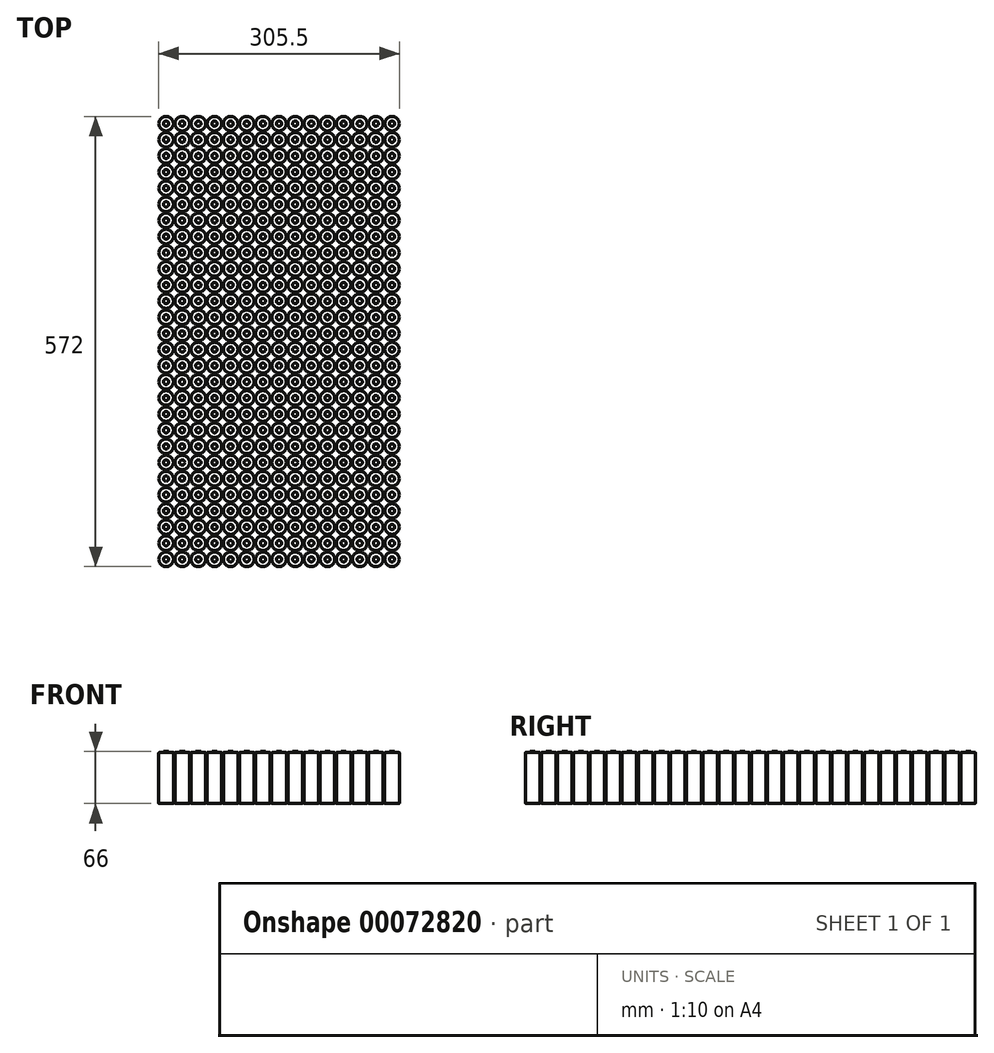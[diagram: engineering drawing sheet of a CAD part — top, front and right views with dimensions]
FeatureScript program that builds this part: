
annotation { "Feature Type Name" : "Feature", "Feature Type Description" : "" }
export const myFeature = defineFeature(function(context is Context, id is Id, definition is map)
    precondition{}
    {
        {
            var Q0;
            Q0=qCreatedBy(makeId("Top.planeOp"),FACE);
            var sketch = newSketch(context, id + "F0", { "sketchPlane" : qUnion([Q0])});
            skCircle(sketch, "E0", {"center": v(0, 0) * mm, "radius": 9.25 * mm});
            skSolve(sketch);
        }
        {
            var Q0;
            Q0 = qSketchRegion(id + "F0", true);
            extrude(context, id + "F1", {"entities" : qUnion([Q0]), "endBound" : BoundingType.SYMMETRIC, "depth" : 65 * mm});
        }
        {
            var Q0;
            Q0=makeQuery(id+"F1.opExtrude","CAP_FACE",FACE,{"disambiguationData":[OSD([sQuery(id+"F0.wireOp",EDGE,"E0")])],"isStart":false});
            var sketch = newSketch(context, id + "F2", { "sketchPlane" : qUnion([Q0])});
            skCircle(sketch, "E1", {"center": v(0, 0) * mm, "radius": 3.3 * mm});
            skSolve(sketch);
        }
        {
            var Q0;
            Q0 = qSketchRegion(id + "F2", true);
            extrude(context, id + "F3", {"entities" : qUnion([Q0]), "operationType" : NewBodyOperationType.ADD, "depth" : 1 * mm});
        }
        {
            var Q0;
            Q0=makeQuery(id+"F1.opExtrude","SWEPT_BODY",BODY,{"disambiguationData":[OSD([sQuery(id+"F0.wireOp",EDGE,"E0")])]});
            var Q1;
            Q1=qCreatedBy(makeId("Right.planeOp"),FACE);
            transform(context, id + "F4", {"entities" : qUnion([Q0]), "transformType" : TransformType.TRANSLATION_DISTANCE, "transformDirection" : qUnion([Q1]), "distance" : 20.5 * mm, "makeCopy" : true});
        }
        {
            var Q0;
            Q0=makeQuery(id+"F1.opExtrude","CAP_EDGE",EDGE,{"disambiguationData":[OSD([sQuery(id+"F0.wireOp",EDGE,"E0")])],"isStart":false});
            fillet(context, id + "F5", {"entities" : qUnion([Q0]), "radius" : 0.64 * mm, "tangentPropagation" : true, "allowEdgeOverflow" : false});
        }
        {
            var Q0;
            Q0=makeQuery(id+"F4.opPattern","COPY",EDGE,{"derivedFrom":makeQuery(id+"F1.opExtrude","CAP_EDGE",EDGE,{"disambiguationData":[OSD([sQuery(id+"F0.wireOp",EDGE,"E0")])],"isStart":false}),"instanceName":"1"});
            fillet(context, id + "F6", {"entities" : qUnion([Q0]), "radius" : 0.64 * mm, "tangentPropagation" : true, "allowEdgeOverflow" : false});
        }
        {
            var Q0;
            Q0=makeQuery(id+"F1.opExtrude","CAP_EDGE",EDGE,{"disambiguationData":[OSD([sQuery(id+"F0.wireOp",EDGE,"E0")])],"isStart":true});
            var Q1;
            Q1=makeQuery(id+"F1.opExtrude","SWEPT_FACE",FACE,{"disambiguationData":[OSD([sQuery(id+"F0.wireOp",EDGE,"E0")])]});
            fillet(context, id + "F7", {"entities" : qUnion([Q0, Q1]), "radius" : 0.64 * mm, "tangentPropagation" : true, "allowEdgeOverflow" : false});
        }
        {
            var Q0;
            Q0=makeQuery(id+"F4.opPattern","COPY",EDGE,{"derivedFrom":makeQuery(id+"F1.opExtrude","CAP_EDGE",EDGE,{"disambiguationData":[OSD([sQuery(id+"F0.wireOp",EDGE,"E0")])],"isStart":true}),"instanceName":"1"});
            fillet(context, id + "F8", {"entities" : qUnion([Q0]), "radius" : 0.64 * mm, "tangentPropagation" : true, "allowEdgeOverflow" : false});
        }
        {
            var Q0;
            Q0=makeQuery(id+"F1.opExtrude","SWEPT_BODY",BODY,{"disambiguationData":[OSD([sQuery(id+"F0.wireOp",EDGE,"E0")])]});
            var Q1;
            Q1=makeQuery(id+"F4.opPattern","COPY",BODY,{"derivedFrom":makeQuery(id+"F1.opExtrude","SWEPT_BODY",BODY,{"disambiguationData":[OSD([sQuery(id+"F0.wireOp",EDGE,"E0")])]}),"instanceName":"1"});
            var Q2;
            Q2=qCreatedBy(makeId("Right.planeOp"),FACE);
            transform(context, id + "F9", {"entities" : qUnion([Q0, Q1]), "transformType" : TransformType.TRANSLATION_DISTANCE, "transformDirection" : qUnion([Q2]), "distance" : 41 * mm, "oppositeDirection" : true, "makeCopy" : true});
        }
        {
            var Q0;
            Q0=makeQuery(id+"F1.opExtrude","SWEPT_BODY",BODY,{"disambiguationData":[OSD([sQuery(id+"F0.wireOp",EDGE,"E0")])]});
            var Q1;
            Q1=qCreatedBy(makeId("Right.planeOp"),FACE);
            transform(context, id + "F10", {"entities" : qUnion([Q0]), "transformType" : TransformType.TRANSLATION_DISTANCE, "transformDirection" : qUnion([Q1]), "distance" : 41 * mm, "makeCopy" : true});
        }
        {
            var Q0;
            Q0=makeQuery(id+"F4.opPattern","COPY",BODY,{"derivedFrom":makeQuery(id+"F1.opExtrude","SWEPT_BODY",BODY,{"disambiguationData":[OSD([sQuery(id+"F0.wireOp",EDGE,"E0")])]}),"instanceName":"1"});
            var Q1;
            Q1=makeQuery(id+"F1.opExtrude","SWEPT_BODY",BODY,{"disambiguationData":[OSD([sQuery(id+"F0.wireOp",EDGE,"E0")])]});
            var Q2;
            Q2=makeQuery(id+"F9.opPattern","COPY",BODY,{"derivedFrom":makeQuery(id+"F1.opExtrude","SWEPT_BODY",BODY,{"disambiguationData":[OSD([sQuery(id+"F0.wireOp",EDGE,"E0")])]}),"instanceName":"1"});
            var Q3;
            Q3=makeQuery(id+"F10.opPattern","COPY",BODY,{"derivedFrom":makeQuery(id+"F1.opExtrude","SWEPT_BODY",BODY,{"disambiguationData":[OSD([sQuery(id+"F0.wireOp",EDGE,"E0")])]}),"instanceName":"1"});
            var Q4;
            Q4=makeQuery(id+"F9.opPattern","COPY",BODY,{"derivedFrom":makeQuery(id+"F4.opPattern","COPY",BODY,{"derivedFrom":makeQuery(id+"F1.opExtrude","SWEPT_BODY",BODY,{"disambiguationData":[OSD([sQuery(id+"F0.wireOp",EDGE,"E0")])]}),"instanceName":"1"}),"instanceName":"1"});
            var Q5;
            Q5=qCreatedBy(makeId("Right.planeOp"),FACE);
            transform(context, id + "F11", {"entities" : qUnion([Q0, Q1, Q2, Q3, Q4]), "transformType" : TransformType.TRANSLATION_DISTANCE, "transformDirection" : qUnion([Q5]), "distance" : 102.5 * mm, "makeCopy" : true});
        }
        {
            var Q0;
            Q0=makeQuery(id+"F1.opExtrude","SWEPT_BODY",BODY,{"disambiguationData":[OSD([sQuery(id+"F0.wireOp",EDGE,"E0")])]});
            var Q1;
            Q1=makeQuery(id+"F4.opPattern","COPY",BODY,{"derivedFrom":makeQuery(id+"F1.opExtrude","SWEPT_BODY",BODY,{"disambiguationData":[OSD([sQuery(id+"F0.wireOp",EDGE,"E0")])]}),"instanceName":"1"});
            var Q2;
            Q2=makeQuery(id+"F9.opPattern","COPY",BODY,{"derivedFrom":makeQuery(id+"F1.opExtrude","SWEPT_BODY",BODY,{"disambiguationData":[OSD([sQuery(id+"F0.wireOp",EDGE,"E0")])]}),"instanceName":"1"});
            var Q3;
            Q3=makeQuery(id+"F10.opPattern","COPY",BODY,{"derivedFrom":makeQuery(id+"F1.opExtrude","SWEPT_BODY",BODY,{"disambiguationData":[OSD([sQuery(id+"F0.wireOp",EDGE,"E0")])]}),"instanceName":"1"});
            var Q4;
            Q4=makeQuery(id+"F11.opPattern","COPY",BODY,{"derivedFrom":makeQuery(id+"F9.opPattern","COPY",BODY,{"derivedFrom":makeQuery(id+"F1.opExtrude","SWEPT_BODY",BODY,{"disambiguationData":[OSD([sQuery(id+"F0.wireOp",EDGE,"E0")])]}),"instanceName":"1"}),"instanceName":"1"});
            var Q5;
            Q5=makeQuery(id+"F11.opPattern","COPY",BODY,{"derivedFrom":makeQuery(id+"F10.opPattern","COPY",BODY,{"derivedFrom":makeQuery(id+"F1.opExtrude","SWEPT_BODY",BODY,{"disambiguationData":[OSD([sQuery(id+"F0.wireOp",EDGE,"E0")])]}),"instanceName":"1"}),"instanceName":"1"});
            var Q6;
            Q6=makeQuery(id+"F11.opPattern","COPY",BODY,{"derivedFrom":makeQuery(id+"F9.opPattern","COPY",BODY,{"derivedFrom":makeQuery(id+"F4.opPattern","COPY",BODY,{"derivedFrom":makeQuery(id+"F1.opExtrude","SWEPT_BODY",BODY,{"disambiguationData":[OSD([sQuery(id+"F0.wireOp",EDGE,"E0")])]}),"instanceName":"1"}),"instanceName":"1"}),"instanceName":"1"});
            var Q7;
            Q7=makeQuery(id+"F11.opPattern","COPY",BODY,{"derivedFrom":makeQuery(id+"F4.opPattern","COPY",BODY,{"derivedFrom":makeQuery(id+"F1.opExtrude","SWEPT_BODY",BODY,{"disambiguationData":[OSD([sQuery(id+"F0.wireOp",EDGE,"E0")])]}),"instanceName":"1"}),"instanceName":"1"});
            var Q8;
            Q8=makeQuery(id+"F11.opPattern","COPY",BODY,{"derivedFrom":makeQuery(id+"F1.opExtrude","SWEPT_BODY",BODY,{"disambiguationData":[OSD([sQuery(id+"F0.wireOp",EDGE,"E0")])]}),"instanceName":"1"});
            var Q9;
            Q9=makeQuery(id+"F9.opPattern","COPY",BODY,{"derivedFrom":makeQuery(id+"F4.opPattern","COPY",BODY,{"derivedFrom":makeQuery(id+"F1.opExtrude","SWEPT_BODY",BODY,{"disambiguationData":[OSD([sQuery(id+"F0.wireOp",EDGE,"E0")])]}),"instanceName":"1"}),"instanceName":"1"});
            var Q10;
            Q10=qCreatedBy(makeId("Right.planeOp"),FACE);
            transform(context, id + "F12", {"entities" : qUnion([Q0, Q1, Q2, Q3, Q4, Q5, Q6, Q7, Q8, Q9]), "transformType" : TransformType.TRANSLATION_DISTANCE, "transformDirection" : qUnion([Q10]), "distance" : 205 * mm, "oppositeDirection" : true, "makeCopy" : true});
        }
        {
            var Q0;
            Q0=makeQuery(id+"F1.opExtrude","SWEPT_BODY",BODY,{"disambiguationData":[OSD([sQuery(id+"F0.wireOp",EDGE,"E0")])]});
            var Q1;
            Q1=makeQuery(id+"F4.opPattern","COPY",BODY,{"derivedFrom":makeQuery(id+"F1.opExtrude","SWEPT_BODY",BODY,{"disambiguationData":[OSD([sQuery(id+"F0.wireOp",EDGE,"E0")])]}),"instanceName":"1"});
            var Q2;
            Q2=makeQuery(id+"F9.opPattern","COPY",BODY,{"derivedFrom":makeQuery(id+"F4.opPattern","COPY",BODY,{"derivedFrom":makeQuery(id+"F1.opExtrude","SWEPT_BODY",BODY,{"disambiguationData":[OSD([sQuery(id+"F0.wireOp",EDGE,"E0")])]}),"instanceName":"1"}),"instanceName":"1"});
            var Q3;
            Q3=makeQuery(id+"F9.opPattern","COPY",BODY,{"derivedFrom":makeQuery(id+"F1.opExtrude","SWEPT_BODY",BODY,{"disambiguationData":[OSD([sQuery(id+"F0.wireOp",EDGE,"E0")])]}),"instanceName":"1"});
            var Q4;
            Q4=makeQuery(id+"F10.opPattern","COPY",BODY,{"derivedFrom":makeQuery(id+"F1.opExtrude","SWEPT_BODY",BODY,{"disambiguationData":[OSD([sQuery(id+"F0.wireOp",EDGE,"E0")])]}),"instanceName":"1"});
            var Q5;
            Q5=makeQuery(id+"F11.opPattern","COPY",BODY,{"derivedFrom":makeQuery(id+"F9.opPattern","COPY",BODY,{"derivedFrom":makeQuery(id+"F1.opExtrude","SWEPT_BODY",BODY,{"disambiguationData":[OSD([sQuery(id+"F0.wireOp",EDGE,"E0")])]}),"instanceName":"1"}),"instanceName":"1"});
            var Q6;
            Q6=makeQuery(id+"F11.opPattern","COPY",BODY,{"derivedFrom":makeQuery(id+"F10.opPattern","COPY",BODY,{"derivedFrom":makeQuery(id+"F1.opExtrude","SWEPT_BODY",BODY,{"disambiguationData":[OSD([sQuery(id+"F0.wireOp",EDGE,"E0")])]}),"instanceName":"1"}),"instanceName":"1"});
            var Q7;
            Q7=makeQuery(id+"F11.opPattern","COPY",BODY,{"derivedFrom":makeQuery(id+"F9.opPattern","COPY",BODY,{"derivedFrom":makeQuery(id+"F4.opPattern","COPY",BODY,{"derivedFrom":makeQuery(id+"F1.opExtrude","SWEPT_BODY",BODY,{"disambiguationData":[OSD([sQuery(id+"F0.wireOp",EDGE,"E0")])]}),"instanceName":"1"}),"instanceName":"1"}),"instanceName":"1"});
            var Q8;
            Q8=makeQuery(id+"F11.opPattern","COPY",BODY,{"derivedFrom":makeQuery(id+"F4.opPattern","COPY",BODY,{"derivedFrom":makeQuery(id+"F1.opExtrude","SWEPT_BODY",BODY,{"disambiguationData":[OSD([sQuery(id+"F0.wireOp",EDGE,"E0")])]}),"instanceName":"1"}),"instanceName":"1"});
            var Q9;
            Q9=makeQuery(id+"F11.opPattern","COPY",BODY,{"derivedFrom":makeQuery(id+"F1.opExtrude","SWEPT_BODY",BODY,{"disambiguationData":[OSD([sQuery(id+"F0.wireOp",EDGE,"E0")])]}),"instanceName":"1"});
            var Q10;
            Q10=makeQuery(id+"F12.opPattern","COPY",BODY,{"derivedFrom":makeQuery(id+"F11.opPattern","COPY",BODY,{"derivedFrom":makeQuery(id+"F4.opPattern","COPY",BODY,{"derivedFrom":makeQuery(id+"F1.opExtrude","SWEPT_BODY",BODY,{"disambiguationData":[OSD([sQuery(id+"F0.wireOp",EDGE,"E0")])]}),"instanceName":"1"}),"instanceName":"1"}),"instanceName":"1"});
            var Q11;
            Q11=makeQuery(id+"F12.opPattern","COPY",BODY,{"derivedFrom":makeQuery(id+"F11.opPattern","COPY",BODY,{"derivedFrom":makeQuery(id+"F1.opExtrude","SWEPT_BODY",BODY,{"disambiguationData":[OSD([sQuery(id+"F0.wireOp",EDGE,"E0")])]}),"instanceName":"1"}),"instanceName":"1"});
            var Q12;
            Q12=makeQuery(id+"F12.opPattern","COPY",BODY,{"derivedFrom":makeQuery(id+"F11.opPattern","COPY",BODY,{"derivedFrom":makeQuery(id+"F9.opPattern","COPY",BODY,{"derivedFrom":makeQuery(id+"F4.opPattern","COPY",BODY,{"derivedFrom":makeQuery(id+"F1.opExtrude","SWEPT_BODY",BODY,{"disambiguationData":[OSD([sQuery(id+"F0.wireOp",EDGE,"E0")])]}),"instanceName":"1"}),"instanceName":"1"}),"instanceName":"1"}),"instanceName":"1"});
            var Q13;
            Q13=makeQuery(id+"F12.opPattern","COPY",BODY,{"derivedFrom":makeQuery(id+"F10.opPattern","COPY",BODY,{"derivedFrom":makeQuery(id+"F1.opExtrude","SWEPT_BODY",BODY,{"disambiguationData":[OSD([sQuery(id+"F0.wireOp",EDGE,"E0")])]}),"instanceName":"1"}),"instanceName":"1"});
            var Q14;
            Q14=makeQuery(id+"F12.opPattern","COPY",BODY,{"derivedFrom":makeQuery(id+"F9.opPattern","COPY",BODY,{"derivedFrom":makeQuery(id+"F4.opPattern","COPY",BODY,{"derivedFrom":makeQuery(id+"F1.opExtrude","SWEPT_BODY",BODY,{"disambiguationData":[OSD([sQuery(id+"F0.wireOp",EDGE,"E0")])]}),"instanceName":"1"}),"instanceName":"1"}),"instanceName":"1"});
            var Q15;
            Q15=makeQuery(id+"F12.opPattern","COPY",BODY,{"derivedFrom":makeQuery(id+"F11.opPattern","COPY",BODY,{"derivedFrom":makeQuery(id+"F10.opPattern","COPY",BODY,{"derivedFrom":makeQuery(id+"F1.opExtrude","SWEPT_BODY",BODY,{"disambiguationData":[OSD([sQuery(id+"F0.wireOp",EDGE,"E0")])]}),"instanceName":"1"}),"instanceName":"1"}),"instanceName":"1"});
            var Q16;
            Q16=makeQuery(id+"F12.opPattern","COPY",BODY,{"derivedFrom":makeQuery(id+"F11.opPattern","COPY",BODY,{"derivedFrom":makeQuery(id+"F9.opPattern","COPY",BODY,{"derivedFrom":makeQuery(id+"F1.opExtrude","SWEPT_BODY",BODY,{"disambiguationData":[OSD([sQuery(id+"F0.wireOp",EDGE,"E0")])]}),"instanceName":"1"}),"instanceName":"1"}),"instanceName":"1"});
            var Q17;
            Q17=makeQuery(id+"F12.opPattern","COPY",BODY,{"derivedFrom":makeQuery(id+"F9.opPattern","COPY",BODY,{"derivedFrom":makeQuery(id+"F1.opExtrude","SWEPT_BODY",BODY,{"disambiguationData":[OSD([sQuery(id+"F0.wireOp",EDGE,"E0")])]}),"instanceName":"1"}),"instanceName":"1"});
            var Q18;
            Q18=makeQuery(id+"F12.opPattern","COPY",BODY,{"derivedFrom":makeQuery(id+"F4.opPattern","COPY",BODY,{"derivedFrom":makeQuery(id+"F1.opExtrude","SWEPT_BODY",BODY,{"disambiguationData":[OSD([sQuery(id+"F0.wireOp",EDGE,"E0")])]}),"instanceName":"1"}),"instanceName":"1"});
            var Q19;
            Q19=makeQuery(id+"F12.opPattern","COPY",BODY,{"derivedFrom":makeQuery(id+"F1.opExtrude","SWEPT_BODY",BODY,{"disambiguationData":[OSD([sQuery(id+"F0.wireOp",EDGE,"E0")])]}),"instanceName":"1"});
            var Q20;
            Q20=qCreatedBy(makeId("Right.planeOp"),FACE);
            transform(context, id + "F13", {"entities" : qUnion([Q0, Q1, Q2, Q3, Q4, Q5, Q6, Q7, Q8, Q9, Q10, Q11, Q12, Q13, Q14, Q15, Q16, Q17, Q18, Q19]), "transformType" : TransformType.TRANSLATION_DISTANCE, "transformDirection" : qUnion([Q20]), "distance" : 30.75 * mm, "oppositeDirection" : true, "makeCopy" : false});
        }
        {
            var Q0;
            Q0=makeQuery(id+"F4.opPattern","COPY",BODY,{"derivedFrom":makeQuery(id+"F1.opExtrude","SWEPT_BODY",BODY,{"disambiguationData":[OSD([sQuery(id+"F0.wireOp",EDGE,"E0")])]}),"instanceName":"1"});
            var Q1;
            Q1=makeQuery(id+"F10.opPattern","COPY",BODY,{"derivedFrom":makeQuery(id+"F1.opExtrude","SWEPT_BODY",BODY,{"disambiguationData":[OSD([sQuery(id+"F0.wireOp",EDGE,"E0")])]}),"instanceName":"1"});
            var Q2;
            Q2=makeQuery(id+"F11.opPattern","COPY",BODY,{"derivedFrom":makeQuery(id+"F9.opPattern","COPY",BODY,{"derivedFrom":makeQuery(id+"F1.opExtrude","SWEPT_BODY",BODY,{"disambiguationData":[OSD([sQuery(id+"F0.wireOp",EDGE,"E0")])]}),"instanceName":"1"}),"instanceName":"1"});
            var Q3;
            Q3=makeQuery(id+"F11.opPattern","COPY",BODY,{"derivedFrom":makeQuery(id+"F10.opPattern","COPY",BODY,{"derivedFrom":makeQuery(id+"F1.opExtrude","SWEPT_BODY",BODY,{"disambiguationData":[OSD([sQuery(id+"F0.wireOp",EDGE,"E0")])]}),"instanceName":"1"}),"instanceName":"1"});
            var Q4;
            Q4=makeQuery(id+"F11.opPattern","COPY",BODY,{"derivedFrom":makeQuery(id+"F9.opPattern","COPY",BODY,{"derivedFrom":makeQuery(id+"F4.opPattern","COPY",BODY,{"derivedFrom":makeQuery(id+"F1.opExtrude","SWEPT_BODY",BODY,{"disambiguationData":[OSD([sQuery(id+"F0.wireOp",EDGE,"E0")])]}),"instanceName":"1"}),"instanceName":"1"}),"instanceName":"1"});
            var Q5;
            Q5=makeQuery(id+"F11.opPattern","COPY",BODY,{"derivedFrom":makeQuery(id+"F4.opPattern","COPY",BODY,{"derivedFrom":makeQuery(id+"F1.opExtrude","SWEPT_BODY",BODY,{"disambiguationData":[OSD([sQuery(id+"F0.wireOp",EDGE,"E0")])]}),"instanceName":"1"}),"instanceName":"1"});
            var Q6;
            Q6=makeQuery(id+"F11.opPattern","COPY",BODY,{"derivedFrom":makeQuery(id+"F1.opExtrude","SWEPT_BODY",BODY,{"disambiguationData":[OSD([sQuery(id+"F0.wireOp",EDGE,"E0")])]}),"instanceName":"1"});
            var Q7;
            Q7=makeQuery(id+"F1.opExtrude","SWEPT_BODY",BODY,{"disambiguationData":[OSD([sQuery(id+"F0.wireOp",EDGE,"E0")])]});
            var Q8;
            Q8=qCreatedBy(makeId("Right.planeOp"),FACE);
            transform(context, id + "F14", {"entities" : qUnion([Q0, Q1, Q2, Q3, Q4, Q5, Q6, Q7]), "transformType" : TransformType.TRANSLATION_DISTANCE, "transformDirection" : qUnion([Q8]), "distance" : 164 * mm, "makeCopy" : true});
        }
        {
            var Q0;
            Q0=makeQuery(id+"F4.opPattern","COPY",BODY,{"derivedFrom":makeQuery(id+"F1.opExtrude","SWEPT_BODY",BODY,{"disambiguationData":[OSD([sQuery(id+"F0.wireOp",EDGE,"E0")])]}),"instanceName":"1"});
            var Q1;
            Q1=makeQuery(id+"F9.opPattern","COPY",BODY,{"derivedFrom":makeQuery(id+"F4.opPattern","COPY",BODY,{"derivedFrom":makeQuery(id+"F1.opExtrude","SWEPT_BODY",BODY,{"disambiguationData":[OSD([sQuery(id+"F0.wireOp",EDGE,"E0")])]}),"instanceName":"1"}),"instanceName":"1"});
            var Q2;
            Q2=makeQuery(id+"F9.opPattern","COPY",BODY,{"derivedFrom":makeQuery(id+"F1.opExtrude","SWEPT_BODY",BODY,{"disambiguationData":[OSD([sQuery(id+"F0.wireOp",EDGE,"E0")])]}),"instanceName":"1"});
            var Q3;
            Q3=makeQuery(id+"F10.opPattern","COPY",BODY,{"derivedFrom":makeQuery(id+"F1.opExtrude","SWEPT_BODY",BODY,{"disambiguationData":[OSD([sQuery(id+"F0.wireOp",EDGE,"E0")])]}),"instanceName":"1"});
            var Q4;
            Q4=makeQuery(id+"F11.opPattern","COPY",BODY,{"derivedFrom":makeQuery(id+"F9.opPattern","COPY",BODY,{"derivedFrom":makeQuery(id+"F1.opExtrude","SWEPT_BODY",BODY,{"disambiguationData":[OSD([sQuery(id+"F0.wireOp",EDGE,"E0")])]}),"instanceName":"1"}),"instanceName":"1"});
            var Q5;
            Q5=makeQuery(id+"F11.opPattern","COPY",BODY,{"derivedFrom":makeQuery(id+"F10.opPattern","COPY",BODY,{"derivedFrom":makeQuery(id+"F1.opExtrude","SWEPT_BODY",BODY,{"disambiguationData":[OSD([sQuery(id+"F0.wireOp",EDGE,"E0")])]}),"instanceName":"1"}),"instanceName":"1"});
            var Q6;
            Q6=makeQuery(id+"F11.opPattern","COPY",BODY,{"derivedFrom":makeQuery(id+"F9.opPattern","COPY",BODY,{"derivedFrom":makeQuery(id+"F4.opPattern","COPY",BODY,{"derivedFrom":makeQuery(id+"F1.opExtrude","SWEPT_BODY",BODY,{"disambiguationData":[OSD([sQuery(id+"F0.wireOp",EDGE,"E0")])]}),"instanceName":"1"}),"instanceName":"1"}),"instanceName":"1"});
            var Q7;
            Q7=makeQuery(id+"F11.opPattern","COPY",BODY,{"derivedFrom":makeQuery(id+"F4.opPattern","COPY",BODY,{"derivedFrom":makeQuery(id+"F1.opExtrude","SWEPT_BODY",BODY,{"disambiguationData":[OSD([sQuery(id+"F0.wireOp",EDGE,"E0")])]}),"instanceName":"1"}),"instanceName":"1"});
            var Q8;
            Q8=makeQuery(id+"F11.opPattern","COPY",BODY,{"derivedFrom":makeQuery(id+"F1.opExtrude","SWEPT_BODY",BODY,{"disambiguationData":[OSD([sQuery(id+"F0.wireOp",EDGE,"E0")])]}),"instanceName":"1"});
            var Q9;
            Q9=makeQuery(id+"F12.opPattern","COPY",BODY,{"derivedFrom":makeQuery(id+"F11.opPattern","COPY",BODY,{"derivedFrom":makeQuery(id+"F1.opExtrude","SWEPT_BODY",BODY,{"disambiguationData":[OSD([sQuery(id+"F0.wireOp",EDGE,"E0")])]}),"instanceName":"1"}),"instanceName":"1"});
            var Q10;
            Q10=makeQuery(id+"F12.opPattern","COPY",BODY,{"derivedFrom":makeQuery(id+"F11.opPattern","COPY",BODY,{"derivedFrom":makeQuery(id+"F9.opPattern","COPY",BODY,{"derivedFrom":makeQuery(id+"F4.opPattern","COPY",BODY,{"derivedFrom":makeQuery(id+"F1.opExtrude","SWEPT_BODY",BODY,{"disambiguationData":[OSD([sQuery(id+"F0.wireOp",EDGE,"E0")])]}),"instanceName":"1"}),"instanceName":"1"}),"instanceName":"1"}),"instanceName":"1"});
            var Q11;
            Q11=makeQuery(id+"F12.opPattern","COPY",BODY,{"derivedFrom":makeQuery(id+"F10.opPattern","COPY",BODY,{"derivedFrom":makeQuery(id+"F1.opExtrude","SWEPT_BODY",BODY,{"disambiguationData":[OSD([sQuery(id+"F0.wireOp",EDGE,"E0")])]}),"instanceName":"1"}),"instanceName":"1"});
            var Q12;
            Q12=makeQuery(id+"F12.opPattern","COPY",BODY,{"derivedFrom":makeQuery(id+"F9.opPattern","COPY",BODY,{"derivedFrom":makeQuery(id+"F4.opPattern","COPY",BODY,{"derivedFrom":makeQuery(id+"F1.opExtrude","SWEPT_BODY",BODY,{"disambiguationData":[OSD([sQuery(id+"F0.wireOp",EDGE,"E0")])]}),"instanceName":"1"}),"instanceName":"1"}),"instanceName":"1"});
            var Q13;
            Q13=makeQuery(id+"F12.opPattern","COPY",BODY,{"derivedFrom":makeQuery(id+"F11.opPattern","COPY",BODY,{"derivedFrom":makeQuery(id+"F4.opPattern","COPY",BODY,{"derivedFrom":makeQuery(id+"F1.opExtrude","SWEPT_BODY",BODY,{"disambiguationData":[OSD([sQuery(id+"F0.wireOp",EDGE,"E0")])]}),"instanceName":"1"}),"instanceName":"1"}),"instanceName":"1"});
            var Q14;
            Q14=makeQuery(id+"F12.opPattern","COPY",BODY,{"derivedFrom":makeQuery(id+"F11.opPattern","COPY",BODY,{"derivedFrom":makeQuery(id+"F10.opPattern","COPY",BODY,{"derivedFrom":makeQuery(id+"F1.opExtrude","SWEPT_BODY",BODY,{"disambiguationData":[OSD([sQuery(id+"F0.wireOp",EDGE,"E0")])]}),"instanceName":"1"}),"instanceName":"1"}),"instanceName":"1"});
            var Q15;
            Q15=makeQuery(id+"F12.opPattern","COPY",BODY,{"derivedFrom":makeQuery(id+"F9.opPattern","COPY",BODY,{"derivedFrom":makeQuery(id+"F1.opExtrude","SWEPT_BODY",BODY,{"disambiguationData":[OSD([sQuery(id+"F0.wireOp",EDGE,"E0")])]}),"instanceName":"1"}),"instanceName":"1"});
            var Q16;
            Q16=makeQuery(id+"F12.opPattern","COPY",BODY,{"derivedFrom":makeQuery(id+"F11.opPattern","COPY",BODY,{"derivedFrom":makeQuery(id+"F9.opPattern","COPY",BODY,{"derivedFrom":makeQuery(id+"F1.opExtrude","SWEPT_BODY",BODY,{"disambiguationData":[OSD([sQuery(id+"F0.wireOp",EDGE,"E0")])]}),"instanceName":"1"}),"instanceName":"1"}),"instanceName":"1"});
            var Q17;
            Q17=makeQuery(id+"F12.opPattern","COPY",BODY,{"derivedFrom":makeQuery(id+"F4.opPattern","COPY",BODY,{"derivedFrom":makeQuery(id+"F1.opExtrude","SWEPT_BODY",BODY,{"disambiguationData":[OSD([sQuery(id+"F0.wireOp",EDGE,"E0")])]}),"instanceName":"1"}),"instanceName":"1"});
            var Q18;
            Q18=makeQuery(id+"F12.opPattern","COPY",BODY,{"derivedFrom":makeQuery(id+"F1.opExtrude","SWEPT_BODY",BODY,{"disambiguationData":[OSD([sQuery(id+"F0.wireOp",EDGE,"E0")])]}),"instanceName":"1"});
            var Q19;
            Q19=makeQuery(id+"F14.opPattern","COPY",BODY,{"derivedFrom":makeQuery(id+"F11.opPattern","COPY",BODY,{"derivedFrom":makeQuery(id+"F10.opPattern","COPY",BODY,{"derivedFrom":makeQuery(id+"F1.opExtrude","SWEPT_BODY",BODY,{"disambiguationData":[OSD([sQuery(id+"F0.wireOp",EDGE,"E0")])]}),"instanceName":"1"}),"instanceName":"1"}),"instanceName":"1"});
            var Q20;
            Q20=makeQuery(id+"F14.opPattern","COPY",BODY,{"derivedFrom":makeQuery(id+"F11.opPattern","COPY",BODY,{"derivedFrom":makeQuery(id+"F9.opPattern","COPY",BODY,{"derivedFrom":makeQuery(id+"F4.opPattern","COPY",BODY,{"derivedFrom":makeQuery(id+"F1.opExtrude","SWEPT_BODY",BODY,{"disambiguationData":[OSD([sQuery(id+"F0.wireOp",EDGE,"E0")])]}),"instanceName":"1"}),"instanceName":"1"}),"instanceName":"1"}),"instanceName":"1"});
            var Q21;
            Q21=makeQuery(id+"F14.opPattern","COPY",BODY,{"derivedFrom":makeQuery(id+"F11.opPattern","COPY",BODY,{"derivedFrom":makeQuery(id+"F1.opExtrude","SWEPT_BODY",BODY,{"disambiguationData":[OSD([sQuery(id+"F0.wireOp",EDGE,"E0")])]}),"instanceName":"1"}),"instanceName":"1"});
            var Q22;
            Q22=makeQuery(id+"F14.opPattern","COPY",BODY,{"derivedFrom":makeQuery(id+"F11.opPattern","COPY",BODY,{"derivedFrom":makeQuery(id+"F9.opPattern","COPY",BODY,{"derivedFrom":makeQuery(id+"F1.opExtrude","SWEPT_BODY",BODY,{"disambiguationData":[OSD([sQuery(id+"F0.wireOp",EDGE,"E0")])]}),"instanceName":"1"}),"instanceName":"1"}),"instanceName":"1"});
            var Q23;
            Q23=makeQuery(id+"F14.opPattern","COPY",BODY,{"derivedFrom":makeQuery(id+"F11.opPattern","COPY",BODY,{"derivedFrom":makeQuery(id+"F4.opPattern","COPY",BODY,{"derivedFrom":makeQuery(id+"F1.opExtrude","SWEPT_BODY",BODY,{"disambiguationData":[OSD([sQuery(id+"F0.wireOp",EDGE,"E0")])]}),"instanceName":"1"}),"instanceName":"1"}),"instanceName":"1"});
            var Q24;
            Q24=makeQuery(id+"F14.opPattern","COPY",BODY,{"derivedFrom":makeQuery(id+"F10.opPattern","COPY",BODY,{"derivedFrom":makeQuery(id+"F1.opExtrude","SWEPT_BODY",BODY,{"disambiguationData":[OSD([sQuery(id+"F0.wireOp",EDGE,"E0")])]}),"instanceName":"1"}),"instanceName":"1"});
            var Q25;
            Q25=makeQuery(id+"F14.opPattern","COPY",BODY,{"derivedFrom":makeQuery(id+"F4.opPattern","COPY",BODY,{"derivedFrom":makeQuery(id+"F1.opExtrude","SWEPT_BODY",BODY,{"disambiguationData":[OSD([sQuery(id+"F0.wireOp",EDGE,"E0")])]}),"instanceName":"1"}),"instanceName":"1"});
            var Q26;
            Q26=makeQuery(id+"F14.opPattern","COPY",BODY,{"derivedFrom":makeQuery(id+"F1.opExtrude","SWEPT_BODY",BODY,{"disambiguationData":[OSD([sQuery(id+"F0.wireOp",EDGE,"E0")])]}),"instanceName":"1"});
            var Q27;
            Q27=makeQuery(id+"F1.opExtrude","SWEPT_BODY",BODY,{"disambiguationData":[OSD([sQuery(id+"F0.wireOp",EDGE,"E0")])]});
            var Q28;
            Q28=qCreatedBy(makeId("Front.planeOp"),FACE);
            transform(context, id + "F15", {"entities" : qUnion([Q0, Q1, Q2, Q3, Q4, Q5, Q6, Q7, Q8, Q9, Q10, Q11, Q12, Q13, Q14, Q15, Q16, Q17, Q18, Q19, Q20, Q21, Q22, Q23, Q24, Q25, Q26, Q27]), "transformType" : TransformType.TRANSLATION_DISTANCE, "transformDirection" : qUnion([Q28]), "distance" : 20.5 * mm, "makeCopy" : true});
        }
        {
            var Q0;
            Q0=makeQuery(id+"F4.opPattern","COPY",BODY,{"derivedFrom":makeQuery(id+"F1.opExtrude","SWEPT_BODY",BODY,{"disambiguationData":[OSD([sQuery(id+"F0.wireOp",EDGE,"E0")])]}),"instanceName":"1"});
            var Q1;
            Q1=makeQuery(id+"F9.opPattern","COPY",BODY,{"derivedFrom":makeQuery(id+"F4.opPattern","COPY",BODY,{"derivedFrom":makeQuery(id+"F1.opExtrude","SWEPT_BODY",BODY,{"disambiguationData":[OSD([sQuery(id+"F0.wireOp",EDGE,"E0")])]}),"instanceName":"1"}),"instanceName":"1"});
            var Q2;
            Q2=makeQuery(id+"F9.opPattern","COPY",BODY,{"derivedFrom":makeQuery(id+"F1.opExtrude","SWEPT_BODY",BODY,{"disambiguationData":[OSD([sQuery(id+"F0.wireOp",EDGE,"E0")])]}),"instanceName":"1"});
            var Q3;
            Q3=makeQuery(id+"F10.opPattern","COPY",BODY,{"derivedFrom":makeQuery(id+"F1.opExtrude","SWEPT_BODY",BODY,{"disambiguationData":[OSD([sQuery(id+"F0.wireOp",EDGE,"E0")])]}),"instanceName":"1"});
            var Q4;
            Q4=makeQuery(id+"F11.opPattern","COPY",BODY,{"derivedFrom":makeQuery(id+"F9.opPattern","COPY",BODY,{"derivedFrom":makeQuery(id+"F1.opExtrude","SWEPT_BODY",BODY,{"disambiguationData":[OSD([sQuery(id+"F0.wireOp",EDGE,"E0")])]}),"instanceName":"1"}),"instanceName":"1"});
            var Q5;
            Q5=makeQuery(id+"F11.opPattern","COPY",BODY,{"derivedFrom":makeQuery(id+"F10.opPattern","COPY",BODY,{"derivedFrom":makeQuery(id+"F1.opExtrude","SWEPT_BODY",BODY,{"disambiguationData":[OSD([sQuery(id+"F0.wireOp",EDGE,"E0")])]}),"instanceName":"1"}),"instanceName":"1"});
            var Q6;
            Q6=makeQuery(id+"F11.opPattern","COPY",BODY,{"derivedFrom":makeQuery(id+"F4.opPattern","COPY",BODY,{"derivedFrom":makeQuery(id+"F1.opExtrude","SWEPT_BODY",BODY,{"disambiguationData":[OSD([sQuery(id+"F0.wireOp",EDGE,"E0")])]}),"instanceName":"1"}),"instanceName":"1"});
            var Q7;
            Q7=makeQuery(id+"F11.opPattern","COPY",BODY,{"derivedFrom":makeQuery(id+"F9.opPattern","COPY",BODY,{"derivedFrom":makeQuery(id+"F4.opPattern","COPY",BODY,{"derivedFrom":makeQuery(id+"F1.opExtrude","SWEPT_BODY",BODY,{"disambiguationData":[OSD([sQuery(id+"F0.wireOp",EDGE,"E0")])]}),"instanceName":"1"}),"instanceName":"1"}),"instanceName":"1"});
            var Q8;
            Q8=makeQuery(id+"F11.opPattern","COPY",BODY,{"derivedFrom":makeQuery(id+"F1.opExtrude","SWEPT_BODY",BODY,{"disambiguationData":[OSD([sQuery(id+"F0.wireOp",EDGE,"E0")])]}),"instanceName":"1"});
            var Q9;
            Q9=makeQuery(id+"F12.opPattern","COPY",BODY,{"derivedFrom":makeQuery(id+"F9.opPattern","COPY",BODY,{"derivedFrom":makeQuery(id+"F1.opExtrude","SWEPT_BODY",BODY,{"disambiguationData":[OSD([sQuery(id+"F0.wireOp",EDGE,"E0")])]}),"instanceName":"1"}),"instanceName":"1"});
            var Q10;
            Q10=makeQuery(id+"F12.opPattern","COPY",BODY,{"derivedFrom":makeQuery(id+"F11.opPattern","COPY",BODY,{"derivedFrom":makeQuery(id+"F1.opExtrude","SWEPT_BODY",BODY,{"disambiguationData":[OSD([sQuery(id+"F0.wireOp",EDGE,"E0")])]}),"instanceName":"1"}),"instanceName":"1"});
            var Q11;
            Q11=makeQuery(id+"F12.opPattern","COPY",BODY,{"derivedFrom":makeQuery(id+"F11.opPattern","COPY",BODY,{"derivedFrom":makeQuery(id+"F9.opPattern","COPY",BODY,{"derivedFrom":makeQuery(id+"F4.opPattern","COPY",BODY,{"derivedFrom":makeQuery(id+"F1.opExtrude","SWEPT_BODY",BODY,{"disambiguationData":[OSD([sQuery(id+"F0.wireOp",EDGE,"E0")])]}),"instanceName":"1"}),"instanceName":"1"}),"instanceName":"1"}),"instanceName":"1"});
            var Q12;
            Q12=makeQuery(id+"F12.opPattern","COPY",BODY,{"derivedFrom":makeQuery(id+"F10.opPattern","COPY",BODY,{"derivedFrom":makeQuery(id+"F1.opExtrude","SWEPT_BODY",BODY,{"disambiguationData":[OSD([sQuery(id+"F0.wireOp",EDGE,"E0")])]}),"instanceName":"1"}),"instanceName":"1"});
            var Q13;
            Q13=makeQuery(id+"F12.opPattern","COPY",BODY,{"derivedFrom":makeQuery(id+"F9.opPattern","COPY",BODY,{"derivedFrom":makeQuery(id+"F4.opPattern","COPY",BODY,{"derivedFrom":makeQuery(id+"F1.opExtrude","SWEPT_BODY",BODY,{"disambiguationData":[OSD([sQuery(id+"F0.wireOp",EDGE,"E0")])]}),"instanceName":"1"}),"instanceName":"1"}),"instanceName":"1"});
            var Q14;
            Q14=makeQuery(id+"F12.opPattern","COPY",BODY,{"derivedFrom":makeQuery(id+"F11.opPattern","COPY",BODY,{"derivedFrom":makeQuery(id+"F10.opPattern","COPY",BODY,{"derivedFrom":makeQuery(id+"F1.opExtrude","SWEPT_BODY",BODY,{"disambiguationData":[OSD([sQuery(id+"F0.wireOp",EDGE,"E0")])]}),"instanceName":"1"}),"instanceName":"1"}),"instanceName":"1"});
            var Q15;
            Q15=makeQuery(id+"F12.opPattern","COPY",BODY,{"derivedFrom":makeQuery(id+"F11.opPattern","COPY",BODY,{"derivedFrom":makeQuery(id+"F4.opPattern","COPY",BODY,{"derivedFrom":makeQuery(id+"F1.opExtrude","SWEPT_BODY",BODY,{"disambiguationData":[OSD([sQuery(id+"F0.wireOp",EDGE,"E0")])]}),"instanceName":"1"}),"instanceName":"1"}),"instanceName":"1"});
            var Q16;
            Q16=makeQuery(id+"F12.opPattern","COPY",BODY,{"derivedFrom":makeQuery(id+"F4.opPattern","COPY",BODY,{"derivedFrom":makeQuery(id+"F1.opExtrude","SWEPT_BODY",BODY,{"disambiguationData":[OSD([sQuery(id+"F0.wireOp",EDGE,"E0")])]}),"instanceName":"1"}),"instanceName":"1"});
            var Q17;
            Q17=makeQuery(id+"F12.opPattern","COPY",BODY,{"derivedFrom":makeQuery(id+"F1.opExtrude","SWEPT_BODY",BODY,{"disambiguationData":[OSD([sQuery(id+"F0.wireOp",EDGE,"E0")])]}),"instanceName":"1"});
            var Q18;
            Q18=makeQuery(id+"F12.opPattern","COPY",BODY,{"derivedFrom":makeQuery(id+"F11.opPattern","COPY",BODY,{"derivedFrom":makeQuery(id+"F9.opPattern","COPY",BODY,{"derivedFrom":makeQuery(id+"F1.opExtrude","SWEPT_BODY",BODY,{"disambiguationData":[OSD([sQuery(id+"F0.wireOp",EDGE,"E0")])]}),"instanceName":"1"}),"instanceName":"1"}),"instanceName":"1"});
            var Q19;
            Q19=makeQuery(id+"F14.opPattern","COPY",BODY,{"derivedFrom":makeQuery(id+"F11.opPattern","COPY",BODY,{"derivedFrom":makeQuery(id+"F10.opPattern","COPY",BODY,{"derivedFrom":makeQuery(id+"F1.opExtrude","SWEPT_BODY",BODY,{"disambiguationData":[OSD([sQuery(id+"F0.wireOp",EDGE,"E0")])]}),"instanceName":"1"}),"instanceName":"1"}),"instanceName":"1"});
            var Q20;
            Q20=makeQuery(id+"F14.opPattern","COPY",BODY,{"derivedFrom":makeQuery(id+"F11.opPattern","COPY",BODY,{"derivedFrom":makeQuery(id+"F1.opExtrude","SWEPT_BODY",BODY,{"disambiguationData":[OSD([sQuery(id+"F0.wireOp",EDGE,"E0")])]}),"instanceName":"1"}),"instanceName":"1"});
            var Q21;
            Q21=makeQuery(id+"F14.opPattern","COPY",BODY,{"derivedFrom":makeQuery(id+"F11.opPattern","COPY",BODY,{"derivedFrom":makeQuery(id+"F9.opPattern","COPY",BODY,{"derivedFrom":makeQuery(id+"F4.opPattern","COPY",BODY,{"derivedFrom":makeQuery(id+"F1.opExtrude","SWEPT_BODY",BODY,{"disambiguationData":[OSD([sQuery(id+"F0.wireOp",EDGE,"E0")])]}),"instanceName":"1"}),"instanceName":"1"}),"instanceName":"1"}),"instanceName":"1"});
            var Q22;
            Q22=makeQuery(id+"F14.opPattern","COPY",BODY,{"derivedFrom":makeQuery(id+"F11.opPattern","COPY",BODY,{"derivedFrom":makeQuery(id+"F9.opPattern","COPY",BODY,{"derivedFrom":makeQuery(id+"F1.opExtrude","SWEPT_BODY",BODY,{"disambiguationData":[OSD([sQuery(id+"F0.wireOp",EDGE,"E0")])]}),"instanceName":"1"}),"instanceName":"1"}),"instanceName":"1"});
            var Q23;
            Q23=makeQuery(id+"F14.opPattern","COPY",BODY,{"derivedFrom":makeQuery(id+"F11.opPattern","COPY",BODY,{"derivedFrom":makeQuery(id+"F4.opPattern","COPY",BODY,{"derivedFrom":makeQuery(id+"F1.opExtrude","SWEPT_BODY",BODY,{"disambiguationData":[OSD([sQuery(id+"F0.wireOp",EDGE,"E0")])]}),"instanceName":"1"}),"instanceName":"1"}),"instanceName":"1"});
            var Q24;
            Q24=makeQuery(id+"F14.opPattern","COPY",BODY,{"derivedFrom":makeQuery(id+"F10.opPattern","COPY",BODY,{"derivedFrom":makeQuery(id+"F1.opExtrude","SWEPT_BODY",BODY,{"disambiguationData":[OSD([sQuery(id+"F0.wireOp",EDGE,"E0")])]}),"instanceName":"1"}),"instanceName":"1"});
            var Q25;
            Q25=makeQuery(id+"F14.opPattern","COPY",BODY,{"derivedFrom":makeQuery(id+"F4.opPattern","COPY",BODY,{"derivedFrom":makeQuery(id+"F1.opExtrude","SWEPT_BODY",BODY,{"disambiguationData":[OSD([sQuery(id+"F0.wireOp",EDGE,"E0")])]}),"instanceName":"1"}),"instanceName":"1"});
            var Q26;
            Q26=makeQuery(id+"F14.opPattern","COPY",BODY,{"derivedFrom":makeQuery(id+"F1.opExtrude","SWEPT_BODY",BODY,{"disambiguationData":[OSD([sQuery(id+"F0.wireOp",EDGE,"E0")])]}),"instanceName":"1"});
            var Q27;
            Q27=makeQuery(id+"F15.opPattern","COPY",BODY,{"derivedFrom":makeQuery(id+"F12.opPattern","COPY",BODY,{"derivedFrom":makeQuery(id+"F11.opPattern","COPY",BODY,{"derivedFrom":makeQuery(id+"F9.opPattern","COPY",BODY,{"derivedFrom":makeQuery(id+"F4.opPattern","COPY",BODY,{"derivedFrom":makeQuery(id+"F1.opExtrude","SWEPT_BODY",BODY,{"disambiguationData":[OSD([sQuery(id+"F0.wireOp",EDGE,"E0")])]}),"instanceName":"1"}),"instanceName":"1"}),"instanceName":"1"}),"instanceName":"1"}),"instanceName":"1"});
            var Q28;
            Q28=makeQuery(id+"F15.opPattern","COPY",BODY,{"derivedFrom":makeQuery(id+"F14.opPattern","COPY",BODY,{"derivedFrom":makeQuery(id+"F10.opPattern","COPY",BODY,{"derivedFrom":makeQuery(id+"F1.opExtrude","SWEPT_BODY",BODY,{"disambiguationData":[OSD([sQuery(id+"F0.wireOp",EDGE,"E0")])]}),"instanceName":"1"}),"instanceName":"1"}),"instanceName":"1"});
            var Q29;
            Q29=makeQuery(id+"F15.opPattern","COPY",BODY,{"derivedFrom":makeQuery(id+"F12.opPattern","COPY",BODY,{"derivedFrom":makeQuery(id+"F11.opPattern","COPY",BODY,{"derivedFrom":makeQuery(id+"F1.opExtrude","SWEPT_BODY",BODY,{"disambiguationData":[OSD([sQuery(id+"F0.wireOp",EDGE,"E0")])]}),"instanceName":"1"}),"instanceName":"1"}),"instanceName":"1"});
            var Q30;
            Q30=makeQuery(id+"F15.opPattern","COPY",BODY,{"derivedFrom":makeQuery(id+"F14.opPattern","COPY",BODY,{"derivedFrom":makeQuery(id+"F11.opPattern","COPY",BODY,{"derivedFrom":makeQuery(id+"F1.opExtrude","SWEPT_BODY",BODY,{"disambiguationData":[OSD([sQuery(id+"F0.wireOp",EDGE,"E0")])]}),"instanceName":"1"}),"instanceName":"1"}),"instanceName":"1"});
            var Q31;
            Q31=makeQuery(id+"F15.opPattern","COPY",BODY,{"derivedFrom":makeQuery(id+"F12.opPattern","COPY",BODY,{"derivedFrom":makeQuery(id+"F1.opExtrude","SWEPT_BODY",BODY,{"disambiguationData":[OSD([sQuery(id+"F0.wireOp",EDGE,"E0")])]}),"instanceName":"1"}),"instanceName":"1"});
            var Q32;
            Q32=makeQuery(id+"F15.opPattern","COPY",BODY,{"derivedFrom":makeQuery(id+"F12.opPattern","COPY",BODY,{"derivedFrom":makeQuery(id+"F9.opPattern","COPY",BODY,{"derivedFrom":makeQuery(id+"F4.opPattern","COPY",BODY,{"derivedFrom":makeQuery(id+"F1.opExtrude","SWEPT_BODY",BODY,{"disambiguationData":[OSD([sQuery(id+"F0.wireOp",EDGE,"E0")])]}),"instanceName":"1"}),"instanceName":"1"}),"instanceName":"1"}),"instanceName":"1"});
            var Q33;
            Q33=makeQuery(id+"F15.opPattern","COPY",BODY,{"derivedFrom":makeQuery(id+"F14.opPattern","COPY",BODY,{"derivedFrom":makeQuery(id+"F11.opPattern","COPY",BODY,{"derivedFrom":makeQuery(id+"F9.opPattern","COPY",BODY,{"derivedFrom":makeQuery(id+"F4.opPattern","COPY",BODY,{"derivedFrom":makeQuery(id+"F1.opExtrude","SWEPT_BODY",BODY,{"disambiguationData":[OSD([sQuery(id+"F0.wireOp",EDGE,"E0")])]}),"instanceName":"1"}),"instanceName":"1"}),"instanceName":"1"}),"instanceName":"1"}),"instanceName":"1"});
            var Q34;
            Q34=makeQuery(id+"F15.opPattern","COPY",BODY,{"derivedFrom":makeQuery(id+"F11.opPattern","COPY",BODY,{"derivedFrom":makeQuery(id+"F10.opPattern","COPY",BODY,{"derivedFrom":makeQuery(id+"F1.opExtrude","SWEPT_BODY",BODY,{"disambiguationData":[OSD([sQuery(id+"F0.wireOp",EDGE,"E0")])]}),"instanceName":"1"}),"instanceName":"1"}),"instanceName":"1"});
            var Q35;
            Q35=makeQuery(id+"F15.opPattern","COPY",BODY,{"derivedFrom":makeQuery(id+"F11.opPattern","COPY",BODY,{"derivedFrom":makeQuery(id+"F9.opPattern","COPY",BODY,{"derivedFrom":makeQuery(id+"F4.opPattern","COPY",BODY,{"derivedFrom":makeQuery(id+"F1.opExtrude","SWEPT_BODY",BODY,{"disambiguationData":[OSD([sQuery(id+"F0.wireOp",EDGE,"E0")])]}),"instanceName":"1"}),"instanceName":"1"}),"instanceName":"1"}),"instanceName":"1"});
            var Q36;
            Q36=makeQuery(id+"F15.opPattern","COPY",BODY,{"derivedFrom":makeQuery(id+"F11.opPattern","COPY",BODY,{"derivedFrom":makeQuery(id+"F1.opExtrude","SWEPT_BODY",BODY,{"disambiguationData":[OSD([sQuery(id+"F0.wireOp",EDGE,"E0")])]}),"instanceName":"1"}),"instanceName":"1"});
            var Q37;
            Q37=makeQuery(id+"F15.opPattern","COPY",BODY,{"derivedFrom":makeQuery(id+"F9.opPattern","COPY",BODY,{"derivedFrom":makeQuery(id+"F1.opExtrude","SWEPT_BODY",BODY,{"disambiguationData":[OSD([sQuery(id+"F0.wireOp",EDGE,"E0")])]}),"instanceName":"1"}),"instanceName":"1"});
            var Q38;
            Q38=makeQuery(id+"F15.opPattern","COPY",BODY,{"derivedFrom":makeQuery(id+"F14.opPattern","COPY",BODY,{"derivedFrom":makeQuery(id+"F11.opPattern","COPY",BODY,{"derivedFrom":makeQuery(id+"F9.opPattern","COPY",BODY,{"derivedFrom":makeQuery(id+"F1.opExtrude","SWEPT_BODY",BODY,{"disambiguationData":[OSD([sQuery(id+"F0.wireOp",EDGE,"E0")])]}),"instanceName":"1"}),"instanceName":"1"}),"instanceName":"1"}),"instanceName":"1"});
            var Q39;
            Q39=makeQuery(id+"F15.opPattern","COPY",BODY,{"derivedFrom":makeQuery(id+"F14.opPattern","COPY",BODY,{"derivedFrom":makeQuery(id+"F4.opPattern","COPY",BODY,{"derivedFrom":makeQuery(id+"F1.opExtrude","SWEPT_BODY",BODY,{"disambiguationData":[OSD([sQuery(id+"F0.wireOp",EDGE,"E0")])]}),"instanceName":"1"}),"instanceName":"1"}),"instanceName":"1"});
            var Q40;
            Q40=makeQuery(id+"F15.opPattern","COPY",BODY,{"derivedFrom":makeQuery(id+"F12.opPattern","COPY",BODY,{"derivedFrom":makeQuery(id+"F10.opPattern","COPY",BODY,{"derivedFrom":makeQuery(id+"F1.opExtrude","SWEPT_BODY",BODY,{"disambiguationData":[OSD([sQuery(id+"F0.wireOp",EDGE,"E0")])]}),"instanceName":"1"}),"instanceName":"1"}),"instanceName":"1"});
            var Q41;
            Q41=makeQuery(id+"F15.opPattern","COPY",BODY,{"derivedFrom":makeQuery(id+"F12.opPattern","COPY",BODY,{"derivedFrom":makeQuery(id+"F4.opPattern","COPY",BODY,{"derivedFrom":makeQuery(id+"F1.opExtrude","SWEPT_BODY",BODY,{"disambiguationData":[OSD([sQuery(id+"F0.wireOp",EDGE,"E0")])]}),"instanceName":"1"}),"instanceName":"1"}),"instanceName":"1"});
            var Q42;
            Q42=makeQuery(id+"F15.opPattern","COPY",BODY,{"derivedFrom":makeQuery(id+"F14.opPattern","COPY",BODY,{"derivedFrom":makeQuery(id+"F11.opPattern","COPY",BODY,{"derivedFrom":makeQuery(id+"F10.opPattern","COPY",BODY,{"derivedFrom":makeQuery(id+"F1.opExtrude","SWEPT_BODY",BODY,{"disambiguationData":[OSD([sQuery(id+"F0.wireOp",EDGE,"E0")])]}),"instanceName":"1"}),"instanceName":"1"}),"instanceName":"1"}),"instanceName":"1"});
            var Q43;
            Q43=makeQuery(id+"F15.opPattern","COPY",BODY,{"derivedFrom":makeQuery(id+"F14.opPattern","COPY",BODY,{"derivedFrom":makeQuery(id+"F11.opPattern","COPY",BODY,{"derivedFrom":makeQuery(id+"F4.opPattern","COPY",BODY,{"derivedFrom":makeQuery(id+"F1.opExtrude","SWEPT_BODY",BODY,{"disambiguationData":[OSD([sQuery(id+"F0.wireOp",EDGE,"E0")])]}),"instanceName":"1"}),"instanceName":"1"}),"instanceName":"1"}),"instanceName":"1"});
            var Q44;
            Q44=makeQuery(id+"F15.opPattern","COPY",BODY,{"derivedFrom":makeQuery(id+"F11.opPattern","COPY",BODY,{"derivedFrom":makeQuery(id+"F4.opPattern","COPY",BODY,{"derivedFrom":makeQuery(id+"F1.opExtrude","SWEPT_BODY",BODY,{"disambiguationData":[OSD([sQuery(id+"F0.wireOp",EDGE,"E0")])]}),"instanceName":"1"}),"instanceName":"1"}),"instanceName":"1"});
            var Q45;
            Q45=makeQuery(id+"F15.opPattern","COPY",BODY,{"derivedFrom":makeQuery(id+"F10.opPattern","COPY",BODY,{"derivedFrom":makeQuery(id+"F1.opExtrude","SWEPT_BODY",BODY,{"disambiguationData":[OSD([sQuery(id+"F0.wireOp",EDGE,"E0")])]}),"instanceName":"1"}),"instanceName":"1"});
            var Q46;
            Q46=makeQuery(id+"F15.opPattern","COPY",BODY,{"derivedFrom":makeQuery(id+"F9.opPattern","COPY",BODY,{"derivedFrom":makeQuery(id+"F4.opPattern","COPY",BODY,{"derivedFrom":makeQuery(id+"F1.opExtrude","SWEPT_BODY",BODY,{"disambiguationData":[OSD([sQuery(id+"F0.wireOp",EDGE,"E0")])]}),"instanceName":"1"}),"instanceName":"1"}),"instanceName":"1"});
            var Q47;
            Q47=makeQuery(id+"F15.opPattern","COPY",BODY,{"derivedFrom":makeQuery(id+"F12.opPattern","COPY",BODY,{"derivedFrom":makeQuery(id+"F11.opPattern","COPY",BODY,{"derivedFrom":makeQuery(id+"F10.opPattern","COPY",BODY,{"derivedFrom":makeQuery(id+"F1.opExtrude","SWEPT_BODY",BODY,{"disambiguationData":[OSD([sQuery(id+"F0.wireOp",EDGE,"E0")])]}),"instanceName":"1"}),"instanceName":"1"}),"instanceName":"1"}),"instanceName":"1"});
            var Q48;
            Q48=makeQuery(id+"F15.opPattern","COPY",BODY,{"derivedFrom":makeQuery(id+"F12.opPattern","COPY",BODY,{"derivedFrom":makeQuery(id+"F11.opPattern","COPY",BODY,{"derivedFrom":makeQuery(id+"F9.opPattern","COPY",BODY,{"derivedFrom":makeQuery(id+"F1.opExtrude","SWEPT_BODY",BODY,{"disambiguationData":[OSD([sQuery(id+"F0.wireOp",EDGE,"E0")])]}),"instanceName":"1"}),"instanceName":"1"}),"instanceName":"1"}),"instanceName":"1"});
            var Q49;
            Q49=makeQuery(id+"F15.opPattern","COPY",BODY,{"derivedFrom":makeQuery(id+"F12.opPattern","COPY",BODY,{"derivedFrom":makeQuery(id+"F11.opPattern","COPY",BODY,{"derivedFrom":makeQuery(id+"F4.opPattern","COPY",BODY,{"derivedFrom":makeQuery(id+"F1.opExtrude","SWEPT_BODY",BODY,{"disambiguationData":[OSD([sQuery(id+"F0.wireOp",EDGE,"E0")])]}),"instanceName":"1"}),"instanceName":"1"}),"instanceName":"1"}),"instanceName":"1"});
            var Q50;
            Q50=makeQuery(id+"F15.opPattern","COPY",BODY,{"derivedFrom":makeQuery(id+"F12.opPattern","COPY",BODY,{"derivedFrom":makeQuery(id+"F9.opPattern","COPY",BODY,{"derivedFrom":makeQuery(id+"F1.opExtrude","SWEPT_BODY",BODY,{"disambiguationData":[OSD([sQuery(id+"F0.wireOp",EDGE,"E0")])]}),"instanceName":"1"}),"instanceName":"1"}),"instanceName":"1"});
            var Q51;
            Q51=makeQuery(id+"F15.opPattern","COPY",BODY,{"derivedFrom":makeQuery(id+"F4.opPattern","COPY",BODY,{"derivedFrom":makeQuery(id+"F1.opExtrude","SWEPT_BODY",BODY,{"disambiguationData":[OSD([sQuery(id+"F0.wireOp",EDGE,"E0")])]}),"instanceName":"1"}),"instanceName":"1"});
            var Q52;
            Q52=makeQuery(id+"F15.opPattern","COPY",BODY,{"derivedFrom":makeQuery(id+"F14.opPattern","COPY",BODY,{"derivedFrom":makeQuery(id+"F1.opExtrude","SWEPT_BODY",BODY,{"disambiguationData":[OSD([sQuery(id+"F0.wireOp",EDGE,"E0")])]}),"instanceName":"1"}),"instanceName":"1"});
            var Q53;
            Q53=makeQuery(id+"F15.opPattern","COPY",BODY,{"derivedFrom":makeQuery(id+"F11.opPattern","COPY",BODY,{"derivedFrom":makeQuery(id+"F9.opPattern","COPY",BODY,{"derivedFrom":makeQuery(id+"F1.opExtrude","SWEPT_BODY",BODY,{"disambiguationData":[OSD([sQuery(id+"F0.wireOp",EDGE,"E0")])]}),"instanceName":"1"}),"instanceName":"1"}),"instanceName":"1"});
            var Q54;
            Q54=makeQuery(id+"F15.opPattern","COPY",BODY,{"derivedFrom":makeQuery(id+"F1.opExtrude","SWEPT_BODY",BODY,{"disambiguationData":[OSD([sQuery(id+"F0.wireOp",EDGE,"E0")])]}),"instanceName":"1"});
            var Q55;
            Q55=makeQuery(id+"F1.opExtrude","SWEPT_BODY",BODY,{"disambiguationData":[OSD([sQuery(id+"F0.wireOp",EDGE,"E0")])]});
            var Q56;
            Q56=qCreatedBy(makeId("Front.planeOp"),FACE);
            transform(context, id + "F16", {"entities" : qUnion([Q0, Q1, Q2, Q3, Q4, Q5, Q6, Q7, Q8, Q9, Q10, Q11, Q12, Q13, Q14, Q15, Q16, Q17, Q18, Q19, Q20, Q21, Q22, Q23, Q24, Q25, Q26, Q27, Q28, Q29, Q30, Q31, Q32, Q33, Q34, Q35, Q36, Q37, Q38, Q39, Q40, Q41, Q42, Q43, Q44, Q45, Q46, Q47, Q48, Q49, Q50, Q51, Q52, Q53, Q54, Q55]), "transformType" : TransformType.TRANSLATION_DISTANCE, "transformDirection" : qUnion([Q56]), "distance" : 41 * mm, "makeCopy" : true});
        }
        {
            var Q0;
            Q0=makeQuery(id+"F4.opPattern","COPY",BODY,{"derivedFrom":makeQuery(id+"F1.opExtrude","SWEPT_BODY",BODY,{"disambiguationData":[OSD([sQuery(id+"F0.wireOp",EDGE,"E0")])]}),"instanceName":"1"});
            var Q1;
            Q1=makeQuery(id+"F9.opPattern","COPY",BODY,{"derivedFrom":makeQuery(id+"F4.opPattern","COPY",BODY,{"derivedFrom":makeQuery(id+"F1.opExtrude","SWEPT_BODY",BODY,{"disambiguationData":[OSD([sQuery(id+"F0.wireOp",EDGE,"E0")])]}),"instanceName":"1"}),"instanceName":"1"});
            var Q2;
            Q2=makeQuery(id+"F9.opPattern","COPY",BODY,{"derivedFrom":makeQuery(id+"F1.opExtrude","SWEPT_BODY",BODY,{"disambiguationData":[OSD([sQuery(id+"F0.wireOp",EDGE,"E0")])]}),"instanceName":"1"});
            var Q3;
            Q3=makeQuery(id+"F10.opPattern","COPY",BODY,{"derivedFrom":makeQuery(id+"F1.opExtrude","SWEPT_BODY",BODY,{"disambiguationData":[OSD([sQuery(id+"F0.wireOp",EDGE,"E0")])]}),"instanceName":"1"});
            var Q4;
            Q4=makeQuery(id+"F11.opPattern","COPY",BODY,{"derivedFrom":makeQuery(id+"F10.opPattern","COPY",BODY,{"derivedFrom":makeQuery(id+"F1.opExtrude","SWEPT_BODY",BODY,{"disambiguationData":[OSD([sQuery(id+"F0.wireOp",EDGE,"E0")])]}),"instanceName":"1"}),"instanceName":"1"});
            var Q5;
            Q5=makeQuery(id+"F11.opPattern","COPY",BODY,{"derivedFrom":makeQuery(id+"F9.opPattern","COPY",BODY,{"derivedFrom":makeQuery(id+"F1.opExtrude","SWEPT_BODY",BODY,{"disambiguationData":[OSD([sQuery(id+"F0.wireOp",EDGE,"E0")])]}),"instanceName":"1"}),"instanceName":"1"});
            var Q6;
            Q6=makeQuery(id+"F11.opPattern","COPY",BODY,{"derivedFrom":makeQuery(id+"F9.opPattern","COPY",BODY,{"derivedFrom":makeQuery(id+"F4.opPattern","COPY",BODY,{"derivedFrom":makeQuery(id+"F1.opExtrude","SWEPT_BODY",BODY,{"disambiguationData":[OSD([sQuery(id+"F0.wireOp",EDGE,"E0")])]}),"instanceName":"1"}),"instanceName":"1"}),"instanceName":"1"});
            var Q7;
            Q7=makeQuery(id+"F11.opPattern","COPY",BODY,{"derivedFrom":makeQuery(id+"F4.opPattern","COPY",BODY,{"derivedFrom":makeQuery(id+"F1.opExtrude","SWEPT_BODY",BODY,{"disambiguationData":[OSD([sQuery(id+"F0.wireOp",EDGE,"E0")])]}),"instanceName":"1"}),"instanceName":"1"});
            var Q8;
            Q8=makeQuery(id+"F11.opPattern","COPY",BODY,{"derivedFrom":makeQuery(id+"F1.opExtrude","SWEPT_BODY",BODY,{"disambiguationData":[OSD([sQuery(id+"F0.wireOp",EDGE,"E0")])]}),"instanceName":"1"});
            var Q9;
            Q9=makeQuery(id+"F12.opPattern","COPY",BODY,{"derivedFrom":makeQuery(id+"F11.opPattern","COPY",BODY,{"derivedFrom":makeQuery(id+"F1.opExtrude","SWEPT_BODY",BODY,{"disambiguationData":[OSD([sQuery(id+"F0.wireOp",EDGE,"E0")])]}),"instanceName":"1"}),"instanceName":"1"});
            var Q10;
            Q10=makeQuery(id+"F12.opPattern","COPY",BODY,{"derivedFrom":makeQuery(id+"F11.opPattern","COPY",BODY,{"derivedFrom":makeQuery(id+"F9.opPattern","COPY",BODY,{"derivedFrom":makeQuery(id+"F4.opPattern","COPY",BODY,{"derivedFrom":makeQuery(id+"F1.opExtrude","SWEPT_BODY",BODY,{"disambiguationData":[OSD([sQuery(id+"F0.wireOp",EDGE,"E0")])]}),"instanceName":"1"}),"instanceName":"1"}),"instanceName":"1"}),"instanceName":"1"});
            var Q11;
            Q11=makeQuery(id+"F12.opPattern","COPY",BODY,{"derivedFrom":makeQuery(id+"F10.opPattern","COPY",BODY,{"derivedFrom":makeQuery(id+"F1.opExtrude","SWEPT_BODY",BODY,{"disambiguationData":[OSD([sQuery(id+"F0.wireOp",EDGE,"E0")])]}),"instanceName":"1"}),"instanceName":"1"});
            var Q12;
            Q12=makeQuery(id+"F12.opPattern","COPY",BODY,{"derivedFrom":makeQuery(id+"F11.opPattern","COPY",BODY,{"derivedFrom":makeQuery(id+"F10.opPattern","COPY",BODY,{"derivedFrom":makeQuery(id+"F1.opExtrude","SWEPT_BODY",BODY,{"disambiguationData":[OSD([sQuery(id+"F0.wireOp",EDGE,"E0")])]}),"instanceName":"1"}),"instanceName":"1"}),"instanceName":"1"});
            var Q13;
            Q13=makeQuery(id+"F12.opPattern","COPY",BODY,{"derivedFrom":makeQuery(id+"F9.opPattern","COPY",BODY,{"derivedFrom":makeQuery(id+"F1.opExtrude","SWEPT_BODY",BODY,{"disambiguationData":[OSD([sQuery(id+"F0.wireOp",EDGE,"E0")])]}),"instanceName":"1"}),"instanceName":"1"});
            var Q14;
            Q14=makeQuery(id+"F12.opPattern","COPY",BODY,{"derivedFrom":makeQuery(id+"F11.opPattern","COPY",BODY,{"derivedFrom":makeQuery(id+"F4.opPattern","COPY",BODY,{"derivedFrom":makeQuery(id+"F1.opExtrude","SWEPT_BODY",BODY,{"disambiguationData":[OSD([sQuery(id+"F0.wireOp",EDGE,"E0")])]}),"instanceName":"1"}),"instanceName":"1"}),"instanceName":"1"});
            var Q15;
            Q15=makeQuery(id+"F12.opPattern","COPY",BODY,{"derivedFrom":makeQuery(id+"F4.opPattern","COPY",BODY,{"derivedFrom":makeQuery(id+"F1.opExtrude","SWEPT_BODY",BODY,{"disambiguationData":[OSD([sQuery(id+"F0.wireOp",EDGE,"E0")])]}),"instanceName":"1"}),"instanceName":"1"});
            var Q16;
            Q16=makeQuery(id+"F12.opPattern","COPY",BODY,{"derivedFrom":makeQuery(id+"F1.opExtrude","SWEPT_BODY",BODY,{"disambiguationData":[OSD([sQuery(id+"F0.wireOp",EDGE,"E0")])]}),"instanceName":"1"});
            var Q17;
            Q17=makeQuery(id+"F12.opPattern","COPY",BODY,{"derivedFrom":makeQuery(id+"F9.opPattern","COPY",BODY,{"derivedFrom":makeQuery(id+"F4.opPattern","COPY",BODY,{"derivedFrom":makeQuery(id+"F1.opExtrude","SWEPT_BODY",BODY,{"disambiguationData":[OSD([sQuery(id+"F0.wireOp",EDGE,"E0")])]}),"instanceName":"1"}),"instanceName":"1"}),"instanceName":"1"});
            var Q18;
            Q18=makeQuery(id+"F12.opPattern","COPY",BODY,{"derivedFrom":makeQuery(id+"F11.opPattern","COPY",BODY,{"derivedFrom":makeQuery(id+"F9.opPattern","COPY",BODY,{"derivedFrom":makeQuery(id+"F1.opExtrude","SWEPT_BODY",BODY,{"disambiguationData":[OSD([sQuery(id+"F0.wireOp",EDGE,"E0")])]}),"instanceName":"1"}),"instanceName":"1"}),"instanceName":"1"});
            var Q19;
            Q19=makeQuery(id+"F14.opPattern","COPY",BODY,{"derivedFrom":makeQuery(id+"F11.opPattern","COPY",BODY,{"derivedFrom":makeQuery(id+"F10.opPattern","COPY",BODY,{"derivedFrom":makeQuery(id+"F1.opExtrude","SWEPT_BODY",BODY,{"disambiguationData":[OSD([sQuery(id+"F0.wireOp",EDGE,"E0")])]}),"instanceName":"1"}),"instanceName":"1"}),"instanceName":"1"});
            var Q20;
            Q20=makeQuery(id+"F14.opPattern","COPY",BODY,{"derivedFrom":makeQuery(id+"F11.opPattern","COPY",BODY,{"derivedFrom":makeQuery(id+"F1.opExtrude","SWEPT_BODY",BODY,{"disambiguationData":[OSD([sQuery(id+"F0.wireOp",EDGE,"E0")])]}),"instanceName":"1"}),"instanceName":"1"});
            var Q21;
            Q21=makeQuery(id+"F14.opPattern","COPY",BODY,{"derivedFrom":makeQuery(id+"F11.opPattern","COPY",BODY,{"derivedFrom":makeQuery(id+"F9.opPattern","COPY",BODY,{"derivedFrom":makeQuery(id+"F4.opPattern","COPY",BODY,{"derivedFrom":makeQuery(id+"F1.opExtrude","SWEPT_BODY",BODY,{"disambiguationData":[OSD([sQuery(id+"F0.wireOp",EDGE,"E0")])]}),"instanceName":"1"}),"instanceName":"1"}),"instanceName":"1"}),"instanceName":"1"});
            var Q22;
            Q22=makeQuery(id+"F14.opPattern","COPY",BODY,{"derivedFrom":makeQuery(id+"F11.opPattern","COPY",BODY,{"derivedFrom":makeQuery(id+"F9.opPattern","COPY",BODY,{"derivedFrom":makeQuery(id+"F1.opExtrude","SWEPT_BODY",BODY,{"disambiguationData":[OSD([sQuery(id+"F0.wireOp",EDGE,"E0")])]}),"instanceName":"1"}),"instanceName":"1"}),"instanceName":"1"});
            var Q23;
            Q23=makeQuery(id+"F14.opPattern","COPY",BODY,{"derivedFrom":makeQuery(id+"F11.opPattern","COPY",BODY,{"derivedFrom":makeQuery(id+"F4.opPattern","COPY",BODY,{"derivedFrom":makeQuery(id+"F1.opExtrude","SWEPT_BODY",BODY,{"disambiguationData":[OSD([sQuery(id+"F0.wireOp",EDGE,"E0")])]}),"instanceName":"1"}),"instanceName":"1"}),"instanceName":"1"});
            var Q24;
            Q24=makeQuery(id+"F14.opPattern","COPY",BODY,{"derivedFrom":makeQuery(id+"F10.opPattern","COPY",BODY,{"derivedFrom":makeQuery(id+"F1.opExtrude","SWEPT_BODY",BODY,{"disambiguationData":[OSD([sQuery(id+"F0.wireOp",EDGE,"E0")])]}),"instanceName":"1"}),"instanceName":"1"});
            var Q25;
            Q25=makeQuery(id+"F14.opPattern","COPY",BODY,{"derivedFrom":makeQuery(id+"F4.opPattern","COPY",BODY,{"derivedFrom":makeQuery(id+"F1.opExtrude","SWEPT_BODY",BODY,{"disambiguationData":[OSD([sQuery(id+"F0.wireOp",EDGE,"E0")])]}),"instanceName":"1"}),"instanceName":"1"});
            var Q26;
            Q26=makeQuery(id+"F14.opPattern","COPY",BODY,{"derivedFrom":makeQuery(id+"F1.opExtrude","SWEPT_BODY",BODY,{"disambiguationData":[OSD([sQuery(id+"F0.wireOp",EDGE,"E0")])]}),"instanceName":"1"});
            var Q27;
            Q27=makeQuery(id+"F15.opPattern","COPY",BODY,{"derivedFrom":makeQuery(id+"F12.opPattern","COPY",BODY,{"derivedFrom":makeQuery(id+"F11.opPattern","COPY",BODY,{"derivedFrom":makeQuery(id+"F9.opPattern","COPY",BODY,{"derivedFrom":makeQuery(id+"F4.opPattern","COPY",BODY,{"derivedFrom":makeQuery(id+"F1.opExtrude","SWEPT_BODY",BODY,{"disambiguationData":[OSD([sQuery(id+"F0.wireOp",EDGE,"E0")])]}),"instanceName":"1"}),"instanceName":"1"}),"instanceName":"1"}),"instanceName":"1"}),"instanceName":"1"});
            var Q28;
            Q28=makeQuery(id+"F15.opPattern","COPY",BODY,{"derivedFrom":makeQuery(id+"F14.opPattern","COPY",BODY,{"derivedFrom":makeQuery(id+"F10.opPattern","COPY",BODY,{"derivedFrom":makeQuery(id+"F1.opExtrude","SWEPT_BODY",BODY,{"disambiguationData":[OSD([sQuery(id+"F0.wireOp",EDGE,"E0")])]}),"instanceName":"1"}),"instanceName":"1"}),"instanceName":"1"});
            var Q29;
            Q29=makeQuery(id+"F15.opPattern","COPY",BODY,{"derivedFrom":makeQuery(id+"F12.opPattern","COPY",BODY,{"derivedFrom":makeQuery(id+"F11.opPattern","COPY",BODY,{"derivedFrom":makeQuery(id+"F1.opExtrude","SWEPT_BODY",BODY,{"disambiguationData":[OSD([sQuery(id+"F0.wireOp",EDGE,"E0")])]}),"instanceName":"1"}),"instanceName":"1"}),"instanceName":"1"});
            var Q30;
            Q30=makeQuery(id+"F15.opPattern","COPY",BODY,{"derivedFrom":makeQuery(id+"F12.opPattern","COPY",BODY,{"derivedFrom":makeQuery(id+"F1.opExtrude","SWEPT_BODY",BODY,{"disambiguationData":[OSD([sQuery(id+"F0.wireOp",EDGE,"E0")])]}),"instanceName":"1"}),"instanceName":"1"});
            var Q31;
            Q31=makeQuery(id+"F15.opPattern","COPY",BODY,{"derivedFrom":makeQuery(id+"F12.opPattern","COPY",BODY,{"derivedFrom":makeQuery(id+"F9.opPattern","COPY",BODY,{"derivedFrom":makeQuery(id+"F4.opPattern","COPY",BODY,{"derivedFrom":makeQuery(id+"F1.opExtrude","SWEPT_BODY",BODY,{"disambiguationData":[OSD([sQuery(id+"F0.wireOp",EDGE,"E0")])]}),"instanceName":"1"}),"instanceName":"1"}),"instanceName":"1"}),"instanceName":"1"});
            var Q32;
            Q32=makeQuery(id+"F15.opPattern","COPY",BODY,{"derivedFrom":makeQuery(id+"F11.opPattern","COPY",BODY,{"derivedFrom":makeQuery(id+"F9.opPattern","COPY",BODY,{"derivedFrom":makeQuery(id+"F4.opPattern","COPY",BODY,{"derivedFrom":makeQuery(id+"F1.opExtrude","SWEPT_BODY",BODY,{"disambiguationData":[OSD([sQuery(id+"F0.wireOp",EDGE,"E0")])]}),"instanceName":"1"}),"instanceName":"1"}),"instanceName":"1"}),"instanceName":"1"});
            var Q33;
            Q33=makeQuery(id+"F15.opPattern","COPY",BODY,{"derivedFrom":makeQuery(id+"F11.opPattern","COPY",BODY,{"derivedFrom":makeQuery(id+"F1.opExtrude","SWEPT_BODY",BODY,{"disambiguationData":[OSD([sQuery(id+"F0.wireOp",EDGE,"E0")])]}),"instanceName":"1"}),"instanceName":"1"});
            var Q34;
            Q34=makeQuery(id+"F15.opPattern","COPY",BODY,{"derivedFrom":makeQuery(id+"F9.opPattern","COPY",BODY,{"derivedFrom":makeQuery(id+"F1.opExtrude","SWEPT_BODY",BODY,{"disambiguationData":[OSD([sQuery(id+"F0.wireOp",EDGE,"E0")])]}),"instanceName":"1"}),"instanceName":"1"});
            var Q35;
            Q35=makeQuery(id+"F15.opPattern","COPY",BODY,{"derivedFrom":makeQuery(id+"F12.opPattern","COPY",BODY,{"derivedFrom":makeQuery(id+"F10.opPattern","COPY",BODY,{"derivedFrom":makeQuery(id+"F1.opExtrude","SWEPT_BODY",BODY,{"disambiguationData":[OSD([sQuery(id+"F0.wireOp",EDGE,"E0")])]}),"instanceName":"1"}),"instanceName":"1"}),"instanceName":"1"});
            var Q36;
            Q36=makeQuery(id+"F15.opPattern","COPY",BODY,{"derivedFrom":makeQuery(id+"F12.opPattern","COPY",BODY,{"derivedFrom":makeQuery(id+"F4.opPattern","COPY",BODY,{"derivedFrom":makeQuery(id+"F1.opExtrude","SWEPT_BODY",BODY,{"disambiguationData":[OSD([sQuery(id+"F0.wireOp",EDGE,"E0")])]}),"instanceName":"1"}),"instanceName":"1"}),"instanceName":"1"});
            var Q37;
            Q37=makeQuery(id+"F15.opPattern","COPY",BODY,{"derivedFrom":makeQuery(id+"F14.opPattern","COPY",BODY,{"derivedFrom":makeQuery(id+"F11.opPattern","COPY",BODY,{"derivedFrom":makeQuery(id+"F10.opPattern","COPY",BODY,{"derivedFrom":makeQuery(id+"F1.opExtrude","SWEPT_BODY",BODY,{"disambiguationData":[OSD([sQuery(id+"F0.wireOp",EDGE,"E0")])]}),"instanceName":"1"}),"instanceName":"1"}),"instanceName":"1"}),"instanceName":"1"});
            var Q38;
            Q38=makeQuery(id+"F15.opPattern","COPY",BODY,{"derivedFrom":makeQuery(id+"F14.opPattern","COPY",BODY,{"derivedFrom":makeQuery(id+"F11.opPattern","COPY",BODY,{"derivedFrom":makeQuery(id+"F4.opPattern","COPY",BODY,{"derivedFrom":makeQuery(id+"F1.opExtrude","SWEPT_BODY",BODY,{"disambiguationData":[OSD([sQuery(id+"F0.wireOp",EDGE,"E0")])]}),"instanceName":"1"}),"instanceName":"1"}),"instanceName":"1"}),"instanceName":"1"});
            var Q39;
            Q39=makeQuery(id+"F15.opPattern","COPY",BODY,{"derivedFrom":makeQuery(id+"F14.opPattern","COPY",BODY,{"derivedFrom":makeQuery(id+"F4.opPattern","COPY",BODY,{"derivedFrom":makeQuery(id+"F1.opExtrude","SWEPT_BODY",BODY,{"disambiguationData":[OSD([sQuery(id+"F0.wireOp",EDGE,"E0")])]}),"instanceName":"1"}),"instanceName":"1"}),"instanceName":"1"});
            var Q40;
            Q40=makeQuery(id+"F15.opPattern","COPY",BODY,{"derivedFrom":makeQuery(id+"F11.opPattern","COPY",BODY,{"derivedFrom":makeQuery(id+"F4.opPattern","COPY",BODY,{"derivedFrom":makeQuery(id+"F1.opExtrude","SWEPT_BODY",BODY,{"disambiguationData":[OSD([sQuery(id+"F0.wireOp",EDGE,"E0")])]}),"instanceName":"1"}),"instanceName":"1"}),"instanceName":"1"});
            var Q41;
            Q41=makeQuery(id+"F15.opPattern","COPY",BODY,{"derivedFrom":makeQuery(id+"F9.opPattern","COPY",BODY,{"derivedFrom":makeQuery(id+"F4.opPattern","COPY",BODY,{"derivedFrom":makeQuery(id+"F1.opExtrude","SWEPT_BODY",BODY,{"disambiguationData":[OSD([sQuery(id+"F0.wireOp",EDGE,"E0")])]}),"instanceName":"1"}),"instanceName":"1"}),"instanceName":"1"});
            var Q42;
            Q42=makeQuery(id+"F15.opPattern","COPY",BODY,{"derivedFrom":makeQuery(id+"F14.opPattern","COPY",BODY,{"derivedFrom":makeQuery(id+"F11.opPattern","COPY",BODY,{"derivedFrom":makeQuery(id+"F1.opExtrude","SWEPT_BODY",BODY,{"disambiguationData":[OSD([sQuery(id+"F0.wireOp",EDGE,"E0")])]}),"instanceName":"1"}),"instanceName":"1"}),"instanceName":"1"});
            var Q43;
            Q43=makeQuery(id+"F15.opPattern","COPY",BODY,{"derivedFrom":makeQuery(id+"F12.opPattern","COPY",BODY,{"derivedFrom":makeQuery(id+"F11.opPattern","COPY",BODY,{"derivedFrom":makeQuery(id+"F10.opPattern","COPY",BODY,{"derivedFrom":makeQuery(id+"F1.opExtrude","SWEPT_BODY",BODY,{"disambiguationData":[OSD([sQuery(id+"F0.wireOp",EDGE,"E0")])]}),"instanceName":"1"}),"instanceName":"1"}),"instanceName":"1"}),"instanceName":"1"});
            var Q44;
            Q44=makeQuery(id+"F15.opPattern","COPY",BODY,{"derivedFrom":makeQuery(id+"F12.opPattern","COPY",BODY,{"derivedFrom":makeQuery(id+"F11.opPattern","COPY",BODY,{"derivedFrom":makeQuery(id+"F9.opPattern","COPY",BODY,{"derivedFrom":makeQuery(id+"F1.opExtrude","SWEPT_BODY",BODY,{"disambiguationData":[OSD([sQuery(id+"F0.wireOp",EDGE,"E0")])]}),"instanceName":"1"}),"instanceName":"1"}),"instanceName":"1"}),"instanceName":"1"});
            var Q45;
            Q45=makeQuery(id+"F15.opPattern","COPY",BODY,{"derivedFrom":makeQuery(id+"F14.opPattern","COPY",BODY,{"derivedFrom":makeQuery(id+"F11.opPattern","COPY",BODY,{"derivedFrom":makeQuery(id+"F9.opPattern","COPY",BODY,{"derivedFrom":makeQuery(id+"F1.opExtrude","SWEPT_BODY",BODY,{"disambiguationData":[OSD([sQuery(id+"F0.wireOp",EDGE,"E0")])]}),"instanceName":"1"}),"instanceName":"1"}),"instanceName":"1"}),"instanceName":"1"});
            var Q46;
            Q46=makeQuery(id+"F15.opPattern","COPY",BODY,{"derivedFrom":makeQuery(id+"F12.opPattern","COPY",BODY,{"derivedFrom":makeQuery(id+"F9.opPattern","COPY",BODY,{"derivedFrom":makeQuery(id+"F1.opExtrude","SWEPT_BODY",BODY,{"disambiguationData":[OSD([sQuery(id+"F0.wireOp",EDGE,"E0")])]}),"instanceName":"1"}),"instanceName":"1"}),"instanceName":"1"});
            var Q47;
            Q47=makeQuery(id+"F15.opPattern","COPY",BODY,{"derivedFrom":makeQuery(id+"F12.opPattern","COPY",BODY,{"derivedFrom":makeQuery(id+"F11.opPattern","COPY",BODY,{"derivedFrom":makeQuery(id+"F4.opPattern","COPY",BODY,{"derivedFrom":makeQuery(id+"F1.opExtrude","SWEPT_BODY",BODY,{"disambiguationData":[OSD([sQuery(id+"F0.wireOp",EDGE,"E0")])]}),"instanceName":"1"}),"instanceName":"1"}),"instanceName":"1"}),"instanceName":"1"});
            var Q48;
            Q48=makeQuery(id+"F15.opPattern","COPY",BODY,{"derivedFrom":makeQuery(id+"F1.opExtrude","SWEPT_BODY",BODY,{"disambiguationData":[OSD([sQuery(id+"F0.wireOp",EDGE,"E0")])]}),"instanceName":"1"});
            var Q49;
            Q49=makeQuery(id+"F15.opPattern","COPY",BODY,{"derivedFrom":makeQuery(id+"F4.opPattern","COPY",BODY,{"derivedFrom":makeQuery(id+"F1.opExtrude","SWEPT_BODY",BODY,{"disambiguationData":[OSD([sQuery(id+"F0.wireOp",EDGE,"E0")])]}),"instanceName":"1"}),"instanceName":"1"});
            var Q50;
            Q50=makeQuery(id+"F15.opPattern","COPY",BODY,{"derivedFrom":makeQuery(id+"F11.opPattern","COPY",BODY,{"derivedFrom":makeQuery(id+"F10.opPattern","COPY",BODY,{"derivedFrom":makeQuery(id+"F1.opExtrude","SWEPT_BODY",BODY,{"disambiguationData":[OSD([sQuery(id+"F0.wireOp",EDGE,"E0")])]}),"instanceName":"1"}),"instanceName":"1"}),"instanceName":"1"});
            var Q51;
            Q51=makeQuery(id+"F15.opPattern","COPY",BODY,{"derivedFrom":makeQuery(id+"F11.opPattern","COPY",BODY,{"derivedFrom":makeQuery(id+"F9.opPattern","COPY",BODY,{"derivedFrom":makeQuery(id+"F1.opExtrude","SWEPT_BODY",BODY,{"disambiguationData":[OSD([sQuery(id+"F0.wireOp",EDGE,"E0")])]}),"instanceName":"1"}),"instanceName":"1"}),"instanceName":"1"});
            var Q52;
            Q52=makeQuery(id+"F15.opPattern","COPY",BODY,{"derivedFrom":makeQuery(id+"F10.opPattern","COPY",BODY,{"derivedFrom":makeQuery(id+"F1.opExtrude","SWEPT_BODY",BODY,{"disambiguationData":[OSD([sQuery(id+"F0.wireOp",EDGE,"E0")])]}),"instanceName":"1"}),"instanceName":"1"});
            var Q53;
            Q53=makeQuery(id+"F15.opPattern","COPY",BODY,{"derivedFrom":makeQuery(id+"F14.opPattern","COPY",BODY,{"derivedFrom":makeQuery(id+"F11.opPattern","COPY",BODY,{"derivedFrom":makeQuery(id+"F9.opPattern","COPY",BODY,{"derivedFrom":makeQuery(id+"F4.opPattern","COPY",BODY,{"derivedFrom":makeQuery(id+"F1.opExtrude","SWEPT_BODY",BODY,{"disambiguationData":[OSD([sQuery(id+"F0.wireOp",EDGE,"E0")])]}),"instanceName":"1"}),"instanceName":"1"}),"instanceName":"1"}),"instanceName":"1"}),"instanceName":"1"});
            var Q54;
            Q54=makeQuery(id+"F15.opPattern","COPY",BODY,{"derivedFrom":makeQuery(id+"F14.opPattern","COPY",BODY,{"derivedFrom":makeQuery(id+"F1.opExtrude","SWEPT_BODY",BODY,{"disambiguationData":[OSD([sQuery(id+"F0.wireOp",EDGE,"E0")])]}),"instanceName":"1"}),"instanceName":"1"});
            var Q55;
            Q55=makeQuery(id+"F16.opPattern","COPY",BODY,{"derivedFrom":makeQuery(id+"F12.opPattern","COPY",BODY,{"derivedFrom":makeQuery(id+"F9.opPattern","COPY",BODY,{"derivedFrom":makeQuery(id+"F1.opExtrude","SWEPT_BODY",BODY,{"disambiguationData":[OSD([sQuery(id+"F0.wireOp",EDGE,"E0")])]}),"instanceName":"1"}),"instanceName":"1"}),"instanceName":"1"});
            var Q56;
            Q56=makeQuery(id+"F16.opPattern","COPY",BODY,{"derivedFrom":makeQuery(id+"F12.opPattern","COPY",BODY,{"derivedFrom":makeQuery(id+"F10.opPattern","COPY",BODY,{"derivedFrom":makeQuery(id+"F1.opExtrude","SWEPT_BODY",BODY,{"disambiguationData":[OSD([sQuery(id+"F0.wireOp",EDGE,"E0")])]}),"instanceName":"1"}),"instanceName":"1"}),"instanceName":"1"});
            var Q57;
            Q57=makeQuery(id+"F16.opPattern","COPY",BODY,{"derivedFrom":makeQuery(id+"F9.opPattern","COPY",BODY,{"derivedFrom":makeQuery(id+"F4.opPattern","COPY",BODY,{"derivedFrom":makeQuery(id+"F1.opExtrude","SWEPT_BODY",BODY,{"disambiguationData":[OSD([sQuery(id+"F0.wireOp",EDGE,"E0")])]}),"instanceName":"1"}),"instanceName":"1"}),"instanceName":"1"});
            var Q58;
            Q58=makeQuery(id+"F16.opPattern","COPY",BODY,{"derivedFrom":makeQuery(id+"F11.opPattern","COPY",BODY,{"derivedFrom":makeQuery(id+"F1.opExtrude","SWEPT_BODY",BODY,{"disambiguationData":[OSD([sQuery(id+"F0.wireOp",EDGE,"E0")])]}),"instanceName":"1"}),"instanceName":"1"});
            var Q59;
            Q59=makeQuery(id+"F16.opPattern","COPY",BODY,{"derivedFrom":makeQuery(id+"F14.opPattern","COPY",BODY,{"derivedFrom":makeQuery(id+"F11.opPattern","COPY",BODY,{"derivedFrom":makeQuery(id+"F9.opPattern","COPY",BODY,{"derivedFrom":makeQuery(id+"F1.opExtrude","SWEPT_BODY",BODY,{"disambiguationData":[OSD([sQuery(id+"F0.wireOp",EDGE,"E0")])]}),"instanceName":"1"}),"instanceName":"1"}),"instanceName":"1"}),"instanceName":"1"});
            var Q60;
            Q60=makeQuery(id+"F16.opPattern","COPY",BODY,{"derivedFrom":makeQuery(id+"F14.opPattern","COPY",BODY,{"derivedFrom":makeQuery(id+"F11.opPattern","COPY",BODY,{"derivedFrom":makeQuery(id+"F4.opPattern","COPY",BODY,{"derivedFrom":makeQuery(id+"F1.opExtrude","SWEPT_BODY",BODY,{"disambiguationData":[OSD([sQuery(id+"F0.wireOp",EDGE,"E0")])]}),"instanceName":"1"}),"instanceName":"1"}),"instanceName":"1"}),"instanceName":"1"});
            var Q61;
            Q61=makeQuery(id+"F16.opPattern","COPY",BODY,{"derivedFrom":makeQuery(id+"F12.opPattern","COPY",BODY,{"derivedFrom":makeQuery(id+"F11.opPattern","COPY",BODY,{"derivedFrom":makeQuery(id+"F9.opPattern","COPY",BODY,{"derivedFrom":makeQuery(id+"F4.opPattern","COPY",BODY,{"derivedFrom":makeQuery(id+"F1.opExtrude","SWEPT_BODY",BODY,{"disambiguationData":[OSD([sQuery(id+"F0.wireOp",EDGE,"E0")])]}),"instanceName":"1"}),"instanceName":"1"}),"instanceName":"1"}),"instanceName":"1"}),"instanceName":"1"});
            var Q62;
            Q62=makeQuery(id+"F16.opPattern","COPY",BODY,{"derivedFrom":makeQuery(id+"F15.opPattern","COPY",BODY,{"derivedFrom":makeQuery(id+"F11.opPattern","COPY",BODY,{"derivedFrom":makeQuery(id+"F4.opPattern","COPY",BODY,{"derivedFrom":makeQuery(id+"F1.opExtrude","SWEPT_BODY",BODY,{"disambiguationData":[OSD([sQuery(id+"F0.wireOp",EDGE,"E0")])]}),"instanceName":"1"}),"instanceName":"1"}),"instanceName":"1"}),"instanceName":"1"});
            var Q63;
            Q63=makeQuery(id+"F16.opPattern","COPY",BODY,{"derivedFrom":makeQuery(id+"F15.opPattern","COPY",BODY,{"derivedFrom":makeQuery(id+"F9.opPattern","COPY",BODY,{"derivedFrom":makeQuery(id+"F4.opPattern","COPY",BODY,{"derivedFrom":makeQuery(id+"F1.opExtrude","SWEPT_BODY",BODY,{"disambiguationData":[OSD([sQuery(id+"F0.wireOp",EDGE,"E0")])]}),"instanceName":"1"}),"instanceName":"1"}),"instanceName":"1"}),"instanceName":"1"});
            var Q64;
            Q64=makeQuery(id+"F16.opPattern","COPY",BODY,{"derivedFrom":makeQuery(id+"F15.opPattern","COPY",BODY,{"derivedFrom":makeQuery(id+"F1.opExtrude","SWEPT_BODY",BODY,{"disambiguationData":[OSD([sQuery(id+"F0.wireOp",EDGE,"E0")])]}),"instanceName":"1"}),"instanceName":"1"});
            var Q65;
            Q65=makeQuery(id+"F16.opPattern","COPY",BODY,{"derivedFrom":makeQuery(id+"F15.opPattern","COPY",BODY,{"derivedFrom":makeQuery(id+"F12.opPattern","COPY",BODY,{"derivedFrom":makeQuery(id+"F11.opPattern","COPY",BODY,{"derivedFrom":makeQuery(id+"F4.opPattern","COPY",BODY,{"derivedFrom":makeQuery(id+"F1.opExtrude","SWEPT_BODY",BODY,{"disambiguationData":[OSD([sQuery(id+"F0.wireOp",EDGE,"E0")])]}),"instanceName":"1"}),"instanceName":"1"}),"instanceName":"1"}),"instanceName":"1"}),"instanceName":"1"});
            var Q66;
            Q66=makeQuery(id+"F16.opPattern","COPY",BODY,{"derivedFrom":makeQuery(id+"F15.opPattern","COPY",BODY,{"derivedFrom":makeQuery(id+"F12.opPattern","COPY",BODY,{"derivedFrom":makeQuery(id+"F1.opExtrude","SWEPT_BODY",BODY,{"disambiguationData":[OSD([sQuery(id+"F0.wireOp",EDGE,"E0")])]}),"instanceName":"1"}),"instanceName":"1"}),"instanceName":"1"});
            var Q67;
            Q67=makeQuery(id+"F16.opPattern","COPY",BODY,{"derivedFrom":makeQuery(id+"F15.opPattern","COPY",BODY,{"derivedFrom":makeQuery(id+"F11.opPattern","COPY",BODY,{"derivedFrom":makeQuery(id+"F10.opPattern","COPY",BODY,{"derivedFrom":makeQuery(id+"F1.opExtrude","SWEPT_BODY",BODY,{"disambiguationData":[OSD([sQuery(id+"F0.wireOp",EDGE,"E0")])]}),"instanceName":"1"}),"instanceName":"1"}),"instanceName":"1"}),"instanceName":"1"});
            var Q68;
            Q68=makeQuery(id+"F16.opPattern","COPY",BODY,{"derivedFrom":makeQuery(id+"F15.opPattern","COPY",BODY,{"derivedFrom":makeQuery(id+"F14.opPattern","COPY",BODY,{"derivedFrom":makeQuery(id+"F11.opPattern","COPY",BODY,{"derivedFrom":makeQuery(id+"F9.opPattern","COPY",BODY,{"derivedFrom":makeQuery(id+"F1.opExtrude","SWEPT_BODY",BODY,{"disambiguationData":[OSD([sQuery(id+"F0.wireOp",EDGE,"E0")])]}),"instanceName":"1"}),"instanceName":"1"}),"instanceName":"1"}),"instanceName":"1"}),"instanceName":"1"});
            var Q69;
            Q69=makeQuery(id+"F16.opPattern","COPY",BODY,{"derivedFrom":makeQuery(id+"F15.opPattern","COPY",BODY,{"derivedFrom":makeQuery(id+"F14.opPattern","COPY",BODY,{"derivedFrom":makeQuery(id+"F10.opPattern","COPY",BODY,{"derivedFrom":makeQuery(id+"F1.opExtrude","SWEPT_BODY",BODY,{"disambiguationData":[OSD([sQuery(id+"F0.wireOp",EDGE,"E0")])]}),"instanceName":"1"}),"instanceName":"1"}),"instanceName":"1"}),"instanceName":"1"});
            var Q70;
            Q70=makeQuery(id+"F16.opPattern","COPY",BODY,{"derivedFrom":makeQuery(id+"F15.opPattern","COPY",BODY,{"derivedFrom":makeQuery(id+"F14.opPattern","COPY",BODY,{"derivedFrom":makeQuery(id+"F1.opExtrude","SWEPT_BODY",BODY,{"disambiguationData":[OSD([sQuery(id+"F0.wireOp",EDGE,"E0")])]}),"instanceName":"1"}),"instanceName":"1"}),"instanceName":"1"});
            var Q71;
            Q71=makeQuery(id+"F16.opPattern","COPY",BODY,{"derivedFrom":makeQuery(id+"F15.opPattern","COPY",BODY,{"derivedFrom":makeQuery(id+"F14.opPattern","COPY",BODY,{"derivedFrom":makeQuery(id+"F11.opPattern","COPY",BODY,{"derivedFrom":makeQuery(id+"F10.opPattern","COPY",BODY,{"derivedFrom":makeQuery(id+"F1.opExtrude","SWEPT_BODY",BODY,{"disambiguationData":[OSD([sQuery(id+"F0.wireOp",EDGE,"E0")])]}),"instanceName":"1"}),"instanceName":"1"}),"instanceName":"1"}),"instanceName":"1"}),"instanceName":"1"});
            var Q72;
            Q72=makeQuery(id+"F16.opPattern","COPY",BODY,{"derivedFrom":makeQuery(id+"F14.opPattern","COPY",BODY,{"derivedFrom":makeQuery(id+"F11.opPattern","COPY",BODY,{"derivedFrom":makeQuery(id+"F10.opPattern","COPY",BODY,{"derivedFrom":makeQuery(id+"F1.opExtrude","SWEPT_BODY",BODY,{"disambiguationData":[OSD([sQuery(id+"F0.wireOp",EDGE,"E0")])]}),"instanceName":"1"}),"instanceName":"1"}),"instanceName":"1"}),"instanceName":"1"});
            var Q73;
            Q73=makeQuery(id+"F16.opPattern","COPY",BODY,{"derivedFrom":makeQuery(id+"F11.opPattern","COPY",BODY,{"derivedFrom":makeQuery(id+"F4.opPattern","COPY",BODY,{"derivedFrom":makeQuery(id+"F1.opExtrude","SWEPT_BODY",BODY,{"disambiguationData":[OSD([sQuery(id+"F0.wireOp",EDGE,"E0")])]}),"instanceName":"1"}),"instanceName":"1"}),"instanceName":"1"});
            var Q74;
            Q74=makeQuery(id+"F16.opPattern","COPY",BODY,{"derivedFrom":makeQuery(id+"F11.opPattern","COPY",BODY,{"derivedFrom":makeQuery(id+"F10.opPattern","COPY",BODY,{"derivedFrom":makeQuery(id+"F1.opExtrude","SWEPT_BODY",BODY,{"disambiguationData":[OSD([sQuery(id+"F0.wireOp",EDGE,"E0")])]}),"instanceName":"1"}),"instanceName":"1"}),"instanceName":"1"});
            var Q75;
            Q75=makeQuery(id+"F16.opPattern","COPY",BODY,{"derivedFrom":makeQuery(id+"F4.opPattern","COPY",BODY,{"derivedFrom":makeQuery(id+"F1.opExtrude","SWEPT_BODY",BODY,{"disambiguationData":[OSD([sQuery(id+"F0.wireOp",EDGE,"E0")])]}),"instanceName":"1"}),"instanceName":"1"});
            var Q76;
            Q76=makeQuery(id+"F16.opPattern","COPY",BODY,{"derivedFrom":makeQuery(id+"F9.opPattern","COPY",BODY,{"derivedFrom":makeQuery(id+"F1.opExtrude","SWEPT_BODY",BODY,{"disambiguationData":[OSD([sQuery(id+"F0.wireOp",EDGE,"E0")])]}),"instanceName":"1"}),"instanceName":"1"});
            var Q77;
            Q77=makeQuery(id+"F16.opPattern","COPY",BODY,{"derivedFrom":makeQuery(id+"F1.opExtrude","SWEPT_BODY",BODY,{"disambiguationData":[OSD([sQuery(id+"F0.wireOp",EDGE,"E0")])]}),"instanceName":"1"});
            var Q78;
            Q78=makeQuery(id+"F16.opPattern","COPY",BODY,{"derivedFrom":makeQuery(id+"F12.opPattern","COPY",BODY,{"derivedFrom":makeQuery(id+"F11.opPattern","COPY",BODY,{"derivedFrom":makeQuery(id+"F10.opPattern","COPY",BODY,{"derivedFrom":makeQuery(id+"F1.opExtrude","SWEPT_BODY",BODY,{"disambiguationData":[OSD([sQuery(id+"F0.wireOp",EDGE,"E0")])]}),"instanceName":"1"}),"instanceName":"1"}),"instanceName":"1"}),"instanceName":"1"});
            var Q79;
            Q79=makeQuery(id+"F16.opPattern","COPY",BODY,{"derivedFrom":makeQuery(id+"F15.opPattern","COPY",BODY,{"derivedFrom":makeQuery(id+"F12.opPattern","COPY",BODY,{"derivedFrom":makeQuery(id+"F11.opPattern","COPY",BODY,{"derivedFrom":makeQuery(id+"F1.opExtrude","SWEPT_BODY",BODY,{"disambiguationData":[OSD([sQuery(id+"F0.wireOp",EDGE,"E0")])]}),"instanceName":"1"}),"instanceName":"1"}),"instanceName":"1"}),"instanceName":"1"});
            var Q80;
            Q80=makeQuery(id+"F16.opPattern","COPY",BODY,{"derivedFrom":makeQuery(id+"F15.opPattern","COPY",BODY,{"derivedFrom":makeQuery(id+"F12.opPattern","COPY",BODY,{"derivedFrom":makeQuery(id+"F9.opPattern","COPY",BODY,{"derivedFrom":makeQuery(id+"F4.opPattern","COPY",BODY,{"derivedFrom":makeQuery(id+"F1.opExtrude","SWEPT_BODY",BODY,{"disambiguationData":[OSD([sQuery(id+"F0.wireOp",EDGE,"E0")])]}),"instanceName":"1"}),"instanceName":"1"}),"instanceName":"1"}),"instanceName":"1"}),"instanceName":"1"});
            var Q81;
            Q81=makeQuery(id+"F16.opPattern","COPY",BODY,{"derivedFrom":makeQuery(id+"F15.opPattern","COPY",BODY,{"derivedFrom":makeQuery(id+"F12.opPattern","COPY",BODY,{"derivedFrom":makeQuery(id+"F4.opPattern","COPY",BODY,{"derivedFrom":makeQuery(id+"F1.opExtrude","SWEPT_BODY",BODY,{"disambiguationData":[OSD([sQuery(id+"F0.wireOp",EDGE,"E0")])]}),"instanceName":"1"}),"instanceName":"1"}),"instanceName":"1"}),"instanceName":"1"});
            var Q82;
            Q82=makeQuery(id+"F16.opPattern","COPY",BODY,{"derivedFrom":makeQuery(id+"F15.opPattern","COPY",BODY,{"derivedFrom":makeQuery(id+"F14.opPattern","COPY",BODY,{"derivedFrom":makeQuery(id+"F11.opPattern","COPY",BODY,{"derivedFrom":makeQuery(id+"F9.opPattern","COPY",BODY,{"derivedFrom":makeQuery(id+"F4.opPattern","COPY",BODY,{"derivedFrom":makeQuery(id+"F1.opExtrude","SWEPT_BODY",BODY,{"disambiguationData":[OSD([sQuery(id+"F0.wireOp",EDGE,"E0")])]}),"instanceName":"1"}),"instanceName":"1"}),"instanceName":"1"}),"instanceName":"1"}),"instanceName":"1"}),"instanceName":"1"});
            var Q83;
            Q83=makeQuery(id+"F16.opPattern","COPY",BODY,{"derivedFrom":makeQuery(id+"F15.opPattern","COPY",BODY,{"derivedFrom":makeQuery(id+"F14.opPattern","COPY",BODY,{"derivedFrom":makeQuery(id+"F11.opPattern","COPY",BODY,{"derivedFrom":makeQuery(id+"F1.opExtrude","SWEPT_BODY",BODY,{"disambiguationData":[OSD([sQuery(id+"F0.wireOp",EDGE,"E0")])]}),"instanceName":"1"}),"instanceName":"1"}),"instanceName":"1"}),"instanceName":"1"});
            var Q84;
            Q84=makeQuery(id+"F16.opPattern","COPY",BODY,{"derivedFrom":makeQuery(id+"F15.opPattern","COPY",BODY,{"derivedFrom":makeQuery(id+"F12.opPattern","COPY",BODY,{"derivedFrom":makeQuery(id+"F11.opPattern","COPY",BODY,{"derivedFrom":makeQuery(id+"F9.opPattern","COPY",BODY,{"derivedFrom":makeQuery(id+"F1.opExtrude","SWEPT_BODY",BODY,{"disambiguationData":[OSD([sQuery(id+"F0.wireOp",EDGE,"E0")])]}),"instanceName":"1"}),"instanceName":"1"}),"instanceName":"1"}),"instanceName":"1"}),"instanceName":"1"});
            var Q85;
            Q85=makeQuery(id+"F16.opPattern","COPY",BODY,{"derivedFrom":makeQuery(id+"F12.opPattern","COPY",BODY,{"derivedFrom":makeQuery(id+"F9.opPattern","COPY",BODY,{"derivedFrom":makeQuery(id+"F4.opPattern","COPY",BODY,{"derivedFrom":makeQuery(id+"F1.opExtrude","SWEPT_BODY",BODY,{"disambiguationData":[OSD([sQuery(id+"F0.wireOp",EDGE,"E0")])]}),"instanceName":"1"}),"instanceName":"1"}),"instanceName":"1"}),"instanceName":"1"});
            var Q86;
            Q86=makeQuery(id+"F16.opPattern","COPY",BODY,{"derivedFrom":makeQuery(id+"F14.opPattern","COPY",BODY,{"derivedFrom":makeQuery(id+"F1.opExtrude","SWEPT_BODY",BODY,{"disambiguationData":[OSD([sQuery(id+"F0.wireOp",EDGE,"E0")])]}),"instanceName":"1"}),"instanceName":"1"});
            var Q87;
            Q87=makeQuery(id+"F16.opPattern","COPY",BODY,{"derivedFrom":makeQuery(id+"F12.opPattern","COPY",BODY,{"derivedFrom":makeQuery(id+"F11.opPattern","COPY",BODY,{"derivedFrom":makeQuery(id+"F4.opPattern","COPY",BODY,{"derivedFrom":makeQuery(id+"F1.opExtrude","SWEPT_BODY",BODY,{"disambiguationData":[OSD([sQuery(id+"F0.wireOp",EDGE,"E0")])]}),"instanceName":"1"}),"instanceName":"1"}),"instanceName":"1"}),"instanceName":"1"});
            var Q88;
            Q88=makeQuery(id+"F16.opPattern","COPY",BODY,{"derivedFrom":makeQuery(id+"F15.opPattern","COPY",BODY,{"derivedFrom":makeQuery(id+"F9.opPattern","COPY",BODY,{"derivedFrom":makeQuery(id+"F1.opExtrude","SWEPT_BODY",BODY,{"disambiguationData":[OSD([sQuery(id+"F0.wireOp",EDGE,"E0")])]}),"instanceName":"1"}),"instanceName":"1"}),"instanceName":"1"});
            var Q89;
            Q89=makeQuery(id+"F16.opPattern","COPY",BODY,{"derivedFrom":makeQuery(id+"F15.opPattern","COPY",BODY,{"derivedFrom":makeQuery(id+"F4.opPattern","COPY",BODY,{"derivedFrom":makeQuery(id+"F1.opExtrude","SWEPT_BODY",BODY,{"disambiguationData":[OSD([sQuery(id+"F0.wireOp",EDGE,"E0")])]}),"instanceName":"1"}),"instanceName":"1"}),"instanceName":"1"});
            var Q90;
            Q90=makeQuery(id+"F16.opPattern","COPY",BODY,{"derivedFrom":makeQuery(id+"F14.opPattern","COPY",BODY,{"derivedFrom":makeQuery(id+"F11.opPattern","COPY",BODY,{"derivedFrom":makeQuery(id+"F9.opPattern","COPY",BODY,{"derivedFrom":makeQuery(id+"F4.opPattern","COPY",BODY,{"derivedFrom":makeQuery(id+"F1.opExtrude","SWEPT_BODY",BODY,{"disambiguationData":[OSD([sQuery(id+"F0.wireOp",EDGE,"E0")])]}),"instanceName":"1"}),"instanceName":"1"}),"instanceName":"1"}),"instanceName":"1"}),"instanceName":"1"});
            var Q91;
            Q91=makeQuery(id+"F16.opPattern","COPY",BODY,{"derivedFrom":makeQuery(id+"F14.opPattern","COPY",BODY,{"derivedFrom":makeQuery(id+"F11.opPattern","COPY",BODY,{"derivedFrom":makeQuery(id+"F1.opExtrude","SWEPT_BODY",BODY,{"disambiguationData":[OSD([sQuery(id+"F0.wireOp",EDGE,"E0")])]}),"instanceName":"1"}),"instanceName":"1"}),"instanceName":"1"});
            var Q92;
            Q92=makeQuery(id+"F16.opPattern","COPY",BODY,{"derivedFrom":makeQuery(id+"F15.opPattern","COPY",BODY,{"derivedFrom":makeQuery(id+"F10.opPattern","COPY",BODY,{"derivedFrom":makeQuery(id+"F1.opExtrude","SWEPT_BODY",BODY,{"disambiguationData":[OSD([sQuery(id+"F0.wireOp",EDGE,"E0")])]}),"instanceName":"1"}),"instanceName":"1"}),"instanceName":"1"});
            var Q93;
            Q93=makeQuery(id+"F16.opPattern","COPY",BODY,{"derivedFrom":makeQuery(id+"F15.opPattern","COPY",BODY,{"derivedFrom":makeQuery(id+"F14.opPattern","COPY",BODY,{"derivedFrom":makeQuery(id+"F4.opPattern","COPY",BODY,{"derivedFrom":makeQuery(id+"F1.opExtrude","SWEPT_BODY",BODY,{"disambiguationData":[OSD([sQuery(id+"F0.wireOp",EDGE,"E0")])]}),"instanceName":"1"}),"instanceName":"1"}),"instanceName":"1"}),"instanceName":"1"});
            var Q94;
            Q94=makeQuery(id+"F16.opPattern","COPY",BODY,{"derivedFrom":makeQuery(id+"F15.opPattern","COPY",BODY,{"derivedFrom":makeQuery(id+"F12.opPattern","COPY",BODY,{"derivedFrom":makeQuery(id+"F11.opPattern","COPY",BODY,{"derivedFrom":makeQuery(id+"F9.opPattern","COPY",BODY,{"derivedFrom":makeQuery(id+"F4.opPattern","COPY",BODY,{"derivedFrom":makeQuery(id+"F1.opExtrude","SWEPT_BODY",BODY,{"disambiguationData":[OSD([sQuery(id+"F0.wireOp",EDGE,"E0")])]}),"instanceName":"1"}),"instanceName":"1"}),"instanceName":"1"}),"instanceName":"1"}),"instanceName":"1"}),"instanceName":"1"});
            var Q95;
            Q95=makeQuery(id+"F16.opPattern","COPY",BODY,{"derivedFrom":makeQuery(id+"F15.opPattern","COPY",BODY,{"derivedFrom":makeQuery(id+"F12.opPattern","COPY",BODY,{"derivedFrom":makeQuery(id+"F10.opPattern","COPY",BODY,{"derivedFrom":makeQuery(id+"F1.opExtrude","SWEPT_BODY",BODY,{"disambiguationData":[OSD([sQuery(id+"F0.wireOp",EDGE,"E0")])]}),"instanceName":"1"}),"instanceName":"1"}),"instanceName":"1"}),"instanceName":"1"});
            var Q96;
            Q96=makeQuery(id+"F16.opPattern","COPY",BODY,{"derivedFrom":makeQuery(id+"F12.opPattern","COPY",BODY,{"derivedFrom":makeQuery(id+"F1.opExtrude","SWEPT_BODY",BODY,{"disambiguationData":[OSD([sQuery(id+"F0.wireOp",EDGE,"E0")])]}),"instanceName":"1"}),"instanceName":"1"});
            var Q97;
            Q97=makeQuery(id+"F16.opPattern","COPY",BODY,{"derivedFrom":makeQuery(id+"F11.opPattern","COPY",BODY,{"derivedFrom":makeQuery(id+"F9.opPattern","COPY",BODY,{"derivedFrom":makeQuery(id+"F4.opPattern","COPY",BODY,{"derivedFrom":makeQuery(id+"F1.opExtrude","SWEPT_BODY",BODY,{"disambiguationData":[OSD([sQuery(id+"F0.wireOp",EDGE,"E0")])]}),"instanceName":"1"}),"instanceName":"1"}),"instanceName":"1"}),"instanceName":"1"});
            var Q98;
            Q98=makeQuery(id+"F16.opPattern","COPY",BODY,{"derivedFrom":makeQuery(id+"F12.opPattern","COPY",BODY,{"derivedFrom":makeQuery(id+"F11.opPattern","COPY",BODY,{"derivedFrom":makeQuery(id+"F9.opPattern","COPY",BODY,{"derivedFrom":makeQuery(id+"F1.opExtrude","SWEPT_BODY",BODY,{"disambiguationData":[OSD([sQuery(id+"F0.wireOp",EDGE,"E0")])]}),"instanceName":"1"}),"instanceName":"1"}),"instanceName":"1"}),"instanceName":"1"});
            var Q99;
            Q99=makeQuery(id+"F16.opPattern","COPY",BODY,{"derivedFrom":makeQuery(id+"F15.opPattern","COPY",BODY,{"derivedFrom":makeQuery(id+"F11.opPattern","COPY",BODY,{"derivedFrom":makeQuery(id+"F1.opExtrude","SWEPT_BODY",BODY,{"disambiguationData":[OSD([sQuery(id+"F0.wireOp",EDGE,"E0")])]}),"instanceName":"1"}),"instanceName":"1"}),"instanceName":"1"});
            var Q100;
            Q100=makeQuery(id+"F16.opPattern","COPY",BODY,{"derivedFrom":makeQuery(id+"F12.opPattern","COPY",BODY,{"derivedFrom":makeQuery(id+"F4.opPattern","COPY",BODY,{"derivedFrom":makeQuery(id+"F1.opExtrude","SWEPT_BODY",BODY,{"disambiguationData":[OSD([sQuery(id+"F0.wireOp",EDGE,"E0")])]}),"instanceName":"1"}),"instanceName":"1"}),"instanceName":"1"});
            var Q101;
            Q101=makeQuery(id+"F16.opPattern","COPY",BODY,{"derivedFrom":makeQuery(id+"F15.opPattern","COPY",BODY,{"derivedFrom":makeQuery(id+"F12.opPattern","COPY",BODY,{"derivedFrom":makeQuery(id+"F9.opPattern","COPY",BODY,{"derivedFrom":makeQuery(id+"F1.opExtrude","SWEPT_BODY",BODY,{"disambiguationData":[OSD([sQuery(id+"F0.wireOp",EDGE,"E0")])]}),"instanceName":"1"}),"instanceName":"1"}),"instanceName":"1"}),"instanceName":"1"});
            var Q102;
            Q102=makeQuery(id+"F16.opPattern","COPY",BODY,{"derivedFrom":makeQuery(id+"F15.opPattern","COPY",BODY,{"derivedFrom":makeQuery(id+"F14.opPattern","COPY",BODY,{"derivedFrom":makeQuery(id+"F11.opPattern","COPY",BODY,{"derivedFrom":makeQuery(id+"F4.opPattern","COPY",BODY,{"derivedFrom":makeQuery(id+"F1.opExtrude","SWEPT_BODY",BODY,{"disambiguationData":[OSD([sQuery(id+"F0.wireOp",EDGE,"E0")])]}),"instanceName":"1"}),"instanceName":"1"}),"instanceName":"1"}),"instanceName":"1"}),"instanceName":"1"});
            var Q103;
            Q103=makeQuery(id+"F16.opPattern","COPY",BODY,{"derivedFrom":makeQuery(id+"F14.opPattern","COPY",BODY,{"derivedFrom":makeQuery(id+"F4.opPattern","COPY",BODY,{"derivedFrom":makeQuery(id+"F1.opExtrude","SWEPT_BODY",BODY,{"disambiguationData":[OSD([sQuery(id+"F0.wireOp",EDGE,"E0")])]}),"instanceName":"1"}),"instanceName":"1"}),"instanceName":"1"});
            var Q104;
            Q104=makeQuery(id+"F16.opPattern","COPY",BODY,{"derivedFrom":makeQuery(id+"F12.opPattern","COPY",BODY,{"derivedFrom":makeQuery(id+"F11.opPattern","COPY",BODY,{"derivedFrom":makeQuery(id+"F1.opExtrude","SWEPT_BODY",BODY,{"disambiguationData":[OSD([sQuery(id+"F0.wireOp",EDGE,"E0")])]}),"instanceName":"1"}),"instanceName":"1"}),"instanceName":"1"});
            var Q105;
            Q105=makeQuery(id+"F16.opPattern","COPY",BODY,{"derivedFrom":makeQuery(id+"F15.opPattern","COPY",BODY,{"derivedFrom":makeQuery(id+"F11.opPattern","COPY",BODY,{"derivedFrom":makeQuery(id+"F9.opPattern","COPY",BODY,{"derivedFrom":makeQuery(id+"F1.opExtrude","SWEPT_BODY",BODY,{"disambiguationData":[OSD([sQuery(id+"F0.wireOp",EDGE,"E0")])]}),"instanceName":"1"}),"instanceName":"1"}),"instanceName":"1"}),"instanceName":"1"});
            var Q106;
            Q106=makeQuery(id+"F16.opPattern","COPY",BODY,{"derivedFrom":makeQuery(id+"F15.opPattern","COPY",BODY,{"derivedFrom":makeQuery(id+"F12.opPattern","COPY",BODY,{"derivedFrom":makeQuery(id+"F11.opPattern","COPY",BODY,{"derivedFrom":makeQuery(id+"F10.opPattern","COPY",BODY,{"derivedFrom":makeQuery(id+"F1.opExtrude","SWEPT_BODY",BODY,{"disambiguationData":[OSD([sQuery(id+"F0.wireOp",EDGE,"E0")])]}),"instanceName":"1"}),"instanceName":"1"}),"instanceName":"1"}),"instanceName":"1"}),"instanceName":"1"});
            var Q107;
            Q107=makeQuery(id+"F16.opPattern","COPY",BODY,{"derivedFrom":makeQuery(id+"F14.opPattern","COPY",BODY,{"derivedFrom":makeQuery(id+"F10.opPattern","COPY",BODY,{"derivedFrom":makeQuery(id+"F1.opExtrude","SWEPT_BODY",BODY,{"disambiguationData":[OSD([sQuery(id+"F0.wireOp",EDGE,"E0")])]}),"instanceName":"1"}),"instanceName":"1"}),"instanceName":"1"});
            var Q108;
            Q108=makeQuery(id+"F16.opPattern","COPY",BODY,{"derivedFrom":makeQuery(id+"F15.opPattern","COPY",BODY,{"derivedFrom":makeQuery(id+"F11.opPattern","COPY",BODY,{"derivedFrom":makeQuery(id+"F9.opPattern","COPY",BODY,{"derivedFrom":makeQuery(id+"F4.opPattern","COPY",BODY,{"derivedFrom":makeQuery(id+"F1.opExtrude","SWEPT_BODY",BODY,{"disambiguationData":[OSD([sQuery(id+"F0.wireOp",EDGE,"E0")])]}),"instanceName":"1"}),"instanceName":"1"}),"instanceName":"1"}),"instanceName":"1"}),"instanceName":"1"});
            var Q109;
            Q109=makeQuery(id+"F16.opPattern","COPY",BODY,{"derivedFrom":makeQuery(id+"F10.opPattern","COPY",BODY,{"derivedFrom":makeQuery(id+"F1.opExtrude","SWEPT_BODY",BODY,{"disambiguationData":[OSD([sQuery(id+"F0.wireOp",EDGE,"E0")])]}),"instanceName":"1"}),"instanceName":"1"});
            var Q110;
            Q110=makeQuery(id+"F1.opExtrude","SWEPT_BODY",BODY,{"disambiguationData":[OSD([sQuery(id+"F0.wireOp",EDGE,"E0")])]});
            var Q111;
            Q111=makeQuery(id+"F16.opPattern","COPY",BODY,{"derivedFrom":makeQuery(id+"F11.opPattern","COPY",BODY,{"derivedFrom":makeQuery(id+"F9.opPattern","COPY",BODY,{"derivedFrom":makeQuery(id+"F1.opExtrude","SWEPT_BODY",BODY,{"disambiguationData":[OSD([sQuery(id+"F0.wireOp",EDGE,"E0")])]}),"instanceName":"1"}),"instanceName":"1"}),"instanceName":"1"});
            var Q112;
            Q112=qCreatedBy(makeId("Front.planeOp"),FACE);
            transform(context, id + "F17", {"entities" : qUnion([Q0, Q1, Q2, Q3, Q4, Q5, Q6, Q7, Q8, Q9, Q10, Q11, Q12, Q13, Q14, Q15, Q16, Q17, Q18, Q19, Q20, Q21, Q22, Q23, Q24, Q25, Q26, Q27, Q28, Q29, Q30, Q31, Q32, Q33, Q34, Q35, Q36, Q37, Q38, Q39, Q40, Q41, Q42, Q43, Q44, Q45, Q46, Q47, Q48, Q49, Q50, Q51, Q52, Q53, Q54, Q55, Q56, Q57, Q58, Q59, Q60, Q61, Q62, Q63, Q64, Q65, Q66, Q67, Q68, Q69, Q70, Q71, Q72, Q73, Q74, Q75, Q76, Q77, Q78, Q79, Q80, Q81, Q82, Q83, Q84, Q85, Q86, Q87, Q88, Q89, Q90, Q91, Q92, Q93, Q94, Q95, Q96, Q97, Q98, Q99, Q100, Q101, Q102, Q103, Q104, Q105, Q106, Q107, Q108, Q109, Q110, Q111]), "transformType" : TransformType.TRANSLATION_DISTANCE, "transformDirection" : qUnion([Q112]), "distance" : 82 * mm, "makeCopy" : true});
        }
        {
            var Q0;
            Q0=makeQuery(id+"F1.opExtrude","SWEPT_BODY",BODY,{"disambiguationData":[OSD([sQuery(id+"F0.wireOp",EDGE,"E0")])]});
            var Q1;
            Q1=makeQuery(id+"F4.opPattern","COPY",BODY,{"derivedFrom":makeQuery(id+"F1.opExtrude","SWEPT_BODY",BODY,{"disambiguationData":[OSD([sQuery(id+"F0.wireOp",EDGE,"E0")])]}),"instanceName":"1"});
            var Q2;
            Q2=makeQuery(id+"F9.opPattern","COPY",BODY,{"derivedFrom":makeQuery(id+"F4.opPattern","COPY",BODY,{"derivedFrom":makeQuery(id+"F1.opExtrude","SWEPT_BODY",BODY,{"disambiguationData":[OSD([sQuery(id+"F0.wireOp",EDGE,"E0")])]}),"instanceName":"1"}),"instanceName":"1"});
            var Q3;
            Q3=makeQuery(id+"F9.opPattern","COPY",BODY,{"derivedFrom":makeQuery(id+"F1.opExtrude","SWEPT_BODY",BODY,{"disambiguationData":[OSD([sQuery(id+"F0.wireOp",EDGE,"E0")])]}),"instanceName":"1"});
            var Q4;
            Q4=makeQuery(id+"F10.opPattern","COPY",BODY,{"derivedFrom":makeQuery(id+"F1.opExtrude","SWEPT_BODY",BODY,{"disambiguationData":[OSD([sQuery(id+"F0.wireOp",EDGE,"E0")])]}),"instanceName":"1"});
            var Q5;
            Q5=makeQuery(id+"F11.opPattern","COPY",BODY,{"derivedFrom":makeQuery(id+"F10.opPattern","COPY",BODY,{"derivedFrom":makeQuery(id+"F1.opExtrude","SWEPT_BODY",BODY,{"disambiguationData":[OSD([sQuery(id+"F0.wireOp",EDGE,"E0")])]}),"instanceName":"1"}),"instanceName":"1"});
            var Q6;
            Q6=makeQuery(id+"F11.opPattern","COPY",BODY,{"derivedFrom":makeQuery(id+"F9.opPattern","COPY",BODY,{"derivedFrom":makeQuery(id+"F1.opExtrude","SWEPT_BODY",BODY,{"disambiguationData":[OSD([sQuery(id+"F0.wireOp",EDGE,"E0")])]}),"instanceName":"1"}),"instanceName":"1"});
            var Q7;
            Q7=makeQuery(id+"F11.opPattern","COPY",BODY,{"derivedFrom":makeQuery(id+"F9.opPattern","COPY",BODY,{"derivedFrom":makeQuery(id+"F4.opPattern","COPY",BODY,{"derivedFrom":makeQuery(id+"F1.opExtrude","SWEPT_BODY",BODY,{"disambiguationData":[OSD([sQuery(id+"F0.wireOp",EDGE,"E0")])]}),"instanceName":"1"}),"instanceName":"1"}),"instanceName":"1"});
            var Q8;
            Q8=makeQuery(id+"F11.opPattern","COPY",BODY,{"derivedFrom":makeQuery(id+"F1.opExtrude","SWEPT_BODY",BODY,{"disambiguationData":[OSD([sQuery(id+"F0.wireOp",EDGE,"E0")])]}),"instanceName":"1"});
            var Q9;
            Q9=makeQuery(id+"F11.opPattern","COPY",BODY,{"derivedFrom":makeQuery(id+"F4.opPattern","COPY",BODY,{"derivedFrom":makeQuery(id+"F1.opExtrude","SWEPT_BODY",BODY,{"disambiguationData":[OSD([sQuery(id+"F0.wireOp",EDGE,"E0")])]}),"instanceName":"1"}),"instanceName":"1"});
            var Q10;
            Q10=makeQuery(id+"F12.opPattern","COPY",BODY,{"derivedFrom":makeQuery(id+"F9.opPattern","COPY",BODY,{"derivedFrom":makeQuery(id+"F1.opExtrude","SWEPT_BODY",BODY,{"disambiguationData":[OSD([sQuery(id+"F0.wireOp",EDGE,"E0")])]}),"instanceName":"1"}),"instanceName":"1"});
            var Q11;
            Q11=makeQuery(id+"F12.opPattern","COPY",BODY,{"derivedFrom":makeQuery(id+"F9.opPattern","COPY",BODY,{"derivedFrom":makeQuery(id+"F4.opPattern","COPY",BODY,{"derivedFrom":makeQuery(id+"F1.opExtrude","SWEPT_BODY",BODY,{"disambiguationData":[OSD([sQuery(id+"F0.wireOp",EDGE,"E0")])]}),"instanceName":"1"}),"instanceName":"1"}),"instanceName":"1"});
            var Q12;
            Q12=makeQuery(id+"F12.opPattern","COPY",BODY,{"derivedFrom":makeQuery(id+"F11.opPattern","COPY",BODY,{"derivedFrom":makeQuery(id+"F1.opExtrude","SWEPT_BODY",BODY,{"disambiguationData":[OSD([sQuery(id+"F0.wireOp",EDGE,"E0")])]}),"instanceName":"1"}),"instanceName":"1"});
            var Q13;
            Q13=makeQuery(id+"F12.opPattern","COPY",BODY,{"derivedFrom":makeQuery(id+"F11.opPattern","COPY",BODY,{"derivedFrom":makeQuery(id+"F9.opPattern","COPY",BODY,{"derivedFrom":makeQuery(id+"F4.opPattern","COPY",BODY,{"derivedFrom":makeQuery(id+"F1.opExtrude","SWEPT_BODY",BODY,{"disambiguationData":[OSD([sQuery(id+"F0.wireOp",EDGE,"E0")])]}),"instanceName":"1"}),"instanceName":"1"}),"instanceName":"1"}),"instanceName":"1"});
            var Q14;
            Q14=makeQuery(id+"F12.opPattern","COPY",BODY,{"derivedFrom":makeQuery(id+"F10.opPattern","COPY",BODY,{"derivedFrom":makeQuery(id+"F1.opExtrude","SWEPT_BODY",BODY,{"disambiguationData":[OSD([sQuery(id+"F0.wireOp",EDGE,"E0")])]}),"instanceName":"1"}),"instanceName":"1"});
            var Q15;
            Q15=makeQuery(id+"F12.opPattern","COPY",BODY,{"derivedFrom":makeQuery(id+"F11.opPattern","COPY",BODY,{"derivedFrom":makeQuery(id+"F9.opPattern","COPY",BODY,{"derivedFrom":makeQuery(id+"F1.opExtrude","SWEPT_BODY",BODY,{"disambiguationData":[OSD([sQuery(id+"F0.wireOp",EDGE,"E0")])]}),"instanceName":"1"}),"instanceName":"1"}),"instanceName":"1"});
            var Q16;
            Q16=makeQuery(id+"F12.opPattern","COPY",BODY,{"derivedFrom":makeQuery(id+"F11.opPattern","COPY",BODY,{"derivedFrom":makeQuery(id+"F4.opPattern","COPY",BODY,{"derivedFrom":makeQuery(id+"F1.opExtrude","SWEPT_BODY",BODY,{"disambiguationData":[OSD([sQuery(id+"F0.wireOp",EDGE,"E0")])]}),"instanceName":"1"}),"instanceName":"1"}),"instanceName":"1"});
            var Q17;
            Q17=makeQuery(id+"F12.opPattern","COPY",BODY,{"derivedFrom":makeQuery(id+"F11.opPattern","COPY",BODY,{"derivedFrom":makeQuery(id+"F10.opPattern","COPY",BODY,{"derivedFrom":makeQuery(id+"F1.opExtrude","SWEPT_BODY",BODY,{"disambiguationData":[OSD([sQuery(id+"F0.wireOp",EDGE,"E0")])]}),"instanceName":"1"}),"instanceName":"1"}),"instanceName":"1"});
            var Q18;
            Q18=makeQuery(id+"F12.opPattern","COPY",BODY,{"derivedFrom":makeQuery(id+"F1.opExtrude","SWEPT_BODY",BODY,{"disambiguationData":[OSD([sQuery(id+"F0.wireOp",EDGE,"E0")])]}),"instanceName":"1"});
            var Q19;
            Q19=makeQuery(id+"F12.opPattern","COPY",BODY,{"derivedFrom":makeQuery(id+"F4.opPattern","COPY",BODY,{"derivedFrom":makeQuery(id+"F1.opExtrude","SWEPT_BODY",BODY,{"disambiguationData":[OSD([sQuery(id+"F0.wireOp",EDGE,"E0")])]}),"instanceName":"1"}),"instanceName":"1"});
            var Q20;
            Q20=makeQuery(id+"F14.opPattern","COPY",BODY,{"derivedFrom":makeQuery(id+"F11.opPattern","COPY",BODY,{"derivedFrom":makeQuery(id+"F1.opExtrude","SWEPT_BODY",BODY,{"disambiguationData":[OSD([sQuery(id+"F0.wireOp",EDGE,"E0")])]}),"instanceName":"1"}),"instanceName":"1"});
            var Q21;
            Q21=makeQuery(id+"F14.opPattern","COPY",BODY,{"derivedFrom":makeQuery(id+"F11.opPattern","COPY",BODY,{"derivedFrom":makeQuery(id+"F10.opPattern","COPY",BODY,{"derivedFrom":makeQuery(id+"F1.opExtrude","SWEPT_BODY",BODY,{"disambiguationData":[OSD([sQuery(id+"F0.wireOp",EDGE,"E0")])]}),"instanceName":"1"}),"instanceName":"1"}),"instanceName":"1"});
            var Q22;
            Q22=makeQuery(id+"F14.opPattern","COPY",BODY,{"derivedFrom":makeQuery(id+"F11.opPattern","COPY",BODY,{"derivedFrom":makeQuery(id+"F9.opPattern","COPY",BODY,{"derivedFrom":makeQuery(id+"F1.opExtrude","SWEPT_BODY",BODY,{"disambiguationData":[OSD([sQuery(id+"F0.wireOp",EDGE,"E0")])]}),"instanceName":"1"}),"instanceName":"1"}),"instanceName":"1"});
            var Q23;
            Q23=makeQuery(id+"F14.opPattern","COPY",BODY,{"derivedFrom":makeQuery(id+"F11.opPattern","COPY",BODY,{"derivedFrom":makeQuery(id+"F9.opPattern","COPY",BODY,{"derivedFrom":makeQuery(id+"F4.opPattern","COPY",BODY,{"derivedFrom":makeQuery(id+"F1.opExtrude","SWEPT_BODY",BODY,{"disambiguationData":[OSD([sQuery(id+"F0.wireOp",EDGE,"E0")])]}),"instanceName":"1"}),"instanceName":"1"}),"instanceName":"1"}),"instanceName":"1"});
            var Q24;
            Q24=makeQuery(id+"F14.opPattern","COPY",BODY,{"derivedFrom":makeQuery(id+"F11.opPattern","COPY",BODY,{"derivedFrom":makeQuery(id+"F4.opPattern","COPY",BODY,{"derivedFrom":makeQuery(id+"F1.opExtrude","SWEPT_BODY",BODY,{"disambiguationData":[OSD([sQuery(id+"F0.wireOp",EDGE,"E0")])]}),"instanceName":"1"}),"instanceName":"1"}),"instanceName":"1"});
            var Q25;
            Q25=makeQuery(id+"F14.opPattern","COPY",BODY,{"derivedFrom":makeQuery(id+"F10.opPattern","COPY",BODY,{"derivedFrom":makeQuery(id+"F1.opExtrude","SWEPT_BODY",BODY,{"disambiguationData":[OSD([sQuery(id+"F0.wireOp",EDGE,"E0")])]}),"instanceName":"1"}),"instanceName":"1"});
            var Q26;
            Q26=makeQuery(id+"F14.opPattern","COPY",BODY,{"derivedFrom":makeQuery(id+"F1.opExtrude","SWEPT_BODY",BODY,{"disambiguationData":[OSD([sQuery(id+"F0.wireOp",EDGE,"E0")])]}),"instanceName":"1"});
            var Q27;
            Q27=makeQuery(id+"F14.opPattern","COPY",BODY,{"derivedFrom":makeQuery(id+"F4.opPattern","COPY",BODY,{"derivedFrom":makeQuery(id+"F1.opExtrude","SWEPT_BODY",BODY,{"disambiguationData":[OSD([sQuery(id+"F0.wireOp",EDGE,"E0")])]}),"instanceName":"1"}),"instanceName":"1"});
            var Q28;
            Q28=makeQuery(id+"F15.opPattern","COPY",BODY,{"derivedFrom":makeQuery(id+"F12.opPattern","COPY",BODY,{"derivedFrom":makeQuery(id+"F11.opPattern","COPY",BODY,{"derivedFrom":makeQuery(id+"F9.opPattern","COPY",BODY,{"derivedFrom":makeQuery(id+"F4.opPattern","COPY",BODY,{"derivedFrom":makeQuery(id+"F1.opExtrude","SWEPT_BODY",BODY,{"disambiguationData":[OSD([sQuery(id+"F0.wireOp",EDGE,"E0")])]}),"instanceName":"1"}),"instanceName":"1"}),"instanceName":"1"}),"instanceName":"1"}),"instanceName":"1"});
            var Q29;
            Q29=makeQuery(id+"F15.opPattern","COPY",BODY,{"derivedFrom":makeQuery(id+"F12.opPattern","COPY",BODY,{"derivedFrom":makeQuery(id+"F11.opPattern","COPY",BODY,{"derivedFrom":makeQuery(id+"F1.opExtrude","SWEPT_BODY",BODY,{"disambiguationData":[OSD([sQuery(id+"F0.wireOp",EDGE,"E0")])]}),"instanceName":"1"}),"instanceName":"1"}),"instanceName":"1"});
            var Q30;
            Q30=makeQuery(id+"F15.opPattern","COPY",BODY,{"derivedFrom":makeQuery(id+"F12.opPattern","COPY",BODY,{"derivedFrom":makeQuery(id+"F1.opExtrude","SWEPT_BODY",BODY,{"disambiguationData":[OSD([sQuery(id+"F0.wireOp",EDGE,"E0")])]}),"instanceName":"1"}),"instanceName":"1"});
            var Q31;
            Q31=makeQuery(id+"F15.opPattern","COPY",BODY,{"derivedFrom":makeQuery(id+"F12.opPattern","COPY",BODY,{"derivedFrom":makeQuery(id+"F9.opPattern","COPY",BODY,{"derivedFrom":makeQuery(id+"F4.opPattern","COPY",BODY,{"derivedFrom":makeQuery(id+"F1.opExtrude","SWEPT_BODY",BODY,{"disambiguationData":[OSD([sQuery(id+"F0.wireOp",EDGE,"E0")])]}),"instanceName":"1"}),"instanceName":"1"}),"instanceName":"1"}),"instanceName":"1"});
            var Q32;
            Q32=makeQuery(id+"F15.opPattern","COPY",BODY,{"derivedFrom":makeQuery(id+"F11.opPattern","COPY",BODY,{"derivedFrom":makeQuery(id+"F9.opPattern","COPY",BODY,{"derivedFrom":makeQuery(id+"F1.opExtrude","SWEPT_BODY",BODY,{"disambiguationData":[OSD([sQuery(id+"F0.wireOp",EDGE,"E0")])]}),"instanceName":"1"}),"instanceName":"1"}),"instanceName":"1"});
            var Q33;
            Q33=makeQuery(id+"F15.opPattern","COPY",BODY,{"derivedFrom":makeQuery(id+"F9.opPattern","COPY",BODY,{"derivedFrom":makeQuery(id+"F1.opExtrude","SWEPT_BODY",BODY,{"disambiguationData":[OSD([sQuery(id+"F0.wireOp",EDGE,"E0")])]}),"instanceName":"1"}),"instanceName":"1"});
            var Q34;
            Q34=makeQuery(id+"F15.opPattern","COPY",BODY,{"derivedFrom":makeQuery(id+"F12.opPattern","COPY",BODY,{"derivedFrom":makeQuery(id+"F10.opPattern","COPY",BODY,{"derivedFrom":makeQuery(id+"F1.opExtrude","SWEPT_BODY",BODY,{"disambiguationData":[OSD([sQuery(id+"F0.wireOp",EDGE,"E0")])]}),"instanceName":"1"}),"instanceName":"1"}),"instanceName":"1"});
            var Q35;
            Q35=makeQuery(id+"F15.opPattern","COPY",BODY,{"derivedFrom":makeQuery(id+"F12.opPattern","COPY",BODY,{"derivedFrom":makeQuery(id+"F11.opPattern","COPY",BODY,{"derivedFrom":makeQuery(id+"F9.opPattern","COPY",BODY,{"derivedFrom":makeQuery(id+"F1.opExtrude","SWEPT_BODY",BODY,{"disambiguationData":[OSD([sQuery(id+"F0.wireOp",EDGE,"E0")])]}),"instanceName":"1"}),"instanceName":"1"}),"instanceName":"1"}),"instanceName":"1"});
            var Q36;
            Q36=makeQuery(id+"F15.opPattern","COPY",BODY,{"derivedFrom":makeQuery(id+"F14.opPattern","COPY",BODY,{"derivedFrom":makeQuery(id+"F11.opPattern","COPY",BODY,{"derivedFrom":makeQuery(id+"F10.opPattern","COPY",BODY,{"derivedFrom":makeQuery(id+"F1.opExtrude","SWEPT_BODY",BODY,{"disambiguationData":[OSD([sQuery(id+"F0.wireOp",EDGE,"E0")])]}),"instanceName":"1"}),"instanceName":"1"}),"instanceName":"1"}),"instanceName":"1"});
            var Q37;
            Q37=makeQuery(id+"F15.opPattern","COPY",BODY,{"derivedFrom":makeQuery(id+"F14.opPattern","COPY",BODY,{"derivedFrom":makeQuery(id+"F11.opPattern","COPY",BODY,{"derivedFrom":makeQuery(id+"F9.opPattern","COPY",BODY,{"derivedFrom":makeQuery(id+"F1.opExtrude","SWEPT_BODY",BODY,{"disambiguationData":[OSD([sQuery(id+"F0.wireOp",EDGE,"E0")])]}),"instanceName":"1"}),"instanceName":"1"}),"instanceName":"1"}),"instanceName":"1"});
            var Q38;
            Q38=makeQuery(id+"F15.opPattern","COPY",BODY,{"derivedFrom":makeQuery(id+"F14.opPattern","COPY",BODY,{"derivedFrom":makeQuery(id+"F4.opPattern","COPY",BODY,{"derivedFrom":makeQuery(id+"F1.opExtrude","SWEPT_BODY",BODY,{"disambiguationData":[OSD([sQuery(id+"F0.wireOp",EDGE,"E0")])]}),"instanceName":"1"}),"instanceName":"1"}),"instanceName":"1"});
            var Q39;
            Q39=makeQuery(id+"F15.opPattern","COPY",BODY,{"derivedFrom":makeQuery(id+"F11.opPattern","COPY",BODY,{"derivedFrom":makeQuery(id+"F4.opPattern","COPY",BODY,{"derivedFrom":makeQuery(id+"F1.opExtrude","SWEPT_BODY",BODY,{"disambiguationData":[OSD([sQuery(id+"F0.wireOp",EDGE,"E0")])]}),"instanceName":"1"}),"instanceName":"1"}),"instanceName":"1"});
            var Q40;
            Q40=makeQuery(id+"F15.opPattern","COPY",BODY,{"derivedFrom":makeQuery(id+"F14.opPattern","COPY",BODY,{"derivedFrom":makeQuery(id+"F11.opPattern","COPY",BODY,{"derivedFrom":makeQuery(id+"F9.opPattern","COPY",BODY,{"derivedFrom":makeQuery(id+"F4.opPattern","COPY",BODY,{"derivedFrom":makeQuery(id+"F1.opExtrude","SWEPT_BODY",BODY,{"disambiguationData":[OSD([sQuery(id+"F0.wireOp",EDGE,"E0")])]}),"instanceName":"1"}),"instanceName":"1"}),"instanceName":"1"}),"instanceName":"1"}),"instanceName":"1"});
            var Q41;
            Q41=makeQuery(id+"F15.opPattern","COPY",BODY,{"derivedFrom":makeQuery(id+"F14.opPattern","COPY",BODY,{"derivedFrom":makeQuery(id+"F1.opExtrude","SWEPT_BODY",BODY,{"disambiguationData":[OSD([sQuery(id+"F0.wireOp",EDGE,"E0")])]}),"instanceName":"1"}),"instanceName":"1"});
            var Q42;
            Q42=makeQuery(id+"F15.opPattern","COPY",BODY,{"derivedFrom":makeQuery(id+"F11.opPattern","COPY",BODY,{"derivedFrom":makeQuery(id+"F9.opPattern","COPY",BODY,{"derivedFrom":makeQuery(id+"F4.opPattern","COPY",BODY,{"derivedFrom":makeQuery(id+"F1.opExtrude","SWEPT_BODY",BODY,{"disambiguationData":[OSD([sQuery(id+"F0.wireOp",EDGE,"E0")])]}),"instanceName":"1"}),"instanceName":"1"}),"instanceName":"1"}),"instanceName":"1"});
            var Q43;
            Q43=makeQuery(id+"F15.opPattern","COPY",BODY,{"derivedFrom":makeQuery(id+"F10.opPattern","COPY",BODY,{"derivedFrom":makeQuery(id+"F1.opExtrude","SWEPT_BODY",BODY,{"disambiguationData":[OSD([sQuery(id+"F0.wireOp",EDGE,"E0")])]}),"instanceName":"1"}),"instanceName":"1"});
            var Q44;
            Q44=makeQuery(id+"F15.opPattern","COPY",BODY,{"derivedFrom":makeQuery(id+"F11.opPattern","COPY",BODY,{"derivedFrom":makeQuery(id+"F1.opExtrude","SWEPT_BODY",BODY,{"disambiguationData":[OSD([sQuery(id+"F0.wireOp",EDGE,"E0")])]}),"instanceName":"1"}),"instanceName":"1"});
            var Q45;
            Q45=makeQuery(id+"F15.opPattern","COPY",BODY,{"derivedFrom":makeQuery(id+"F9.opPattern","COPY",BODY,{"derivedFrom":makeQuery(id+"F4.opPattern","COPY",BODY,{"derivedFrom":makeQuery(id+"F1.opExtrude","SWEPT_BODY",BODY,{"disambiguationData":[OSD([sQuery(id+"F0.wireOp",EDGE,"E0")])]}),"instanceName":"1"}),"instanceName":"1"}),"instanceName":"1"});
            var Q46;
            Q46=makeQuery(id+"F15.opPattern","COPY",BODY,{"derivedFrom":makeQuery(id+"F14.opPattern","COPY",BODY,{"derivedFrom":makeQuery(id+"F10.opPattern","COPY",BODY,{"derivedFrom":makeQuery(id+"F1.opExtrude","SWEPT_BODY",BODY,{"disambiguationData":[OSD([sQuery(id+"F0.wireOp",EDGE,"E0")])]}),"instanceName":"1"}),"instanceName":"1"}),"instanceName":"1"});
            var Q47;
            Q47=makeQuery(id+"F15.opPattern","COPY",BODY,{"derivedFrom":makeQuery(id+"F12.opPattern","COPY",BODY,{"derivedFrom":makeQuery(id+"F4.opPattern","COPY",BODY,{"derivedFrom":makeQuery(id+"F1.opExtrude","SWEPT_BODY",BODY,{"disambiguationData":[OSD([sQuery(id+"F0.wireOp",EDGE,"E0")])]}),"instanceName":"1"}),"instanceName":"1"}),"instanceName":"1"});
            var Q48;
            Q48=makeQuery(id+"F15.opPattern","COPY",BODY,{"derivedFrom":makeQuery(id+"F14.opPattern","COPY",BODY,{"derivedFrom":makeQuery(id+"F11.opPattern","COPY",BODY,{"derivedFrom":makeQuery(id+"F4.opPattern","COPY",BODY,{"derivedFrom":makeQuery(id+"F1.opExtrude","SWEPT_BODY",BODY,{"disambiguationData":[OSD([sQuery(id+"F0.wireOp",EDGE,"E0")])]}),"instanceName":"1"}),"instanceName":"1"}),"instanceName":"1"}),"instanceName":"1"});
            var Q49;
            Q49=makeQuery(id+"F15.opPattern","COPY",BODY,{"derivedFrom":makeQuery(id+"F1.opExtrude","SWEPT_BODY",BODY,{"disambiguationData":[OSD([sQuery(id+"F0.wireOp",EDGE,"E0")])]}),"instanceName":"1"});
            var Q50;
            Q50=makeQuery(id+"F15.opPattern","COPY",BODY,{"derivedFrom":makeQuery(id+"F4.opPattern","COPY",BODY,{"derivedFrom":makeQuery(id+"F1.opExtrude","SWEPT_BODY",BODY,{"disambiguationData":[OSD([sQuery(id+"F0.wireOp",EDGE,"E0")])]}),"instanceName":"1"}),"instanceName":"1"});
            var Q51;
            Q51=makeQuery(id+"F15.opPattern","COPY",BODY,{"derivedFrom":makeQuery(id+"F12.opPattern","COPY",BODY,{"derivedFrom":makeQuery(id+"F9.opPattern","COPY",BODY,{"derivedFrom":makeQuery(id+"F1.opExtrude","SWEPT_BODY",BODY,{"disambiguationData":[OSD([sQuery(id+"F0.wireOp",EDGE,"E0")])]}),"instanceName":"1"}),"instanceName":"1"}),"instanceName":"1"});
            var Q52;
            Q52=makeQuery(id+"F15.opPattern","COPY",BODY,{"derivedFrom":makeQuery(id+"F12.opPattern","COPY",BODY,{"derivedFrom":makeQuery(id+"F11.opPattern","COPY",BODY,{"derivedFrom":makeQuery(id+"F10.opPattern","COPY",BODY,{"derivedFrom":makeQuery(id+"F1.opExtrude","SWEPT_BODY",BODY,{"disambiguationData":[OSD([sQuery(id+"F0.wireOp",EDGE,"E0")])]}),"instanceName":"1"}),"instanceName":"1"}),"instanceName":"1"}),"instanceName":"1"});
            var Q53;
            Q53=makeQuery(id+"F15.opPattern","COPY",BODY,{"derivedFrom":makeQuery(id+"F14.opPattern","COPY",BODY,{"derivedFrom":makeQuery(id+"F11.opPattern","COPY",BODY,{"derivedFrom":makeQuery(id+"F1.opExtrude","SWEPT_BODY",BODY,{"disambiguationData":[OSD([sQuery(id+"F0.wireOp",EDGE,"E0")])]}),"instanceName":"1"}),"instanceName":"1"}),"instanceName":"1"});
            var Q54;
            Q54=makeQuery(id+"F15.opPattern","COPY",BODY,{"derivedFrom":makeQuery(id+"F12.opPattern","COPY",BODY,{"derivedFrom":makeQuery(id+"F11.opPattern","COPY",BODY,{"derivedFrom":makeQuery(id+"F4.opPattern","COPY",BODY,{"derivedFrom":makeQuery(id+"F1.opExtrude","SWEPT_BODY",BODY,{"disambiguationData":[OSD([sQuery(id+"F0.wireOp",EDGE,"E0")])]}),"instanceName":"1"}),"instanceName":"1"}),"instanceName":"1"}),"instanceName":"1"});
            var Q55;
            Q55=makeQuery(id+"F15.opPattern","COPY",BODY,{"derivedFrom":makeQuery(id+"F11.opPattern","COPY",BODY,{"derivedFrom":makeQuery(id+"F10.opPattern","COPY",BODY,{"derivedFrom":makeQuery(id+"F1.opExtrude","SWEPT_BODY",BODY,{"disambiguationData":[OSD([sQuery(id+"F0.wireOp",EDGE,"E0")])]}),"instanceName":"1"}),"instanceName":"1"}),"instanceName":"1"});
            var Q56;
            Q56=makeQuery(id+"F16.opPattern","COPY",BODY,{"derivedFrom":makeQuery(id+"F12.opPattern","COPY",BODY,{"derivedFrom":makeQuery(id+"F9.opPattern","COPY",BODY,{"derivedFrom":makeQuery(id+"F1.opExtrude","SWEPT_BODY",BODY,{"disambiguationData":[OSD([sQuery(id+"F0.wireOp",EDGE,"E0")])]}),"instanceName":"1"}),"instanceName":"1"}),"instanceName":"1"});
            var Q57;
            Q57=makeQuery(id+"F16.opPattern","COPY",BODY,{"derivedFrom":makeQuery(id+"F12.opPattern","COPY",BODY,{"derivedFrom":makeQuery(id+"F10.opPattern","COPY",BODY,{"derivedFrom":makeQuery(id+"F1.opExtrude","SWEPT_BODY",BODY,{"disambiguationData":[OSD([sQuery(id+"F0.wireOp",EDGE,"E0")])]}),"instanceName":"1"}),"instanceName":"1"}),"instanceName":"1"});
            var Q58;
            Q58=makeQuery(id+"F16.opPattern","COPY",BODY,{"derivedFrom":makeQuery(id+"F11.opPattern","COPY",BODY,{"derivedFrom":makeQuery(id+"F4.opPattern","COPY",BODY,{"derivedFrom":makeQuery(id+"F1.opExtrude","SWEPT_BODY",BODY,{"disambiguationData":[OSD([sQuery(id+"F0.wireOp",EDGE,"E0")])]}),"instanceName":"1"}),"instanceName":"1"}),"instanceName":"1"});
            var Q59;
            Q59=makeQuery(id+"F16.opPattern","COPY",BODY,{"derivedFrom":makeQuery(id+"F9.opPattern","COPY",BODY,{"derivedFrom":makeQuery(id+"F4.opPattern","COPY",BODY,{"derivedFrom":makeQuery(id+"F1.opExtrude","SWEPT_BODY",BODY,{"disambiguationData":[OSD([sQuery(id+"F0.wireOp",EDGE,"E0")])]}),"instanceName":"1"}),"instanceName":"1"}),"instanceName":"1"});
            var Q60;
            Q60=makeQuery(id+"F16.opPattern","COPY",BODY,{"derivedFrom":makeQuery(id+"F11.opPattern","COPY",BODY,{"derivedFrom":makeQuery(id+"F1.opExtrude","SWEPT_BODY",BODY,{"disambiguationData":[OSD([sQuery(id+"F0.wireOp",EDGE,"E0")])]}),"instanceName":"1"}),"instanceName":"1"});
            var Q61;
            Q61=makeQuery(id+"F16.opPattern","COPY",BODY,{"derivedFrom":makeQuery(id+"F11.opPattern","COPY",BODY,{"derivedFrom":makeQuery(id+"F9.opPattern","COPY",BODY,{"derivedFrom":makeQuery(id+"F4.opPattern","COPY",BODY,{"derivedFrom":makeQuery(id+"F1.opExtrude","SWEPT_BODY",BODY,{"disambiguationData":[OSD([sQuery(id+"F0.wireOp",EDGE,"E0")])]}),"instanceName":"1"}),"instanceName":"1"}),"instanceName":"1"}),"instanceName":"1"});
            var Q62;
            Q62=makeQuery(id+"F16.opPattern","COPY",BODY,{"derivedFrom":makeQuery(id+"F15.opPattern","COPY",BODY,{"derivedFrom":makeQuery(id+"F12.opPattern","COPY",BODY,{"derivedFrom":makeQuery(id+"F9.opPattern","COPY",BODY,{"derivedFrom":makeQuery(id+"F1.opExtrude","SWEPT_BODY",BODY,{"disambiguationData":[OSD([sQuery(id+"F0.wireOp",EDGE,"E0")])]}),"instanceName":"1"}),"instanceName":"1"}),"instanceName":"1"}),"instanceName":"1"});
            var Q63;
            Q63=makeQuery(id+"F16.opPattern","COPY",BODY,{"derivedFrom":makeQuery(id+"F14.opPattern","COPY",BODY,{"derivedFrom":makeQuery(id+"F11.opPattern","COPY",BODY,{"derivedFrom":makeQuery(id+"F9.opPattern","COPY",BODY,{"derivedFrom":makeQuery(id+"F1.opExtrude","SWEPT_BODY",BODY,{"disambiguationData":[OSD([sQuery(id+"F0.wireOp",EDGE,"E0")])]}),"instanceName":"1"}),"instanceName":"1"}),"instanceName":"1"}),"instanceName":"1"});
            var Q64;
            Q64=makeQuery(id+"F16.opPattern","COPY",BODY,{"derivedFrom":makeQuery(id+"F15.opPattern","COPY",BODY,{"derivedFrom":makeQuery(id+"F14.opPattern","COPY",BODY,{"derivedFrom":makeQuery(id+"F1.opExtrude","SWEPT_BODY",BODY,{"disambiguationData":[OSD([sQuery(id+"F0.wireOp",EDGE,"E0")])]}),"instanceName":"1"}),"instanceName":"1"}),"instanceName":"1"});
            var Q65;
            Q65=makeQuery(id+"F16.opPattern","COPY",BODY,{"derivedFrom":makeQuery(id+"F15.opPattern","COPY",BODY,{"derivedFrom":makeQuery(id+"F12.opPattern","COPY",BODY,{"derivedFrom":makeQuery(id+"F1.opExtrude","SWEPT_BODY",BODY,{"disambiguationData":[OSD([sQuery(id+"F0.wireOp",EDGE,"E0")])]}),"instanceName":"1"}),"instanceName":"1"}),"instanceName":"1"});
            var Q66;
            Q66=makeQuery(id+"F16.opPattern","COPY",BODY,{"derivedFrom":makeQuery(id+"F14.opPattern","COPY",BODY,{"derivedFrom":makeQuery(id+"F11.opPattern","COPY",BODY,{"derivedFrom":makeQuery(id+"F4.opPattern","COPY",BODY,{"derivedFrom":makeQuery(id+"F1.opExtrude","SWEPT_BODY",BODY,{"disambiguationData":[OSD([sQuery(id+"F0.wireOp",EDGE,"E0")])]}),"instanceName":"1"}),"instanceName":"1"}),"instanceName":"1"}),"instanceName":"1"});
            var Q67;
            Q67=makeQuery(id+"F16.opPattern","COPY",BODY,{"derivedFrom":makeQuery(id+"F15.opPattern","COPY",BODY,{"derivedFrom":makeQuery(id+"F11.opPattern","COPY",BODY,{"derivedFrom":makeQuery(id+"F4.opPattern","COPY",BODY,{"derivedFrom":makeQuery(id+"F1.opExtrude","SWEPT_BODY",BODY,{"disambiguationData":[OSD([sQuery(id+"F0.wireOp",EDGE,"E0")])]}),"instanceName":"1"}),"instanceName":"1"}),"instanceName":"1"}),"instanceName":"1"});
            var Q68;
            Q68=makeQuery(id+"F16.opPattern","COPY",BODY,{"derivedFrom":makeQuery(id+"F15.opPattern","COPY",BODY,{"derivedFrom":makeQuery(id+"F9.opPattern","COPY",BODY,{"derivedFrom":makeQuery(id+"F4.opPattern","COPY",BODY,{"derivedFrom":makeQuery(id+"F1.opExtrude","SWEPT_BODY",BODY,{"disambiguationData":[OSD([sQuery(id+"F0.wireOp",EDGE,"E0")])]}),"instanceName":"1"}),"instanceName":"1"}),"instanceName":"1"}),"instanceName":"1"});
            var Q69;
            Q69=makeQuery(id+"F16.opPattern","COPY",BODY,{"derivedFrom":makeQuery(id+"F15.opPattern","COPY",BODY,{"derivedFrom":makeQuery(id+"F12.opPattern","COPY",BODY,{"derivedFrom":makeQuery(id+"F11.opPattern","COPY",BODY,{"derivedFrom":makeQuery(id+"F4.opPattern","COPY",BODY,{"derivedFrom":makeQuery(id+"F1.opExtrude","SWEPT_BODY",BODY,{"disambiguationData":[OSD([sQuery(id+"F0.wireOp",EDGE,"E0")])]}),"instanceName":"1"}),"instanceName":"1"}),"instanceName":"1"}),"instanceName":"1"}),"instanceName":"1"});
            var Q70;
            Q70=makeQuery(id+"F16.opPattern","COPY",BODY,{"derivedFrom":makeQuery(id+"F15.opPattern","COPY",BODY,{"derivedFrom":makeQuery(id+"F11.opPattern","COPY",BODY,{"derivedFrom":makeQuery(id+"F10.opPattern","COPY",BODY,{"derivedFrom":makeQuery(id+"F1.opExtrude","SWEPT_BODY",BODY,{"disambiguationData":[OSD([sQuery(id+"F0.wireOp",EDGE,"E0")])]}),"instanceName":"1"}),"instanceName":"1"}),"instanceName":"1"}),"instanceName":"1"});
            var Q71;
            Q71=makeQuery(id+"F16.opPattern","COPY",BODY,{"derivedFrom":makeQuery(id+"F15.opPattern","COPY",BODY,{"derivedFrom":makeQuery(id+"F14.opPattern","COPY",BODY,{"derivedFrom":makeQuery(id+"F11.opPattern","COPY",BODY,{"derivedFrom":makeQuery(id+"F9.opPattern","COPY",BODY,{"derivedFrom":makeQuery(id+"F1.opExtrude","SWEPT_BODY",BODY,{"disambiguationData":[OSD([sQuery(id+"F0.wireOp",EDGE,"E0")])]}),"instanceName":"1"}),"instanceName":"1"}),"instanceName":"1"}),"instanceName":"1"}),"instanceName":"1"});
            var Q72;
            Q72=makeQuery(id+"F16.opPattern","COPY",BODY,{"derivedFrom":makeQuery(id+"F15.opPattern","COPY",BODY,{"derivedFrom":makeQuery(id+"F14.opPattern","COPY",BODY,{"derivedFrom":makeQuery(id+"F11.opPattern","COPY",BODY,{"derivedFrom":makeQuery(id+"F10.opPattern","COPY",BODY,{"derivedFrom":makeQuery(id+"F1.opExtrude","SWEPT_BODY",BODY,{"disambiguationData":[OSD([sQuery(id+"F0.wireOp",EDGE,"E0")])]}),"instanceName":"1"}),"instanceName":"1"}),"instanceName":"1"}),"instanceName":"1"}),"instanceName":"1"});
            var Q73;
            Q73=makeQuery(id+"F16.opPattern","COPY",BODY,{"derivedFrom":makeQuery(id+"F14.opPattern","COPY",BODY,{"derivedFrom":makeQuery(id+"F11.opPattern","COPY",BODY,{"derivedFrom":makeQuery(id+"F10.opPattern","COPY",BODY,{"derivedFrom":makeQuery(id+"F1.opExtrude","SWEPT_BODY",BODY,{"disambiguationData":[OSD([sQuery(id+"F0.wireOp",EDGE,"E0")])]}),"instanceName":"1"}),"instanceName":"1"}),"instanceName":"1"}),"instanceName":"1"});
            var Q74;
            Q74=makeQuery(id+"F16.opPattern","COPY",BODY,{"derivedFrom":makeQuery(id+"F12.opPattern","COPY",BODY,{"derivedFrom":makeQuery(id+"F11.opPattern","COPY",BODY,{"derivedFrom":makeQuery(id+"F10.opPattern","COPY",BODY,{"derivedFrom":makeQuery(id+"F1.opExtrude","SWEPT_BODY",BODY,{"disambiguationData":[OSD([sQuery(id+"F0.wireOp",EDGE,"E0")])]}),"instanceName":"1"}),"instanceName":"1"}),"instanceName":"1"}),"instanceName":"1"});
            var Q75;
            Q75=makeQuery(id+"F16.opPattern","COPY",BODY,{"derivedFrom":makeQuery(id+"F15.opPattern","COPY",BODY,{"derivedFrom":makeQuery(id+"F12.opPattern","COPY",BODY,{"derivedFrom":makeQuery(id+"F11.opPattern","COPY",BODY,{"derivedFrom":makeQuery(id+"F9.opPattern","COPY",BODY,{"derivedFrom":makeQuery(id+"F4.opPattern","COPY",BODY,{"derivedFrom":makeQuery(id+"F1.opExtrude","SWEPT_BODY",BODY,{"disambiguationData":[OSD([sQuery(id+"F0.wireOp",EDGE,"E0")])]}),"instanceName":"1"}),"instanceName":"1"}),"instanceName":"1"}),"instanceName":"1"}),"instanceName":"1"}),"instanceName":"1"});
            var Q76;
            Q76=makeQuery(id+"F16.opPattern","COPY",BODY,{"derivedFrom":makeQuery(id+"F15.opPattern","COPY",BODY,{"derivedFrom":makeQuery(id+"F14.opPattern","COPY",BODY,{"derivedFrom":makeQuery(id+"F11.opPattern","COPY",BODY,{"derivedFrom":makeQuery(id+"F9.opPattern","COPY",BODY,{"derivedFrom":makeQuery(id+"F4.opPattern","COPY",BODY,{"derivedFrom":makeQuery(id+"F1.opExtrude","SWEPT_BODY",BODY,{"disambiguationData":[OSD([sQuery(id+"F0.wireOp",EDGE,"E0")])]}),"instanceName":"1"}),"instanceName":"1"}),"instanceName":"1"}),"instanceName":"1"}),"instanceName":"1"}),"instanceName":"1"});
            var Q77;
            Q77=makeQuery(id+"F16.opPattern","COPY",BODY,{"derivedFrom":makeQuery(id+"F11.opPattern","COPY",BODY,{"derivedFrom":makeQuery(id+"F9.opPattern","COPY",BODY,{"derivedFrom":makeQuery(id+"F1.opExtrude","SWEPT_BODY",BODY,{"disambiguationData":[OSD([sQuery(id+"F0.wireOp",EDGE,"E0")])]}),"instanceName":"1"}),"instanceName":"1"}),"instanceName":"1"});
            var Q78;
            Q78=makeQuery(id+"F16.opPattern","COPY",BODY,{"derivedFrom":makeQuery(id+"F9.opPattern","COPY",BODY,{"derivedFrom":makeQuery(id+"F1.opExtrude","SWEPT_BODY",BODY,{"disambiguationData":[OSD([sQuery(id+"F0.wireOp",EDGE,"E0")])]}),"instanceName":"1"}),"instanceName":"1"});
            var Q79;
            Q79=makeQuery(id+"F16.opPattern","COPY",BODY,{"derivedFrom":makeQuery(id+"F1.opExtrude","SWEPT_BODY",BODY,{"disambiguationData":[OSD([sQuery(id+"F0.wireOp",EDGE,"E0")])]}),"instanceName":"1"});
            var Q80;
            Q80=makeQuery(id+"F16.opPattern","COPY",BODY,{"derivedFrom":makeQuery(id+"F14.opPattern","COPY",BODY,{"derivedFrom":makeQuery(id+"F11.opPattern","COPY",BODY,{"derivedFrom":makeQuery(id+"F9.opPattern","COPY",BODY,{"derivedFrom":makeQuery(id+"F4.opPattern","COPY",BODY,{"derivedFrom":makeQuery(id+"F1.opExtrude","SWEPT_BODY",BODY,{"disambiguationData":[OSD([sQuery(id+"F0.wireOp",EDGE,"E0")])]}),"instanceName":"1"}),"instanceName":"1"}),"instanceName":"1"}),"instanceName":"1"}),"instanceName":"1"});
            var Q81;
            Q81=makeQuery(id+"F16.opPattern","COPY",BODY,{"derivedFrom":makeQuery(id+"F14.opPattern","COPY",BODY,{"derivedFrom":makeQuery(id+"F11.opPattern","COPY",BODY,{"derivedFrom":makeQuery(id+"F1.opExtrude","SWEPT_BODY",BODY,{"disambiguationData":[OSD([sQuery(id+"F0.wireOp",EDGE,"E0")])]}),"instanceName":"1"}),"instanceName":"1"}),"instanceName":"1"});
            var Q82;
            Q82=makeQuery(id+"F16.opPattern","COPY",BODY,{"derivedFrom":makeQuery(id+"F4.opPattern","COPY",BODY,{"derivedFrom":makeQuery(id+"F1.opExtrude","SWEPT_BODY",BODY,{"disambiguationData":[OSD([sQuery(id+"F0.wireOp",EDGE,"E0")])]}),"instanceName":"1"}),"instanceName":"1"});
            var Q83;
            Q83=makeQuery(id+"F16.opPattern","COPY",BODY,{"derivedFrom":makeQuery(id+"F15.opPattern","COPY",BODY,{"derivedFrom":makeQuery(id+"F1.opExtrude","SWEPT_BODY",BODY,{"disambiguationData":[OSD([sQuery(id+"F0.wireOp",EDGE,"E0")])]}),"instanceName":"1"}),"instanceName":"1"});
            var Q84;
            Q84=makeQuery(id+"F16.opPattern","COPY",BODY,{"derivedFrom":makeQuery(id+"F15.opPattern","COPY",BODY,{"derivedFrom":makeQuery(id+"F12.opPattern","COPY",BODY,{"derivedFrom":makeQuery(id+"F9.opPattern","COPY",BODY,{"derivedFrom":makeQuery(id+"F4.opPattern","COPY",BODY,{"derivedFrom":makeQuery(id+"F1.opExtrude","SWEPT_BODY",BODY,{"disambiguationData":[OSD([sQuery(id+"F0.wireOp",EDGE,"E0")])]}),"instanceName":"1"}),"instanceName":"1"}),"instanceName":"1"}),"instanceName":"1"}),"instanceName":"1"});
            var Q85;
            Q85=makeQuery(id+"F16.opPattern","COPY",BODY,{"derivedFrom":makeQuery(id+"F15.opPattern","COPY",BODY,{"derivedFrom":makeQuery(id+"F11.opPattern","COPY",BODY,{"derivedFrom":makeQuery(id+"F9.opPattern","COPY",BODY,{"derivedFrom":makeQuery(id+"F1.opExtrude","SWEPT_BODY",BODY,{"disambiguationData":[OSD([sQuery(id+"F0.wireOp",EDGE,"E0")])]}),"instanceName":"1"}),"instanceName":"1"}),"instanceName":"1"}),"instanceName":"1"});
            var Q86;
            Q86=makeQuery(id+"F16.opPattern","COPY",BODY,{"derivedFrom":makeQuery(id+"F15.opPattern","COPY",BODY,{"derivedFrom":makeQuery(id+"F14.opPattern","COPY",BODY,{"derivedFrom":makeQuery(id+"F4.opPattern","COPY",BODY,{"derivedFrom":makeQuery(id+"F1.opExtrude","SWEPT_BODY",BODY,{"disambiguationData":[OSD([sQuery(id+"F0.wireOp",EDGE,"E0")])]}),"instanceName":"1"}),"instanceName":"1"}),"instanceName":"1"}),"instanceName":"1"});
            var Q87;
            Q87=makeQuery(id+"F16.opPattern","COPY",BODY,{"derivedFrom":makeQuery(id+"F12.opPattern","COPY",BODY,{"derivedFrom":makeQuery(id+"F9.opPattern","COPY",BODY,{"derivedFrom":makeQuery(id+"F4.opPattern","COPY",BODY,{"derivedFrom":makeQuery(id+"F1.opExtrude","SWEPT_BODY",BODY,{"disambiguationData":[OSD([sQuery(id+"F0.wireOp",EDGE,"E0")])]}),"instanceName":"1"}),"instanceName":"1"}),"instanceName":"1"}),"instanceName":"1"});
            var Q88;
            Q88=makeQuery(id+"F16.opPattern","COPY",BODY,{"derivedFrom":makeQuery(id+"F15.opPattern","COPY",BODY,{"derivedFrom":makeQuery(id+"F9.opPattern","COPY",BODY,{"derivedFrom":makeQuery(id+"F1.opExtrude","SWEPT_BODY",BODY,{"disambiguationData":[OSD([sQuery(id+"F0.wireOp",EDGE,"E0")])]}),"instanceName":"1"}),"instanceName":"1"}),"instanceName":"1"});
            var Q89;
            Q89=makeQuery(id+"F16.opPattern","COPY",BODY,{"derivedFrom":makeQuery(id+"F15.opPattern","COPY",BODY,{"derivedFrom":makeQuery(id+"F14.opPattern","COPY",BODY,{"derivedFrom":makeQuery(id+"F11.opPattern","COPY",BODY,{"derivedFrom":makeQuery(id+"F1.opExtrude","SWEPT_BODY",BODY,{"disambiguationData":[OSD([sQuery(id+"F0.wireOp",EDGE,"E0")])]}),"instanceName":"1"}),"instanceName":"1"}),"instanceName":"1"}),"instanceName":"1"});
            var Q90;
            Q90=makeQuery(id+"F16.opPattern","COPY",BODY,{"derivedFrom":makeQuery(id+"F12.opPattern","COPY",BODY,{"derivedFrom":makeQuery(id+"F1.opExtrude","SWEPT_BODY",BODY,{"disambiguationData":[OSD([sQuery(id+"F0.wireOp",EDGE,"E0")])]}),"instanceName":"1"}),"instanceName":"1"});
            var Q91;
            Q91=makeQuery(id+"F16.opPattern","COPY",BODY,{"derivedFrom":makeQuery(id+"F15.opPattern","COPY",BODY,{"derivedFrom":makeQuery(id+"F4.opPattern","COPY",BODY,{"derivedFrom":makeQuery(id+"F1.opExtrude","SWEPT_BODY",BODY,{"disambiguationData":[OSD([sQuery(id+"F0.wireOp",EDGE,"E0")])]}),"instanceName":"1"}),"instanceName":"1"}),"instanceName":"1"});
            var Q92;
            Q92=makeQuery(id+"F16.opPattern","COPY",BODY,{"derivedFrom":makeQuery(id+"F15.opPattern","COPY",BODY,{"derivedFrom":makeQuery(id+"F12.opPattern","COPY",BODY,{"derivedFrom":makeQuery(id+"F10.opPattern","COPY",BODY,{"derivedFrom":makeQuery(id+"F1.opExtrude","SWEPT_BODY",BODY,{"disambiguationData":[OSD([sQuery(id+"F0.wireOp",EDGE,"E0")])]}),"instanceName":"1"}),"instanceName":"1"}),"instanceName":"1"}),"instanceName":"1"});
            var Q93;
            Q93=makeQuery(id+"F16.opPattern","COPY",BODY,{"derivedFrom":makeQuery(id+"F14.opPattern","COPY",BODY,{"derivedFrom":makeQuery(id+"F10.opPattern","COPY",BODY,{"derivedFrom":makeQuery(id+"F1.opExtrude","SWEPT_BODY",BODY,{"disambiguationData":[OSD([sQuery(id+"F0.wireOp",EDGE,"E0")])]}),"instanceName":"1"}),"instanceName":"1"}),"instanceName":"1"});
            var Q94;
            Q94=makeQuery(id+"F16.opPattern","COPY",BODY,{"derivedFrom":makeQuery(id+"F15.opPattern","COPY",BODY,{"derivedFrom":makeQuery(id+"F12.opPattern","COPY",BODY,{"derivedFrom":makeQuery(id+"F11.opPattern","COPY",BODY,{"derivedFrom":makeQuery(id+"F1.opExtrude","SWEPT_BODY",BODY,{"disambiguationData":[OSD([sQuery(id+"F0.wireOp",EDGE,"E0")])]}),"instanceName":"1"}),"instanceName":"1"}),"instanceName":"1"}),"instanceName":"1"});
            var Q95;
            Q95=makeQuery(id+"F16.opPattern","COPY",BODY,{"derivedFrom":makeQuery(id+"F12.opPattern","COPY",BODY,{"derivedFrom":makeQuery(id+"F11.opPattern","COPY",BODY,{"derivedFrom":makeQuery(id+"F9.opPattern","COPY",BODY,{"derivedFrom":makeQuery(id+"F1.opExtrude","SWEPT_BODY",BODY,{"disambiguationData":[OSD([sQuery(id+"F0.wireOp",EDGE,"E0")])]}),"instanceName":"1"}),"instanceName":"1"}),"instanceName":"1"}),"instanceName":"1"});
            var Q96;
            Q96=makeQuery(id+"F16.opPattern","COPY",BODY,{"derivedFrom":makeQuery(id+"F15.opPattern","COPY",BODY,{"derivedFrom":makeQuery(id+"F11.opPattern","COPY",BODY,{"derivedFrom":makeQuery(id+"F9.opPattern","COPY",BODY,{"derivedFrom":makeQuery(id+"F4.opPattern","COPY",BODY,{"derivedFrom":makeQuery(id+"F1.opExtrude","SWEPT_BODY",BODY,{"disambiguationData":[OSD([sQuery(id+"F0.wireOp",EDGE,"E0")])]}),"instanceName":"1"}),"instanceName":"1"}),"instanceName":"1"}),"instanceName":"1"}),"instanceName":"1"});
            var Q97;
            Q97=makeQuery(id+"F16.opPattern","COPY",BODY,{"derivedFrom":makeQuery(id+"F15.opPattern","COPY",BODY,{"derivedFrom":makeQuery(id+"F11.opPattern","COPY",BODY,{"derivedFrom":makeQuery(id+"F1.opExtrude","SWEPT_BODY",BODY,{"disambiguationData":[OSD([sQuery(id+"F0.wireOp",EDGE,"E0")])]}),"instanceName":"1"}),"instanceName":"1"}),"instanceName":"1"});
            var Q98;
            Q98=makeQuery(id+"F16.opPattern","COPY",BODY,{"derivedFrom":makeQuery(id+"F15.opPattern","COPY",BODY,{"derivedFrom":makeQuery(id+"F14.opPattern","COPY",BODY,{"derivedFrom":makeQuery(id+"F11.opPattern","COPY",BODY,{"derivedFrom":makeQuery(id+"F4.opPattern","COPY",BODY,{"derivedFrom":makeQuery(id+"F1.opExtrude","SWEPT_BODY",BODY,{"disambiguationData":[OSD([sQuery(id+"F0.wireOp",EDGE,"E0")])]}),"instanceName":"1"}),"instanceName":"1"}),"instanceName":"1"}),"instanceName":"1"}),"instanceName":"1"});
            var Q99;
            Q99=makeQuery(id+"F16.opPattern","COPY",BODY,{"derivedFrom":makeQuery(id+"F11.opPattern","COPY",BODY,{"derivedFrom":makeQuery(id+"F10.opPattern","COPY",BODY,{"derivedFrom":makeQuery(id+"F1.opExtrude","SWEPT_BODY",BODY,{"disambiguationData":[OSD([sQuery(id+"F0.wireOp",EDGE,"E0")])]}),"instanceName":"1"}),"instanceName":"1"}),"instanceName":"1"});
            var Q100;
            Q100=makeQuery(id+"F16.opPattern","COPY",BODY,{"derivedFrom":makeQuery(id+"F10.opPattern","COPY",BODY,{"derivedFrom":makeQuery(id+"F1.opExtrude","SWEPT_BODY",BODY,{"disambiguationData":[OSD([sQuery(id+"F0.wireOp",EDGE,"E0")])]}),"instanceName":"1"}),"instanceName":"1"});
            var Q101;
            Q101=makeQuery(id+"F16.opPattern","COPY",BODY,{"derivedFrom":makeQuery(id+"F12.opPattern","COPY",BODY,{"derivedFrom":makeQuery(id+"F4.opPattern","COPY",BODY,{"derivedFrom":makeQuery(id+"F1.opExtrude","SWEPT_BODY",BODY,{"disambiguationData":[OSD([sQuery(id+"F0.wireOp",EDGE,"E0")])]}),"instanceName":"1"}),"instanceName":"1"}),"instanceName":"1"});
            var Q102;
            Q102=makeQuery(id+"F16.opPattern","COPY",BODY,{"derivedFrom":makeQuery(id+"F12.opPattern","COPY",BODY,{"derivedFrom":makeQuery(id+"F11.opPattern","COPY",BODY,{"derivedFrom":makeQuery(id+"F4.opPattern","COPY",BODY,{"derivedFrom":makeQuery(id+"F1.opExtrude","SWEPT_BODY",BODY,{"disambiguationData":[OSD([sQuery(id+"F0.wireOp",EDGE,"E0")])]}),"instanceName":"1"}),"instanceName":"1"}),"instanceName":"1"}),"instanceName":"1"});
            var Q103;
            Q103=makeQuery(id+"F16.opPattern","COPY",BODY,{"derivedFrom":makeQuery(id+"F14.opPattern","COPY",BODY,{"derivedFrom":makeQuery(id+"F4.opPattern","COPY",BODY,{"derivedFrom":makeQuery(id+"F1.opExtrude","SWEPT_BODY",BODY,{"disambiguationData":[OSD([sQuery(id+"F0.wireOp",EDGE,"E0")])]}),"instanceName":"1"}),"instanceName":"1"}),"instanceName":"1"});
            var Q104;
            Q104=makeQuery(id+"F16.opPattern","COPY",BODY,{"derivedFrom":makeQuery(id+"F15.opPattern","COPY",BODY,{"derivedFrom":makeQuery(id+"F12.opPattern","COPY",BODY,{"derivedFrom":makeQuery(id+"F11.opPattern","COPY",BODY,{"derivedFrom":makeQuery(id+"F9.opPattern","COPY",BODY,{"derivedFrom":makeQuery(id+"F1.opExtrude","SWEPT_BODY",BODY,{"disambiguationData":[OSD([sQuery(id+"F0.wireOp",EDGE,"E0")])]}),"instanceName":"1"}),"instanceName":"1"}),"instanceName":"1"}),"instanceName":"1"}),"instanceName":"1"});
            var Q105;
            Q105=makeQuery(id+"F16.opPattern","COPY",BODY,{"derivedFrom":makeQuery(id+"F15.opPattern","COPY",BODY,{"derivedFrom":makeQuery(id+"F14.opPattern","COPY",BODY,{"derivedFrom":makeQuery(id+"F10.opPattern","COPY",BODY,{"derivedFrom":makeQuery(id+"F1.opExtrude","SWEPT_BODY",BODY,{"disambiguationData":[OSD([sQuery(id+"F0.wireOp",EDGE,"E0")])]}),"instanceName":"1"}),"instanceName":"1"}),"instanceName":"1"}),"instanceName":"1"});
            var Q106;
            Q106=makeQuery(id+"F16.opPattern","COPY",BODY,{"derivedFrom":makeQuery(id+"F12.opPattern","COPY",BODY,{"derivedFrom":makeQuery(id+"F11.opPattern","COPY",BODY,{"derivedFrom":makeQuery(id+"F9.opPattern","COPY",BODY,{"derivedFrom":makeQuery(id+"F4.opPattern","COPY",BODY,{"derivedFrom":makeQuery(id+"F1.opExtrude","SWEPT_BODY",BODY,{"disambiguationData":[OSD([sQuery(id+"F0.wireOp",EDGE,"E0")])]}),"instanceName":"1"}),"instanceName":"1"}),"instanceName":"1"}),"instanceName":"1"}),"instanceName":"1"});
            var Q107;
            Q107=makeQuery(id+"F16.opPattern","COPY",BODY,{"derivedFrom":makeQuery(id+"F12.opPattern","COPY",BODY,{"derivedFrom":makeQuery(id+"F11.opPattern","COPY",BODY,{"derivedFrom":makeQuery(id+"F1.opExtrude","SWEPT_BODY",BODY,{"disambiguationData":[OSD([sQuery(id+"F0.wireOp",EDGE,"E0")])]}),"instanceName":"1"}),"instanceName":"1"}),"instanceName":"1"});
            var Q108;
            Q108=makeQuery(id+"F16.opPattern","COPY",BODY,{"derivedFrom":makeQuery(id+"F15.opPattern","COPY",BODY,{"derivedFrom":makeQuery(id+"F12.opPattern","COPY",BODY,{"derivedFrom":makeQuery(id+"F11.opPattern","COPY",BODY,{"derivedFrom":makeQuery(id+"F10.opPattern","COPY",BODY,{"derivedFrom":makeQuery(id+"F1.opExtrude","SWEPT_BODY",BODY,{"disambiguationData":[OSD([sQuery(id+"F0.wireOp",EDGE,"E0")])]}),"instanceName":"1"}),"instanceName":"1"}),"instanceName":"1"}),"instanceName":"1"}),"instanceName":"1"});
            var Q109;
            Q109=makeQuery(id+"F16.opPattern","COPY",BODY,{"derivedFrom":makeQuery(id+"F15.opPattern","COPY",BODY,{"derivedFrom":makeQuery(id+"F12.opPattern","COPY",BODY,{"derivedFrom":makeQuery(id+"F4.opPattern","COPY",BODY,{"derivedFrom":makeQuery(id+"F1.opExtrude","SWEPT_BODY",BODY,{"disambiguationData":[OSD([sQuery(id+"F0.wireOp",EDGE,"E0")])]}),"instanceName":"1"}),"instanceName":"1"}),"instanceName":"1"}),"instanceName":"1"});
            var Q110;
            Q110=makeQuery(id+"F16.opPattern","COPY",BODY,{"derivedFrom":makeQuery(id+"F14.opPattern","COPY",BODY,{"derivedFrom":makeQuery(id+"F1.opExtrude","SWEPT_BODY",BODY,{"disambiguationData":[OSD([sQuery(id+"F0.wireOp",EDGE,"E0")])]}),"instanceName":"1"}),"instanceName":"1"});
            var Q111;
            Q111=makeQuery(id+"F16.opPattern","COPY",BODY,{"derivedFrom":makeQuery(id+"F15.opPattern","COPY",BODY,{"derivedFrom":makeQuery(id+"F10.opPattern","COPY",BODY,{"derivedFrom":makeQuery(id+"F1.opExtrude","SWEPT_BODY",BODY,{"disambiguationData":[OSD([sQuery(id+"F0.wireOp",EDGE,"E0")])]}),"instanceName":"1"}),"instanceName":"1"}),"instanceName":"1"});
            var Q112;
            Q112=makeQuery(id+"F17.opPattern","COPY",BODY,{"derivedFrom":makeQuery(id+"F16.opPattern","COPY",BODY,{"derivedFrom":makeQuery(id+"F12.opPattern","COPY",BODY,{"derivedFrom":makeQuery(id+"F11.opPattern","COPY",BODY,{"derivedFrom":makeQuery(id+"F9.opPattern","COPY",BODY,{"derivedFrom":makeQuery(id+"F4.opPattern","COPY",BODY,{"derivedFrom":makeQuery(id+"F1.opExtrude","SWEPT_BODY",BODY,{"disambiguationData":[OSD([sQuery(id+"F0.wireOp",EDGE,"E0")])]}),"instanceName":"1"}),"instanceName":"1"}),"instanceName":"1"}),"instanceName":"1"}),"instanceName":"1"}),"instanceName":"1"});
            var Q113;
            Q113=makeQuery(id+"F17.opPattern","COPY",BODY,{"derivedFrom":makeQuery(id+"F16.opPattern","COPY",BODY,{"derivedFrom":makeQuery(id+"F14.opPattern","COPY",BODY,{"derivedFrom":makeQuery(id+"F11.opPattern","COPY",BODY,{"derivedFrom":makeQuery(id+"F9.opPattern","COPY",BODY,{"derivedFrom":makeQuery(id+"F4.opPattern","COPY",BODY,{"derivedFrom":makeQuery(id+"F1.opExtrude","SWEPT_BODY",BODY,{"disambiguationData":[OSD([sQuery(id+"F0.wireOp",EDGE,"E0")])]}),"instanceName":"1"}),"instanceName":"1"}),"instanceName":"1"}),"instanceName":"1"}),"instanceName":"1"}),"instanceName":"1"});
            var Q114;
            Q114=makeQuery(id+"F17.opPattern","COPY",BODY,{"derivedFrom":makeQuery(id+"F14.opPattern","COPY",BODY,{"derivedFrom":makeQuery(id+"F10.opPattern","COPY",BODY,{"derivedFrom":makeQuery(id+"F1.opExtrude","SWEPT_BODY",BODY,{"disambiguationData":[OSD([sQuery(id+"F0.wireOp",EDGE,"E0")])]}),"instanceName":"1"}),"instanceName":"1"}),"instanceName":"1"});
            var Q115;
            Q115=makeQuery(id+"F17.opPattern","COPY",BODY,{"derivedFrom":makeQuery(id+"F12.opPattern","COPY",BODY,{"derivedFrom":makeQuery(id+"F11.opPattern","COPY",BODY,{"derivedFrom":makeQuery(id+"F1.opExtrude","SWEPT_BODY",BODY,{"disambiguationData":[OSD([sQuery(id+"F0.wireOp",EDGE,"E0")])]}),"instanceName":"1"}),"instanceName":"1"}),"instanceName":"1"});
            var Q116;
            Q116=makeQuery(id+"F17.opPattern","COPY",BODY,{"derivedFrom":makeQuery(id+"F15.opPattern","COPY",BODY,{"derivedFrom":makeQuery(id+"F11.opPattern","COPY",BODY,{"derivedFrom":makeQuery(id+"F4.opPattern","COPY",BODY,{"derivedFrom":makeQuery(id+"F1.opExtrude","SWEPT_BODY",BODY,{"disambiguationData":[OSD([sQuery(id+"F0.wireOp",EDGE,"E0")])]}),"instanceName":"1"}),"instanceName":"1"}),"instanceName":"1"}),"instanceName":"1"});
            var Q117;
            Q117=makeQuery(id+"F17.opPattern","COPY",BODY,{"derivedFrom":makeQuery(id+"F12.opPattern","COPY",BODY,{"derivedFrom":makeQuery(id+"F11.opPattern","COPY",BODY,{"derivedFrom":makeQuery(id+"F9.opPattern","COPY",BODY,{"derivedFrom":makeQuery(id+"F4.opPattern","COPY",BODY,{"derivedFrom":makeQuery(id+"F1.opExtrude","SWEPT_BODY",BODY,{"disambiguationData":[OSD([sQuery(id+"F0.wireOp",EDGE,"E0")])]}),"instanceName":"1"}),"instanceName":"1"}),"instanceName":"1"}),"instanceName":"1"}),"instanceName":"1"});
            var Q118;
            Q118=makeQuery(id+"F17.opPattern","COPY",BODY,{"derivedFrom":makeQuery(id+"F16.opPattern","COPY",BODY,{"derivedFrom":makeQuery(id+"F12.opPattern","COPY",BODY,{"derivedFrom":makeQuery(id+"F9.opPattern","COPY",BODY,{"derivedFrom":makeQuery(id+"F1.opExtrude","SWEPT_BODY",BODY,{"disambiguationData":[OSD([sQuery(id+"F0.wireOp",EDGE,"E0")])]}),"instanceName":"1"}),"instanceName":"1"}),"instanceName":"1"}),"instanceName":"1"});
            var Q119;
            Q119=makeQuery(id+"F17.opPattern","COPY",BODY,{"derivedFrom":makeQuery(id+"F16.opPattern","COPY",BODY,{"derivedFrom":makeQuery(id+"F14.opPattern","COPY",BODY,{"derivedFrom":makeQuery(id+"F1.opExtrude","SWEPT_BODY",BODY,{"disambiguationData":[OSD([sQuery(id+"F0.wireOp",EDGE,"E0")])]}),"instanceName":"1"}),"instanceName":"1"}),"instanceName":"1"});
            var Q120;
            Q120=makeQuery(id+"F17.opPattern","COPY",BODY,{"derivedFrom":makeQuery(id+"F12.opPattern","COPY",BODY,{"derivedFrom":makeQuery(id+"F4.opPattern","COPY",BODY,{"derivedFrom":makeQuery(id+"F1.opExtrude","SWEPT_BODY",BODY,{"disambiguationData":[OSD([sQuery(id+"F0.wireOp",EDGE,"E0")])]}),"instanceName":"1"}),"instanceName":"1"}),"instanceName":"1"});
            var Q121;
            Q121=makeQuery(id+"F17.opPattern","COPY",BODY,{"derivedFrom":makeQuery(id+"F15.opPattern","COPY",BODY,{"derivedFrom":makeQuery(id+"F12.opPattern","COPY",BODY,{"derivedFrom":makeQuery(id+"F4.opPattern","COPY",BODY,{"derivedFrom":makeQuery(id+"F1.opExtrude","SWEPT_BODY",BODY,{"disambiguationData":[OSD([sQuery(id+"F0.wireOp",EDGE,"E0")])]}),"instanceName":"1"}),"instanceName":"1"}),"instanceName":"1"}),"instanceName":"1"});
            var Q122;
            Q122=makeQuery(id+"F17.opPattern","COPY",BODY,{"derivedFrom":makeQuery(id+"F15.opPattern","COPY",BODY,{"derivedFrom":makeQuery(id+"F12.opPattern","COPY",BODY,{"derivedFrom":makeQuery(id+"F9.opPattern","COPY",BODY,{"derivedFrom":makeQuery(id+"F1.opExtrude","SWEPT_BODY",BODY,{"disambiguationData":[OSD([sQuery(id+"F0.wireOp",EDGE,"E0")])]}),"instanceName":"1"}),"instanceName":"1"}),"instanceName":"1"}),"instanceName":"1"});
            var Q123;
            Q123=makeQuery(id+"F17.opPattern","COPY",BODY,{"derivedFrom":makeQuery(id+"F16.opPattern","COPY",BODY,{"derivedFrom":makeQuery(id+"F14.opPattern","COPY",BODY,{"derivedFrom":makeQuery(id+"F11.opPattern","COPY",BODY,{"derivedFrom":makeQuery(id+"F1.opExtrude","SWEPT_BODY",BODY,{"disambiguationData":[OSD([sQuery(id+"F0.wireOp",EDGE,"E0")])]}),"instanceName":"1"}),"instanceName":"1"}),"instanceName":"1"}),"instanceName":"1"});
            var Q124;
            Q124=makeQuery(id+"F17.opPattern","COPY",BODY,{"derivedFrom":makeQuery(id+"F16.opPattern","COPY",BODY,{"derivedFrom":makeQuery(id+"F12.opPattern","COPY",BODY,{"derivedFrom":makeQuery(id+"F10.opPattern","COPY",BODY,{"derivedFrom":makeQuery(id+"F1.opExtrude","SWEPT_BODY",BODY,{"disambiguationData":[OSD([sQuery(id+"F0.wireOp",EDGE,"E0")])]}),"instanceName":"1"}),"instanceName":"1"}),"instanceName":"1"}),"instanceName":"1"});
            var Q125;
            Q125=makeQuery(id+"F17.opPattern","COPY",BODY,{"derivedFrom":makeQuery(id+"F14.opPattern","COPY",BODY,{"derivedFrom":makeQuery(id+"F1.opExtrude","SWEPT_BODY",BODY,{"disambiguationData":[OSD([sQuery(id+"F0.wireOp",EDGE,"E0")])]}),"instanceName":"1"}),"instanceName":"1"});
            var Q126;
            Q126=makeQuery(id+"F17.opPattern","COPY",BODY,{"derivedFrom":makeQuery(id+"F16.opPattern","COPY",BODY,{"derivedFrom":makeQuery(id+"F9.opPattern","COPY",BODY,{"derivedFrom":makeQuery(id+"F4.opPattern","COPY",BODY,{"derivedFrom":makeQuery(id+"F1.opExtrude","SWEPT_BODY",BODY,{"disambiguationData":[OSD([sQuery(id+"F0.wireOp",EDGE,"E0")])]}),"instanceName":"1"}),"instanceName":"1"}),"instanceName":"1"}),"instanceName":"1"});
            var Q127;
            Q127=makeQuery(id+"F17.opPattern","COPY",BODY,{"derivedFrom":makeQuery(id+"F16.opPattern","COPY",BODY,{"derivedFrom":makeQuery(id+"F1.opExtrude","SWEPT_BODY",BODY,{"disambiguationData":[OSD([sQuery(id+"F0.wireOp",EDGE,"E0")])]}),"instanceName":"1"}),"instanceName":"1"});
            var Q128;
            Q128=makeQuery(id+"F17.opPattern","COPY",BODY,{"derivedFrom":makeQuery(id+"F16.opPattern","COPY",BODY,{"derivedFrom":makeQuery(id+"F11.opPattern","COPY",BODY,{"derivedFrom":makeQuery(id+"F9.opPattern","COPY",BODY,{"derivedFrom":makeQuery(id+"F1.opExtrude","SWEPT_BODY",BODY,{"disambiguationData":[OSD([sQuery(id+"F0.wireOp",EDGE,"E0")])]}),"instanceName":"1"}),"instanceName":"1"}),"instanceName":"1"}),"instanceName":"1"});
            var Q129;
            Q129=makeQuery(id+"F17.opPattern","COPY",BODY,{"derivedFrom":makeQuery(id+"F16.opPattern","COPY",BODY,{"derivedFrom":makeQuery(id+"F11.opPattern","COPY",BODY,{"derivedFrom":makeQuery(id+"F4.opPattern","COPY",BODY,{"derivedFrom":makeQuery(id+"F1.opExtrude","SWEPT_BODY",BODY,{"disambiguationData":[OSD([sQuery(id+"F0.wireOp",EDGE,"E0")])]}),"instanceName":"1"}),"instanceName":"1"}),"instanceName":"1"}),"instanceName":"1"});
            var Q130;
            Q130=makeQuery(id+"F17.opPattern","COPY",BODY,{"derivedFrom":makeQuery(id+"F15.opPattern","COPY",BODY,{"derivedFrom":makeQuery(id+"F4.opPattern","COPY",BODY,{"derivedFrom":makeQuery(id+"F1.opExtrude","SWEPT_BODY",BODY,{"disambiguationData":[OSD([sQuery(id+"F0.wireOp",EDGE,"E0")])]}),"instanceName":"1"}),"instanceName":"1"}),"instanceName":"1"});
            var Q131;
            Q131=makeQuery(id+"F17.opPattern","COPY",BODY,{"derivedFrom":makeQuery(id+"F15.opPattern","COPY",BODY,{"derivedFrom":makeQuery(id+"F12.opPattern","COPY",BODY,{"derivedFrom":makeQuery(id+"F10.opPattern","COPY",BODY,{"derivedFrom":makeQuery(id+"F1.opExtrude","SWEPT_BODY",BODY,{"disambiguationData":[OSD([sQuery(id+"F0.wireOp",EDGE,"E0")])]}),"instanceName":"1"}),"instanceName":"1"}),"instanceName":"1"}),"instanceName":"1"});
            var Q132;
            Q132=makeQuery(id+"F17.opPattern","COPY",BODY,{"derivedFrom":makeQuery(id+"F15.opPattern","COPY",BODY,{"derivedFrom":makeQuery(id+"F11.opPattern","COPY",BODY,{"derivedFrom":makeQuery(id+"F10.opPattern","COPY",BODY,{"derivedFrom":makeQuery(id+"F1.opExtrude","SWEPT_BODY",BODY,{"disambiguationData":[OSD([sQuery(id+"F0.wireOp",EDGE,"E0")])]}),"instanceName":"1"}),"instanceName":"1"}),"instanceName":"1"}),"instanceName":"1"});
            var Q133;
            Q133=makeQuery(id+"F17.opPattern","COPY",BODY,{"derivedFrom":makeQuery(id+"F16.opPattern","COPY",BODY,{"derivedFrom":makeQuery(id+"F12.opPattern","COPY",BODY,{"derivedFrom":makeQuery(id+"F4.opPattern","COPY",BODY,{"derivedFrom":makeQuery(id+"F1.opExtrude","SWEPT_BODY",BODY,{"disambiguationData":[OSD([sQuery(id+"F0.wireOp",EDGE,"E0")])]}),"instanceName":"1"}),"instanceName":"1"}),"instanceName":"1"}),"instanceName":"1"});
            var Q134;
            Q134=makeQuery(id+"F17.opPattern","COPY",BODY,{"derivedFrom":makeQuery(id+"F16.opPattern","COPY",BODY,{"derivedFrom":makeQuery(id+"F11.opPattern","COPY",BODY,{"derivedFrom":makeQuery(id+"F1.opExtrude","SWEPT_BODY",BODY,{"disambiguationData":[OSD([sQuery(id+"F0.wireOp",EDGE,"E0")])]}),"instanceName":"1"}),"instanceName":"1"}),"instanceName":"1"});
            var Q135;
            Q135=makeQuery(id+"F17.opPattern","COPY",BODY,{"derivedFrom":makeQuery(id+"F16.opPattern","COPY",BODY,{"derivedFrom":makeQuery(id+"F12.opPattern","COPY",BODY,{"derivedFrom":makeQuery(id+"F9.opPattern","COPY",BODY,{"derivedFrom":makeQuery(id+"F4.opPattern","COPY",BODY,{"derivedFrom":makeQuery(id+"F1.opExtrude","SWEPT_BODY",BODY,{"disambiguationData":[OSD([sQuery(id+"F0.wireOp",EDGE,"E0")])]}),"instanceName":"1"}),"instanceName":"1"}),"instanceName":"1"}),"instanceName":"1"}),"instanceName":"1"});
            var Q136;
            Q136=makeQuery(id+"F17.opPattern","COPY",BODY,{"derivedFrom":makeQuery(id+"F10.opPattern","COPY",BODY,{"derivedFrom":makeQuery(id+"F1.opExtrude","SWEPT_BODY",BODY,{"disambiguationData":[OSD([sQuery(id+"F0.wireOp",EDGE,"E0")])]}),"instanceName":"1"}),"instanceName":"1"});
            var Q137;
            Q137=makeQuery(id+"F17.opPattern","COPY",BODY,{"derivedFrom":makeQuery(id+"F11.opPattern","COPY",BODY,{"derivedFrom":makeQuery(id+"F9.opPattern","COPY",BODY,{"derivedFrom":makeQuery(id+"F4.opPattern","COPY",BODY,{"derivedFrom":makeQuery(id+"F1.opExtrude","SWEPT_BODY",BODY,{"disambiguationData":[OSD([sQuery(id+"F0.wireOp",EDGE,"E0")])]}),"instanceName":"1"}),"instanceName":"1"}),"instanceName":"1"}),"instanceName":"1"});
            var Q138;
            Q138=makeQuery(id+"F17.opPattern","COPY",BODY,{"derivedFrom":makeQuery(id+"F12.opPattern","COPY",BODY,{"derivedFrom":makeQuery(id+"F9.opPattern","COPY",BODY,{"derivedFrom":makeQuery(id+"F4.opPattern","COPY",BODY,{"derivedFrom":makeQuery(id+"F1.opExtrude","SWEPT_BODY",BODY,{"disambiguationData":[OSD([sQuery(id+"F0.wireOp",EDGE,"E0")])]}),"instanceName":"1"}),"instanceName":"1"}),"instanceName":"1"}),"instanceName":"1"});
            var Q139;
            Q139=makeQuery(id+"F17.opPattern","COPY",BODY,{"derivedFrom":makeQuery(id+"F11.opPattern","COPY",BODY,{"derivedFrom":makeQuery(id+"F1.opExtrude","SWEPT_BODY",BODY,{"disambiguationData":[OSD([sQuery(id+"F0.wireOp",EDGE,"E0")])]}),"instanceName":"1"}),"instanceName":"1"});
            var Q140;
            Q140=makeQuery(id+"F17.opPattern","COPY",BODY,{"derivedFrom":makeQuery(id+"F16.opPattern","COPY",BODY,{"derivedFrom":makeQuery(id+"F12.opPattern","COPY",BODY,{"derivedFrom":makeQuery(id+"F11.opPattern","COPY",BODY,{"derivedFrom":makeQuery(id+"F10.opPattern","COPY",BODY,{"derivedFrom":makeQuery(id+"F1.opExtrude","SWEPT_BODY",BODY,{"disambiguationData":[OSD([sQuery(id+"F0.wireOp",EDGE,"E0")])]}),"instanceName":"1"}),"instanceName":"1"}),"instanceName":"1"}),"instanceName":"1"}),"instanceName":"1"});
            var Q141;
            Q141=makeQuery(id+"F17.opPattern","COPY",BODY,{"derivedFrom":makeQuery(id+"F14.opPattern","COPY",BODY,{"derivedFrom":makeQuery(id+"F11.opPattern","COPY",BODY,{"derivedFrom":makeQuery(id+"F10.opPattern","COPY",BODY,{"derivedFrom":makeQuery(id+"F1.opExtrude","SWEPT_BODY",BODY,{"disambiguationData":[OSD([sQuery(id+"F0.wireOp",EDGE,"E0")])]}),"instanceName":"1"}),"instanceName":"1"}),"instanceName":"1"}),"instanceName":"1"});
            var Q142;
            Q142=makeQuery(id+"F17.opPattern","COPY",BODY,{"derivedFrom":makeQuery(id+"F15.opPattern","COPY",BODY,{"derivedFrom":makeQuery(id+"F12.opPattern","COPY",BODY,{"derivedFrom":makeQuery(id+"F9.opPattern","COPY",BODY,{"derivedFrom":makeQuery(id+"F4.opPattern","COPY",BODY,{"derivedFrom":makeQuery(id+"F1.opExtrude","SWEPT_BODY",BODY,{"disambiguationData":[OSD([sQuery(id+"F0.wireOp",EDGE,"E0")])]}),"instanceName":"1"}),"instanceName":"1"}),"instanceName":"1"}),"instanceName":"1"}),"instanceName":"1"});
            var Q143;
            Q143=makeQuery(id+"F17.opPattern","COPY",BODY,{"derivedFrom":makeQuery(id+"F15.opPattern","COPY",BODY,{"derivedFrom":makeQuery(id+"F12.opPattern","COPY",BODY,{"derivedFrom":makeQuery(id+"F1.opExtrude","SWEPT_BODY",BODY,{"disambiguationData":[OSD([sQuery(id+"F0.wireOp",EDGE,"E0")])]}),"instanceName":"1"}),"instanceName":"1"}),"instanceName":"1"});
            var Q144;
            Q144=makeQuery(id+"F17.opPattern","COPY",BODY,{"derivedFrom":makeQuery(id+"F15.opPattern","COPY",BODY,{"derivedFrom":makeQuery(id+"F12.opPattern","COPY",BODY,{"derivedFrom":makeQuery(id+"F11.opPattern","COPY",BODY,{"derivedFrom":makeQuery(id+"F9.opPattern","COPY",BODY,{"derivedFrom":makeQuery(id+"F4.opPattern","COPY",BODY,{"derivedFrom":makeQuery(id+"F1.opExtrude","SWEPT_BODY",BODY,{"disambiguationData":[OSD([sQuery(id+"F0.wireOp",EDGE,"E0")])]}),"instanceName":"1"}),"instanceName":"1"}),"instanceName":"1"}),"instanceName":"1"}),"instanceName":"1"}),"instanceName":"1"});
            var Q145;
            Q145=makeQuery(id+"F17.opPattern","COPY",BODY,{"derivedFrom":makeQuery(id+"F15.opPattern","COPY",BODY,{"derivedFrom":makeQuery(id+"F12.opPattern","COPY",BODY,{"derivedFrom":makeQuery(id+"F11.opPattern","COPY",BODY,{"derivedFrom":makeQuery(id+"F1.opExtrude","SWEPT_BODY",BODY,{"disambiguationData":[OSD([sQuery(id+"F0.wireOp",EDGE,"E0")])]}),"instanceName":"1"}),"instanceName":"1"}),"instanceName":"1"}),"instanceName":"1"});
            var Q146;
            Q146=makeQuery(id+"F17.opPattern","COPY",BODY,{"derivedFrom":makeQuery(id+"F16.opPattern","COPY",BODY,{"derivedFrom":makeQuery(id+"F4.opPattern","COPY",BODY,{"derivedFrom":makeQuery(id+"F1.opExtrude","SWEPT_BODY",BODY,{"disambiguationData":[OSD([sQuery(id+"F0.wireOp",EDGE,"E0")])]}),"instanceName":"1"}),"instanceName":"1"}),"instanceName":"1"});
            var Q147;
            Q147=makeQuery(id+"F17.opPattern","COPY",BODY,{"derivedFrom":makeQuery(id+"F15.opPattern","COPY",BODY,{"derivedFrom":makeQuery(id+"F14.opPattern","COPY",BODY,{"derivedFrom":makeQuery(id+"F10.opPattern","COPY",BODY,{"derivedFrom":makeQuery(id+"F1.opExtrude","SWEPT_BODY",BODY,{"disambiguationData":[OSD([sQuery(id+"F0.wireOp",EDGE,"E0")])]}),"instanceName":"1"}),"instanceName":"1"}),"instanceName":"1"}),"instanceName":"1"});
            var Q148;
            Q148=makeQuery(id+"F17.opPattern","COPY",BODY,{"derivedFrom":makeQuery(id+"F16.opPattern","COPY",BODY,{"derivedFrom":makeQuery(id+"F12.opPattern","COPY",BODY,{"derivedFrom":makeQuery(id+"F11.opPattern","COPY",BODY,{"derivedFrom":makeQuery(id+"F1.opExtrude","SWEPT_BODY",BODY,{"disambiguationData":[OSD([sQuery(id+"F0.wireOp",EDGE,"E0")])]}),"instanceName":"1"}),"instanceName":"1"}),"instanceName":"1"}),"instanceName":"1"});
            var Q149;
            Q149=makeQuery(id+"F17.opPattern","COPY",BODY,{"derivedFrom":makeQuery(id+"F16.opPattern","COPY",BODY,{"derivedFrom":makeQuery(id+"F14.opPattern","COPY",BODY,{"derivedFrom":makeQuery(id+"F4.opPattern","COPY",BODY,{"derivedFrom":makeQuery(id+"F1.opExtrude","SWEPT_BODY",BODY,{"disambiguationData":[OSD([sQuery(id+"F0.wireOp",EDGE,"E0")])]}),"instanceName":"1"}),"instanceName":"1"}),"instanceName":"1"}),"instanceName":"1"});
            var Q150;
            Q150=makeQuery(id+"F17.opPattern","COPY",BODY,{"derivedFrom":makeQuery(id+"F9.opPattern","COPY",BODY,{"derivedFrom":makeQuery(id+"F1.opExtrude","SWEPT_BODY",BODY,{"disambiguationData":[OSD([sQuery(id+"F0.wireOp",EDGE,"E0")])]}),"instanceName":"1"}),"instanceName":"1"});
            var Q151;
            Q151=makeQuery(id+"F17.opPattern","COPY",BODY,{"derivedFrom":makeQuery(id+"F1.opExtrude","SWEPT_BODY",BODY,{"disambiguationData":[OSD([sQuery(id+"F0.wireOp",EDGE,"E0")])]}),"instanceName":"1"});
            var Q152;
            Q152=makeQuery(id+"F17.opPattern","COPY",BODY,{"derivedFrom":makeQuery(id+"F11.opPattern","COPY",BODY,{"derivedFrom":makeQuery(id+"F9.opPattern","COPY",BODY,{"derivedFrom":makeQuery(id+"F1.opExtrude","SWEPT_BODY",BODY,{"disambiguationData":[OSD([sQuery(id+"F0.wireOp",EDGE,"E0")])]}),"instanceName":"1"}),"instanceName":"1"}),"instanceName":"1"});
            var Q153;
            Q153=makeQuery(id+"F17.opPattern","COPY",BODY,{"derivedFrom":makeQuery(id+"F14.opPattern","COPY",BODY,{"derivedFrom":makeQuery(id+"F11.opPattern","COPY",BODY,{"derivedFrom":makeQuery(id+"F1.opExtrude","SWEPT_BODY",BODY,{"disambiguationData":[OSD([sQuery(id+"F0.wireOp",EDGE,"E0")])]}),"instanceName":"1"}),"instanceName":"1"}),"instanceName":"1"});
            var Q154;
            Q154=makeQuery(id+"F17.opPattern","COPY",BODY,{"derivedFrom":makeQuery(id+"F14.opPattern","COPY",BODY,{"derivedFrom":makeQuery(id+"F4.opPattern","COPY",BODY,{"derivedFrom":makeQuery(id+"F1.opExtrude","SWEPT_BODY",BODY,{"disambiguationData":[OSD([sQuery(id+"F0.wireOp",EDGE,"E0")])]}),"instanceName":"1"}),"instanceName":"1"}),"instanceName":"1"});
            var Q155;
            Q155=makeQuery(id+"F17.opPattern","COPY",BODY,{"derivedFrom":makeQuery(id+"F4.opPattern","COPY",BODY,{"derivedFrom":makeQuery(id+"F1.opExtrude","SWEPT_BODY",BODY,{"disambiguationData":[OSD([sQuery(id+"F0.wireOp",EDGE,"E0")])]}),"instanceName":"1"}),"instanceName":"1"});
            var Q156;
            Q156=makeQuery(id+"F17.opPattern","COPY",BODY,{"derivedFrom":makeQuery(id+"F12.opPattern","COPY",BODY,{"derivedFrom":makeQuery(id+"F1.opExtrude","SWEPT_BODY",BODY,{"disambiguationData":[OSD([sQuery(id+"F0.wireOp",EDGE,"E0")])]}),"instanceName":"1"}),"instanceName":"1"});
            var Q157;
            Q157=makeQuery(id+"F17.opPattern","COPY",BODY,{"derivedFrom":makeQuery(id+"F11.opPattern","COPY",BODY,{"derivedFrom":makeQuery(id+"F4.opPattern","COPY",BODY,{"derivedFrom":makeQuery(id+"F1.opExtrude","SWEPT_BODY",BODY,{"disambiguationData":[OSD([sQuery(id+"F0.wireOp",EDGE,"E0")])]}),"instanceName":"1"}),"instanceName":"1"}),"instanceName":"1"});
            var Q158;
            Q158=makeQuery(id+"F17.opPattern","COPY",BODY,{"derivedFrom":makeQuery(id+"F15.opPattern","COPY",BODY,{"derivedFrom":makeQuery(id+"F10.opPattern","COPY",BODY,{"derivedFrom":makeQuery(id+"F1.opExtrude","SWEPT_BODY",BODY,{"disambiguationData":[OSD([sQuery(id+"F0.wireOp",EDGE,"E0")])]}),"instanceName":"1"}),"instanceName":"1"}),"instanceName":"1"});
            var Q159;
            Q159=makeQuery(id+"F17.opPattern","COPY",BODY,{"derivedFrom":makeQuery(id+"F15.opPattern","COPY",BODY,{"derivedFrom":makeQuery(id+"F12.opPattern","COPY",BODY,{"derivedFrom":makeQuery(id+"F11.opPattern","COPY",BODY,{"derivedFrom":makeQuery(id+"F9.opPattern","COPY",BODY,{"derivedFrom":makeQuery(id+"F1.opExtrude","SWEPT_BODY",BODY,{"disambiguationData":[OSD([sQuery(id+"F0.wireOp",EDGE,"E0")])]}),"instanceName":"1"}),"instanceName":"1"}),"instanceName":"1"}),"instanceName":"1"}),"instanceName":"1"});
            var Q160;
            Q160=makeQuery(id+"F17.opPattern","COPY",BODY,{"derivedFrom":makeQuery(id+"F15.opPattern","COPY",BODY,{"derivedFrom":makeQuery(id+"F12.opPattern","COPY",BODY,{"derivedFrom":makeQuery(id+"F11.opPattern","COPY",BODY,{"derivedFrom":makeQuery(id+"F4.opPattern","COPY",BODY,{"derivedFrom":makeQuery(id+"F1.opExtrude","SWEPT_BODY",BODY,{"disambiguationData":[OSD([sQuery(id+"F0.wireOp",EDGE,"E0")])]}),"instanceName":"1"}),"instanceName":"1"}),"instanceName":"1"}),"instanceName":"1"}),"instanceName":"1"});
            var Q161;
            Q161=makeQuery(id+"F17.opPattern","COPY",BODY,{"derivedFrom":makeQuery(id+"F16.opPattern","COPY",BODY,{"derivedFrom":makeQuery(id+"F11.opPattern","COPY",BODY,{"derivedFrom":makeQuery(id+"F9.opPattern","COPY",BODY,{"derivedFrom":makeQuery(id+"F4.opPattern","COPY",BODY,{"derivedFrom":makeQuery(id+"F1.opExtrude","SWEPT_BODY",BODY,{"disambiguationData":[OSD([sQuery(id+"F0.wireOp",EDGE,"E0")])]}),"instanceName":"1"}),"instanceName":"1"}),"instanceName":"1"}),"instanceName":"1"}),"instanceName":"1"});
            var Q162;
            Q162=makeQuery(id+"F17.opPattern","COPY",BODY,{"derivedFrom":makeQuery(id+"F16.opPattern","COPY",BODY,{"derivedFrom":makeQuery(id+"F12.opPattern","COPY",BODY,{"derivedFrom":makeQuery(id+"F11.opPattern","COPY",BODY,{"derivedFrom":makeQuery(id+"F9.opPattern","COPY",BODY,{"derivedFrom":makeQuery(id+"F1.opExtrude","SWEPT_BODY",BODY,{"disambiguationData":[OSD([sQuery(id+"F0.wireOp",EDGE,"E0")])]}),"instanceName":"1"}),"instanceName":"1"}),"instanceName":"1"}),"instanceName":"1"}),"instanceName":"1"});
            var Q163;
            Q163=makeQuery(id+"F17.opPattern","COPY",BODY,{"derivedFrom":makeQuery(id+"F16.opPattern","COPY",BODY,{"derivedFrom":makeQuery(id+"F14.opPattern","COPY",BODY,{"derivedFrom":makeQuery(id+"F11.opPattern","COPY",BODY,{"derivedFrom":makeQuery(id+"F4.opPattern","COPY",BODY,{"derivedFrom":makeQuery(id+"F1.opExtrude","SWEPT_BODY",BODY,{"disambiguationData":[OSD([sQuery(id+"F0.wireOp",EDGE,"E0")])]}),"instanceName":"1"}),"instanceName":"1"}),"instanceName":"1"}),"instanceName":"1"}),"instanceName":"1"});
            var Q164;
            Q164=makeQuery(id+"F17.opPattern","COPY",BODY,{"derivedFrom":makeQuery(id+"F15.opPattern","COPY",BODY,{"derivedFrom":makeQuery(id+"F14.opPattern","COPY",BODY,{"derivedFrom":makeQuery(id+"F1.opExtrude","SWEPT_BODY",BODY,{"disambiguationData":[OSD([sQuery(id+"F0.wireOp",EDGE,"E0")])]}),"instanceName":"1"}),"instanceName":"1"}),"instanceName":"1"});
            var Q165;
            Q165=makeQuery(id+"F17.opPattern","COPY",BODY,{"derivedFrom":makeQuery(id+"F16.opPattern","COPY",BODY,{"derivedFrom":makeQuery(id+"F12.opPattern","COPY",BODY,{"derivedFrom":makeQuery(id+"F1.opExtrude","SWEPT_BODY",BODY,{"disambiguationData":[OSD([sQuery(id+"F0.wireOp",EDGE,"E0")])]}),"instanceName":"1"}),"instanceName":"1"}),"instanceName":"1"});
            var Q166;
            Q166=makeQuery(id+"F17.opPattern","COPY",BODY,{"derivedFrom":makeQuery(id+"F11.opPattern","COPY",BODY,{"derivedFrom":makeQuery(id+"F10.opPattern","COPY",BODY,{"derivedFrom":makeQuery(id+"F1.opExtrude","SWEPT_BODY",BODY,{"disambiguationData":[OSD([sQuery(id+"F0.wireOp",EDGE,"E0")])]}),"instanceName":"1"}),"instanceName":"1"}),"instanceName":"1"});
            var Q167;
            Q167=makeQuery(id+"F17.opPattern","COPY",BODY,{"derivedFrom":makeQuery(id+"F12.opPattern","COPY",BODY,{"derivedFrom":makeQuery(id+"F11.opPattern","COPY",BODY,{"derivedFrom":makeQuery(id+"F4.opPattern","COPY",BODY,{"derivedFrom":makeQuery(id+"F1.opExtrude","SWEPT_BODY",BODY,{"disambiguationData":[OSD([sQuery(id+"F0.wireOp",EDGE,"E0")])]}),"instanceName":"1"}),"instanceName":"1"}),"instanceName":"1"}),"instanceName":"1"});
            var Q168;
            Q168=makeQuery(id+"F17.opPattern","COPY",BODY,{"derivedFrom":makeQuery(id+"F14.opPattern","COPY",BODY,{"derivedFrom":makeQuery(id+"F11.opPattern","COPY",BODY,{"derivedFrom":makeQuery(id+"F9.opPattern","COPY",BODY,{"derivedFrom":makeQuery(id+"F1.opExtrude","SWEPT_BODY",BODY,{"disambiguationData":[OSD([sQuery(id+"F0.wireOp",EDGE,"E0")])]}),"instanceName":"1"}),"instanceName":"1"}),"instanceName":"1"}),"instanceName":"1"});
            var Q169;
            Q169=makeQuery(id+"F17.opPattern","COPY",BODY,{"derivedFrom":makeQuery(id+"F14.opPattern","COPY",BODY,{"derivedFrom":makeQuery(id+"F11.opPattern","COPY",BODY,{"derivedFrom":makeQuery(id+"F4.opPattern","COPY",BODY,{"derivedFrom":makeQuery(id+"F1.opExtrude","SWEPT_BODY",BODY,{"disambiguationData":[OSD([sQuery(id+"F0.wireOp",EDGE,"E0")])]}),"instanceName":"1"}),"instanceName":"1"}),"instanceName":"1"}),"instanceName":"1"});
            var Q170;
            Q170=makeQuery(id+"F17.opPattern","COPY",BODY,{"derivedFrom":makeQuery(id+"F16.opPattern","COPY",BODY,{"derivedFrom":makeQuery(id+"F9.opPattern","COPY",BODY,{"derivedFrom":makeQuery(id+"F1.opExtrude","SWEPT_BODY",BODY,{"disambiguationData":[OSD([sQuery(id+"F0.wireOp",EDGE,"E0")])]}),"instanceName":"1"}),"instanceName":"1"}),"instanceName":"1"});
            var Q171;
            Q171=makeQuery(id+"F17.opPattern","COPY",BODY,{"derivedFrom":makeQuery(id+"F16.opPattern","COPY",BODY,{"derivedFrom":makeQuery(id+"F12.opPattern","COPY",BODY,{"derivedFrom":makeQuery(id+"F11.opPattern","COPY",BODY,{"derivedFrom":makeQuery(id+"F4.opPattern","COPY",BODY,{"derivedFrom":makeQuery(id+"F1.opExtrude","SWEPT_BODY",BODY,{"disambiguationData":[OSD([sQuery(id+"F0.wireOp",EDGE,"E0")])]}),"instanceName":"1"}),"instanceName":"1"}),"instanceName":"1"}),"instanceName":"1"}),"instanceName":"1"});
            var Q172;
            Q172=makeQuery(id+"F17.opPattern","COPY",BODY,{"derivedFrom":makeQuery(id+"F9.opPattern","COPY",BODY,{"derivedFrom":makeQuery(id+"F4.opPattern","COPY",BODY,{"derivedFrom":makeQuery(id+"F1.opExtrude","SWEPT_BODY",BODY,{"disambiguationData":[OSD([sQuery(id+"F0.wireOp",EDGE,"E0")])]}),"instanceName":"1"}),"instanceName":"1"}),"instanceName":"1"});
            var Q173;
            Q173=makeQuery(id+"F17.opPattern","COPY",BODY,{"derivedFrom":makeQuery(id+"F12.opPattern","COPY",BODY,{"derivedFrom":makeQuery(id+"F11.opPattern","COPY",BODY,{"derivedFrom":makeQuery(id+"F9.opPattern","COPY",BODY,{"derivedFrom":makeQuery(id+"F1.opExtrude","SWEPT_BODY",BODY,{"disambiguationData":[OSD([sQuery(id+"F0.wireOp",EDGE,"E0")])]}),"instanceName":"1"}),"instanceName":"1"}),"instanceName":"1"}),"instanceName":"1"});
            var Q174;
            Q174=makeQuery(id+"F17.opPattern","COPY",BODY,{"derivedFrom":makeQuery(id+"F15.opPattern","COPY",BODY,{"derivedFrom":makeQuery(id+"F14.opPattern","COPY",BODY,{"derivedFrom":makeQuery(id+"F4.opPattern","COPY",BODY,{"derivedFrom":makeQuery(id+"F1.opExtrude","SWEPT_BODY",BODY,{"disambiguationData":[OSD([sQuery(id+"F0.wireOp",EDGE,"E0")])]}),"instanceName":"1"}),"instanceName":"1"}),"instanceName":"1"}),"instanceName":"1"});
            var Q175;
            Q175=makeQuery(id+"F17.opPattern","COPY",BODY,{"derivedFrom":makeQuery(id+"F14.opPattern","COPY",BODY,{"derivedFrom":makeQuery(id+"F11.opPattern","COPY",BODY,{"derivedFrom":makeQuery(id+"F9.opPattern","COPY",BODY,{"derivedFrom":makeQuery(id+"F4.opPattern","COPY",BODY,{"derivedFrom":makeQuery(id+"F1.opExtrude","SWEPT_BODY",BODY,{"disambiguationData":[OSD([sQuery(id+"F0.wireOp",EDGE,"E0")])]}),"instanceName":"1"}),"instanceName":"1"}),"instanceName":"1"}),"instanceName":"1"}),"instanceName":"1"});
            var Q176;
            Q176=makeQuery(id+"F17.opPattern","COPY",BODY,{"derivedFrom":makeQuery(id+"F15.opPattern","COPY",BODY,{"derivedFrom":makeQuery(id+"F14.opPattern","COPY",BODY,{"derivedFrom":makeQuery(id+"F11.opPattern","COPY",BODY,{"derivedFrom":makeQuery(id+"F10.opPattern","COPY",BODY,{"derivedFrom":makeQuery(id+"F1.opExtrude","SWEPT_BODY",BODY,{"disambiguationData":[OSD([sQuery(id+"F0.wireOp",EDGE,"E0")])]}),"instanceName":"1"}),"instanceName":"1"}),"instanceName":"1"}),"instanceName":"1"}),"instanceName":"1"});
            var Q177;
            Q177=makeQuery(id+"F17.opPattern","COPY",BODY,{"derivedFrom":makeQuery(id+"F15.opPattern","COPY",BODY,{"derivedFrom":makeQuery(id+"F14.opPattern","COPY",BODY,{"derivedFrom":makeQuery(id+"F11.opPattern","COPY",BODY,{"derivedFrom":makeQuery(id+"F9.opPattern","COPY",BODY,{"derivedFrom":makeQuery(id+"F1.opExtrude","SWEPT_BODY",BODY,{"disambiguationData":[OSD([sQuery(id+"F0.wireOp",EDGE,"E0")])]}),"instanceName":"1"}),"instanceName":"1"}),"instanceName":"1"}),"instanceName":"1"}),"instanceName":"1"});
            var Q178;
            Q178=makeQuery(id+"F17.opPattern","COPY",BODY,{"derivedFrom":makeQuery(id+"F16.opPattern","COPY",BODY,{"derivedFrom":makeQuery(id+"F14.opPattern","COPY",BODY,{"derivedFrom":makeQuery(id+"F10.opPattern","COPY",BODY,{"derivedFrom":makeQuery(id+"F1.opExtrude","SWEPT_BODY",BODY,{"disambiguationData":[OSD([sQuery(id+"F0.wireOp",EDGE,"E0")])]}),"instanceName":"1"}),"instanceName":"1"}),"instanceName":"1"}),"instanceName":"1"});
            var Q179;
            Q179=makeQuery(id+"F17.opPattern","COPY",BODY,{"derivedFrom":makeQuery(id+"F12.opPattern","COPY",BODY,{"derivedFrom":makeQuery(id+"F10.opPattern","COPY",BODY,{"derivedFrom":makeQuery(id+"F1.opExtrude","SWEPT_BODY",BODY,{"disambiguationData":[OSD([sQuery(id+"F0.wireOp",EDGE,"E0")])]}),"instanceName":"1"}),"instanceName":"1"}),"instanceName":"1"});
            var Q180;
            Q180=makeQuery(id+"F17.opPattern","COPY",BODY,{"derivedFrom":makeQuery(id+"F15.opPattern","COPY",BODY,{"derivedFrom":makeQuery(id+"F9.opPattern","COPY",BODY,{"derivedFrom":makeQuery(id+"F1.opExtrude","SWEPT_BODY",BODY,{"disambiguationData":[OSD([sQuery(id+"F0.wireOp",EDGE,"E0")])]}),"instanceName":"1"}),"instanceName":"1"}),"instanceName":"1"});
            var Q181;
            Q181=makeQuery(id+"F17.opPattern","COPY",BODY,{"derivedFrom":makeQuery(id+"F12.opPattern","COPY",BODY,{"derivedFrom":makeQuery(id+"F9.opPattern","COPY",BODY,{"derivedFrom":makeQuery(id+"F1.opExtrude","SWEPT_BODY",BODY,{"disambiguationData":[OSD([sQuery(id+"F0.wireOp",EDGE,"E0")])]}),"instanceName":"1"}),"instanceName":"1"}),"instanceName":"1"});
            var Q182;
            Q182=makeQuery(id+"F17.opPattern","COPY",BODY,{"derivedFrom":makeQuery(id+"F15.opPattern","COPY",BODY,{"derivedFrom":makeQuery(id+"F9.opPattern","COPY",BODY,{"derivedFrom":makeQuery(id+"F4.opPattern","COPY",BODY,{"derivedFrom":makeQuery(id+"F1.opExtrude","SWEPT_BODY",BODY,{"disambiguationData":[OSD([sQuery(id+"F0.wireOp",EDGE,"E0")])]}),"instanceName":"1"}),"instanceName":"1"}),"instanceName":"1"}),"instanceName":"1"});
            var Q183;
            Q183=makeQuery(id+"F17.opPattern","COPY",BODY,{"derivedFrom":makeQuery(id+"F12.opPattern","COPY",BODY,{"derivedFrom":makeQuery(id+"F11.opPattern","COPY",BODY,{"derivedFrom":makeQuery(id+"F10.opPattern","COPY",BODY,{"derivedFrom":makeQuery(id+"F1.opExtrude","SWEPT_BODY",BODY,{"disambiguationData":[OSD([sQuery(id+"F0.wireOp",EDGE,"E0")])]}),"instanceName":"1"}),"instanceName":"1"}),"instanceName":"1"}),"instanceName":"1"});
            var Q184;
            Q184=makeQuery(id+"F17.opPattern","COPY",BODY,{"derivedFrom":makeQuery(id+"F15.opPattern","COPY",BODY,{"derivedFrom":makeQuery(id+"F14.opPattern","COPY",BODY,{"derivedFrom":makeQuery(id+"F11.opPattern","COPY",BODY,{"derivedFrom":makeQuery(id+"F9.opPattern","COPY",BODY,{"derivedFrom":makeQuery(id+"F4.opPattern","COPY",BODY,{"derivedFrom":makeQuery(id+"F1.opExtrude","SWEPT_BODY",BODY,{"disambiguationData":[OSD([sQuery(id+"F0.wireOp",EDGE,"E0")])]}),"instanceName":"1"}),"instanceName":"1"}),"instanceName":"1"}),"instanceName":"1"}),"instanceName":"1"}),"instanceName":"1"});
            var Q185;
            Q185=makeQuery(id+"F17.opPattern","COPY",BODY,{"derivedFrom":makeQuery(id+"F16.opPattern","COPY",BODY,{"derivedFrom":makeQuery(id+"F14.opPattern","COPY",BODY,{"derivedFrom":makeQuery(id+"F11.opPattern","COPY",BODY,{"derivedFrom":makeQuery(id+"F10.opPattern","COPY",BODY,{"derivedFrom":makeQuery(id+"F1.opExtrude","SWEPT_BODY",BODY,{"disambiguationData":[OSD([sQuery(id+"F0.wireOp",EDGE,"E0")])]}),"instanceName":"1"}),"instanceName":"1"}),"instanceName":"1"}),"instanceName":"1"}),"instanceName":"1"});
            var Q186;
            Q186=makeQuery(id+"F17.opPattern","COPY",BODY,{"derivedFrom":makeQuery(id+"F15.opPattern","COPY",BODY,{"derivedFrom":makeQuery(id+"F1.opExtrude","SWEPT_BODY",BODY,{"disambiguationData":[OSD([sQuery(id+"F0.wireOp",EDGE,"E0")])]}),"instanceName":"1"}),"instanceName":"1"});
            var Q187;
            Q187=makeQuery(id+"F17.opPattern","COPY",BODY,{"derivedFrom":makeQuery(id+"F16.opPattern","COPY",BODY,{"derivedFrom":makeQuery(id+"F10.opPattern","COPY",BODY,{"derivedFrom":makeQuery(id+"F1.opExtrude","SWEPT_BODY",BODY,{"disambiguationData":[OSD([sQuery(id+"F0.wireOp",EDGE,"E0")])]}),"instanceName":"1"}),"instanceName":"1"}),"instanceName":"1"});
            var Q188;
            Q188=makeQuery(id+"F17.opPattern","COPY",BODY,{"derivedFrom":makeQuery(id+"F15.opPattern","COPY",BODY,{"derivedFrom":makeQuery(id+"F11.opPattern","COPY",BODY,{"derivedFrom":makeQuery(id+"F9.opPattern","COPY",BODY,{"derivedFrom":makeQuery(id+"F1.opExtrude","SWEPT_BODY",BODY,{"disambiguationData":[OSD([sQuery(id+"F0.wireOp",EDGE,"E0")])]}),"instanceName":"1"}),"instanceName":"1"}),"instanceName":"1"}),"instanceName":"1"});
            var Q189;
            Q189=makeQuery(id+"F17.opPattern","COPY",BODY,{"derivedFrom":makeQuery(id+"F15.opPattern","COPY",BODY,{"derivedFrom":makeQuery(id+"F14.opPattern","COPY",BODY,{"derivedFrom":makeQuery(id+"F11.opPattern","COPY",BODY,{"derivedFrom":makeQuery(id+"F1.opExtrude","SWEPT_BODY",BODY,{"disambiguationData":[OSD([sQuery(id+"F0.wireOp",EDGE,"E0")])]}),"instanceName":"1"}),"instanceName":"1"}),"instanceName":"1"}),"instanceName":"1"});
            var Q190;
            Q190=makeQuery(id+"F17.opPattern","COPY",BODY,{"derivedFrom":makeQuery(id+"F16.opPattern","COPY",BODY,{"derivedFrom":makeQuery(id+"F11.opPattern","COPY",BODY,{"derivedFrom":makeQuery(id+"F10.opPattern","COPY",BODY,{"derivedFrom":makeQuery(id+"F1.opExtrude","SWEPT_BODY",BODY,{"disambiguationData":[OSD([sQuery(id+"F0.wireOp",EDGE,"E0")])]}),"instanceName":"1"}),"instanceName":"1"}),"instanceName":"1"}),"instanceName":"1"});
            var Q191;
            Q191=makeQuery(id+"F17.opPattern","COPY",BODY,{"derivedFrom":makeQuery(id+"F15.opPattern","COPY",BODY,{"derivedFrom":makeQuery(id+"F11.opPattern","COPY",BODY,{"derivedFrom":makeQuery(id+"F9.opPattern","COPY",BODY,{"derivedFrom":makeQuery(id+"F4.opPattern","COPY",BODY,{"derivedFrom":makeQuery(id+"F1.opExtrude","SWEPT_BODY",BODY,{"disambiguationData":[OSD([sQuery(id+"F0.wireOp",EDGE,"E0")])]}),"instanceName":"1"}),"instanceName":"1"}),"instanceName":"1"}),"instanceName":"1"}),"instanceName":"1"});
            var Q192;
            Q192=makeQuery(id+"F17.opPattern","COPY",BODY,{"derivedFrom":makeQuery(id+"F15.opPattern","COPY",BODY,{"derivedFrom":makeQuery(id+"F11.opPattern","COPY",BODY,{"derivedFrom":makeQuery(id+"F1.opExtrude","SWEPT_BODY",BODY,{"disambiguationData":[OSD([sQuery(id+"F0.wireOp",EDGE,"E0")])]}),"instanceName":"1"}),"instanceName":"1"}),"instanceName":"1"});
            var Q193;
            Q193=makeQuery(id+"F17.opPattern","COPY",BODY,{"derivedFrom":makeQuery(id+"F15.opPattern","COPY",BODY,{"derivedFrom":makeQuery(id+"F14.opPattern","COPY",BODY,{"derivedFrom":makeQuery(id+"F11.opPattern","COPY",BODY,{"derivedFrom":makeQuery(id+"F4.opPattern","COPY",BODY,{"derivedFrom":makeQuery(id+"F1.opExtrude","SWEPT_BODY",BODY,{"disambiguationData":[OSD([sQuery(id+"F0.wireOp",EDGE,"E0")])]}),"instanceName":"1"}),"instanceName":"1"}),"instanceName":"1"}),"instanceName":"1"}),"instanceName":"1"});
            var Q194;
            Q194=makeQuery(id+"F17.opPattern","COPY",BODY,{"derivedFrom":makeQuery(id+"F16.opPattern","COPY",BODY,{"derivedFrom":makeQuery(id+"F14.opPattern","COPY",BODY,{"derivedFrom":makeQuery(id+"F11.opPattern","COPY",BODY,{"derivedFrom":makeQuery(id+"F9.opPattern","COPY",BODY,{"derivedFrom":makeQuery(id+"F1.opExtrude","SWEPT_BODY",BODY,{"disambiguationData":[OSD([sQuery(id+"F0.wireOp",EDGE,"E0")])]}),"instanceName":"1"}),"instanceName":"1"}),"instanceName":"1"}),"instanceName":"1"}),"instanceName":"1"});
            var Q195;
            Q195=makeQuery(id+"F17.opPattern","COPY",BODY,{"derivedFrom":makeQuery(id+"F15.opPattern","COPY",BODY,{"derivedFrom":makeQuery(id+"F12.opPattern","COPY",BODY,{"derivedFrom":makeQuery(id+"F11.opPattern","COPY",BODY,{"derivedFrom":makeQuery(id+"F10.opPattern","COPY",BODY,{"derivedFrom":makeQuery(id+"F1.opExtrude","SWEPT_BODY",BODY,{"disambiguationData":[OSD([sQuery(id+"F0.wireOp",EDGE,"E0")])]}),"instanceName":"1"}),"instanceName":"1"}),"instanceName":"1"}),"instanceName":"1"}),"instanceName":"1"});
            var Q196;
            Q196=qCreatedBy(makeId("Front.planeOp"),FACE);
            transform(context, id + "F18", {"entities" : qUnion([Q0, Q1, Q2, Q3, Q4, Q5, Q6, Q7, Q8, Q9, Q10, Q11, Q12, Q13, Q14, Q15, Q16, Q17, Q18, Q19, Q20, Q21, Q22, Q23, Q24, Q25, Q26, Q27, Q28, Q29, Q30, Q31, Q32, Q33, Q34, Q35, Q36, Q37, Q38, Q39, Q40, Q41, Q42, Q43, Q44, Q45, Q46, Q47, Q48, Q49, Q50, Q51, Q52, Q53, Q54, Q55, Q56, Q57, Q58, Q59, Q60, Q61, Q62, Q63, Q64, Q65, Q66, Q67, Q68, Q69, Q70, Q71, Q72, Q73, Q74, Q75, Q76, Q77, Q78, Q79, Q80, Q81, Q82, Q83, Q84, Q85, Q86, Q87, Q88, Q89, Q90, Q91, Q92, Q93, Q94, Q95, Q96, Q97, Q98, Q99, Q100, Q101, Q102, Q103, Q104, Q105, Q106, Q107, Q108, Q109, Q110, Q111, Q112, Q113, Q114, Q115, Q116, Q117, Q118, Q119, Q120, Q121, Q122, Q123, Q124, Q125, Q126, Q127, Q128, Q129, Q130, Q131, Q132, Q133, Q134, Q135, Q136, Q137, Q138, Q139, Q140, Q141, Q142, Q143, Q144, Q145, Q146, Q147, Q148, Q149, Q150, Q151, Q152, Q153, Q154, Q155, Q156, Q157, Q158, Q159, Q160, Q161, Q162, Q163, Q164, Q165, Q166, Q167, Q168, Q169, Q170, Q171, Q172, Q173, Q174, Q175, Q176, Q177, Q178, Q179, Q180, Q181, Q182, Q183, Q184, Q185, Q186, Q187, Q188, Q189, Q190, Q191, Q192, Q193, Q194, Q195]), "transformType" : TransformType.TRANSLATION_DISTANCE, "transformDirection" : qUnion([Q196]), "distance" : 143.5 * mm, "oppositeDirection" : true, "makeCopy" : true});
        }
        {
            var Q0;
            Q0=makeQuery(id+"F12.opPattern","COPY",BODY,{"derivedFrom":makeQuery(id+"F9.opPattern","COPY",BODY,{"derivedFrom":makeQuery(id+"F4.opPattern","COPY",BODY,{"derivedFrom":makeQuery(id+"F1.opExtrude","SWEPT_BODY",BODY,{"disambiguationData":[OSD([sQuery(id+"F0.wireOp",EDGE,"E0")])]}),"instanceName":"1"}),"instanceName":"1"}),"instanceName":"1"});
            var Q1;
            Q1=makeQuery(id+"F9.opPattern","COPY",BODY,{"derivedFrom":makeQuery(id+"F1.opExtrude","SWEPT_BODY",BODY,{"disambiguationData":[OSD([sQuery(id+"F0.wireOp",EDGE,"E0")])]}),"instanceName":"1"});
            var Q2;
            Q2=makeQuery(id+"F9.opPattern","COPY",BODY,{"derivedFrom":makeQuery(id+"F4.opPattern","COPY",BODY,{"derivedFrom":makeQuery(id+"F1.opExtrude","SWEPT_BODY",BODY,{"disambiguationData":[OSD([sQuery(id+"F0.wireOp",EDGE,"E0")])]}),"instanceName":"1"}),"instanceName":"1"});
            var Q3;
            Q3=makeQuery(id+"F10.opPattern","COPY",BODY,{"derivedFrom":makeQuery(id+"F1.opExtrude","SWEPT_BODY",BODY,{"disambiguationData":[OSD([sQuery(id+"F0.wireOp",EDGE,"E0")])]}),"instanceName":"1"});
            var Q4;
            Q4=makeQuery(id+"F11.opPattern","COPY",BODY,{"derivedFrom":makeQuery(id+"F9.opPattern","COPY",BODY,{"derivedFrom":makeQuery(id+"F1.opExtrude","SWEPT_BODY",BODY,{"disambiguationData":[OSD([sQuery(id+"F0.wireOp",EDGE,"E0")])]}),"instanceName":"1"}),"instanceName":"1"});
            var Q5;
            Q5=makeQuery(id+"F11.opPattern","COPY",BODY,{"derivedFrom":makeQuery(id+"F4.opPattern","COPY",BODY,{"derivedFrom":makeQuery(id+"F1.opExtrude","SWEPT_BODY",BODY,{"disambiguationData":[OSD([sQuery(id+"F0.wireOp",EDGE,"E0")])]}),"instanceName":"1"}),"instanceName":"1"});
            var Q6;
            Q6=makeQuery(id+"F11.opPattern","COPY",BODY,{"derivedFrom":makeQuery(id+"F1.opExtrude","SWEPT_BODY",BODY,{"disambiguationData":[OSD([sQuery(id+"F0.wireOp",EDGE,"E0")])]}),"instanceName":"1"});
            var Q7;
            Q7=makeQuery(id+"F12.opPattern","COPY",BODY,{"derivedFrom":makeQuery(id+"F9.opPattern","COPY",BODY,{"derivedFrom":makeQuery(id+"F1.opExtrude","SWEPT_BODY",BODY,{"disambiguationData":[OSD([sQuery(id+"F0.wireOp",EDGE,"E0")])]}),"instanceName":"1"}),"instanceName":"1"});
            var Q8;
            Q8=makeQuery(id+"F18.opPattern","COPY",BODY,{"derivedFrom":makeQuery(id+"F17.opPattern","COPY",BODY,{"derivedFrom":makeQuery(id+"F16.opPattern","COPY",BODY,{"derivedFrom":makeQuery(id+"F11.opPattern","COPY",BODY,{"derivedFrom":makeQuery(id+"F9.opPattern","COPY",BODY,{"derivedFrom":makeQuery(id+"F1.opExtrude","SWEPT_BODY",BODY,{"disambiguationData":[OSD([sQuery(id+"F0.wireOp",EDGE,"E0")])]}),"instanceName":"1"}),"instanceName":"1"}),"instanceName":"1"}),"instanceName":"1"}),"instanceName":"1"});
            var Q9;
            Q9=makeQuery(id+"F18.opPattern","COPY",BODY,{"derivedFrom":makeQuery(id+"F17.opPattern","COPY",BODY,{"derivedFrom":makeQuery(id+"F15.opPattern","COPY",BODY,{"derivedFrom":makeQuery(id+"F14.opPattern","COPY",BODY,{"derivedFrom":makeQuery(id+"F11.opPattern","COPY",BODY,{"derivedFrom":makeQuery(id+"F10.opPattern","COPY",BODY,{"derivedFrom":makeQuery(id+"F1.opExtrude","SWEPT_BODY",BODY,{"disambiguationData":[OSD([sQuery(id+"F0.wireOp",EDGE,"E0")])]}),"instanceName":"1"}),"instanceName":"1"}),"instanceName":"1"}),"instanceName":"1"}),"instanceName":"1"}),"instanceName":"1"});
            var Q10;
            Q10=makeQuery(id+"F12.opPattern","COPY",BODY,{"derivedFrom":makeQuery(id+"F1.opExtrude","SWEPT_BODY",BODY,{"disambiguationData":[OSD([sQuery(id+"F0.wireOp",EDGE,"E0")])]}),"instanceName":"1"});
            var Q11;
            Q11=makeQuery(id+"F12.opPattern","COPY",BODY,{"derivedFrom":makeQuery(id+"F11.opPattern","COPY",BODY,{"derivedFrom":makeQuery(id+"F9.opPattern","COPY",BODY,{"derivedFrom":makeQuery(id+"F1.opExtrude","SWEPT_BODY",BODY,{"disambiguationData":[OSD([sQuery(id+"F0.wireOp",EDGE,"E0")])]}),"instanceName":"1"}),"instanceName":"1"}),"instanceName":"1"});
            var Q12;
            Q12=makeQuery(id+"F12.opPattern","COPY",BODY,{"derivedFrom":makeQuery(id+"F4.opPattern","COPY",BODY,{"derivedFrom":makeQuery(id+"F1.opExtrude","SWEPT_BODY",BODY,{"disambiguationData":[OSD([sQuery(id+"F0.wireOp",EDGE,"E0")])]}),"instanceName":"1"}),"instanceName":"1"});
            var Q13;
            Q13=makeQuery(id+"F12.opPattern","COPY",BODY,{"derivedFrom":makeQuery(id+"F11.opPattern","COPY",BODY,{"derivedFrom":makeQuery(id+"F10.opPattern","COPY",BODY,{"derivedFrom":makeQuery(id+"F1.opExtrude","SWEPT_BODY",BODY,{"disambiguationData":[OSD([sQuery(id+"F0.wireOp",EDGE,"E0")])]}),"instanceName":"1"}),"instanceName":"1"}),"instanceName":"1"});
            var Q14;
            Q14=makeQuery(id+"F18.opPattern","COPY",BODY,{"derivedFrom":makeQuery(id+"F17.opPattern","COPY",BODY,{"derivedFrom":makeQuery(id+"F16.opPattern","COPY",BODY,{"derivedFrom":makeQuery(id+"F11.opPattern","COPY",BODY,{"derivedFrom":makeQuery(id+"F10.opPattern","COPY",BODY,{"derivedFrom":makeQuery(id+"F1.opExtrude","SWEPT_BODY",BODY,{"disambiguationData":[OSD([sQuery(id+"F0.wireOp",EDGE,"E0")])]}),"instanceName":"1"}),"instanceName":"1"}),"instanceName":"1"}),"instanceName":"1"}),"instanceName":"1"});
            var Q15;
            Q15=makeQuery(id+"F14.opPattern","COPY",BODY,{"derivedFrom":makeQuery(id+"F10.opPattern","COPY",BODY,{"derivedFrom":makeQuery(id+"F1.opExtrude","SWEPT_BODY",BODY,{"disambiguationData":[OSD([sQuery(id+"F0.wireOp",EDGE,"E0")])]}),"instanceName":"1"}),"instanceName":"1"});
            var Q16;
            Q16=makeQuery(id+"F18.opPattern","COPY",BODY,{"derivedFrom":makeQuery(id+"F17.opPattern","COPY",BODY,{"derivedFrom":makeQuery(id+"F16.opPattern","COPY",BODY,{"derivedFrom":makeQuery(id+"F12.opPattern","COPY",BODY,{"derivedFrom":makeQuery(id+"F9.opPattern","COPY",BODY,{"derivedFrom":makeQuery(id+"F4.opPattern","COPY",BODY,{"derivedFrom":makeQuery(id+"F1.opExtrude","SWEPT_BODY",BODY,{"disambiguationData":[OSD([sQuery(id+"F0.wireOp",EDGE,"E0")])]}),"instanceName":"1"}),"instanceName":"1"}),"instanceName":"1"}),"instanceName":"1"}),"instanceName":"1"}),"instanceName":"1"});
            var Q17;
            Q17=makeQuery(id+"F18.opPattern","COPY",BODY,{"derivedFrom":makeQuery(id+"F17.opPattern","COPY",BODY,{"derivedFrom":makeQuery(id+"F16.opPattern","COPY",BODY,{"derivedFrom":makeQuery(id+"F14.opPattern","COPY",BODY,{"derivedFrom":makeQuery(id+"F4.opPattern","COPY",BODY,{"derivedFrom":makeQuery(id+"F1.opExtrude","SWEPT_BODY",BODY,{"disambiguationData":[OSD([sQuery(id+"F0.wireOp",EDGE,"E0")])]}),"instanceName":"1"}),"instanceName":"1"}),"instanceName":"1"}),"instanceName":"1"}),"instanceName":"1"});
            var Q18;
            Q18=makeQuery(id+"F14.opPattern","COPY",BODY,{"derivedFrom":makeQuery(id+"F1.opExtrude","SWEPT_BODY",BODY,{"disambiguationData":[OSD([sQuery(id+"F0.wireOp",EDGE,"E0")])]}),"instanceName":"1"});
            var Q19;
            Q19=makeQuery(id+"F12.opPattern","COPY",BODY,{"derivedFrom":makeQuery(id+"F11.opPattern","COPY",BODY,{"derivedFrom":makeQuery(id+"F9.opPattern","COPY",BODY,{"derivedFrom":makeQuery(id+"F4.opPattern","COPY",BODY,{"derivedFrom":makeQuery(id+"F1.opExtrude","SWEPT_BODY",BODY,{"disambiguationData":[OSD([sQuery(id+"F0.wireOp",EDGE,"E0")])]}),"instanceName":"1"}),"instanceName":"1"}),"instanceName":"1"}),"instanceName":"1"});
            var Q20;
            Q20=makeQuery(id+"F15.opPattern","COPY",BODY,{"derivedFrom":makeQuery(id+"F9.opPattern","COPY",BODY,{"derivedFrom":makeQuery(id+"F1.opExtrude","SWEPT_BODY",BODY,{"disambiguationData":[OSD([sQuery(id+"F0.wireOp",EDGE,"E0")])]}),"instanceName":"1"}),"instanceName":"1"});
            var Q21;
            Q21=makeQuery(id+"F12.opPattern","COPY",BODY,{"derivedFrom":makeQuery(id+"F11.opPattern","COPY",BODY,{"derivedFrom":makeQuery(id+"F1.opExtrude","SWEPT_BODY",BODY,{"disambiguationData":[OSD([sQuery(id+"F0.wireOp",EDGE,"E0")])]}),"instanceName":"1"}),"instanceName":"1"});
            var Q22;
            Q22=makeQuery(id+"F14.opPattern","COPY",BODY,{"derivedFrom":makeQuery(id+"F4.opPattern","COPY",BODY,{"derivedFrom":makeQuery(id+"F1.opExtrude","SWEPT_BODY",BODY,{"disambiguationData":[OSD([sQuery(id+"F0.wireOp",EDGE,"E0")])]}),"instanceName":"1"}),"instanceName":"1"});
            var Q23;
            Q23=makeQuery(id+"F18.opPattern","COPY",BODY,{"derivedFrom":makeQuery(id+"F17.opPattern","COPY",BODY,{"derivedFrom":makeQuery(id+"F15.opPattern","COPY",BODY,{"derivedFrom":makeQuery(id+"F12.opPattern","COPY",BODY,{"derivedFrom":makeQuery(id+"F10.opPattern","COPY",BODY,{"derivedFrom":makeQuery(id+"F1.opExtrude","SWEPT_BODY",BODY,{"disambiguationData":[OSD([sQuery(id+"F0.wireOp",EDGE,"E0")])]}),"instanceName":"1"}),"instanceName":"1"}),"instanceName":"1"}),"instanceName":"1"}),"instanceName":"1"});
            var Q24;
            Q24=makeQuery(id+"F15.opPattern","COPY",BODY,{"derivedFrom":makeQuery(id+"F1.opExtrude","SWEPT_BODY",BODY,{"disambiguationData":[OSD([sQuery(id+"F0.wireOp",EDGE,"E0")])]}),"instanceName":"1"});
            var Q25;
            Q25=makeQuery(id+"F18.opPattern","COPY",BODY,{"derivedFrom":makeQuery(id+"F17.opPattern","COPY",BODY,{"derivedFrom":makeQuery(id+"F16.opPattern","COPY",BODY,{"derivedFrom":makeQuery(id+"F14.opPattern","COPY",BODY,{"derivedFrom":makeQuery(id+"F11.opPattern","COPY",BODY,{"derivedFrom":makeQuery(id+"F1.opExtrude","SWEPT_BODY",BODY,{"disambiguationData":[OSD([sQuery(id+"F0.wireOp",EDGE,"E0")])]}),"instanceName":"1"}),"instanceName":"1"}),"instanceName":"1"}),"instanceName":"1"}),"instanceName":"1"});
            var Q26;
            Q26=makeQuery(id+"F15.opPattern","COPY",BODY,{"derivedFrom":makeQuery(id+"F4.opPattern","COPY",BODY,{"derivedFrom":makeQuery(id+"F1.opExtrude","SWEPT_BODY",BODY,{"disambiguationData":[OSD([sQuery(id+"F0.wireOp",EDGE,"E0")])]}),"instanceName":"1"}),"instanceName":"1"});
            var Q27;
            Q27=makeQuery(id+"F16.opPattern","COPY",BODY,{"derivedFrom":makeQuery(id+"F9.opPattern","COPY",BODY,{"derivedFrom":makeQuery(id+"F1.opExtrude","SWEPT_BODY",BODY,{"disambiguationData":[OSD([sQuery(id+"F0.wireOp",EDGE,"E0")])]}),"instanceName":"1"}),"instanceName":"1"});
            var Q28;
            Q28=makeQuery(id+"F18.opPattern","COPY",BODY,{"derivedFrom":makeQuery(id+"F17.opPattern","COPY",BODY,{"derivedFrom":makeQuery(id+"F15.opPattern","COPY",BODY,{"derivedFrom":makeQuery(id+"F11.opPattern","COPY",BODY,{"derivedFrom":makeQuery(id+"F9.opPattern","COPY",BODY,{"derivedFrom":makeQuery(id+"F4.opPattern","COPY",BODY,{"derivedFrom":makeQuery(id+"F1.opExtrude","SWEPT_BODY",BODY,{"disambiguationData":[OSD([sQuery(id+"F0.wireOp",EDGE,"E0")])]}),"instanceName":"1"}),"instanceName":"1"}),"instanceName":"1"}),"instanceName":"1"}),"instanceName":"1"}),"instanceName":"1"});
            var Q29;
            Q29=makeQuery(id+"F16.opPattern","COPY",BODY,{"derivedFrom":makeQuery(id+"F1.opExtrude","SWEPT_BODY",BODY,{"disambiguationData":[OSD([sQuery(id+"F0.wireOp",EDGE,"E0")])]}),"instanceName":"1"});
            var Q30;
            Q30=makeQuery(id+"F11.opPattern","COPY",BODY,{"derivedFrom":makeQuery(id+"F10.opPattern","COPY",BODY,{"derivedFrom":makeQuery(id+"F1.opExtrude","SWEPT_BODY",BODY,{"disambiguationData":[OSD([sQuery(id+"F0.wireOp",EDGE,"E0")])]}),"instanceName":"1"}),"instanceName":"1"});
            var Q31;
            Q31=makeQuery(id+"F17.opPattern","COPY",BODY,{"derivedFrom":makeQuery(id+"F9.opPattern","COPY",BODY,{"derivedFrom":makeQuery(id+"F1.opExtrude","SWEPT_BODY",BODY,{"disambiguationData":[OSD([sQuery(id+"F0.wireOp",EDGE,"E0")])]}),"instanceName":"1"}),"instanceName":"1"});
            var Q32;
            Q32=makeQuery(id+"F16.opPattern","COPY",BODY,{"derivedFrom":makeQuery(id+"F4.opPattern","COPY",BODY,{"derivedFrom":makeQuery(id+"F1.opExtrude","SWEPT_BODY",BODY,{"disambiguationData":[OSD([sQuery(id+"F0.wireOp",EDGE,"E0")])]}),"instanceName":"1"}),"instanceName":"1"});
            var Q33;
            Q33=makeQuery(id+"F18.opPattern","COPY",BODY,{"derivedFrom":makeQuery(id+"F17.opPattern","COPY",BODY,{"derivedFrom":makeQuery(id+"F16.opPattern","COPY",BODY,{"derivedFrom":makeQuery(id+"F12.opPattern","COPY",BODY,{"derivedFrom":makeQuery(id+"F1.opExtrude","SWEPT_BODY",BODY,{"disambiguationData":[OSD([sQuery(id+"F0.wireOp",EDGE,"E0")])]}),"instanceName":"1"}),"instanceName":"1"}),"instanceName":"1"}),"instanceName":"1"});
            var Q34;
            Q34=makeQuery(id+"F17.opPattern","COPY",BODY,{"derivedFrom":makeQuery(id+"F1.opExtrude","SWEPT_BODY",BODY,{"disambiguationData":[OSD([sQuery(id+"F0.wireOp",EDGE,"E0")])]}),"instanceName":"1"});
            var Q35;
            Q35=makeQuery(id+"F17.opPattern","COPY",BODY,{"derivedFrom":makeQuery(id+"F4.opPattern","COPY",BODY,{"derivedFrom":makeQuery(id+"F1.opExtrude","SWEPT_BODY",BODY,{"disambiguationData":[OSD([sQuery(id+"F0.wireOp",EDGE,"E0")])]}),"instanceName":"1"}),"instanceName":"1"});
            var Q36;
            Q36=makeQuery(id+"F18.opPattern","COPY",BODY,{"derivedFrom":makeQuery(id+"F17.opPattern","COPY",BODY,{"derivedFrom":makeQuery(id+"F16.opPattern","COPY",BODY,{"derivedFrom":makeQuery(id+"F14.opPattern","COPY",BODY,{"derivedFrom":makeQuery(id+"F10.opPattern","COPY",BODY,{"derivedFrom":makeQuery(id+"F1.opExtrude","SWEPT_BODY",BODY,{"disambiguationData":[OSD([sQuery(id+"F0.wireOp",EDGE,"E0")])]}),"instanceName":"1"}),"instanceName":"1"}),"instanceName":"1"}),"instanceName":"1"}),"instanceName":"1"});
            var Q37;
            Q37=makeQuery(id+"F18.opPattern","COPY",BODY,{"derivedFrom":makeQuery(id+"F17.opPattern","COPY",BODY,{"derivedFrom":makeQuery(id+"F15.opPattern","COPY",BODY,{"derivedFrom":makeQuery(id+"F12.opPattern","COPY",BODY,{"derivedFrom":makeQuery(id+"F1.opExtrude","SWEPT_BODY",BODY,{"disambiguationData":[OSD([sQuery(id+"F0.wireOp",EDGE,"E0")])]}),"instanceName":"1"}),"instanceName":"1"}),"instanceName":"1"}),"instanceName":"1"});
            var Q38;
            Q38=makeQuery(id+"F18.opPattern","COPY",BODY,{"derivedFrom":makeQuery(id+"F17.opPattern","COPY",BODY,{"derivedFrom":makeQuery(id+"F15.opPattern","COPY",BODY,{"derivedFrom":makeQuery(id+"F12.opPattern","COPY",BODY,{"derivedFrom":makeQuery(id+"F11.opPattern","COPY",BODY,{"derivedFrom":makeQuery(id+"F1.opExtrude","SWEPT_BODY",BODY,{"disambiguationData":[OSD([sQuery(id+"F0.wireOp",EDGE,"E0")])]}),"instanceName":"1"}),"instanceName":"1"}),"instanceName":"1"}),"instanceName":"1"}),"instanceName":"1"});
            var Q39;
            Q39=makeQuery(id+"F18.opPattern","COPY",BODY,{"derivedFrom":makeQuery(id+"F17.opPattern","COPY",BODY,{"derivedFrom":makeQuery(id+"F15.opPattern","COPY",BODY,{"derivedFrom":makeQuery(id+"F14.opPattern","COPY",BODY,{"derivedFrom":makeQuery(id+"F11.opPattern","COPY",BODY,{"derivedFrom":makeQuery(id+"F4.opPattern","COPY",BODY,{"derivedFrom":makeQuery(id+"F1.opExtrude","SWEPT_BODY",BODY,{"disambiguationData":[OSD([sQuery(id+"F0.wireOp",EDGE,"E0")])]}),"instanceName":"1"}),"instanceName":"1"}),"instanceName":"1"}),"instanceName":"1"}),"instanceName":"1"}),"instanceName":"1"});
            var Q40;
            Q40=makeQuery(id+"F12.opPattern","COPY",BODY,{"derivedFrom":makeQuery(id+"F11.opPattern","COPY",BODY,{"derivedFrom":makeQuery(id+"F4.opPattern","COPY",BODY,{"derivedFrom":makeQuery(id+"F1.opExtrude","SWEPT_BODY",BODY,{"disambiguationData":[OSD([sQuery(id+"F0.wireOp",EDGE,"E0")])]}),"instanceName":"1"}),"instanceName":"1"}),"instanceName":"1"});
            var Q41;
            Q41=makeQuery(id+"F18.opPattern","COPY",BODY,{"derivedFrom":makeQuery(id+"F17.opPattern","COPY",BODY,{"derivedFrom":makeQuery(id+"F15.opPattern","COPY",BODY,{"derivedFrom":makeQuery(id+"F12.opPattern","COPY",BODY,{"derivedFrom":makeQuery(id+"F9.opPattern","COPY",BODY,{"derivedFrom":makeQuery(id+"F4.opPattern","COPY",BODY,{"derivedFrom":makeQuery(id+"F1.opExtrude","SWEPT_BODY",BODY,{"disambiguationData":[OSD([sQuery(id+"F0.wireOp",EDGE,"E0")])]}),"instanceName":"1"}),"instanceName":"1"}),"instanceName":"1"}),"instanceName":"1"}),"instanceName":"1"}),"instanceName":"1"});
            var Q42;
            Q42=makeQuery(id+"F18.opPattern","COPY",BODY,{"derivedFrom":makeQuery(id+"F17.opPattern","COPY",BODY,{"derivedFrom":makeQuery(id+"F16.opPattern","COPY",BODY,{"derivedFrom":makeQuery(id+"F14.opPattern","COPY",BODY,{"derivedFrom":makeQuery(id+"F11.opPattern","COPY",BODY,{"derivedFrom":makeQuery(id+"F9.opPattern","COPY",BODY,{"derivedFrom":makeQuery(id+"F4.opPattern","COPY",BODY,{"derivedFrom":makeQuery(id+"F1.opExtrude","SWEPT_BODY",BODY,{"disambiguationData":[OSD([sQuery(id+"F0.wireOp",EDGE,"E0")])]}),"instanceName":"1"}),"instanceName":"1"}),"instanceName":"1"}),"instanceName":"1"}),"instanceName":"1"}),"instanceName":"1"}),"instanceName":"1"});
            var Q43;
            Q43=makeQuery(id+"F18.opPattern","COPY",BODY,{"derivedFrom":makeQuery(id+"F17.opPattern","COPY",BODY,{"derivedFrom":makeQuery(id+"F16.opPattern","COPY",BODY,{"derivedFrom":makeQuery(id+"F12.opPattern","COPY",BODY,{"derivedFrom":makeQuery(id+"F11.opPattern","COPY",BODY,{"derivedFrom":makeQuery(id+"F9.opPattern","COPY",BODY,{"derivedFrom":makeQuery(id+"F1.opExtrude","SWEPT_BODY",BODY,{"disambiguationData":[OSD([sQuery(id+"F0.wireOp",EDGE,"E0")])]}),"instanceName":"1"}),"instanceName":"1"}),"instanceName":"1"}),"instanceName":"1"}),"instanceName":"1"}),"instanceName":"1"});
            var Q44;
            Q44=makeQuery(id+"F18.opPattern","COPY",BODY,{"derivedFrom":makeQuery(id+"F17.opPattern","COPY",BODY,{"derivedFrom":makeQuery(id+"F15.opPattern","COPY",BODY,{"derivedFrom":makeQuery(id+"F12.opPattern","COPY",BODY,{"derivedFrom":makeQuery(id+"F4.opPattern","COPY",BODY,{"derivedFrom":makeQuery(id+"F1.opExtrude","SWEPT_BODY",BODY,{"disambiguationData":[OSD([sQuery(id+"F0.wireOp",EDGE,"E0")])]}),"instanceName":"1"}),"instanceName":"1"}),"instanceName":"1"}),"instanceName":"1"}),"instanceName":"1"});
            var Q45;
            Q45=makeQuery(id+"F18.opPattern","COPY",BODY,{"derivedFrom":makeQuery(id+"F17.opPattern","COPY",BODY,{"derivedFrom":makeQuery(id+"F15.opPattern","COPY",BODY,{"derivedFrom":makeQuery(id+"F14.opPattern","COPY",BODY,{"derivedFrom":makeQuery(id+"F10.opPattern","COPY",BODY,{"derivedFrom":makeQuery(id+"F1.opExtrude","SWEPT_BODY",BODY,{"disambiguationData":[OSD([sQuery(id+"F0.wireOp",EDGE,"E0")])]}),"instanceName":"1"}),"instanceName":"1"}),"instanceName":"1"}),"instanceName":"1"}),"instanceName":"1"});
            var Q46;
            Q46=makeQuery(id+"F18.opPattern","COPY",BODY,{"derivedFrom":makeQuery(id+"F9.opPattern","COPY",BODY,{"derivedFrom":makeQuery(id+"F1.opExtrude","SWEPT_BODY",BODY,{"disambiguationData":[OSD([sQuery(id+"F0.wireOp",EDGE,"E0")])]}),"instanceName":"1"}),"instanceName":"1"});
            var Q47;
            Q47=makeQuery(id+"F18.opPattern","COPY",BODY,{"derivedFrom":makeQuery(id+"F4.opPattern","COPY",BODY,{"derivedFrom":makeQuery(id+"F1.opExtrude","SWEPT_BODY",BODY,{"disambiguationData":[OSD([sQuery(id+"F0.wireOp",EDGE,"E0")])]}),"instanceName":"1"}),"instanceName":"1"});
            var Q48;
            Q48=makeQuery(id+"F18.opPattern","COPY",BODY,{"derivedFrom":makeQuery(id+"F17.opPattern","COPY",BODY,{"derivedFrom":makeQuery(id+"F15.opPattern","COPY",BODY,{"derivedFrom":makeQuery(id+"F12.opPattern","COPY",BODY,{"derivedFrom":makeQuery(id+"F11.opPattern","COPY",BODY,{"derivedFrom":makeQuery(id+"F9.opPattern","COPY",BODY,{"derivedFrom":makeQuery(id+"F4.opPattern","COPY",BODY,{"derivedFrom":makeQuery(id+"F1.opExtrude","SWEPT_BODY",BODY,{"disambiguationData":[OSD([sQuery(id+"F0.wireOp",EDGE,"E0")])]}),"instanceName":"1"}),"instanceName":"1"}),"instanceName":"1"}),"instanceName":"1"}),"instanceName":"1"}),"instanceName":"1"}),"instanceName":"1"});
            var Q49;
            Q49=makeQuery(id+"F18.opPattern","COPY",BODY,{"derivedFrom":makeQuery(id+"F17.opPattern","COPY",BODY,{"derivedFrom":makeQuery(id+"F15.opPattern","COPY",BODY,{"derivedFrom":makeQuery(id+"F14.opPattern","COPY",BODY,{"derivedFrom":makeQuery(id+"F11.opPattern","COPY",BODY,{"derivedFrom":makeQuery(id+"F9.opPattern","COPY",BODY,{"derivedFrom":makeQuery(id+"F1.opExtrude","SWEPT_BODY",BODY,{"disambiguationData":[OSD([sQuery(id+"F0.wireOp",EDGE,"E0")])]}),"instanceName":"1"}),"instanceName":"1"}),"instanceName":"1"}),"instanceName":"1"}),"instanceName":"1"}),"instanceName":"1"});
            var Q50;
            Q50=makeQuery(id+"F18.opPattern","COPY",BODY,{"derivedFrom":makeQuery(id+"F1.opExtrude","SWEPT_BODY",BODY,{"disambiguationData":[OSD([sQuery(id+"F0.wireOp",EDGE,"E0")])]}),"instanceName":"1"});
            var Q51;
            Q51=makeQuery(id+"F18.opPattern","COPY",BODY,{"derivedFrom":makeQuery(id+"F17.opPattern","COPY",BODY,{"derivedFrom":makeQuery(id+"F15.opPattern","COPY",BODY,{"derivedFrom":makeQuery(id+"F14.opPattern","COPY",BODY,{"derivedFrom":makeQuery(id+"F1.opExtrude","SWEPT_BODY",BODY,{"disambiguationData":[OSD([sQuery(id+"F0.wireOp",EDGE,"E0")])]}),"instanceName":"1"}),"instanceName":"1"}),"instanceName":"1"}),"instanceName":"1"});
            var Q52;
            Q52=makeQuery(id+"F18.opPattern","COPY",BODY,{"derivedFrom":makeQuery(id+"F17.opPattern","COPY",BODY,{"derivedFrom":makeQuery(id+"F16.opPattern","COPY",BODY,{"derivedFrom":makeQuery(id+"F11.opPattern","COPY",BODY,{"derivedFrom":makeQuery(id+"F4.opPattern","COPY",BODY,{"derivedFrom":makeQuery(id+"F1.opExtrude","SWEPT_BODY",BODY,{"disambiguationData":[OSD([sQuery(id+"F0.wireOp",EDGE,"E0")])]}),"instanceName":"1"}),"instanceName":"1"}),"instanceName":"1"}),"instanceName":"1"}),"instanceName":"1"});
            var Q53;
            Q53=makeQuery(id+"F18.opPattern","COPY",BODY,{"derivedFrom":makeQuery(id+"F17.opPattern","COPY",BODY,{"derivedFrom":makeQuery(id+"F16.opPattern","COPY",BODY,{"derivedFrom":makeQuery(id+"F4.opPattern","COPY",BODY,{"derivedFrom":makeQuery(id+"F1.opExtrude","SWEPT_BODY",BODY,{"disambiguationData":[OSD([sQuery(id+"F0.wireOp",EDGE,"E0")])]}),"instanceName":"1"}),"instanceName":"1"}),"instanceName":"1"}),"instanceName":"1"});
            var Q54;
            Q54=makeQuery(id+"F18.opPattern","COPY",BODY,{"derivedFrom":makeQuery(id+"F17.opPattern","COPY",BODY,{"derivedFrom":makeQuery(id+"F16.opPattern","COPY",BODY,{"derivedFrom":makeQuery(id+"F12.opPattern","COPY",BODY,{"derivedFrom":makeQuery(id+"F9.opPattern","COPY",BODY,{"derivedFrom":makeQuery(id+"F1.opExtrude","SWEPT_BODY",BODY,{"disambiguationData":[OSD([sQuery(id+"F0.wireOp",EDGE,"E0")])]}),"instanceName":"1"}),"instanceName":"1"}),"instanceName":"1"}),"instanceName":"1"}),"instanceName":"1"});
            var Q55;
            Q55=makeQuery(id+"F18.opPattern","COPY",BODY,{"derivedFrom":makeQuery(id+"F17.opPattern","COPY",BODY,{"derivedFrom":makeQuery(id+"F16.opPattern","COPY",BODY,{"derivedFrom":makeQuery(id+"F14.opPattern","COPY",BODY,{"derivedFrom":makeQuery(id+"F1.opExtrude","SWEPT_BODY",BODY,{"disambiguationData":[OSD([sQuery(id+"F0.wireOp",EDGE,"E0")])]}),"instanceName":"1"}),"instanceName":"1"}),"instanceName":"1"}),"instanceName":"1"});
            var Q56;
            Q56=makeQuery(id+"F18.opPattern","COPY",BODY,{"derivedFrom":makeQuery(id+"F17.opPattern","COPY",BODY,{"derivedFrom":makeQuery(id+"F15.opPattern","COPY",BODY,{"derivedFrom":makeQuery(id+"F11.opPattern","COPY",BODY,{"derivedFrom":makeQuery(id+"F9.opPattern","COPY",BODY,{"derivedFrom":makeQuery(id+"F1.opExtrude","SWEPT_BODY",BODY,{"disambiguationData":[OSD([sQuery(id+"F0.wireOp",EDGE,"E0")])]}),"instanceName":"1"}),"instanceName":"1"}),"instanceName":"1"}),"instanceName":"1"}),"instanceName":"1"});
            var Q57;
            Q57=makeQuery(id+"F18.opPattern","COPY",BODY,{"derivedFrom":makeQuery(id+"F17.opPattern","COPY",BODY,{"derivedFrom":makeQuery(id+"F16.opPattern","COPY",BODY,{"derivedFrom":makeQuery(id+"F12.opPattern","COPY",BODY,{"derivedFrom":makeQuery(id+"F11.opPattern","COPY",BODY,{"derivedFrom":makeQuery(id+"F4.opPattern","COPY",BODY,{"derivedFrom":makeQuery(id+"F1.opExtrude","SWEPT_BODY",BODY,{"disambiguationData":[OSD([sQuery(id+"F0.wireOp",EDGE,"E0")])]}),"instanceName":"1"}),"instanceName":"1"}),"instanceName":"1"}),"instanceName":"1"}),"instanceName":"1"}),"instanceName":"1"});
            var Q58;
            Q58=makeQuery(id+"F18.opPattern","COPY",BODY,{"derivedFrom":makeQuery(id+"F17.opPattern","COPY",BODY,{"derivedFrom":makeQuery(id+"F15.opPattern","COPY",BODY,{"derivedFrom":makeQuery(id+"F11.opPattern","COPY",BODY,{"derivedFrom":makeQuery(id+"F10.opPattern","COPY",BODY,{"derivedFrom":makeQuery(id+"F1.opExtrude","SWEPT_BODY",BODY,{"disambiguationData":[OSD([sQuery(id+"F0.wireOp",EDGE,"E0")])]}),"instanceName":"1"}),"instanceName":"1"}),"instanceName":"1"}),"instanceName":"1"}),"instanceName":"1"});
            var Q59;
            Q59=makeQuery(id+"F18.opPattern","COPY",BODY,{"derivedFrom":makeQuery(id+"F17.opPattern","COPY",BODY,{"derivedFrom":makeQuery(id+"F16.opPattern","COPY",BODY,{"derivedFrom":makeQuery(id+"F12.opPattern","COPY",BODY,{"derivedFrom":makeQuery(id+"F4.opPattern","COPY",BODY,{"derivedFrom":makeQuery(id+"F1.opExtrude","SWEPT_BODY",BODY,{"disambiguationData":[OSD([sQuery(id+"F0.wireOp",EDGE,"E0")])]}),"instanceName":"1"}),"instanceName":"1"}),"instanceName":"1"}),"instanceName":"1"}),"instanceName":"1"});
            var Q60;
            Q60=makeQuery(id+"F18.opPattern","COPY",BODY,{"derivedFrom":makeQuery(id+"F17.opPattern","COPY",BODY,{"derivedFrom":makeQuery(id+"F15.opPattern","COPY",BODY,{"derivedFrom":makeQuery(id+"F14.opPattern","COPY",BODY,{"derivedFrom":makeQuery(id+"F4.opPattern","COPY",BODY,{"derivedFrom":makeQuery(id+"F1.opExtrude","SWEPT_BODY",BODY,{"disambiguationData":[OSD([sQuery(id+"F0.wireOp",EDGE,"E0")])]}),"instanceName":"1"}),"instanceName":"1"}),"instanceName":"1"}),"instanceName":"1"}),"instanceName":"1"});
            var Q61;
            Q61=makeQuery(id+"F18.opPattern","COPY",BODY,{"derivedFrom":makeQuery(id+"F17.opPattern","COPY",BODY,{"derivedFrom":makeQuery(id+"F15.opPattern","COPY",BODY,{"derivedFrom":makeQuery(id+"F14.opPattern","COPY",BODY,{"derivedFrom":makeQuery(id+"F11.opPattern","COPY",BODY,{"derivedFrom":makeQuery(id+"F1.opExtrude","SWEPT_BODY",BODY,{"disambiguationData":[OSD([sQuery(id+"F0.wireOp",EDGE,"E0")])]}),"instanceName":"1"}),"instanceName":"1"}),"instanceName":"1"}),"instanceName":"1"}),"instanceName":"1"});
            var Q62;
            Q62=makeQuery(id+"F18.opPattern","COPY",BODY,{"derivedFrom":makeQuery(id+"F17.opPattern","COPY",BODY,{"derivedFrom":makeQuery(id+"F16.opPattern","COPY",BODY,{"derivedFrom":makeQuery(id+"F14.opPattern","COPY",BODY,{"derivedFrom":makeQuery(id+"F11.opPattern","COPY",BODY,{"derivedFrom":makeQuery(id+"F9.opPattern","COPY",BODY,{"derivedFrom":makeQuery(id+"F1.opExtrude","SWEPT_BODY",BODY,{"disambiguationData":[OSD([sQuery(id+"F0.wireOp",EDGE,"E0")])]}),"instanceName":"1"}),"instanceName":"1"}),"instanceName":"1"}),"instanceName":"1"}),"instanceName":"1"}),"instanceName":"1"});
            var Q63;
            Q63=makeQuery(id+"F18.opPattern","COPY",BODY,{"derivedFrom":makeQuery(id+"F17.opPattern","COPY",BODY,{"derivedFrom":makeQuery(id+"F16.opPattern","COPY",BODY,{"derivedFrom":makeQuery(id+"F12.opPattern","COPY",BODY,{"derivedFrom":makeQuery(id+"F11.opPattern","COPY",BODY,{"derivedFrom":makeQuery(id+"F10.opPattern","COPY",BODY,{"derivedFrom":makeQuery(id+"F1.opExtrude","SWEPT_BODY",BODY,{"disambiguationData":[OSD([sQuery(id+"F0.wireOp",EDGE,"E0")])]}),"instanceName":"1"}),"instanceName":"1"}),"instanceName":"1"}),"instanceName":"1"}),"instanceName":"1"}),"instanceName":"1"});
            var Q64;
            Q64=makeQuery(id+"F18.opPattern","COPY",BODY,{"derivedFrom":makeQuery(id+"F17.opPattern","COPY",BODY,{"derivedFrom":makeQuery(id+"F16.opPattern","COPY",BODY,{"derivedFrom":makeQuery(id+"F14.opPattern","COPY",BODY,{"derivedFrom":makeQuery(id+"F11.opPattern","COPY",BODY,{"derivedFrom":makeQuery(id+"F10.opPattern","COPY",BODY,{"derivedFrom":makeQuery(id+"F1.opExtrude","SWEPT_BODY",BODY,{"disambiguationData":[OSD([sQuery(id+"F0.wireOp",EDGE,"E0")])]}),"instanceName":"1"}),"instanceName":"1"}),"instanceName":"1"}),"instanceName":"1"}),"instanceName":"1"}),"instanceName":"1"});
            var Q65;
            Q65=makeQuery(id+"F18.opPattern","COPY",BODY,{"derivedFrom":makeQuery(id+"F17.opPattern","COPY",BODY,{"derivedFrom":makeQuery(id+"F16.opPattern","COPY",BODY,{"derivedFrom":makeQuery(id+"F10.opPattern","COPY",BODY,{"derivedFrom":makeQuery(id+"F1.opExtrude","SWEPT_BODY",BODY,{"disambiguationData":[OSD([sQuery(id+"F0.wireOp",EDGE,"E0")])]}),"instanceName":"1"}),"instanceName":"1"}),"instanceName":"1"}),"instanceName":"1"});
            var Q66;
            Q66=makeQuery(id+"F18.opPattern","COPY",BODY,{"derivedFrom":makeQuery(id+"F17.opPattern","COPY",BODY,{"derivedFrom":makeQuery(id+"F15.opPattern","COPY",BODY,{"derivedFrom":makeQuery(id+"F14.opPattern","COPY",BODY,{"derivedFrom":makeQuery(id+"F11.opPattern","COPY",BODY,{"derivedFrom":makeQuery(id+"F9.opPattern","COPY",BODY,{"derivedFrom":makeQuery(id+"F4.opPattern","COPY",BODY,{"derivedFrom":makeQuery(id+"F1.opExtrude","SWEPT_BODY",BODY,{"disambiguationData":[OSD([sQuery(id+"F0.wireOp",EDGE,"E0")])]}),"instanceName":"1"}),"instanceName":"1"}),"instanceName":"1"}),"instanceName":"1"}),"instanceName":"1"}),"instanceName":"1"}),"instanceName":"1"});
            var Q67;
            Q67=makeQuery(id+"F12.opPattern","COPY",BODY,{"derivedFrom":makeQuery(id+"F10.opPattern","COPY",BODY,{"derivedFrom":makeQuery(id+"F1.opExtrude","SWEPT_BODY",BODY,{"disambiguationData":[OSD([sQuery(id+"F0.wireOp",EDGE,"E0")])]}),"instanceName":"1"}),"instanceName":"1"});
            var Q68;
            Q68=makeQuery(id+"F14.opPattern","COPY",BODY,{"derivedFrom":makeQuery(id+"F11.opPattern","COPY",BODY,{"derivedFrom":makeQuery(id+"F10.opPattern","COPY",BODY,{"derivedFrom":makeQuery(id+"F1.opExtrude","SWEPT_BODY",BODY,{"disambiguationData":[OSD([sQuery(id+"F0.wireOp",EDGE,"E0")])]}),"instanceName":"1"}),"instanceName":"1"}),"instanceName":"1"});
            var Q69;
            Q69=makeQuery(id+"F18.opPattern","COPY",BODY,{"derivedFrom":makeQuery(id+"F17.opPattern","COPY",BODY,{"derivedFrom":makeQuery(id+"F15.opPattern","COPY",BODY,{"derivedFrom":makeQuery(id+"F12.opPattern","COPY",BODY,{"derivedFrom":makeQuery(id+"F9.opPattern","COPY",BODY,{"derivedFrom":makeQuery(id+"F1.opExtrude","SWEPT_BODY",BODY,{"disambiguationData":[OSD([sQuery(id+"F0.wireOp",EDGE,"E0")])]}),"instanceName":"1"}),"instanceName":"1"}),"instanceName":"1"}),"instanceName":"1"}),"instanceName":"1"});
            var Q70;
            Q70=makeQuery(id+"F18.opPattern","COPY",BODY,{"derivedFrom":makeQuery(id+"F17.opPattern","COPY",BODY,{"derivedFrom":makeQuery(id+"F15.opPattern","COPY",BODY,{"derivedFrom":makeQuery(id+"F12.opPattern","COPY",BODY,{"derivedFrom":makeQuery(id+"F11.opPattern","COPY",BODY,{"derivedFrom":makeQuery(id+"F10.opPattern","COPY",BODY,{"derivedFrom":makeQuery(id+"F1.opExtrude","SWEPT_BODY",BODY,{"disambiguationData":[OSD([sQuery(id+"F0.wireOp",EDGE,"E0")])]}),"instanceName":"1"}),"instanceName":"1"}),"instanceName":"1"}),"instanceName":"1"}),"instanceName":"1"}),"instanceName":"1"});
            var Q71;
            Q71=makeQuery(id+"F18.opPattern","COPY",BODY,{"derivedFrom":makeQuery(id+"F17.opPattern","COPY",BODY,{"derivedFrom":makeQuery(id+"F16.opPattern","COPY",BODY,{"derivedFrom":makeQuery(id+"F11.opPattern","COPY",BODY,{"derivedFrom":makeQuery(id+"F9.opPattern","COPY",BODY,{"derivedFrom":makeQuery(id+"F4.opPattern","COPY",BODY,{"derivedFrom":makeQuery(id+"F1.opExtrude","SWEPT_BODY",BODY,{"disambiguationData":[OSD([sQuery(id+"F0.wireOp",EDGE,"E0")])]}),"instanceName":"1"}),"instanceName":"1"}),"instanceName":"1"}),"instanceName":"1"}),"instanceName":"1"}),"instanceName":"1"});
            var Q72;
            Q72=makeQuery(id+"F18.opPattern","COPY",BODY,{"derivedFrom":makeQuery(id+"F17.opPattern","COPY",BODY,{"derivedFrom":makeQuery(id+"F15.opPattern","COPY",BODY,{"derivedFrom":makeQuery(id+"F12.opPattern","COPY",BODY,{"derivedFrom":makeQuery(id+"F11.opPattern","COPY",BODY,{"derivedFrom":makeQuery(id+"F9.opPattern","COPY",BODY,{"derivedFrom":makeQuery(id+"F1.opExtrude","SWEPT_BODY",BODY,{"disambiguationData":[OSD([sQuery(id+"F0.wireOp",EDGE,"E0")])]}),"instanceName":"1"}),"instanceName":"1"}),"instanceName":"1"}),"instanceName":"1"}),"instanceName":"1"}),"instanceName":"1"});
            var Q73;
            Q73=makeQuery(id+"F18.opPattern","COPY",BODY,{"derivedFrom":makeQuery(id+"F17.opPattern","COPY",BODY,{"derivedFrom":makeQuery(id+"F16.opPattern","COPY",BODY,{"derivedFrom":makeQuery(id+"F9.opPattern","COPY",BODY,{"derivedFrom":makeQuery(id+"F4.opPattern","COPY",BODY,{"derivedFrom":makeQuery(id+"F1.opExtrude","SWEPT_BODY",BODY,{"disambiguationData":[OSD([sQuery(id+"F0.wireOp",EDGE,"E0")])]}),"instanceName":"1"}),"instanceName":"1"}),"instanceName":"1"}),"instanceName":"1"}),"instanceName":"1"});
            var Q74;
            Q74=makeQuery(id+"F18.opPattern","COPY",BODY,{"derivedFrom":makeQuery(id+"F17.opPattern","COPY",BODY,{"derivedFrom":makeQuery(id+"F16.opPattern","COPY",BODY,{"derivedFrom":makeQuery(id+"F11.opPattern","COPY",BODY,{"derivedFrom":makeQuery(id+"F1.opExtrude","SWEPT_BODY",BODY,{"disambiguationData":[OSD([sQuery(id+"F0.wireOp",EDGE,"E0")])]}),"instanceName":"1"}),"instanceName":"1"}),"instanceName":"1"}),"instanceName":"1"});
            var Q75;
            Q75=makeQuery(id+"F18.opPattern","COPY",BODY,{"derivedFrom":makeQuery(id+"F17.opPattern","COPY",BODY,{"derivedFrom":makeQuery(id+"F16.opPattern","COPY",BODY,{"derivedFrom":makeQuery(id+"F1.opExtrude","SWEPT_BODY",BODY,{"disambiguationData":[OSD([sQuery(id+"F0.wireOp",EDGE,"E0")])]}),"instanceName":"1"}),"instanceName":"1"}),"instanceName":"1"});
            var Q76;
            Q76=makeQuery(id+"F18.opPattern","COPY",BODY,{"derivedFrom":makeQuery(id+"F17.opPattern","COPY",BODY,{"derivedFrom":makeQuery(id+"F16.opPattern","COPY",BODY,{"derivedFrom":makeQuery(id+"F12.opPattern","COPY",BODY,{"derivedFrom":makeQuery(id+"F10.opPattern","COPY",BODY,{"derivedFrom":makeQuery(id+"F1.opExtrude","SWEPT_BODY",BODY,{"disambiguationData":[OSD([sQuery(id+"F0.wireOp",EDGE,"E0")])]}),"instanceName":"1"}),"instanceName":"1"}),"instanceName":"1"}),"instanceName":"1"}),"instanceName":"1"});
            var Q77;
            Q77=makeQuery(id+"F18.opPattern","COPY",BODY,{"derivedFrom":makeQuery(id+"F17.opPattern","COPY",BODY,{"derivedFrom":makeQuery(id+"F16.opPattern","COPY",BODY,{"derivedFrom":makeQuery(id+"F14.opPattern","COPY",BODY,{"derivedFrom":makeQuery(id+"F11.opPattern","COPY",BODY,{"derivedFrom":makeQuery(id+"F4.opPattern","COPY",BODY,{"derivedFrom":makeQuery(id+"F1.opExtrude","SWEPT_BODY",BODY,{"disambiguationData":[OSD([sQuery(id+"F0.wireOp",EDGE,"E0")])]}),"instanceName":"1"}),"instanceName":"1"}),"instanceName":"1"}),"instanceName":"1"}),"instanceName":"1"}),"instanceName":"1"});
            var Q78;
            Q78=makeQuery(id+"F18.opPattern","COPY",BODY,{"derivedFrom":makeQuery(id+"F17.opPattern","COPY",BODY,{"derivedFrom":makeQuery(id+"F16.opPattern","COPY",BODY,{"derivedFrom":makeQuery(id+"F12.opPattern","COPY",BODY,{"derivedFrom":makeQuery(id+"F11.opPattern","COPY",BODY,{"derivedFrom":makeQuery(id+"F1.opExtrude","SWEPT_BODY",BODY,{"disambiguationData":[OSD([sQuery(id+"F0.wireOp",EDGE,"E0")])]}),"instanceName":"1"}),"instanceName":"1"}),"instanceName":"1"}),"instanceName":"1"}),"instanceName":"1"});
            var Q79;
            Q79=makeQuery(id+"F18.opPattern","COPY",BODY,{"derivedFrom":makeQuery(id+"F17.opPattern","COPY",BODY,{"derivedFrom":makeQuery(id+"F15.opPattern","COPY",BODY,{"derivedFrom":makeQuery(id+"F12.opPattern","COPY",BODY,{"derivedFrom":makeQuery(id+"F11.opPattern","COPY",BODY,{"derivedFrom":makeQuery(id+"F4.opPattern","COPY",BODY,{"derivedFrom":makeQuery(id+"F1.opExtrude","SWEPT_BODY",BODY,{"disambiguationData":[OSD([sQuery(id+"F0.wireOp",EDGE,"E0")])]}),"instanceName":"1"}),"instanceName":"1"}),"instanceName":"1"}),"instanceName":"1"}),"instanceName":"1"}),"instanceName":"1"});
            var Q80;
            Q80=makeQuery(id+"F18.opPattern","COPY",BODY,{"derivedFrom":makeQuery(id+"F17.opPattern","COPY",BODY,{"derivedFrom":makeQuery(id+"F16.opPattern","COPY",BODY,{"derivedFrom":makeQuery(id+"F12.opPattern","COPY",BODY,{"derivedFrom":makeQuery(id+"F11.opPattern","COPY",BODY,{"derivedFrom":makeQuery(id+"F9.opPattern","COPY",BODY,{"derivedFrom":makeQuery(id+"F4.opPattern","COPY",BODY,{"derivedFrom":makeQuery(id+"F1.opExtrude","SWEPT_BODY",BODY,{"disambiguationData":[OSD([sQuery(id+"F0.wireOp",EDGE,"E0")])]}),"instanceName":"1"}),"instanceName":"1"}),"instanceName":"1"}),"instanceName":"1"}),"instanceName":"1"}),"instanceName":"1"}),"instanceName":"1"});
            var Q81;
            Q81=makeQuery(id+"F14.opPattern","COPY",BODY,{"derivedFrom":makeQuery(id+"F11.opPattern","COPY",BODY,{"derivedFrom":makeQuery(id+"F9.opPattern","COPY",BODY,{"derivedFrom":makeQuery(id+"F1.opExtrude","SWEPT_BODY",BODY,{"disambiguationData":[OSD([sQuery(id+"F0.wireOp",EDGE,"E0")])]}),"instanceName":"1"}),"instanceName":"1"}),"instanceName":"1"});
            var Q82;
            Q82=makeQuery(id+"F15.opPattern","COPY",BODY,{"derivedFrom":makeQuery(id+"F10.opPattern","COPY",BODY,{"derivedFrom":makeQuery(id+"F1.opExtrude","SWEPT_BODY",BODY,{"disambiguationData":[OSD([sQuery(id+"F0.wireOp",EDGE,"E0")])]}),"instanceName":"1"}),"instanceName":"1"});
            var Q83;
            Q83=makeQuery(id+"F15.opPattern","COPY",BODY,{"derivedFrom":makeQuery(id+"F14.opPattern","COPY",BODY,{"derivedFrom":makeQuery(id+"F4.opPattern","COPY",BODY,{"derivedFrom":makeQuery(id+"F1.opExtrude","SWEPT_BODY",BODY,{"disambiguationData":[OSD([sQuery(id+"F0.wireOp",EDGE,"E0")])]}),"instanceName":"1"}),"instanceName":"1"}),"instanceName":"1"});
            var Q84;
            Q84=makeQuery(id+"F15.opPattern","COPY",BODY,{"derivedFrom":makeQuery(id+"F12.opPattern","COPY",BODY,{"derivedFrom":makeQuery(id+"F11.opPattern","COPY",BODY,{"derivedFrom":makeQuery(id+"F4.opPattern","COPY",BODY,{"derivedFrom":makeQuery(id+"F1.opExtrude","SWEPT_BODY",BODY,{"disambiguationData":[OSD([sQuery(id+"F0.wireOp",EDGE,"E0")])]}),"instanceName":"1"}),"instanceName":"1"}),"instanceName":"1"}),"instanceName":"1"});
            var Q85;
            Q85=makeQuery(id+"F15.opPattern","COPY",BODY,{"derivedFrom":makeQuery(id+"F14.opPattern","COPY",BODY,{"derivedFrom":makeQuery(id+"F11.opPattern","COPY",BODY,{"derivedFrom":makeQuery(id+"F10.opPattern","COPY",BODY,{"derivedFrom":makeQuery(id+"F1.opExtrude","SWEPT_BODY",BODY,{"disambiguationData":[OSD([sQuery(id+"F0.wireOp",EDGE,"E0")])]}),"instanceName":"1"}),"instanceName":"1"}),"instanceName":"1"}),"instanceName":"1"});
            var Q86;
            Q86=makeQuery(id+"F18.opPattern","COPY",BODY,{"derivedFrom":makeQuery(id+"F17.opPattern","COPY",BODY,{"derivedFrom":makeQuery(id+"F16.opPattern","COPY",BODY,{"derivedFrom":makeQuery(id+"F9.opPattern","COPY",BODY,{"derivedFrom":makeQuery(id+"F1.opExtrude","SWEPT_BODY",BODY,{"disambiguationData":[OSD([sQuery(id+"F0.wireOp",EDGE,"E0")])]}),"instanceName":"1"}),"instanceName":"1"}),"instanceName":"1"}),"instanceName":"1"});
            var Q87;
            Q87=makeQuery(id+"F15.opPattern","COPY",BODY,{"derivedFrom":makeQuery(id+"F12.opPattern","COPY",BODY,{"derivedFrom":makeQuery(id+"F11.opPattern","COPY",BODY,{"derivedFrom":makeQuery(id+"F9.opPattern","COPY",BODY,{"derivedFrom":makeQuery(id+"F4.opPattern","COPY",BODY,{"derivedFrom":makeQuery(id+"F1.opExtrude","SWEPT_BODY",BODY,{"disambiguationData":[OSD([sQuery(id+"F0.wireOp",EDGE,"E0")])]}),"instanceName":"1"}),"instanceName":"1"}),"instanceName":"1"}),"instanceName":"1"}),"instanceName":"1"});
            var Q88;
            Q88=makeQuery(id+"F15.opPattern","COPY",BODY,{"derivedFrom":makeQuery(id+"F12.opPattern","COPY",BODY,{"derivedFrom":makeQuery(id+"F9.opPattern","COPY",BODY,{"derivedFrom":makeQuery(id+"F1.opExtrude","SWEPT_BODY",BODY,{"disambiguationData":[OSD([sQuery(id+"F0.wireOp",EDGE,"E0")])]}),"instanceName":"1"}),"instanceName":"1"}),"instanceName":"1"});
            var Q89;
            Q89=makeQuery(id+"F15.opPattern","COPY",BODY,{"derivedFrom":makeQuery(id+"F14.opPattern","COPY",BODY,{"derivedFrom":makeQuery(id+"F11.opPattern","COPY",BODY,{"derivedFrom":makeQuery(id+"F9.opPattern","COPY",BODY,{"derivedFrom":makeQuery(id+"F4.opPattern","COPY",BODY,{"derivedFrom":makeQuery(id+"F1.opExtrude","SWEPT_BODY",BODY,{"disambiguationData":[OSD([sQuery(id+"F0.wireOp",EDGE,"E0")])]}),"instanceName":"1"}),"instanceName":"1"}),"instanceName":"1"}),"instanceName":"1"}),"instanceName":"1"});
            var Q90;
            Q90=makeQuery(id+"F15.opPattern","COPY",BODY,{"derivedFrom":makeQuery(id+"F14.opPattern","COPY",BODY,{"derivedFrom":makeQuery(id+"F1.opExtrude","SWEPT_BODY",BODY,{"disambiguationData":[OSD([sQuery(id+"F0.wireOp",EDGE,"E0")])]}),"instanceName":"1"}),"instanceName":"1"});
            var Q91;
            Q91=makeQuery(id+"F15.opPattern","COPY",BODY,{"derivedFrom":makeQuery(id+"F12.opPattern","COPY",BODY,{"derivedFrom":makeQuery(id+"F11.opPattern","COPY",BODY,{"derivedFrom":makeQuery(id+"F1.opExtrude","SWEPT_BODY",BODY,{"disambiguationData":[OSD([sQuery(id+"F0.wireOp",EDGE,"E0")])]}),"instanceName":"1"}),"instanceName":"1"}),"instanceName":"1"});
            var Q92;
            Q92=makeQuery(id+"F15.opPattern","COPY",BODY,{"derivedFrom":makeQuery(id+"F12.opPattern","COPY",BODY,{"derivedFrom":makeQuery(id+"F4.opPattern","COPY",BODY,{"derivedFrom":makeQuery(id+"F1.opExtrude","SWEPT_BODY",BODY,{"disambiguationData":[OSD([sQuery(id+"F0.wireOp",EDGE,"E0")])]}),"instanceName":"1"}),"instanceName":"1"}),"instanceName":"1"});
            var Q93;
            Q93=makeQuery(id+"F15.opPattern","COPY",BODY,{"derivedFrom":makeQuery(id+"F14.opPattern","COPY",BODY,{"derivedFrom":makeQuery(id+"F10.opPattern","COPY",BODY,{"derivedFrom":makeQuery(id+"F1.opExtrude","SWEPT_BODY",BODY,{"disambiguationData":[OSD([sQuery(id+"F0.wireOp",EDGE,"E0")])]}),"instanceName":"1"}),"instanceName":"1"}),"instanceName":"1"});
            var Q94;
            Q94=makeQuery(id+"F14.opPattern","COPY",BODY,{"derivedFrom":makeQuery(id+"F11.opPattern","COPY",BODY,{"derivedFrom":makeQuery(id+"F9.opPattern","COPY",BODY,{"derivedFrom":makeQuery(id+"F4.opPattern","COPY",BODY,{"derivedFrom":makeQuery(id+"F1.opExtrude","SWEPT_BODY",BODY,{"disambiguationData":[OSD([sQuery(id+"F0.wireOp",EDGE,"E0")])]}),"instanceName":"1"}),"instanceName":"1"}),"instanceName":"1"}),"instanceName":"1"});
            var Q95;
            Q95=makeQuery(id+"F15.opPattern","COPY",BODY,{"derivedFrom":makeQuery(id+"F14.opPattern","COPY",BODY,{"derivedFrom":makeQuery(id+"F11.opPattern","COPY",BODY,{"derivedFrom":makeQuery(id+"F1.opExtrude","SWEPT_BODY",BODY,{"disambiguationData":[OSD([sQuery(id+"F0.wireOp",EDGE,"E0")])]}),"instanceName":"1"}),"instanceName":"1"}),"instanceName":"1"});
            var Q96;
            Q96=makeQuery(id+"F14.opPattern","COPY",BODY,{"derivedFrom":makeQuery(id+"F11.opPattern","COPY",BODY,{"derivedFrom":makeQuery(id+"F1.opExtrude","SWEPT_BODY",BODY,{"disambiguationData":[OSD([sQuery(id+"F0.wireOp",EDGE,"E0")])]}),"instanceName":"1"}),"instanceName":"1"});
            var Q97;
            Q97=makeQuery(id+"F18.opPattern","COPY",BODY,{"derivedFrom":makeQuery(id+"F17.opPattern","COPY",BODY,{"derivedFrom":makeQuery(id+"F14.opPattern","COPY",BODY,{"derivedFrom":makeQuery(id+"F11.opPattern","COPY",BODY,{"derivedFrom":makeQuery(id+"F10.opPattern","COPY",BODY,{"derivedFrom":makeQuery(id+"F1.opExtrude","SWEPT_BODY",BODY,{"disambiguationData":[OSD([sQuery(id+"F0.wireOp",EDGE,"E0")])]}),"instanceName":"1"}),"instanceName":"1"}),"instanceName":"1"}),"instanceName":"1"}),"instanceName":"1"});
            var Q98;
            Q98=makeQuery(id+"F18.opPattern","COPY",BODY,{"derivedFrom":makeQuery(id+"F17.opPattern","COPY",BODY,{"derivedFrom":makeQuery(id+"F14.opPattern","COPY",BODY,{"derivedFrom":makeQuery(id+"F4.opPattern","COPY",BODY,{"derivedFrom":makeQuery(id+"F1.opExtrude","SWEPT_BODY",BODY,{"disambiguationData":[OSD([sQuery(id+"F0.wireOp",EDGE,"E0")])]}),"instanceName":"1"}),"instanceName":"1"}),"instanceName":"1"}),"instanceName":"1"});
            var Q99;
            Q99=makeQuery(id+"F18.opPattern","COPY",BODY,{"derivedFrom":makeQuery(id+"F10.opPattern","COPY",BODY,{"derivedFrom":makeQuery(id+"F1.opExtrude","SWEPT_BODY",BODY,{"disambiguationData":[OSD([sQuery(id+"F0.wireOp",EDGE,"E0")])]}),"instanceName":"1"}),"instanceName":"1"});
            var Q100;
            Q100=makeQuery(id+"F18.opPattern","COPY",BODY,{"derivedFrom":makeQuery(id+"F12.opPattern","COPY",BODY,{"derivedFrom":makeQuery(id+"F11.opPattern","COPY",BODY,{"derivedFrom":makeQuery(id+"F4.opPattern","COPY",BODY,{"derivedFrom":makeQuery(id+"F1.opExtrude","SWEPT_BODY",BODY,{"disambiguationData":[OSD([sQuery(id+"F0.wireOp",EDGE,"E0")])]}),"instanceName":"1"}),"instanceName":"1"}),"instanceName":"1"}),"instanceName":"1"});
            var Q101;
            Q101=makeQuery(id+"F18.opPattern","COPY",BODY,{"derivedFrom":makeQuery(id+"F14.opPattern","COPY",BODY,{"derivedFrom":makeQuery(id+"F11.opPattern","COPY",BODY,{"derivedFrom":makeQuery(id+"F10.opPattern","COPY",BODY,{"derivedFrom":makeQuery(id+"F1.opExtrude","SWEPT_BODY",BODY,{"disambiguationData":[OSD([sQuery(id+"F0.wireOp",EDGE,"E0")])]}),"instanceName":"1"}),"instanceName":"1"}),"instanceName":"1"}),"instanceName":"1"});
            var Q102;
            Q102=makeQuery(id+"F18.opPattern","COPY",BODY,{"derivedFrom":makeQuery(id+"F14.opPattern","COPY",BODY,{"derivedFrom":makeQuery(id+"F4.opPattern","COPY",BODY,{"derivedFrom":makeQuery(id+"F1.opExtrude","SWEPT_BODY",BODY,{"disambiguationData":[OSD([sQuery(id+"F0.wireOp",EDGE,"E0")])]}),"instanceName":"1"}),"instanceName":"1"}),"instanceName":"1"});
            var Q103;
            Q103=makeQuery(id+"F18.opPattern","COPY",BODY,{"derivedFrom":makeQuery(id+"F15.opPattern","COPY",BODY,{"derivedFrom":makeQuery(id+"F12.opPattern","COPY",BODY,{"derivedFrom":makeQuery(id+"F11.opPattern","COPY",BODY,{"derivedFrom":makeQuery(id+"F9.opPattern","COPY",BODY,{"derivedFrom":makeQuery(id+"F1.opExtrude","SWEPT_BODY",BODY,{"disambiguationData":[OSD([sQuery(id+"F0.wireOp",EDGE,"E0")])]}),"instanceName":"1"}),"instanceName":"1"}),"instanceName":"1"}),"instanceName":"1"}),"instanceName":"1"});
            var Q104;
            Q104=makeQuery(id+"F18.opPattern","COPY",BODY,{"derivedFrom":makeQuery(id+"F15.opPattern","COPY",BODY,{"derivedFrom":makeQuery(id+"F12.opPattern","COPY",BODY,{"derivedFrom":makeQuery(id+"F9.opPattern","COPY",BODY,{"derivedFrom":makeQuery(id+"F4.opPattern","COPY",BODY,{"derivedFrom":makeQuery(id+"F1.opExtrude","SWEPT_BODY",BODY,{"disambiguationData":[OSD([sQuery(id+"F0.wireOp",EDGE,"E0")])]}),"instanceName":"1"}),"instanceName":"1"}),"instanceName":"1"}),"instanceName":"1"}),"instanceName":"1"});
            var Q105;
            Q105=makeQuery(id+"F18.opPattern","COPY",BODY,{"derivedFrom":makeQuery(id+"F15.opPattern","COPY",BODY,{"derivedFrom":makeQuery(id+"F12.opPattern","COPY",BODY,{"derivedFrom":makeQuery(id+"F1.opExtrude","SWEPT_BODY",BODY,{"disambiguationData":[OSD([sQuery(id+"F0.wireOp",EDGE,"E0")])]}),"instanceName":"1"}),"instanceName":"1"}),"instanceName":"1"});
            var Q106;
            Q106=makeQuery(id+"F15.opPattern","COPY",BODY,{"derivedFrom":makeQuery(id+"F11.opPattern","COPY",BODY,{"derivedFrom":makeQuery(id+"F9.opPattern","COPY",BODY,{"derivedFrom":makeQuery(id+"F1.opExtrude","SWEPT_BODY",BODY,{"disambiguationData":[OSD([sQuery(id+"F0.wireOp",EDGE,"E0")])]}),"instanceName":"1"}),"instanceName":"1"}),"instanceName":"1"});
            var Q107;
            Q107=makeQuery(id+"F15.opPattern","COPY",BODY,{"derivedFrom":makeQuery(id+"F12.opPattern","COPY",BODY,{"derivedFrom":makeQuery(id+"F9.opPattern","COPY",BODY,{"derivedFrom":makeQuery(id+"F4.opPattern","COPY",BODY,{"derivedFrom":makeQuery(id+"F1.opExtrude","SWEPT_BODY",BODY,{"disambiguationData":[OSD([sQuery(id+"F0.wireOp",EDGE,"E0")])]}),"instanceName":"1"}),"instanceName":"1"}),"instanceName":"1"}),"instanceName":"1"});
            var Q108;
            Q108=makeQuery(id+"F18.opPattern","COPY",BODY,{"derivedFrom":makeQuery(id+"F17.opPattern","COPY",BODY,{"derivedFrom":makeQuery(id+"F12.opPattern","COPY",BODY,{"derivedFrom":makeQuery(id+"F11.opPattern","COPY",BODY,{"derivedFrom":makeQuery(id+"F4.opPattern","COPY",BODY,{"derivedFrom":makeQuery(id+"F1.opExtrude","SWEPT_BODY",BODY,{"disambiguationData":[OSD([sQuery(id+"F0.wireOp",EDGE,"E0")])]}),"instanceName":"1"}),"instanceName":"1"}),"instanceName":"1"}),"instanceName":"1"}),"instanceName":"1"});
            var Q109;
            Q109=makeQuery(id+"F18.opPattern","COPY",BODY,{"derivedFrom":makeQuery(id+"F17.opPattern","COPY",BODY,{"derivedFrom":makeQuery(id+"F9.opPattern","COPY",BODY,{"derivedFrom":makeQuery(id+"F1.opExtrude","SWEPT_BODY",BODY,{"disambiguationData":[OSD([sQuery(id+"F0.wireOp",EDGE,"E0")])]}),"instanceName":"1"}),"instanceName":"1"}),"instanceName":"1"});
            var Q110;
            Q110=makeQuery(id+"F18.opPattern","COPY",BODY,{"derivedFrom":makeQuery(id+"F16.opPattern","COPY",BODY,{"derivedFrom":makeQuery(id+"F15.opPattern","COPY",BODY,{"derivedFrom":makeQuery(id+"F14.opPattern","COPY",BODY,{"derivedFrom":makeQuery(id+"F11.opPattern","COPY",BODY,{"derivedFrom":makeQuery(id+"F9.opPattern","COPY",BODY,{"derivedFrom":makeQuery(id+"F1.opExtrude","SWEPT_BODY",BODY,{"disambiguationData":[OSD([sQuery(id+"F0.wireOp",EDGE,"E0")])]}),"instanceName":"1"}),"instanceName":"1"}),"instanceName":"1"}),"instanceName":"1"}),"instanceName":"1"}),"instanceName":"1"});
            var Q111;
            Q111=makeQuery(id+"F18.opPattern","COPY",BODY,{"derivedFrom":makeQuery(id+"F16.opPattern","COPY",BODY,{"derivedFrom":makeQuery(id+"F15.opPattern","COPY",BODY,{"derivedFrom":makeQuery(id+"F14.opPattern","COPY",BODY,{"derivedFrom":makeQuery(id+"F11.opPattern","COPY",BODY,{"derivedFrom":makeQuery(id+"F4.opPattern","COPY",BODY,{"derivedFrom":makeQuery(id+"F1.opExtrude","SWEPT_BODY",BODY,{"disambiguationData":[OSD([sQuery(id+"F0.wireOp",EDGE,"E0")])]}),"instanceName":"1"}),"instanceName":"1"}),"instanceName":"1"}),"instanceName":"1"}),"instanceName":"1"}),"instanceName":"1"});
            var Q112;
            Q112=makeQuery(id+"F18.opPattern","COPY",BODY,{"derivedFrom":makeQuery(id+"F17.opPattern","COPY",BODY,{"derivedFrom":makeQuery(id+"F10.opPattern","COPY",BODY,{"derivedFrom":makeQuery(id+"F1.opExtrude","SWEPT_BODY",BODY,{"disambiguationData":[OSD([sQuery(id+"F0.wireOp",EDGE,"E0")])]}),"instanceName":"1"}),"instanceName":"1"}),"instanceName":"1"});
            var Q113;
            Q113=makeQuery(id+"F18.opPattern","COPY",BODY,{"derivedFrom":makeQuery(id+"F15.opPattern","COPY",BODY,{"derivedFrom":makeQuery(id+"F14.opPattern","COPY",BODY,{"derivedFrom":makeQuery(id+"F10.opPattern","COPY",BODY,{"derivedFrom":makeQuery(id+"F1.opExtrude","SWEPT_BODY",BODY,{"disambiguationData":[OSD([sQuery(id+"F0.wireOp",EDGE,"E0")])]}),"instanceName":"1"}),"instanceName":"1"}),"instanceName":"1"}),"instanceName":"1"});
            var Q114;
            Q114=makeQuery(id+"F18.opPattern","COPY",BODY,{"derivedFrom":makeQuery(id+"F16.opPattern","COPY",BODY,{"derivedFrom":makeQuery(id+"F4.opPattern","COPY",BODY,{"derivedFrom":makeQuery(id+"F1.opExtrude","SWEPT_BODY",BODY,{"disambiguationData":[OSD([sQuery(id+"F0.wireOp",EDGE,"E0")])]}),"instanceName":"1"}),"instanceName":"1"}),"instanceName":"1"});
            var Q115;
            Q115=makeQuery(id+"F18.opPattern","COPY",BODY,{"derivedFrom":makeQuery(id+"F16.opPattern","COPY",BODY,{"derivedFrom":makeQuery(id+"F12.opPattern","COPY",BODY,{"derivedFrom":makeQuery(id+"F9.opPattern","COPY",BODY,{"derivedFrom":makeQuery(id+"F4.opPattern","COPY",BODY,{"derivedFrom":makeQuery(id+"F1.opExtrude","SWEPT_BODY",BODY,{"disambiguationData":[OSD([sQuery(id+"F0.wireOp",EDGE,"E0")])]}),"instanceName":"1"}),"instanceName":"1"}),"instanceName":"1"}),"instanceName":"1"}),"instanceName":"1"});
            var Q116;
            Q116=makeQuery(id+"F18.opPattern","COPY",BODY,{"derivedFrom":makeQuery(id+"F16.opPattern","COPY",BODY,{"derivedFrom":makeQuery(id+"F12.opPattern","COPY",BODY,{"derivedFrom":makeQuery(id+"F1.opExtrude","SWEPT_BODY",BODY,{"disambiguationData":[OSD([sQuery(id+"F0.wireOp",EDGE,"E0")])]}),"instanceName":"1"}),"instanceName":"1"}),"instanceName":"1"});
            var Q117;
            Q117=makeQuery(id+"F18.opPattern","COPY",BODY,{"derivedFrom":makeQuery(id+"F16.opPattern","COPY",BODY,{"derivedFrom":makeQuery(id+"F11.opPattern","COPY",BODY,{"derivedFrom":makeQuery(id+"F9.opPattern","COPY",BODY,{"derivedFrom":makeQuery(id+"F4.opPattern","COPY",BODY,{"derivedFrom":makeQuery(id+"F1.opExtrude","SWEPT_BODY",BODY,{"disambiguationData":[OSD([sQuery(id+"F0.wireOp",EDGE,"E0")])]}),"instanceName":"1"}),"instanceName":"1"}),"instanceName":"1"}),"instanceName":"1"}),"instanceName":"1"});
            var Q118;
            Q118=makeQuery(id+"F18.opPattern","COPY",BODY,{"derivedFrom":makeQuery(id+"F16.opPattern","COPY",BODY,{"derivedFrom":makeQuery(id+"F11.opPattern","COPY",BODY,{"derivedFrom":makeQuery(id+"F1.opExtrude","SWEPT_BODY",BODY,{"disambiguationData":[OSD([sQuery(id+"F0.wireOp",EDGE,"E0")])]}),"instanceName":"1"}),"instanceName":"1"}),"instanceName":"1"});
            var Q119;
            Q119=makeQuery(id+"F18.opPattern","COPY",BODY,{"derivedFrom":makeQuery(id+"F16.opPattern","COPY",BODY,{"derivedFrom":makeQuery(id+"F12.opPattern","COPY",BODY,{"derivedFrom":makeQuery(id+"F11.opPattern","COPY",BODY,{"derivedFrom":makeQuery(id+"F10.opPattern","COPY",BODY,{"derivedFrom":makeQuery(id+"F1.opExtrude","SWEPT_BODY",BODY,{"disambiguationData":[OSD([sQuery(id+"F0.wireOp",EDGE,"E0")])]}),"instanceName":"1"}),"instanceName":"1"}),"instanceName":"1"}),"instanceName":"1"}),"instanceName":"1"});
            var Q120;
            Q120=makeQuery(id+"F18.opPattern","COPY",BODY,{"derivedFrom":makeQuery(id+"F16.opPattern","COPY",BODY,{"derivedFrom":makeQuery(id+"F15.opPattern","COPY",BODY,{"derivedFrom":makeQuery(id+"F9.opPattern","COPY",BODY,{"derivedFrom":makeQuery(id+"F1.opExtrude","SWEPT_BODY",BODY,{"disambiguationData":[OSD([sQuery(id+"F0.wireOp",EDGE,"E0")])]}),"instanceName":"1"}),"instanceName":"1"}),"instanceName":"1"}),"instanceName":"1"});
            var Q121;
            Q121=makeQuery(id+"F18.opPattern","COPY",BODY,{"derivedFrom":makeQuery(id+"F16.opPattern","COPY",BODY,{"derivedFrom":makeQuery(id+"F15.opPattern","COPY",BODY,{"derivedFrom":makeQuery(id+"F4.opPattern","COPY",BODY,{"derivedFrom":makeQuery(id+"F1.opExtrude","SWEPT_BODY",BODY,{"disambiguationData":[OSD([sQuery(id+"F0.wireOp",EDGE,"E0")])]}),"instanceName":"1"}),"instanceName":"1"}),"instanceName":"1"}),"instanceName":"1"});
            var Q122;
            Q122=makeQuery(id+"F18.opPattern","COPY",BODY,{"derivedFrom":makeQuery(id+"F16.opPattern","COPY",BODY,{"derivedFrom":makeQuery(id+"F14.opPattern","COPY",BODY,{"derivedFrom":makeQuery(id+"F11.opPattern","COPY",BODY,{"derivedFrom":makeQuery(id+"F4.opPattern","COPY",BODY,{"derivedFrom":makeQuery(id+"F1.opExtrude","SWEPT_BODY",BODY,{"disambiguationData":[OSD([sQuery(id+"F0.wireOp",EDGE,"E0")])]}),"instanceName":"1"}),"instanceName":"1"}),"instanceName":"1"}),"instanceName":"1"}),"instanceName":"1"});
            var Q123;
            Q123=makeQuery(id+"F18.opPattern","COPY",BODY,{"derivedFrom":makeQuery(id+"F16.opPattern","COPY",BODY,{"derivedFrom":makeQuery(id+"F15.opPattern","COPY",BODY,{"derivedFrom":makeQuery(id+"F11.opPattern","COPY",BODY,{"derivedFrom":makeQuery(id+"F9.opPattern","COPY",BODY,{"derivedFrom":makeQuery(id+"F4.opPattern","COPY",BODY,{"derivedFrom":makeQuery(id+"F1.opExtrude","SWEPT_BODY",BODY,{"disambiguationData":[OSD([sQuery(id+"F0.wireOp",EDGE,"E0")])]}),"instanceName":"1"}),"instanceName":"1"}),"instanceName":"1"}),"instanceName":"1"}),"instanceName":"1"}),"instanceName":"1"});
            var Q124;
            Q124=makeQuery(id+"F18.opPattern","COPY",BODY,{"derivedFrom":makeQuery(id+"F16.opPattern","COPY",BODY,{"derivedFrom":makeQuery(id+"F15.opPattern","COPY",BODY,{"derivedFrom":makeQuery(id+"F14.opPattern","COPY",BODY,{"derivedFrom":makeQuery(id+"F4.opPattern","COPY",BODY,{"derivedFrom":makeQuery(id+"F1.opExtrude","SWEPT_BODY",BODY,{"disambiguationData":[OSD([sQuery(id+"F0.wireOp",EDGE,"E0")])]}),"instanceName":"1"}),"instanceName":"1"}),"instanceName":"1"}),"instanceName":"1"}),"instanceName":"1"});
            var Q125;
            Q125=makeQuery(id+"F18.opPattern","COPY",BODY,{"derivedFrom":makeQuery(id+"F16.opPattern","COPY",BODY,{"derivedFrom":makeQuery(id+"F15.opPattern","COPY",BODY,{"derivedFrom":makeQuery(id+"F12.opPattern","COPY",BODY,{"derivedFrom":makeQuery(id+"F11.opPattern","COPY",BODY,{"derivedFrom":makeQuery(id+"F1.opExtrude","SWEPT_BODY",BODY,{"disambiguationData":[OSD([sQuery(id+"F0.wireOp",EDGE,"E0")])]}),"instanceName":"1"}),"instanceName":"1"}),"instanceName":"1"}),"instanceName":"1"}),"instanceName":"1"});
            var Q126;
            Q126=makeQuery(id+"F18.opPattern","COPY",BODY,{"derivedFrom":makeQuery(id+"F16.opPattern","COPY",BODY,{"derivedFrom":makeQuery(id+"F15.opPattern","COPY",BODY,{"derivedFrom":makeQuery(id+"F12.opPattern","COPY",BODY,{"derivedFrom":makeQuery(id+"F10.opPattern","COPY",BODY,{"derivedFrom":makeQuery(id+"F1.opExtrude","SWEPT_BODY",BODY,{"disambiguationData":[OSD([sQuery(id+"F0.wireOp",EDGE,"E0")])]}),"instanceName":"1"}),"instanceName":"1"}),"instanceName":"1"}),"instanceName":"1"}),"instanceName":"1"});
            var Q127;
            Q127=makeQuery(id+"F18.opPattern","COPY",BODY,{"derivedFrom":makeQuery(id+"F12.opPattern","COPY",BODY,{"derivedFrom":makeQuery(id+"F9.opPattern","COPY",BODY,{"derivedFrom":makeQuery(id+"F1.opExtrude","SWEPT_BODY",BODY,{"disambiguationData":[OSD([sQuery(id+"F0.wireOp",EDGE,"E0")])]}),"instanceName":"1"}),"instanceName":"1"}),"instanceName":"1"});
            var Q128;
            Q128=makeQuery(id+"F18.opPattern","COPY",BODY,{"derivedFrom":makeQuery(id+"F14.opPattern","COPY",BODY,{"derivedFrom":makeQuery(id+"F11.opPattern","COPY",BODY,{"derivedFrom":makeQuery(id+"F9.opPattern","COPY",BODY,{"derivedFrom":makeQuery(id+"F4.opPattern","COPY",BODY,{"derivedFrom":makeQuery(id+"F1.opExtrude","SWEPT_BODY",BODY,{"disambiguationData":[OSD([sQuery(id+"F0.wireOp",EDGE,"E0")])]}),"instanceName":"1"}),"instanceName":"1"}),"instanceName":"1"}),"instanceName":"1"}),"instanceName":"1"});
            var Q129;
            Q129=makeQuery(id+"F18.opPattern","COPY",BODY,{"derivedFrom":makeQuery(id+"F12.opPattern","COPY",BODY,{"derivedFrom":makeQuery(id+"F11.opPattern","COPY",BODY,{"derivedFrom":makeQuery(id+"F9.opPattern","COPY",BODY,{"derivedFrom":makeQuery(id+"F4.opPattern","COPY",BODY,{"derivedFrom":makeQuery(id+"F1.opExtrude","SWEPT_BODY",BODY,{"disambiguationData":[OSD([sQuery(id+"F0.wireOp",EDGE,"E0")])]}),"instanceName":"1"}),"instanceName":"1"}),"instanceName":"1"}),"instanceName":"1"}),"instanceName":"1"});
            var Q130;
            Q130=makeQuery(id+"F18.opPattern","COPY",BODY,{"derivedFrom":makeQuery(id+"F17.opPattern","COPY",BODY,{"derivedFrom":makeQuery(id+"F15.opPattern","COPY",BODY,{"derivedFrom":makeQuery(id+"F11.opPattern","COPY",BODY,{"derivedFrom":makeQuery(id+"F4.opPattern","COPY",BODY,{"derivedFrom":makeQuery(id+"F1.opExtrude","SWEPT_BODY",BODY,{"disambiguationData":[OSD([sQuery(id+"F0.wireOp",EDGE,"E0")])]}),"instanceName":"1"}),"instanceName":"1"}),"instanceName":"1"}),"instanceName":"1"}),"instanceName":"1"});
            var Q131;
            Q131=makeQuery(id+"F18.opPattern","COPY",BODY,{"derivedFrom":makeQuery(id+"F15.opPattern","COPY",BODY,{"derivedFrom":makeQuery(id+"F11.opPattern","COPY",BODY,{"derivedFrom":makeQuery(id+"F4.opPattern","COPY",BODY,{"derivedFrom":makeQuery(id+"F1.opExtrude","SWEPT_BODY",BODY,{"disambiguationData":[OSD([sQuery(id+"F0.wireOp",EDGE,"E0")])]}),"instanceName":"1"}),"instanceName":"1"}),"instanceName":"1"}),"instanceName":"1"});
            var Q132;
            Q132=makeQuery(id+"F18.opPattern","COPY",BODY,{"derivedFrom":makeQuery(id+"F15.opPattern","COPY",BODY,{"derivedFrom":makeQuery(id+"F1.opExtrude","SWEPT_BODY",BODY,{"disambiguationData":[OSD([sQuery(id+"F0.wireOp",EDGE,"E0")])]}),"instanceName":"1"}),"instanceName":"1"});
            var Q133;
            Q133=makeQuery(id+"F18.opPattern","COPY",BODY,{"derivedFrom":makeQuery(id+"F15.opPattern","COPY",BODY,{"derivedFrom":makeQuery(id+"F12.opPattern","COPY",BODY,{"derivedFrom":makeQuery(id+"F11.opPattern","COPY",BODY,{"derivedFrom":makeQuery(id+"F10.opPattern","COPY",BODY,{"derivedFrom":makeQuery(id+"F1.opExtrude","SWEPT_BODY",BODY,{"disambiguationData":[OSD([sQuery(id+"F0.wireOp",EDGE,"E0")])]}),"instanceName":"1"}),"instanceName":"1"}),"instanceName":"1"}),"instanceName":"1"}),"instanceName":"1"});
            var Q134;
            Q134=makeQuery(id+"F18.opPattern","COPY",BODY,{"derivedFrom":makeQuery(id+"F17.opPattern","COPY",BODY,{"derivedFrom":makeQuery(id+"F12.opPattern","COPY",BODY,{"derivedFrom":makeQuery(id+"F11.opPattern","COPY",BODY,{"derivedFrom":makeQuery(id+"F1.opExtrude","SWEPT_BODY",BODY,{"disambiguationData":[OSD([sQuery(id+"F0.wireOp",EDGE,"E0")])]}),"instanceName":"1"}),"instanceName":"1"}),"instanceName":"1"}),"instanceName":"1"});
            var Q135;
            Q135=makeQuery(id+"F18.opPattern","COPY",BODY,{"derivedFrom":makeQuery(id+"F17.opPattern","COPY",BODY,{"derivedFrom":makeQuery(id+"F12.opPattern","COPY",BODY,{"derivedFrom":makeQuery(id+"F4.opPattern","COPY",BODY,{"derivedFrom":makeQuery(id+"F1.opExtrude","SWEPT_BODY",BODY,{"disambiguationData":[OSD([sQuery(id+"F0.wireOp",EDGE,"E0")])]}),"instanceName":"1"}),"instanceName":"1"}),"instanceName":"1"}),"instanceName":"1"});
            var Q136;
            Q136=makeQuery(id+"F18.opPattern","COPY",BODY,{"derivedFrom":makeQuery(id+"F15.opPattern","COPY",BODY,{"derivedFrom":makeQuery(id+"F14.opPattern","COPY",BODY,{"derivedFrom":makeQuery(id+"F11.opPattern","COPY",BODY,{"derivedFrom":makeQuery(id+"F10.opPattern","COPY",BODY,{"derivedFrom":makeQuery(id+"F1.opExtrude","SWEPT_BODY",BODY,{"disambiguationData":[OSD([sQuery(id+"F0.wireOp",EDGE,"E0")])]}),"instanceName":"1"}),"instanceName":"1"}),"instanceName":"1"}),"instanceName":"1"}),"instanceName":"1"});
            var Q137;
            Q137=makeQuery(id+"F18.opPattern","COPY",BODY,{"derivedFrom":makeQuery(id+"F17.opPattern","COPY",BODY,{"derivedFrom":makeQuery(id+"F14.opPattern","COPY",BODY,{"derivedFrom":makeQuery(id+"F10.opPattern","COPY",BODY,{"derivedFrom":makeQuery(id+"F1.opExtrude","SWEPT_BODY",BODY,{"disambiguationData":[OSD([sQuery(id+"F0.wireOp",EDGE,"E0")])]}),"instanceName":"1"}),"instanceName":"1"}),"instanceName":"1"}),"instanceName":"1"});
            var Q138;
            Q138=makeQuery(id+"F18.opPattern","COPY",BODY,{"derivedFrom":makeQuery(id+"F17.opPattern","COPY",BODY,{"derivedFrom":makeQuery(id+"F14.opPattern","COPY",BODY,{"derivedFrom":makeQuery(id+"F1.opExtrude","SWEPT_BODY",BODY,{"disambiguationData":[OSD([sQuery(id+"F0.wireOp",EDGE,"E0")])]}),"instanceName":"1"}),"instanceName":"1"}),"instanceName":"1"});
            var Q139;
            Q139=makeQuery(id+"F18.opPattern","COPY",BODY,{"derivedFrom":makeQuery(id+"F17.opPattern","COPY",BODY,{"derivedFrom":makeQuery(id+"F12.opPattern","COPY",BODY,{"derivedFrom":makeQuery(id+"F11.opPattern","COPY",BODY,{"derivedFrom":makeQuery(id+"F9.opPattern","COPY",BODY,{"derivedFrom":makeQuery(id+"F4.opPattern","COPY",BODY,{"derivedFrom":makeQuery(id+"F1.opExtrude","SWEPT_BODY",BODY,{"disambiguationData":[OSD([sQuery(id+"F0.wireOp",EDGE,"E0")])]}),"instanceName":"1"}),"instanceName":"1"}),"instanceName":"1"}),"instanceName":"1"}),"instanceName":"1"}),"instanceName":"1"});
            var Q140;
            Q140=makeQuery(id+"F18.opPattern","COPY",BODY,{"derivedFrom":makeQuery(id+"F16.opPattern","COPY",BODY,{"derivedFrom":makeQuery(id+"F12.opPattern","COPY",BODY,{"derivedFrom":makeQuery(id+"F9.opPattern","COPY",BODY,{"derivedFrom":makeQuery(id+"F1.opExtrude","SWEPT_BODY",BODY,{"disambiguationData":[OSD([sQuery(id+"F0.wireOp",EDGE,"E0")])]}),"instanceName":"1"}),"instanceName":"1"}),"instanceName":"1"}),"instanceName":"1"});
            var Q141;
            Q141=makeQuery(id+"F18.opPattern","COPY",BODY,{"derivedFrom":makeQuery(id+"F17.opPattern","COPY",BODY,{"derivedFrom":makeQuery(id+"F15.opPattern","COPY",BODY,{"derivedFrom":makeQuery(id+"F1.opExtrude","SWEPT_BODY",BODY,{"disambiguationData":[OSD([sQuery(id+"F0.wireOp",EDGE,"E0")])]}),"instanceName":"1"}),"instanceName":"1"}),"instanceName":"1"});
            var Q142;
            Q142=makeQuery(id+"F18.opPattern","COPY",BODY,{"derivedFrom":makeQuery(id+"F16.opPattern","COPY",BODY,{"derivedFrom":makeQuery(id+"F11.opPattern","COPY",BODY,{"derivedFrom":makeQuery(id+"F9.opPattern","COPY",BODY,{"derivedFrom":makeQuery(id+"F1.opExtrude","SWEPT_BODY",BODY,{"disambiguationData":[OSD([sQuery(id+"F0.wireOp",EDGE,"E0")])]}),"instanceName":"1"}),"instanceName":"1"}),"instanceName":"1"}),"instanceName":"1"});
            var Q143;
            Q143=makeQuery(id+"F18.opPattern","COPY",BODY,{"derivedFrom":makeQuery(id+"F16.opPattern","COPY",BODY,{"derivedFrom":makeQuery(id+"F11.opPattern","COPY",BODY,{"derivedFrom":makeQuery(id+"F4.opPattern","COPY",BODY,{"derivedFrom":makeQuery(id+"F1.opExtrude","SWEPT_BODY",BODY,{"disambiguationData":[OSD([sQuery(id+"F0.wireOp",EDGE,"E0")])]}),"instanceName":"1"}),"instanceName":"1"}),"instanceName":"1"}),"instanceName":"1"});
            var Q144;
            Q144=makeQuery(id+"F18.opPattern","COPY",BODY,{"derivedFrom":makeQuery(id+"F16.opPattern","COPY",BODY,{"derivedFrom":makeQuery(id+"F12.opPattern","COPY",BODY,{"derivedFrom":makeQuery(id+"F10.opPattern","COPY",BODY,{"derivedFrom":makeQuery(id+"F1.opExtrude","SWEPT_BODY",BODY,{"disambiguationData":[OSD([sQuery(id+"F0.wireOp",EDGE,"E0")])]}),"instanceName":"1"}),"instanceName":"1"}),"instanceName":"1"}),"instanceName":"1"});
            var Q145;
            Q145=makeQuery(id+"F15.opPattern","COPY",BODY,{"derivedFrom":makeQuery(id+"F11.opPattern","COPY",BODY,{"derivedFrom":makeQuery(id+"F9.opPattern","COPY",BODY,{"derivedFrom":makeQuery(id+"F4.opPattern","COPY",BODY,{"derivedFrom":makeQuery(id+"F1.opExtrude","SWEPT_BODY",BODY,{"disambiguationData":[OSD([sQuery(id+"F0.wireOp",EDGE,"E0")])]}),"instanceName":"1"}),"instanceName":"1"}),"instanceName":"1"}),"instanceName":"1"});
            var Q146;
            Q146=makeQuery(id+"F18.opPattern","COPY",BODY,{"derivedFrom":makeQuery(id+"F16.opPattern","COPY",BODY,{"derivedFrom":makeQuery(id+"F15.opPattern","COPY",BODY,{"derivedFrom":makeQuery(id+"F1.opExtrude","SWEPT_BODY",BODY,{"disambiguationData":[OSD([sQuery(id+"F0.wireOp",EDGE,"E0")])]}),"instanceName":"1"}),"instanceName":"1"}),"instanceName":"1"});
            var Q147;
            Q147=makeQuery(id+"F15.opPattern","COPY",BODY,{"derivedFrom":makeQuery(id+"F11.opPattern","COPY",BODY,{"derivedFrom":makeQuery(id+"F4.opPattern","COPY",BODY,{"derivedFrom":makeQuery(id+"F1.opExtrude","SWEPT_BODY",BODY,{"disambiguationData":[OSD([sQuery(id+"F0.wireOp",EDGE,"E0")])]}),"instanceName":"1"}),"instanceName":"1"}),"instanceName":"1"});
            var Q148;
            Q148=makeQuery(id+"F18.opPattern","COPY",BODY,{"derivedFrom":makeQuery(id+"F16.opPattern","COPY",BODY,{"derivedFrom":makeQuery(id+"F14.opPattern","COPY",BODY,{"derivedFrom":makeQuery(id+"F11.opPattern","COPY",BODY,{"derivedFrom":makeQuery(id+"F9.opPattern","COPY",BODY,{"derivedFrom":makeQuery(id+"F4.opPattern","COPY",BODY,{"derivedFrom":makeQuery(id+"F1.opExtrude","SWEPT_BODY",BODY,{"disambiguationData":[OSD([sQuery(id+"F0.wireOp",EDGE,"E0")])]}),"instanceName":"1"}),"instanceName":"1"}),"instanceName":"1"}),"instanceName":"1"}),"instanceName":"1"}),"instanceName":"1"});
            var Q149;
            Q149=makeQuery(id+"F18.opPattern","COPY",BODY,{"derivedFrom":makeQuery(id+"F16.opPattern","COPY",BODY,{"derivedFrom":makeQuery(id+"F14.opPattern","COPY",BODY,{"derivedFrom":makeQuery(id+"F11.opPattern","COPY",BODY,{"derivedFrom":makeQuery(id+"F1.opExtrude","SWEPT_BODY",BODY,{"disambiguationData":[OSD([sQuery(id+"F0.wireOp",EDGE,"E0")])]}),"instanceName":"1"}),"instanceName":"1"}),"instanceName":"1"}),"instanceName":"1"});
            var Q150;
            Q150=makeQuery(id+"F18.opPattern","COPY",BODY,{"derivedFrom":makeQuery(id+"F16.opPattern","COPY",BODY,{"derivedFrom":makeQuery(id+"F15.opPattern","COPY",BODY,{"derivedFrom":makeQuery(id+"F11.opPattern","COPY",BODY,{"derivedFrom":makeQuery(id+"F10.opPattern","COPY",BODY,{"derivedFrom":makeQuery(id+"F1.opExtrude","SWEPT_BODY",BODY,{"disambiguationData":[OSD([sQuery(id+"F0.wireOp",EDGE,"E0")])]}),"instanceName":"1"}),"instanceName":"1"}),"instanceName":"1"}),"instanceName":"1"}),"instanceName":"1"});
            var Q151;
            Q151=makeQuery(id+"F15.opPattern","COPY",BODY,{"derivedFrom":makeQuery(id+"F12.opPattern","COPY",BODY,{"derivedFrom":makeQuery(id+"F1.opExtrude","SWEPT_BODY",BODY,{"disambiguationData":[OSD([sQuery(id+"F0.wireOp",EDGE,"E0")])]}),"instanceName":"1"}),"instanceName":"1"});
            var Q152;
            Q152=makeQuery(id+"F18.opPattern","COPY",BODY,{"derivedFrom":makeQuery(id+"F16.opPattern","COPY",BODY,{"derivedFrom":makeQuery(id+"F15.opPattern","COPY",BODY,{"derivedFrom":makeQuery(id+"F9.opPattern","COPY",BODY,{"derivedFrom":makeQuery(id+"F4.opPattern","COPY",BODY,{"derivedFrom":makeQuery(id+"F1.opExtrude","SWEPT_BODY",BODY,{"disambiguationData":[OSD([sQuery(id+"F0.wireOp",EDGE,"E0")])]}),"instanceName":"1"}),"instanceName":"1"}),"instanceName":"1"}),"instanceName":"1"}),"instanceName":"1"});
            var Q153;
            Q153=makeQuery(id+"F18.opPattern","COPY",BODY,{"derivedFrom":makeQuery(id+"F16.opPattern","COPY",BODY,{"derivedFrom":makeQuery(id+"F15.opPattern","COPY",BODY,{"derivedFrom":makeQuery(id+"F14.opPattern","COPY",BODY,{"derivedFrom":makeQuery(id+"F1.opExtrude","SWEPT_BODY",BODY,{"disambiguationData":[OSD([sQuery(id+"F0.wireOp",EDGE,"E0")])]}),"instanceName":"1"}),"instanceName":"1"}),"instanceName":"1"}),"instanceName":"1"});
            var Q154;
            Q154=makeQuery(id+"F18.opPattern","COPY",BODY,{"derivedFrom":makeQuery(id+"F16.opPattern","COPY",BODY,{"derivedFrom":makeQuery(id+"F12.opPattern","COPY",BODY,{"derivedFrom":makeQuery(id+"F11.opPattern","COPY",BODY,{"derivedFrom":makeQuery(id+"F9.opPattern","COPY",BODY,{"derivedFrom":makeQuery(id+"F4.opPattern","COPY",BODY,{"derivedFrom":makeQuery(id+"F1.opExtrude","SWEPT_BODY",BODY,{"disambiguationData":[OSD([sQuery(id+"F0.wireOp",EDGE,"E0")])]}),"instanceName":"1"}),"instanceName":"1"}),"instanceName":"1"}),"instanceName":"1"}),"instanceName":"1"}),"instanceName":"1"});
            var Q155;
            Q155=makeQuery(id+"F18.opPattern","COPY",BODY,{"derivedFrom":makeQuery(id+"F12.opPattern","COPY",BODY,{"derivedFrom":makeQuery(id+"F11.opPattern","COPY",BODY,{"derivedFrom":makeQuery(id+"F1.opExtrude","SWEPT_BODY",BODY,{"disambiguationData":[OSD([sQuery(id+"F0.wireOp",EDGE,"E0")])]}),"instanceName":"1"}),"instanceName":"1"}),"instanceName":"1"});
            var Q156;
            Q156=makeQuery(id+"F18.opPattern","COPY",BODY,{"derivedFrom":makeQuery(id+"F12.opPattern","COPY",BODY,{"derivedFrom":makeQuery(id+"F4.opPattern","COPY",BODY,{"derivedFrom":makeQuery(id+"F1.opExtrude","SWEPT_BODY",BODY,{"disambiguationData":[OSD([sQuery(id+"F0.wireOp",EDGE,"E0")])]}),"instanceName":"1"}),"instanceName":"1"}),"instanceName":"1"});
            var Q157;
            Q157=makeQuery(id+"F18.opPattern","COPY",BODY,{"derivedFrom":makeQuery(id+"F16.opPattern","COPY",BODY,{"derivedFrom":makeQuery(id+"F14.opPattern","COPY",BODY,{"derivedFrom":makeQuery(id+"F1.opExtrude","SWEPT_BODY",BODY,{"disambiguationData":[OSD([sQuery(id+"F0.wireOp",EDGE,"E0")])]}),"instanceName":"1"}),"instanceName":"1"}),"instanceName":"1"});
            var Q158;
            Q158=makeQuery(id+"F18.opPattern","COPY",BODY,{"derivedFrom":makeQuery(id+"F14.opPattern","COPY",BODY,{"derivedFrom":makeQuery(id+"F10.opPattern","COPY",BODY,{"derivedFrom":makeQuery(id+"F1.opExtrude","SWEPT_BODY",BODY,{"disambiguationData":[OSD([sQuery(id+"F0.wireOp",EDGE,"E0")])]}),"instanceName":"1"}),"instanceName":"1"}),"instanceName":"1"});
            var Q159;
            Q159=makeQuery(id+"F18.opPattern","COPY",BODY,{"derivedFrom":makeQuery(id+"F14.opPattern","COPY",BODY,{"derivedFrom":makeQuery(id+"F1.opExtrude","SWEPT_BODY",BODY,{"disambiguationData":[OSD([sQuery(id+"F0.wireOp",EDGE,"E0")])]}),"instanceName":"1"}),"instanceName":"1"});
            var Q160;
            Q160=makeQuery(id+"F18.opPattern","COPY",BODY,{"derivedFrom":makeQuery(id+"F16.opPattern","COPY",BODY,{"derivedFrom":makeQuery(id+"F15.opPattern","COPY",BODY,{"derivedFrom":makeQuery(id+"F11.opPattern","COPY",BODY,{"derivedFrom":makeQuery(id+"F4.opPattern","COPY",BODY,{"derivedFrom":makeQuery(id+"F1.opExtrude","SWEPT_BODY",BODY,{"disambiguationData":[OSD([sQuery(id+"F0.wireOp",EDGE,"E0")])]}),"instanceName":"1"}),"instanceName":"1"}),"instanceName":"1"}),"instanceName":"1"}),"instanceName":"1"});
            var Q161;
            Q161=makeQuery(id+"F18.opPattern","COPY",BODY,{"derivedFrom":makeQuery(id+"F16.opPattern","COPY",BODY,{"derivedFrom":makeQuery(id+"F15.opPattern","COPY",BODY,{"derivedFrom":makeQuery(id+"F12.opPattern","COPY",BODY,{"derivedFrom":makeQuery(id+"F11.opPattern","COPY",BODY,{"derivedFrom":makeQuery(id+"F10.opPattern","COPY",BODY,{"derivedFrom":makeQuery(id+"F1.opExtrude","SWEPT_BODY",BODY,{"disambiguationData":[OSD([sQuery(id+"F0.wireOp",EDGE,"E0")])]}),"instanceName":"1"}),"instanceName":"1"}),"instanceName":"1"}),"instanceName":"1"}),"instanceName":"1"}),"instanceName":"1"});
            var Q162;
            Q162=makeQuery(id+"F18.opPattern","COPY",BODY,{"derivedFrom":makeQuery(id+"F15.opPattern","COPY",BODY,{"derivedFrom":makeQuery(id+"F12.opPattern","COPY",BODY,{"derivedFrom":makeQuery(id+"F9.opPattern","COPY",BODY,{"derivedFrom":makeQuery(id+"F1.opExtrude","SWEPT_BODY",BODY,{"disambiguationData":[OSD([sQuery(id+"F0.wireOp",EDGE,"E0")])]}),"instanceName":"1"}),"instanceName":"1"}),"instanceName":"1"}),"instanceName":"1"});
            var Q163;
            Q163=makeQuery(id+"F18.opPattern","COPY",BODY,{"derivedFrom":makeQuery(id+"F15.opPattern","COPY",BODY,{"derivedFrom":makeQuery(id+"F12.opPattern","COPY",BODY,{"derivedFrom":makeQuery(id+"F4.opPattern","COPY",BODY,{"derivedFrom":makeQuery(id+"F1.opExtrude","SWEPT_BODY",BODY,{"disambiguationData":[OSD([sQuery(id+"F0.wireOp",EDGE,"E0")])]}),"instanceName":"1"}),"instanceName":"1"}),"instanceName":"1"}),"instanceName":"1"});
            var Q164;
            Q164=makeQuery(id+"F18.opPattern","COPY",BODY,{"derivedFrom":makeQuery(id+"F17.opPattern","COPY",BODY,{"derivedFrom":makeQuery(id+"F12.opPattern","COPY",BODY,{"derivedFrom":makeQuery(id+"F9.opPattern","COPY",BODY,{"derivedFrom":makeQuery(id+"F1.opExtrude","SWEPT_BODY",BODY,{"disambiguationData":[OSD([sQuery(id+"F0.wireOp",EDGE,"E0")])]}),"instanceName":"1"}),"instanceName":"1"}),"instanceName":"1"}),"instanceName":"1"});
            var Q165;
            Q165=makeQuery(id+"F18.opPattern","COPY",BODY,{"derivedFrom":makeQuery(id+"F17.opPattern","COPY",BODY,{"derivedFrom":makeQuery(id+"F14.opPattern","COPY",BODY,{"derivedFrom":makeQuery(id+"F11.opPattern","COPY",BODY,{"derivedFrom":makeQuery(id+"F9.opPattern","COPY",BODY,{"derivedFrom":makeQuery(id+"F4.opPattern","COPY",BODY,{"derivedFrom":makeQuery(id+"F1.opExtrude","SWEPT_BODY",BODY,{"disambiguationData":[OSD([sQuery(id+"F0.wireOp",EDGE,"E0")])]}),"instanceName":"1"}),"instanceName":"1"}),"instanceName":"1"}),"instanceName":"1"}),"instanceName":"1"}),"instanceName":"1"});
            var Q166;
            Q166=makeQuery(id+"F18.opPattern","COPY",BODY,{"derivedFrom":makeQuery(id+"F16.opPattern","COPY",BODY,{"derivedFrom":makeQuery(id+"F9.opPattern","COPY",BODY,{"derivedFrom":makeQuery(id+"F4.opPattern","COPY",BODY,{"derivedFrom":makeQuery(id+"F1.opExtrude","SWEPT_BODY",BODY,{"disambiguationData":[OSD([sQuery(id+"F0.wireOp",EDGE,"E0")])]}),"instanceName":"1"}),"instanceName":"1"}),"instanceName":"1"}),"instanceName":"1"});
            var Q167;
            Q167=makeQuery(id+"F18.opPattern","COPY",BODY,{"derivedFrom":makeQuery(id+"F16.opPattern","COPY",BODY,{"derivedFrom":makeQuery(id+"F1.opExtrude","SWEPT_BODY",BODY,{"disambiguationData":[OSD([sQuery(id+"F0.wireOp",EDGE,"E0")])]}),"instanceName":"1"}),"instanceName":"1"});
            var Q168;
            Q168=makeQuery(id+"F18.opPattern","COPY",BODY,{"derivedFrom":makeQuery(id+"F15.opPattern","COPY",BODY,{"derivedFrom":makeQuery(id+"F11.opPattern","COPY",BODY,{"derivedFrom":makeQuery(id+"F10.opPattern","COPY",BODY,{"derivedFrom":makeQuery(id+"F1.opExtrude","SWEPT_BODY",BODY,{"disambiguationData":[OSD([sQuery(id+"F0.wireOp",EDGE,"E0")])]}),"instanceName":"1"}),"instanceName":"1"}),"instanceName":"1"}),"instanceName":"1"});
            var Q169;
            Q169=makeQuery(id+"F15.opPattern","COPY",BODY,{"derivedFrom":makeQuery(id+"F11.opPattern","COPY",BODY,{"derivedFrom":makeQuery(id+"F10.opPattern","COPY",BODY,{"derivedFrom":makeQuery(id+"F1.opExtrude","SWEPT_BODY",BODY,{"disambiguationData":[OSD([sQuery(id+"F0.wireOp",EDGE,"E0")])]}),"instanceName":"1"}),"instanceName":"1"}),"instanceName":"1"});
            var Q170;
            Q170=makeQuery(id+"F18.opPattern","COPY",BODY,{"derivedFrom":makeQuery(id+"F17.opPattern","COPY",BODY,{"derivedFrom":makeQuery(id+"F15.opPattern","COPY",BODY,{"derivedFrom":makeQuery(id+"F4.opPattern","COPY",BODY,{"derivedFrom":makeQuery(id+"F1.opExtrude","SWEPT_BODY",BODY,{"disambiguationData":[OSD([sQuery(id+"F0.wireOp",EDGE,"E0")])]}),"instanceName":"1"}),"instanceName":"1"}),"instanceName":"1"}),"instanceName":"1"});
            var Q171;
            Q171=makeQuery(id+"F15.opPattern","COPY",BODY,{"derivedFrom":makeQuery(id+"F14.opPattern","COPY",BODY,{"derivedFrom":makeQuery(id+"F11.opPattern","COPY",BODY,{"derivedFrom":makeQuery(id+"F9.opPattern","COPY",BODY,{"derivedFrom":makeQuery(id+"F1.opExtrude","SWEPT_BODY",BODY,{"disambiguationData":[OSD([sQuery(id+"F0.wireOp",EDGE,"E0")])]}),"instanceName":"1"}),"instanceName":"1"}),"instanceName":"1"}),"instanceName":"1"});
            var Q172;
            Q172=makeQuery(id+"F18.opPattern","COPY",BODY,{"derivedFrom":makeQuery(id+"F16.opPattern","COPY",BODY,{"derivedFrom":makeQuery(id+"F15.opPattern","COPY",BODY,{"derivedFrom":makeQuery(id+"F11.opPattern","COPY",BODY,{"derivedFrom":makeQuery(id+"F9.opPattern","COPY",BODY,{"derivedFrom":makeQuery(id+"F1.opExtrude","SWEPT_BODY",BODY,{"disambiguationData":[OSD([sQuery(id+"F0.wireOp",EDGE,"E0")])]}),"instanceName":"1"}),"instanceName":"1"}),"instanceName":"1"}),"instanceName":"1"}),"instanceName":"1"});
            var Q173;
            Q173=makeQuery(id+"F18.opPattern","COPY",BODY,{"derivedFrom":makeQuery(id+"F16.opPattern","COPY",BODY,{"derivedFrom":makeQuery(id+"F15.opPattern","COPY",BODY,{"derivedFrom":makeQuery(id+"F10.opPattern","COPY",BODY,{"derivedFrom":makeQuery(id+"F1.opExtrude","SWEPT_BODY",BODY,{"disambiguationData":[OSD([sQuery(id+"F0.wireOp",EDGE,"E0")])]}),"instanceName":"1"}),"instanceName":"1"}),"instanceName":"1"}),"instanceName":"1"});
            var Q174;
            Q174=makeQuery(id+"F15.opPattern","COPY",BODY,{"derivedFrom":makeQuery(id+"F14.opPattern","COPY",BODY,{"derivedFrom":makeQuery(id+"F11.opPattern","COPY",BODY,{"derivedFrom":makeQuery(id+"F4.opPattern","COPY",BODY,{"derivedFrom":makeQuery(id+"F1.opExtrude","SWEPT_BODY",BODY,{"disambiguationData":[OSD([sQuery(id+"F0.wireOp",EDGE,"E0")])]}),"instanceName":"1"}),"instanceName":"1"}),"instanceName":"1"}),"instanceName":"1"});
            var Q175;
            Q175=makeQuery(id+"F18.opPattern","COPY",BODY,{"derivedFrom":makeQuery(id+"F16.opPattern","COPY",BODY,{"derivedFrom":makeQuery(id+"F15.opPattern","COPY",BODY,{"derivedFrom":makeQuery(id+"F14.opPattern","COPY",BODY,{"derivedFrom":makeQuery(id+"F11.opPattern","COPY",BODY,{"derivedFrom":makeQuery(id+"F9.opPattern","COPY",BODY,{"derivedFrom":makeQuery(id+"F4.opPattern","COPY",BODY,{"derivedFrom":makeQuery(id+"F1.opExtrude","SWEPT_BODY",BODY,{"disambiguationData":[OSD([sQuery(id+"F0.wireOp",EDGE,"E0")])]}),"instanceName":"1"}),"instanceName":"1"}),"instanceName":"1"}),"instanceName":"1"}),"instanceName":"1"}),"instanceName":"1"}),"instanceName":"1"});
            var Q176;
            Q176=makeQuery(id+"F18.opPattern","COPY",BODY,{"derivedFrom":makeQuery(id+"F16.opPattern","COPY",BODY,{"derivedFrom":makeQuery(id+"F15.opPattern","COPY",BODY,{"derivedFrom":makeQuery(id+"F14.opPattern","COPY",BODY,{"derivedFrom":makeQuery(id+"F11.opPattern","COPY",BODY,{"derivedFrom":makeQuery(id+"F1.opExtrude","SWEPT_BODY",BODY,{"disambiguationData":[OSD([sQuery(id+"F0.wireOp",EDGE,"E0")])]}),"instanceName":"1"}),"instanceName":"1"}),"instanceName":"1"}),"instanceName":"1"}),"instanceName":"1"});
            var Q177;
            Q177=makeQuery(id+"F18.opPattern","COPY",BODY,{"derivedFrom":makeQuery(id+"F16.opPattern","COPY",BODY,{"derivedFrom":makeQuery(id+"F12.opPattern","COPY",BODY,{"derivedFrom":makeQuery(id+"F11.opPattern","COPY",BODY,{"derivedFrom":makeQuery(id+"F1.opExtrude","SWEPT_BODY",BODY,{"disambiguationData":[OSD([sQuery(id+"F0.wireOp",EDGE,"E0")])]}),"instanceName":"1"}),"instanceName":"1"}),"instanceName":"1"}),"instanceName":"1"});
            var Q178;
            Q178=makeQuery(id+"F18.opPattern","COPY",BODY,{"derivedFrom":makeQuery(id+"F16.opPattern","COPY",BODY,{"derivedFrom":makeQuery(id+"F14.opPattern","COPY",BODY,{"derivedFrom":makeQuery(id+"F4.opPattern","COPY",BODY,{"derivedFrom":makeQuery(id+"F1.opExtrude","SWEPT_BODY",BODY,{"disambiguationData":[OSD([sQuery(id+"F0.wireOp",EDGE,"E0")])]}),"instanceName":"1"}),"instanceName":"1"}),"instanceName":"1"}),"instanceName":"1"});
            var Q179;
            Q179=makeQuery(id+"F18.opPattern","COPY",BODY,{"derivedFrom":makeQuery(id+"F14.opPattern","COPY",BODY,{"derivedFrom":makeQuery(id+"F11.opPattern","COPY",BODY,{"derivedFrom":makeQuery(id+"F4.opPattern","COPY",BODY,{"derivedFrom":makeQuery(id+"F1.opExtrude","SWEPT_BODY",BODY,{"disambiguationData":[OSD([sQuery(id+"F0.wireOp",EDGE,"E0")])]}),"instanceName":"1"}),"instanceName":"1"}),"instanceName":"1"}),"instanceName":"1"});
            var Q180;
            Q180=makeQuery(id+"F18.opPattern","COPY",BODY,{"derivedFrom":makeQuery(id+"F16.opPattern","COPY",BODY,{"derivedFrom":makeQuery(id+"F15.opPattern","COPY",BODY,{"derivedFrom":makeQuery(id+"F14.opPattern","COPY",BODY,{"derivedFrom":makeQuery(id+"F10.opPattern","COPY",BODY,{"derivedFrom":makeQuery(id+"F1.opExtrude","SWEPT_BODY",BODY,{"disambiguationData":[OSD([sQuery(id+"F0.wireOp",EDGE,"E0")])]}),"instanceName":"1"}),"instanceName":"1"}),"instanceName":"1"}),"instanceName":"1"}),"instanceName":"1"});
            var Q181;
            Q181=makeQuery(id+"F18.opPattern","COPY",BODY,{"derivedFrom":makeQuery(id+"F17.opPattern","COPY",BODY,{"derivedFrom":makeQuery(id+"F11.opPattern","COPY",BODY,{"derivedFrom":makeQuery(id+"F1.opExtrude","SWEPT_BODY",BODY,{"disambiguationData":[OSD([sQuery(id+"F0.wireOp",EDGE,"E0")])]}),"instanceName":"1"}),"instanceName":"1"}),"instanceName":"1"});
            var Q182;
            Q182=makeQuery(id+"F18.opPattern","COPY",BODY,{"derivedFrom":makeQuery(id+"F15.opPattern","COPY",BODY,{"derivedFrom":makeQuery(id+"F12.opPattern","COPY",BODY,{"derivedFrom":makeQuery(id+"F11.opPattern","COPY",BODY,{"derivedFrom":makeQuery(id+"F1.opExtrude","SWEPT_BODY",BODY,{"disambiguationData":[OSD([sQuery(id+"F0.wireOp",EDGE,"E0")])]}),"instanceName":"1"}),"instanceName":"1"}),"instanceName":"1"}),"instanceName":"1"});
            var Q183;
            Q183=makeQuery(id+"F18.opPattern","COPY",BODY,{"derivedFrom":makeQuery(id+"F17.opPattern","COPY",BODY,{"derivedFrom":makeQuery(id+"F12.opPattern","COPY",BODY,{"derivedFrom":makeQuery(id+"F9.opPattern","COPY",BODY,{"derivedFrom":makeQuery(id+"F4.opPattern","COPY",BODY,{"derivedFrom":makeQuery(id+"F1.opExtrude","SWEPT_BODY",BODY,{"disambiguationData":[OSD([sQuery(id+"F0.wireOp",EDGE,"E0")])]}),"instanceName":"1"}),"instanceName":"1"}),"instanceName":"1"}),"instanceName":"1"}),"instanceName":"1"});
            var Q184;
            Q184=makeQuery(id+"F18.opPattern","COPY",BODY,{"derivedFrom":makeQuery(id+"F17.opPattern","COPY",BODY,{"derivedFrom":makeQuery(id+"F11.opPattern","COPY",BODY,{"derivedFrom":makeQuery(id+"F9.opPattern","COPY",BODY,{"derivedFrom":makeQuery(id+"F1.opExtrude","SWEPT_BODY",BODY,{"disambiguationData":[OSD([sQuery(id+"F0.wireOp",EDGE,"E0")])]}),"instanceName":"1"}),"instanceName":"1"}),"instanceName":"1"}),"instanceName":"1"});
            var Q185;
            Q185=makeQuery(id+"F18.opPattern","COPY",BODY,{"derivedFrom":makeQuery(id+"F15.opPattern","COPY",BODY,{"derivedFrom":makeQuery(id+"F12.opPattern","COPY",BODY,{"derivedFrom":makeQuery(id+"F11.opPattern","COPY",BODY,{"derivedFrom":makeQuery(id+"F9.opPattern","COPY",BODY,{"derivedFrom":makeQuery(id+"F4.opPattern","COPY",BODY,{"derivedFrom":makeQuery(id+"F1.opExtrude","SWEPT_BODY",BODY,{"disambiguationData":[OSD([sQuery(id+"F0.wireOp",EDGE,"E0")])]}),"instanceName":"1"}),"instanceName":"1"}),"instanceName":"1"}),"instanceName":"1"}),"instanceName":"1"}),"instanceName":"1"});
            var Q186;
            Q186=makeQuery(id+"F18.opPattern","COPY",BODY,{"derivedFrom":makeQuery(id+"F12.opPattern","COPY",BODY,{"derivedFrom":makeQuery(id+"F9.opPattern","COPY",BODY,{"derivedFrom":makeQuery(id+"F4.opPattern","COPY",BODY,{"derivedFrom":makeQuery(id+"F1.opExtrude","SWEPT_BODY",BODY,{"disambiguationData":[OSD([sQuery(id+"F0.wireOp",EDGE,"E0")])]}),"instanceName":"1"}),"instanceName":"1"}),"instanceName":"1"}),"instanceName":"1"});
            var Q187;
            Q187=makeQuery(id+"F18.opPattern","COPY",BODY,{"derivedFrom":makeQuery(id+"F11.opPattern","COPY",BODY,{"derivedFrom":makeQuery(id+"F9.opPattern","COPY",BODY,{"derivedFrom":makeQuery(id+"F1.opExtrude","SWEPT_BODY",BODY,{"disambiguationData":[OSD([sQuery(id+"F0.wireOp",EDGE,"E0")])]}),"instanceName":"1"}),"instanceName":"1"}),"instanceName":"1"});
            var Q188;
            Q188=makeQuery(id+"F18.opPattern","COPY",BODY,{"derivedFrom":makeQuery(id+"F14.opPattern","COPY",BODY,{"derivedFrom":makeQuery(id+"F11.opPattern","COPY",BODY,{"derivedFrom":makeQuery(id+"F1.opExtrude","SWEPT_BODY",BODY,{"disambiguationData":[OSD([sQuery(id+"F0.wireOp",EDGE,"E0")])]}),"instanceName":"1"}),"instanceName":"1"}),"instanceName":"1"});
            var Q189;
            Q189=makeQuery(id+"F18.opPattern","COPY",BODY,{"derivedFrom":makeQuery(id+"F15.opPattern","COPY",BODY,{"derivedFrom":makeQuery(id+"F4.opPattern","COPY",BODY,{"derivedFrom":makeQuery(id+"F1.opExtrude","SWEPT_BODY",BODY,{"disambiguationData":[OSD([sQuery(id+"F0.wireOp",EDGE,"E0")])]}),"instanceName":"1"}),"instanceName":"1"}),"instanceName":"1"});
            var Q190;
            Q190=makeQuery(id+"F18.opPattern","COPY",BODY,{"derivedFrom":makeQuery(id+"F15.opPattern","COPY",BODY,{"derivedFrom":makeQuery(id+"F12.opPattern","COPY",BODY,{"derivedFrom":makeQuery(id+"F10.opPattern","COPY",BODY,{"derivedFrom":makeQuery(id+"F1.opExtrude","SWEPT_BODY",BODY,{"disambiguationData":[OSD([sQuery(id+"F0.wireOp",EDGE,"E0")])]}),"instanceName":"1"}),"instanceName":"1"}),"instanceName":"1"}),"instanceName":"1"});
            var Q191;
            Q191=makeQuery(id+"F15.opPattern","COPY",BODY,{"derivedFrom":makeQuery(id+"F9.opPattern","COPY",BODY,{"derivedFrom":makeQuery(id+"F4.opPattern","COPY",BODY,{"derivedFrom":makeQuery(id+"F1.opExtrude","SWEPT_BODY",BODY,{"disambiguationData":[OSD([sQuery(id+"F0.wireOp",EDGE,"E0")])]}),"instanceName":"1"}),"instanceName":"1"}),"instanceName":"1"});
            var Q192;
            Q192=makeQuery(id+"F15.opPattern","COPY",BODY,{"derivedFrom":makeQuery(id+"F11.opPattern","COPY",BODY,{"derivedFrom":makeQuery(id+"F1.opExtrude","SWEPT_BODY",BODY,{"disambiguationData":[OSD([sQuery(id+"F0.wireOp",EDGE,"E0")])]}),"instanceName":"1"}),"instanceName":"1"});
            var Q193;
            Q193=makeQuery(id+"F14.opPattern","COPY",BODY,{"derivedFrom":makeQuery(id+"F11.opPattern","COPY",BODY,{"derivedFrom":makeQuery(id+"F4.opPattern","COPY",BODY,{"derivedFrom":makeQuery(id+"F1.opExtrude","SWEPT_BODY",BODY,{"disambiguationData":[OSD([sQuery(id+"F0.wireOp",EDGE,"E0")])]}),"instanceName":"1"}),"instanceName":"1"}),"instanceName":"1"});
            var Q194;
            Q194=makeQuery(id+"F16.opPattern","COPY",BODY,{"derivedFrom":makeQuery(id+"F10.opPattern","COPY",BODY,{"derivedFrom":makeQuery(id+"F1.opExtrude","SWEPT_BODY",BODY,{"disambiguationData":[OSD([sQuery(id+"F0.wireOp",EDGE,"E0")])]}),"instanceName":"1"}),"instanceName":"1"});
            var Q195;
            Q195=makeQuery(id+"F15.opPattern","COPY",BODY,{"derivedFrom":makeQuery(id+"F12.opPattern","COPY",BODY,{"derivedFrom":makeQuery(id+"F11.opPattern","COPY",BODY,{"derivedFrom":makeQuery(id+"F10.opPattern","COPY",BODY,{"derivedFrom":makeQuery(id+"F1.opExtrude","SWEPT_BODY",BODY,{"disambiguationData":[OSD([sQuery(id+"F0.wireOp",EDGE,"E0")])]}),"instanceName":"1"}),"instanceName":"1"}),"instanceName":"1"}),"instanceName":"1"});
            var Q196;
            Q196=makeQuery(id+"F16.opPattern","COPY",BODY,{"derivedFrom":makeQuery(id+"F12.opPattern","COPY",BODY,{"derivedFrom":makeQuery(id+"F11.opPattern","COPY",BODY,{"derivedFrom":makeQuery(id+"F4.opPattern","COPY",BODY,{"derivedFrom":makeQuery(id+"F1.opExtrude","SWEPT_BODY",BODY,{"disambiguationData":[OSD([sQuery(id+"F0.wireOp",EDGE,"E0")])]}),"instanceName":"1"}),"instanceName":"1"}),"instanceName":"1"}),"instanceName":"1"});
            var Q197;
            Q197=makeQuery(id+"F16.opPattern","COPY",BODY,{"derivedFrom":makeQuery(id+"F14.opPattern","COPY",BODY,{"derivedFrom":makeQuery(id+"F11.opPattern","COPY",BODY,{"derivedFrom":makeQuery(id+"F10.opPattern","COPY",BODY,{"derivedFrom":makeQuery(id+"F1.opExtrude","SWEPT_BODY",BODY,{"disambiguationData":[OSD([sQuery(id+"F0.wireOp",EDGE,"E0")])]}),"instanceName":"1"}),"instanceName":"1"}),"instanceName":"1"}),"instanceName":"1"});
            var Q198;
            Q198=makeQuery(id+"F16.opPattern","COPY",BODY,{"derivedFrom":makeQuery(id+"F14.opPattern","COPY",BODY,{"derivedFrom":makeQuery(id+"F4.opPattern","COPY",BODY,{"derivedFrom":makeQuery(id+"F1.opExtrude","SWEPT_BODY",BODY,{"disambiguationData":[OSD([sQuery(id+"F0.wireOp",EDGE,"E0")])]}),"instanceName":"1"}),"instanceName":"1"}),"instanceName":"1"});
            var Q199;
            Q199=makeQuery(id+"F16.opPattern","COPY",BODY,{"derivedFrom":makeQuery(id+"F15.opPattern","COPY",BODY,{"derivedFrom":makeQuery(id+"F12.opPattern","COPY",BODY,{"derivedFrom":makeQuery(id+"F11.opPattern","COPY",BODY,{"derivedFrom":makeQuery(id+"F9.opPattern","COPY",BODY,{"derivedFrom":makeQuery(id+"F1.opExtrude","SWEPT_BODY",BODY,{"disambiguationData":[OSD([sQuery(id+"F0.wireOp",EDGE,"E0")])]}),"instanceName":"1"}),"instanceName":"1"}),"instanceName":"1"}),"instanceName":"1"}),"instanceName":"1"});
            var Q200;
            Q200=makeQuery(id+"F16.opPattern","COPY",BODY,{"derivedFrom":makeQuery(id+"F15.opPattern","COPY",BODY,{"derivedFrom":makeQuery(id+"F12.opPattern","COPY",BODY,{"derivedFrom":makeQuery(id+"F9.opPattern","COPY",BODY,{"derivedFrom":makeQuery(id+"F4.opPattern","COPY",BODY,{"derivedFrom":makeQuery(id+"F1.opExtrude","SWEPT_BODY",BODY,{"disambiguationData":[OSD([sQuery(id+"F0.wireOp",EDGE,"E0")])]}),"instanceName":"1"}),"instanceName":"1"}),"instanceName":"1"}),"instanceName":"1"}),"instanceName":"1"});
            var Q201;
            Q201=makeQuery(id+"F16.opPattern","COPY",BODY,{"derivedFrom":makeQuery(id+"F15.opPattern","COPY",BODY,{"derivedFrom":makeQuery(id+"F12.opPattern","COPY",BODY,{"derivedFrom":makeQuery(id+"F1.opExtrude","SWEPT_BODY",BODY,{"disambiguationData":[OSD([sQuery(id+"F0.wireOp",EDGE,"E0")])]}),"instanceName":"1"}),"instanceName":"1"}),"instanceName":"1"});
            var Q202;
            Q202=makeQuery(id+"F16.opPattern","COPY",BODY,{"derivedFrom":makeQuery(id+"F15.opPattern","COPY",BODY,{"derivedFrom":makeQuery(id+"F14.opPattern","COPY",BODY,{"derivedFrom":makeQuery(id+"F10.opPattern","COPY",BODY,{"derivedFrom":makeQuery(id+"F1.opExtrude","SWEPT_BODY",BODY,{"disambiguationData":[OSD([sQuery(id+"F0.wireOp",EDGE,"E0")])]}),"instanceName":"1"}),"instanceName":"1"}),"instanceName":"1"}),"instanceName":"1"});
            var Q203;
            Q203=makeQuery(id+"F18.opPattern","COPY",BODY,{"derivedFrom":makeQuery(id+"F17.opPattern","COPY",BODY,{"derivedFrom":makeQuery(id+"F14.opPattern","COPY",BODY,{"derivedFrom":makeQuery(id+"F11.opPattern","COPY",BODY,{"derivedFrom":makeQuery(id+"F1.opExtrude","SWEPT_BODY",BODY,{"disambiguationData":[OSD([sQuery(id+"F0.wireOp",EDGE,"E0")])]}),"instanceName":"1"}),"instanceName":"1"}),"instanceName":"1"}),"instanceName":"1"});
            var Q204;
            Q204=makeQuery(id+"F16.opPattern","COPY",BODY,{"derivedFrom":makeQuery(id+"F12.opPattern","COPY",BODY,{"derivedFrom":makeQuery(id+"F9.opPattern","COPY",BODY,{"derivedFrom":makeQuery(id+"F1.opExtrude","SWEPT_BODY",BODY,{"disambiguationData":[OSD([sQuery(id+"F0.wireOp",EDGE,"E0")])]}),"instanceName":"1"}),"instanceName":"1"}),"instanceName":"1"});
            var Q205;
            Q205=makeQuery(id+"F16.opPattern","COPY",BODY,{"derivedFrom":makeQuery(id+"F14.opPattern","COPY",BODY,{"derivedFrom":makeQuery(id+"F11.opPattern","COPY",BODY,{"derivedFrom":makeQuery(id+"F9.opPattern","COPY",BODY,{"derivedFrom":makeQuery(id+"F4.opPattern","COPY",BODY,{"derivedFrom":makeQuery(id+"F1.opExtrude","SWEPT_BODY",BODY,{"disambiguationData":[OSD([sQuery(id+"F0.wireOp",EDGE,"E0")])]}),"instanceName":"1"}),"instanceName":"1"}),"instanceName":"1"}),"instanceName":"1"}),"instanceName":"1"});
            var Q206;
            Q206=makeQuery(id+"F16.opPattern","COPY",BODY,{"derivedFrom":makeQuery(id+"F14.opPattern","COPY",BODY,{"derivedFrom":makeQuery(id+"F1.opExtrude","SWEPT_BODY",BODY,{"disambiguationData":[OSD([sQuery(id+"F0.wireOp",EDGE,"E0")])]}),"instanceName":"1"}),"instanceName":"1"});
            var Q207;
            Q207=makeQuery(id+"F16.opPattern","COPY",BODY,{"derivedFrom":makeQuery(id+"F12.opPattern","COPY",BODY,{"derivedFrom":makeQuery(id+"F11.opPattern","COPY",BODY,{"derivedFrom":makeQuery(id+"F9.opPattern","COPY",BODY,{"derivedFrom":makeQuery(id+"F4.opPattern","COPY",BODY,{"derivedFrom":makeQuery(id+"F1.opExtrude","SWEPT_BODY",BODY,{"disambiguationData":[OSD([sQuery(id+"F0.wireOp",EDGE,"E0")])]}),"instanceName":"1"}),"instanceName":"1"}),"instanceName":"1"}),"instanceName":"1"}),"instanceName":"1"});
            var Q208;
            Q208=makeQuery(id+"F16.opPattern","COPY",BODY,{"derivedFrom":makeQuery(id+"F15.opPattern","COPY",BODY,{"derivedFrom":makeQuery(id+"F11.opPattern","COPY",BODY,{"derivedFrom":makeQuery(id+"F4.opPattern","COPY",BODY,{"derivedFrom":makeQuery(id+"F1.opExtrude","SWEPT_BODY",BODY,{"disambiguationData":[OSD([sQuery(id+"F0.wireOp",EDGE,"E0")])]}),"instanceName":"1"}),"instanceName":"1"}),"instanceName":"1"}),"instanceName":"1"});
            var Q209;
            Q209=makeQuery(id+"F16.opPattern","COPY",BODY,{"derivedFrom":makeQuery(id+"F15.opPattern","COPY",BODY,{"derivedFrom":makeQuery(id+"F1.opExtrude","SWEPT_BODY",BODY,{"disambiguationData":[OSD([sQuery(id+"F0.wireOp",EDGE,"E0")])]}),"instanceName":"1"}),"instanceName":"1"});
            var Q210;
            Q210=makeQuery(id+"F16.opPattern","COPY",BODY,{"derivedFrom":makeQuery(id+"F15.opPattern","COPY",BODY,{"derivedFrom":makeQuery(id+"F12.opPattern","COPY",BODY,{"derivedFrom":makeQuery(id+"F11.opPattern","COPY",BODY,{"derivedFrom":makeQuery(id+"F10.opPattern","COPY",BODY,{"derivedFrom":makeQuery(id+"F1.opExtrude","SWEPT_BODY",BODY,{"disambiguationData":[OSD([sQuery(id+"F0.wireOp",EDGE,"E0")])]}),"instanceName":"1"}),"instanceName":"1"}),"instanceName":"1"}),"instanceName":"1"}),"instanceName":"1"});
            var Q211;
            Q211=makeQuery(id+"F16.opPattern","COPY",BODY,{"derivedFrom":makeQuery(id+"F15.opPattern","COPY",BODY,{"derivedFrom":makeQuery(id+"F14.opPattern","COPY",BODY,{"derivedFrom":makeQuery(id+"F11.opPattern","COPY",BODY,{"derivedFrom":makeQuery(id+"F10.opPattern","COPY",BODY,{"derivedFrom":makeQuery(id+"F1.opExtrude","SWEPT_BODY",BODY,{"disambiguationData":[OSD([sQuery(id+"F0.wireOp",EDGE,"E0")])]}),"instanceName":"1"}),"instanceName":"1"}),"instanceName":"1"}),"instanceName":"1"}),"instanceName":"1"});
            var Q212;
            Q212=makeQuery(id+"F18.opPattern","COPY",BODY,{"derivedFrom":makeQuery(id+"F11.opPattern","COPY",BODY,{"derivedFrom":makeQuery(id+"F9.opPattern","COPY",BODY,{"derivedFrom":makeQuery(id+"F4.opPattern","COPY",BODY,{"derivedFrom":makeQuery(id+"F1.opExtrude","SWEPT_BODY",BODY,{"disambiguationData":[OSD([sQuery(id+"F0.wireOp",EDGE,"E0")])]}),"instanceName":"1"}),"instanceName":"1"}),"instanceName":"1"}),"instanceName":"1"});
            var Q213;
            Q213=makeQuery(id+"F15.opPattern","COPY",BODY,{"derivedFrom":makeQuery(id+"F12.opPattern","COPY",BODY,{"derivedFrom":makeQuery(id+"F10.opPattern","COPY",BODY,{"derivedFrom":makeQuery(id+"F1.opExtrude","SWEPT_BODY",BODY,{"disambiguationData":[OSD([sQuery(id+"F0.wireOp",EDGE,"E0")])]}),"instanceName":"1"}),"instanceName":"1"}),"instanceName":"1"});
            var Q214;
            Q214=makeQuery(id+"F18.opPattern","COPY",BODY,{"derivedFrom":makeQuery(id+"F17.opPattern","COPY",BODY,{"derivedFrom":makeQuery(id+"F11.opPattern","COPY",BODY,{"derivedFrom":makeQuery(id+"F4.opPattern","COPY",BODY,{"derivedFrom":makeQuery(id+"F1.opExtrude","SWEPT_BODY",BODY,{"disambiguationData":[OSD([sQuery(id+"F0.wireOp",EDGE,"E0")])]}),"instanceName":"1"}),"instanceName":"1"}),"instanceName":"1"}),"instanceName":"1"});
            var Q215;
            Q215=makeQuery(id+"F18.opPattern","COPY",BODY,{"derivedFrom":makeQuery(id+"F15.opPattern","COPY",BODY,{"derivedFrom":makeQuery(id+"F12.opPattern","COPY",BODY,{"derivedFrom":makeQuery(id+"F11.opPattern","COPY",BODY,{"derivedFrom":makeQuery(id+"F4.opPattern","COPY",BODY,{"derivedFrom":makeQuery(id+"F1.opExtrude","SWEPT_BODY",BODY,{"disambiguationData":[OSD([sQuery(id+"F0.wireOp",EDGE,"E0")])]}),"instanceName":"1"}),"instanceName":"1"}),"instanceName":"1"}),"instanceName":"1"}),"instanceName":"1"});
            var Q216;
            Q216=makeQuery(id+"F18.opPattern","COPY",BODY,{"derivedFrom":makeQuery(id+"F17.opPattern","COPY",BODY,{"derivedFrom":makeQuery(id+"F1.opExtrude","SWEPT_BODY",BODY,{"disambiguationData":[OSD([sQuery(id+"F0.wireOp",EDGE,"E0")])]}),"instanceName":"1"}),"instanceName":"1"});
            var Q217;
            Q217=makeQuery(id+"F18.opPattern","COPY",BODY,{"derivedFrom":makeQuery(id+"F16.opPattern","COPY",BODY,{"derivedFrom":makeQuery(id+"F9.opPattern","COPY",BODY,{"derivedFrom":makeQuery(id+"F1.opExtrude","SWEPT_BODY",BODY,{"disambiguationData":[OSD([sQuery(id+"F0.wireOp",EDGE,"E0")])]}),"instanceName":"1"}),"instanceName":"1"}),"instanceName":"1"});
            var Q218;
            Q218=makeQuery(id+"F18.opPattern","COPY",BODY,{"derivedFrom":makeQuery(id+"F16.opPattern","COPY",BODY,{"derivedFrom":makeQuery(id+"F12.opPattern","COPY",BODY,{"derivedFrom":makeQuery(id+"F11.opPattern","COPY",BODY,{"derivedFrom":makeQuery(id+"F9.opPattern","COPY",BODY,{"derivedFrom":makeQuery(id+"F1.opExtrude","SWEPT_BODY",BODY,{"disambiguationData":[OSD([sQuery(id+"F0.wireOp",EDGE,"E0")])]}),"instanceName":"1"}),"instanceName":"1"}),"instanceName":"1"}),"instanceName":"1"}),"instanceName":"1"});
            var Q219;
            Q219=makeQuery(id+"F16.opPattern","COPY",BODY,{"derivedFrom":makeQuery(id+"F12.opPattern","COPY",BODY,{"derivedFrom":makeQuery(id+"F11.opPattern","COPY",BODY,{"derivedFrom":makeQuery(id+"F1.opExtrude","SWEPT_BODY",BODY,{"disambiguationData":[OSD([sQuery(id+"F0.wireOp",EDGE,"E0")])]}),"instanceName":"1"}),"instanceName":"1"}),"instanceName":"1"});
            var Q220;
            Q220=makeQuery(id+"F16.opPattern","COPY",BODY,{"derivedFrom":makeQuery(id+"F12.opPattern","COPY",BODY,{"derivedFrom":makeQuery(id+"F4.opPattern","COPY",BODY,{"derivedFrom":makeQuery(id+"F1.opExtrude","SWEPT_BODY",BODY,{"disambiguationData":[OSD([sQuery(id+"F0.wireOp",EDGE,"E0")])]}),"instanceName":"1"}),"instanceName":"1"}),"instanceName":"1"});
            var Q221;
            Q221=makeQuery(id+"F18.opPattern","COPY",BODY,{"derivedFrom":makeQuery(id+"F15.opPattern","COPY",BODY,{"derivedFrom":makeQuery(id+"F10.opPattern","COPY",BODY,{"derivedFrom":makeQuery(id+"F1.opExtrude","SWEPT_BODY",BODY,{"disambiguationData":[OSD([sQuery(id+"F0.wireOp",EDGE,"E0")])]}),"instanceName":"1"}),"instanceName":"1"}),"instanceName":"1"});
            var Q222;
            Q222=makeQuery(id+"F18.opPattern","COPY",BODY,{"derivedFrom":makeQuery(id+"F15.opPattern","COPY",BODY,{"derivedFrom":makeQuery(id+"F14.opPattern","COPY",BODY,{"derivedFrom":makeQuery(id+"F1.opExtrude","SWEPT_BODY",BODY,{"disambiguationData":[OSD([sQuery(id+"F0.wireOp",EDGE,"E0")])]}),"instanceName":"1"}),"instanceName":"1"}),"instanceName":"1"});
            var Q223;
            Q223=makeQuery(id+"F16.opPattern","COPY",BODY,{"derivedFrom":makeQuery(id+"F14.opPattern","COPY",BODY,{"derivedFrom":makeQuery(id+"F10.opPattern","COPY",BODY,{"derivedFrom":makeQuery(id+"F1.opExtrude","SWEPT_BODY",BODY,{"disambiguationData":[OSD([sQuery(id+"F0.wireOp",EDGE,"E0")])]}),"instanceName":"1"}),"instanceName":"1"}),"instanceName":"1"});
            var Q224;
            Q224=makeQuery(id+"F18.opPattern","COPY",BODY,{"derivedFrom":makeQuery(id+"F17.opPattern","COPY",BODY,{"derivedFrom":makeQuery(id+"F11.opPattern","COPY",BODY,{"derivedFrom":makeQuery(id+"F10.opPattern","COPY",BODY,{"derivedFrom":makeQuery(id+"F1.opExtrude","SWEPT_BODY",BODY,{"disambiguationData":[OSD([sQuery(id+"F0.wireOp",EDGE,"E0")])]}),"instanceName":"1"}),"instanceName":"1"}),"instanceName":"1"}),"instanceName":"1"});
            var Q225;
            Q225=makeQuery(id+"F18.opPattern","COPY",BODY,{"derivedFrom":makeQuery(id+"F17.opPattern","COPY",BODY,{"derivedFrom":makeQuery(id+"F14.opPattern","COPY",BODY,{"derivedFrom":makeQuery(id+"F11.opPattern","COPY",BODY,{"derivedFrom":makeQuery(id+"F9.opPattern","COPY",BODY,{"derivedFrom":makeQuery(id+"F1.opExtrude","SWEPT_BODY",BODY,{"disambiguationData":[OSD([sQuery(id+"F0.wireOp",EDGE,"E0")])]}),"instanceName":"1"}),"instanceName":"1"}),"instanceName":"1"}),"instanceName":"1"}),"instanceName":"1"});
            var Q226;
            Q226=makeQuery(id+"F18.opPattern","COPY",BODY,{"derivedFrom":makeQuery(id+"F15.opPattern","COPY",BODY,{"derivedFrom":makeQuery(id+"F14.opPattern","COPY",BODY,{"derivedFrom":makeQuery(id+"F11.opPattern","COPY",BODY,{"derivedFrom":makeQuery(id+"F9.opPattern","COPY",BODY,{"derivedFrom":makeQuery(id+"F4.opPattern","COPY",BODY,{"derivedFrom":makeQuery(id+"F1.opExtrude","SWEPT_BODY",BODY,{"disambiguationData":[OSD([sQuery(id+"F0.wireOp",EDGE,"E0")])]}),"instanceName":"1"}),"instanceName":"1"}),"instanceName":"1"}),"instanceName":"1"}),"instanceName":"1"}),"instanceName":"1"});
            var Q227;
            Q227=makeQuery(id+"F16.opPattern","COPY",BODY,{"derivedFrom":makeQuery(id+"F15.opPattern","COPY",BODY,{"derivedFrom":makeQuery(id+"F12.opPattern","COPY",BODY,{"derivedFrom":makeQuery(id+"F9.opPattern","COPY",BODY,{"derivedFrom":makeQuery(id+"F1.opExtrude","SWEPT_BODY",BODY,{"disambiguationData":[OSD([sQuery(id+"F0.wireOp",EDGE,"E0")])]}),"instanceName":"1"}),"instanceName":"1"}),"instanceName":"1"}),"instanceName":"1"});
            var Q228;
            Q228=makeQuery(id+"F16.opPattern","COPY",BODY,{"derivedFrom":makeQuery(id+"F15.opPattern","COPY",BODY,{"derivedFrom":makeQuery(id+"F12.opPattern","COPY",BODY,{"derivedFrom":makeQuery(id+"F4.opPattern","COPY",BODY,{"derivedFrom":makeQuery(id+"F1.opExtrude","SWEPT_BODY",BODY,{"disambiguationData":[OSD([sQuery(id+"F0.wireOp",EDGE,"E0")])]}),"instanceName":"1"}),"instanceName":"1"}),"instanceName":"1"}),"instanceName":"1"});
            var Q229;
            Q229=makeQuery(id+"F16.opPattern","COPY",BODY,{"derivedFrom":makeQuery(id+"F15.opPattern","COPY",BODY,{"derivedFrom":makeQuery(id+"F14.opPattern","COPY",BODY,{"derivedFrom":makeQuery(id+"F4.opPattern","COPY",BODY,{"derivedFrom":makeQuery(id+"F1.opExtrude","SWEPT_BODY",BODY,{"disambiguationData":[OSD([sQuery(id+"F0.wireOp",EDGE,"E0")])]}),"instanceName":"1"}),"instanceName":"1"}),"instanceName":"1"}),"instanceName":"1"});
            var Q230;
            Q230=makeQuery(id+"F18.opPattern","COPY",BODY,{"derivedFrom":makeQuery(id+"F16.opPattern","COPY",BODY,{"derivedFrom":makeQuery(id+"F12.opPattern","COPY",BODY,{"derivedFrom":makeQuery(id+"F11.opPattern","COPY",BODY,{"derivedFrom":makeQuery(id+"F4.opPattern","COPY",BODY,{"derivedFrom":makeQuery(id+"F1.opExtrude","SWEPT_BODY",BODY,{"disambiguationData":[OSD([sQuery(id+"F0.wireOp",EDGE,"E0")])]}),"instanceName":"1"}),"instanceName":"1"}),"instanceName":"1"}),"instanceName":"1"}),"instanceName":"1"});
            var Q231;
            Q231=makeQuery(id+"F18.opPattern","COPY",BODY,{"derivedFrom":makeQuery(id+"F11.opPattern","COPY",BODY,{"derivedFrom":makeQuery(id+"F10.opPattern","COPY",BODY,{"derivedFrom":makeQuery(id+"F1.opExtrude","SWEPT_BODY",BODY,{"disambiguationData":[OSD([sQuery(id+"F0.wireOp",EDGE,"E0")])]}),"instanceName":"1"}),"instanceName":"1"}),"instanceName":"1"});
            var Q232;
            Q232=makeQuery(id+"F18.opPattern","COPY",BODY,{"derivedFrom":makeQuery(id+"F14.opPattern","COPY",BODY,{"derivedFrom":makeQuery(id+"F11.opPattern","COPY",BODY,{"derivedFrom":makeQuery(id+"F9.opPattern","COPY",BODY,{"derivedFrom":makeQuery(id+"F1.opExtrude","SWEPT_BODY",BODY,{"disambiguationData":[OSD([sQuery(id+"F0.wireOp",EDGE,"E0")])]}),"instanceName":"1"}),"instanceName":"1"}),"instanceName":"1"}),"instanceName":"1"});
            var Q233;
            Q233=makeQuery(id+"F16.opPattern","COPY",BODY,{"derivedFrom":makeQuery(id+"F15.opPattern","COPY",BODY,{"derivedFrom":makeQuery(id+"F11.opPattern","COPY",BODY,{"derivedFrom":makeQuery(id+"F10.opPattern","COPY",BODY,{"derivedFrom":makeQuery(id+"F1.opExtrude","SWEPT_BODY",BODY,{"disambiguationData":[OSD([sQuery(id+"F0.wireOp",EDGE,"E0")])]}),"instanceName":"1"}),"instanceName":"1"}),"instanceName":"1"}),"instanceName":"1"});
            var Q234;
            Q234=makeQuery(id+"F16.opPattern","COPY",BODY,{"derivedFrom":makeQuery(id+"F15.opPattern","COPY",BODY,{"derivedFrom":makeQuery(id+"F4.opPattern","COPY",BODY,{"derivedFrom":makeQuery(id+"F1.opExtrude","SWEPT_BODY",BODY,{"disambiguationData":[OSD([sQuery(id+"F0.wireOp",EDGE,"E0")])]}),"instanceName":"1"}),"instanceName":"1"}),"instanceName":"1"});
            var Q235;
            Q235=makeQuery(id+"F18.opPattern","COPY",BODY,{"derivedFrom":makeQuery(id+"F17.opPattern","COPY",BODY,{"derivedFrom":makeQuery(id+"F15.opPattern","COPY",BODY,{"derivedFrom":makeQuery(id+"F10.opPattern","COPY",BODY,{"derivedFrom":makeQuery(id+"F1.opExtrude","SWEPT_BODY",BODY,{"disambiguationData":[OSD([sQuery(id+"F0.wireOp",EDGE,"E0")])]}),"instanceName":"1"}),"instanceName":"1"}),"instanceName":"1"}),"instanceName":"1"});
            var Q236;
            Q236=makeQuery(id+"F18.opPattern","COPY",BODY,{"derivedFrom":makeQuery(id+"F16.opPattern","COPY",BODY,{"derivedFrom":makeQuery(id+"F15.opPattern","COPY",BODY,{"derivedFrom":makeQuery(id+"F11.opPattern","COPY",BODY,{"derivedFrom":makeQuery(id+"F1.opExtrude","SWEPT_BODY",BODY,{"disambiguationData":[OSD([sQuery(id+"F0.wireOp",EDGE,"E0")])]}),"instanceName":"1"}),"instanceName":"1"}),"instanceName":"1"}),"instanceName":"1"});
            var Q237;
            Q237=makeQuery(id+"F16.opPattern","COPY",BODY,{"derivedFrom":makeQuery(id+"F11.opPattern","COPY",BODY,{"derivedFrom":makeQuery(id+"F1.opExtrude","SWEPT_BODY",BODY,{"disambiguationData":[OSD([sQuery(id+"F0.wireOp",EDGE,"E0")])]}),"instanceName":"1"}),"instanceName":"1"});
            var Q238;
            Q238=makeQuery(id+"F16.opPattern","COPY",BODY,{"derivedFrom":makeQuery(id+"F12.opPattern","COPY",BODY,{"derivedFrom":makeQuery(id+"F9.opPattern","COPY",BODY,{"derivedFrom":makeQuery(id+"F4.opPattern","COPY",BODY,{"derivedFrom":makeQuery(id+"F1.opExtrude","SWEPT_BODY",BODY,{"disambiguationData":[OSD([sQuery(id+"F0.wireOp",EDGE,"E0")])]}),"instanceName":"1"}),"instanceName":"1"}),"instanceName":"1"}),"instanceName":"1"});
            var Q239;
            Q239=makeQuery(id+"F18.opPattern","COPY",BODY,{"derivedFrom":makeQuery(id+"F17.opPattern","COPY",BODY,{"derivedFrom":makeQuery(id+"F12.opPattern","COPY",BODY,{"derivedFrom":makeQuery(id+"F1.opExtrude","SWEPT_BODY",BODY,{"disambiguationData":[OSD([sQuery(id+"F0.wireOp",EDGE,"E0")])]}),"instanceName":"1"}),"instanceName":"1"}),"instanceName":"1"});
            var Q240;
            Q240=makeQuery(id+"F18.opPattern","COPY",BODY,{"derivedFrom":makeQuery(id+"F17.opPattern","COPY",BODY,{"derivedFrom":makeQuery(id+"F11.opPattern","COPY",BODY,{"derivedFrom":makeQuery(id+"F9.opPattern","COPY",BODY,{"derivedFrom":makeQuery(id+"F4.opPattern","COPY",BODY,{"derivedFrom":makeQuery(id+"F1.opExtrude","SWEPT_BODY",BODY,{"disambiguationData":[OSD([sQuery(id+"F0.wireOp",EDGE,"E0")])]}),"instanceName":"1"}),"instanceName":"1"}),"instanceName":"1"}),"instanceName":"1"}),"instanceName":"1"});
            var Q241;
            Q241=makeQuery(id+"F18.opPattern","COPY",BODY,{"derivedFrom":makeQuery(id+"F16.opPattern","COPY",BODY,{"derivedFrom":makeQuery(id+"F12.opPattern","COPY",BODY,{"derivedFrom":makeQuery(id+"F4.opPattern","COPY",BODY,{"derivedFrom":makeQuery(id+"F1.opExtrude","SWEPT_BODY",BODY,{"disambiguationData":[OSD([sQuery(id+"F0.wireOp",EDGE,"E0")])]}),"instanceName":"1"}),"instanceName":"1"}),"instanceName":"1"}),"instanceName":"1"});
            var Q242;
            Q242=makeQuery(id+"F16.opPattern","COPY",BODY,{"derivedFrom":makeQuery(id+"F15.opPattern","COPY",BODY,{"derivedFrom":makeQuery(id+"F12.opPattern","COPY",BODY,{"derivedFrom":makeQuery(id+"F11.opPattern","COPY",BODY,{"derivedFrom":makeQuery(id+"F1.opExtrude","SWEPT_BODY",BODY,{"disambiguationData":[OSD([sQuery(id+"F0.wireOp",EDGE,"E0")])]}),"instanceName":"1"}),"instanceName":"1"}),"instanceName":"1"}),"instanceName":"1"});
            var Q243;
            Q243=makeQuery(id+"F16.opPattern","COPY",BODY,{"derivedFrom":makeQuery(id+"F15.opPattern","COPY",BODY,{"derivedFrom":makeQuery(id+"F12.opPattern","COPY",BODY,{"derivedFrom":makeQuery(id+"F11.opPattern","COPY",BODY,{"derivedFrom":makeQuery(id+"F9.opPattern","COPY",BODY,{"derivedFrom":makeQuery(id+"F4.opPattern","COPY",BODY,{"derivedFrom":makeQuery(id+"F1.opExtrude","SWEPT_BODY",BODY,{"disambiguationData":[OSD([sQuery(id+"F0.wireOp",EDGE,"E0")])]}),"instanceName":"1"}),"instanceName":"1"}),"instanceName":"1"}),"instanceName":"1"}),"instanceName":"1"}),"instanceName":"1"});
            var Q244;
            Q244=makeQuery(id+"F18.opPattern","COPY",BODY,{"derivedFrom":makeQuery(id+"F9.opPattern","COPY",BODY,{"derivedFrom":makeQuery(id+"F4.opPattern","COPY",BODY,{"derivedFrom":makeQuery(id+"F1.opExtrude","SWEPT_BODY",BODY,{"disambiguationData":[OSD([sQuery(id+"F0.wireOp",EDGE,"E0")])]}),"instanceName":"1"}),"instanceName":"1"}),"instanceName":"1"});
            var Q245;
            Q245=makeQuery(id+"F16.opPattern","COPY",BODY,{"derivedFrom":makeQuery(id+"F15.opPattern","COPY",BODY,{"derivedFrom":makeQuery(id+"F12.opPattern","COPY",BODY,{"derivedFrom":makeQuery(id+"F10.opPattern","COPY",BODY,{"derivedFrom":makeQuery(id+"F1.opExtrude","SWEPT_BODY",BODY,{"disambiguationData":[OSD([sQuery(id+"F0.wireOp",EDGE,"E0")])]}),"instanceName":"1"}),"instanceName":"1"}),"instanceName":"1"}),"instanceName":"1"});
            var Q246;
            Q246=makeQuery(id+"F18.opPattern","COPY",BODY,{"derivedFrom":makeQuery(id+"F15.opPattern","COPY",BODY,{"derivedFrom":makeQuery(id+"F11.opPattern","COPY",BODY,{"derivedFrom":makeQuery(id+"F9.opPattern","COPY",BODY,{"derivedFrom":makeQuery(id+"F1.opExtrude","SWEPT_BODY",BODY,{"disambiguationData":[OSD([sQuery(id+"F0.wireOp",EDGE,"E0")])]}),"instanceName":"1"}),"instanceName":"1"}),"instanceName":"1"}),"instanceName":"1"});
            var Q247;
            Q247=makeQuery(id+"F18.opPattern","COPY",BODY,{"derivedFrom":makeQuery(id+"F16.opPattern","COPY",BODY,{"derivedFrom":makeQuery(id+"F15.opPattern","COPY",BODY,{"derivedFrom":makeQuery(id+"F12.opPattern","COPY",BODY,{"derivedFrom":makeQuery(id+"F9.opPattern","COPY",BODY,{"derivedFrom":makeQuery(id+"F1.opExtrude","SWEPT_BODY",BODY,{"disambiguationData":[OSD([sQuery(id+"F0.wireOp",EDGE,"E0")])]}),"instanceName":"1"}),"instanceName":"1"}),"instanceName":"1"}),"instanceName":"1"}),"instanceName":"1"});
            var Q248;
            Q248=makeQuery(id+"F18.opPattern","COPY",BODY,{"derivedFrom":makeQuery(id+"F17.opPattern","COPY",BODY,{"derivedFrom":makeQuery(id+"F9.opPattern","COPY",BODY,{"derivedFrom":makeQuery(id+"F4.opPattern","COPY",BODY,{"derivedFrom":makeQuery(id+"F1.opExtrude","SWEPT_BODY",BODY,{"disambiguationData":[OSD([sQuery(id+"F0.wireOp",EDGE,"E0")])]}),"instanceName":"1"}),"instanceName":"1"}),"instanceName":"1"}),"instanceName":"1"});
            var Q249;
            Q249=makeQuery(id+"F16.opPattern","COPY",BODY,{"derivedFrom":makeQuery(id+"F11.opPattern","COPY",BODY,{"derivedFrom":makeQuery(id+"F9.opPattern","COPY",BODY,{"derivedFrom":makeQuery(id+"F1.opExtrude","SWEPT_BODY",BODY,{"disambiguationData":[OSD([sQuery(id+"F0.wireOp",EDGE,"E0")])]}),"instanceName":"1"}),"instanceName":"1"}),"instanceName":"1"});
            var Q250;
            Q250=makeQuery(id+"F16.opPattern","COPY",BODY,{"derivedFrom":makeQuery(id+"F14.opPattern","COPY",BODY,{"derivedFrom":makeQuery(id+"F11.opPattern","COPY",BODY,{"derivedFrom":makeQuery(id+"F1.opExtrude","SWEPT_BODY",BODY,{"disambiguationData":[OSD([sQuery(id+"F0.wireOp",EDGE,"E0")])]}),"instanceName":"1"}),"instanceName":"1"}),"instanceName":"1"});
            var Q251;
            Q251=makeQuery(id+"F18.opPattern","COPY",BODY,{"derivedFrom":makeQuery(id+"F15.opPattern","COPY",BODY,{"derivedFrom":makeQuery(id+"F14.opPattern","COPY",BODY,{"derivedFrom":makeQuery(id+"F11.opPattern","COPY",BODY,{"derivedFrom":makeQuery(id+"F1.opExtrude","SWEPT_BODY",BODY,{"disambiguationData":[OSD([sQuery(id+"F0.wireOp",EDGE,"E0")])]}),"instanceName":"1"}),"instanceName":"1"}),"instanceName":"1"}),"instanceName":"1"});
            var Q252;
            Q252=makeQuery(id+"F18.opPattern","COPY",BODY,{"derivedFrom":makeQuery(id+"F16.opPattern","COPY",BODY,{"derivedFrom":makeQuery(id+"F14.opPattern","COPY",BODY,{"derivedFrom":makeQuery(id+"F11.opPattern","COPY",BODY,{"derivedFrom":makeQuery(id+"F10.opPattern","COPY",BODY,{"derivedFrom":makeQuery(id+"F1.opExtrude","SWEPT_BODY",BODY,{"disambiguationData":[OSD([sQuery(id+"F0.wireOp",EDGE,"E0")])]}),"instanceName":"1"}),"instanceName":"1"}),"instanceName":"1"}),"instanceName":"1"}),"instanceName":"1"});
            var Q253;
            Q253=makeQuery(id+"F18.opPattern","COPY",BODY,{"derivedFrom":makeQuery(id+"F16.opPattern","COPY",BODY,{"derivedFrom":makeQuery(id+"F15.opPattern","COPY",BODY,{"derivedFrom":makeQuery(id+"F12.opPattern","COPY",BODY,{"derivedFrom":makeQuery(id+"F11.opPattern","COPY",BODY,{"derivedFrom":makeQuery(id+"F9.opPattern","COPY",BODY,{"derivedFrom":makeQuery(id+"F1.opExtrude","SWEPT_BODY",BODY,{"disambiguationData":[OSD([sQuery(id+"F0.wireOp",EDGE,"E0")])]}),"instanceName":"1"}),"instanceName":"1"}),"instanceName":"1"}),"instanceName":"1"}),"instanceName":"1"}),"instanceName":"1"});
            var Q254;
            Q254=makeQuery(id+"F18.opPattern","COPY",BODY,{"derivedFrom":makeQuery(id+"F11.opPattern","COPY",BODY,{"derivedFrom":makeQuery(id+"F1.opExtrude","SWEPT_BODY",BODY,{"disambiguationData":[OSD([sQuery(id+"F0.wireOp",EDGE,"E0")])]}),"instanceName":"1"}),"instanceName":"1"});
            var Q255;
            Q255=makeQuery(id+"F18.opPattern","COPY",BODY,{"derivedFrom":makeQuery(id+"F17.opPattern","COPY",BODY,{"derivedFrom":makeQuery(id+"F15.opPattern","COPY",BODY,{"derivedFrom":makeQuery(id+"F9.opPattern","COPY",BODY,{"derivedFrom":makeQuery(id+"F1.opExtrude","SWEPT_BODY",BODY,{"disambiguationData":[OSD([sQuery(id+"F0.wireOp",EDGE,"E0")])]}),"instanceName":"1"}),"instanceName":"1"}),"instanceName":"1"}),"instanceName":"1"});
            var Q256;
            Q256=makeQuery(id+"F18.opPattern","COPY",BODY,{"derivedFrom":makeQuery(id+"F17.opPattern","COPY",BODY,{"derivedFrom":makeQuery(id+"F12.opPattern","COPY",BODY,{"derivedFrom":makeQuery(id+"F10.opPattern","COPY",BODY,{"derivedFrom":makeQuery(id+"F1.opExtrude","SWEPT_BODY",BODY,{"disambiguationData":[OSD([sQuery(id+"F0.wireOp",EDGE,"E0")])]}),"instanceName":"1"}),"instanceName":"1"}),"instanceName":"1"}),"instanceName":"1"});
            var Q257;
            Q257=makeQuery(id+"F18.opPattern","COPY",BODY,{"derivedFrom":makeQuery(id+"F15.opPattern","COPY",BODY,{"derivedFrom":makeQuery(id+"F14.opPattern","COPY",BODY,{"derivedFrom":makeQuery(id+"F11.opPattern","COPY",BODY,{"derivedFrom":makeQuery(id+"F9.opPattern","COPY",BODY,{"derivedFrom":makeQuery(id+"F1.opExtrude","SWEPT_BODY",BODY,{"disambiguationData":[OSD([sQuery(id+"F0.wireOp",EDGE,"E0")])]}),"instanceName":"1"}),"instanceName":"1"}),"instanceName":"1"}),"instanceName":"1"}),"instanceName":"1"});
            var Q258;
            Q258=makeQuery(id+"F18.opPattern","COPY",BODY,{"derivedFrom":makeQuery(id+"F16.opPattern","COPY",BODY,{"derivedFrom":makeQuery(id+"F14.opPattern","COPY",BODY,{"derivedFrom":makeQuery(id+"F10.opPattern","COPY",BODY,{"derivedFrom":makeQuery(id+"F1.opExtrude","SWEPT_BODY",BODY,{"disambiguationData":[OSD([sQuery(id+"F0.wireOp",EDGE,"E0")])]}),"instanceName":"1"}),"instanceName":"1"}),"instanceName":"1"}),"instanceName":"1"});
            var Q259;
            Q259=makeQuery(id+"F18.opPattern","COPY",BODY,{"derivedFrom":makeQuery(id+"F16.opPattern","COPY",BODY,{"derivedFrom":makeQuery(id+"F15.opPattern","COPY",BODY,{"derivedFrom":makeQuery(id+"F12.opPattern","COPY",BODY,{"derivedFrom":makeQuery(id+"F1.opExtrude","SWEPT_BODY",BODY,{"disambiguationData":[OSD([sQuery(id+"F0.wireOp",EDGE,"E0")])]}),"instanceName":"1"}),"instanceName":"1"}),"instanceName":"1"}),"instanceName":"1"});
            var Q260;
            Q260=makeQuery(id+"F18.opPattern","COPY",BODY,{"derivedFrom":makeQuery(id+"F16.opPattern","COPY",BODY,{"derivedFrom":makeQuery(id+"F15.opPattern","COPY",BODY,{"derivedFrom":makeQuery(id+"F12.opPattern","COPY",BODY,{"derivedFrom":makeQuery(id+"F9.opPattern","COPY",BODY,{"derivedFrom":makeQuery(id+"F4.opPattern","COPY",BODY,{"derivedFrom":makeQuery(id+"F1.opExtrude","SWEPT_BODY",BODY,{"disambiguationData":[OSD([sQuery(id+"F0.wireOp",EDGE,"E0")])]}),"instanceName":"1"}),"instanceName":"1"}),"instanceName":"1"}),"instanceName":"1"}),"instanceName":"1"}),"instanceName":"1"});
            var Q261;
            Q261=makeQuery(id+"F18.opPattern","COPY",BODY,{"derivedFrom":makeQuery(id+"F17.opPattern","COPY",BODY,{"derivedFrom":makeQuery(id+"F4.opPattern","COPY",BODY,{"derivedFrom":makeQuery(id+"F1.opExtrude","SWEPT_BODY",BODY,{"disambiguationData":[OSD([sQuery(id+"F0.wireOp",EDGE,"E0")])]}),"instanceName":"1"}),"instanceName":"1"}),"instanceName":"1"});
            var Q262;
            Q262=makeQuery(id+"F18.opPattern","COPY",BODY,{"derivedFrom":makeQuery(id+"F12.opPattern","COPY",BODY,{"derivedFrom":makeQuery(id+"F10.opPattern","COPY",BODY,{"derivedFrom":makeQuery(id+"F1.opExtrude","SWEPT_BODY",BODY,{"disambiguationData":[OSD([sQuery(id+"F0.wireOp",EDGE,"E0")])]}),"instanceName":"1"}),"instanceName":"1"}),"instanceName":"1"});
            var Q263;
            Q263=makeQuery(id+"F18.opPattern","COPY",BODY,{"derivedFrom":makeQuery(id+"F15.opPattern","COPY",BODY,{"derivedFrom":makeQuery(id+"F9.opPattern","COPY",BODY,{"derivedFrom":makeQuery(id+"F1.opExtrude","SWEPT_BODY",BODY,{"disambiguationData":[OSD([sQuery(id+"F0.wireOp",EDGE,"E0")])]}),"instanceName":"1"}),"instanceName":"1"}),"instanceName":"1"});
            var Q264;
            Q264=makeQuery(id+"F18.opPattern","COPY",BODY,{"derivedFrom":makeQuery(id+"F15.opPattern","COPY",BODY,{"derivedFrom":makeQuery(id+"F14.opPattern","COPY",BODY,{"derivedFrom":makeQuery(id+"F4.opPattern","COPY",BODY,{"derivedFrom":makeQuery(id+"F1.opExtrude","SWEPT_BODY",BODY,{"disambiguationData":[OSD([sQuery(id+"F0.wireOp",EDGE,"E0")])]}),"instanceName":"1"}),"instanceName":"1"}),"instanceName":"1"}),"instanceName":"1"});
            var Q265;
            Q265=makeQuery(id+"F18.opPattern","COPY",BODY,{"derivedFrom":makeQuery(id+"F11.opPattern","COPY",BODY,{"derivedFrom":makeQuery(id+"F4.opPattern","COPY",BODY,{"derivedFrom":makeQuery(id+"F1.opExtrude","SWEPT_BODY",BODY,{"disambiguationData":[OSD([sQuery(id+"F0.wireOp",EDGE,"E0")])]}),"instanceName":"1"}),"instanceName":"1"}),"instanceName":"1"});
            var Q266;
            Q266=makeQuery(id+"F16.opPattern","COPY",BODY,{"derivedFrom":makeQuery(id+"F11.opPattern","COPY",BODY,{"derivedFrom":makeQuery(id+"F4.opPattern","COPY",BODY,{"derivedFrom":makeQuery(id+"F1.opExtrude","SWEPT_BODY",BODY,{"disambiguationData":[OSD([sQuery(id+"F0.wireOp",EDGE,"E0")])]}),"instanceName":"1"}),"instanceName":"1"}),"instanceName":"1"});
            var Q267;
            Q267=makeQuery(id+"F18.opPattern","COPY",BODY,{"derivedFrom":makeQuery(id+"F15.opPattern","COPY",BODY,{"derivedFrom":makeQuery(id+"F11.opPattern","COPY",BODY,{"derivedFrom":makeQuery(id+"F9.opPattern","COPY",BODY,{"derivedFrom":makeQuery(id+"F4.opPattern","COPY",BODY,{"derivedFrom":makeQuery(id+"F1.opExtrude","SWEPT_BODY",BODY,{"disambiguationData":[OSD([sQuery(id+"F0.wireOp",EDGE,"E0")])]}),"instanceName":"1"}),"instanceName":"1"}),"instanceName":"1"}),"instanceName":"1"}),"instanceName":"1"});
            var Q268;
            Q268=makeQuery(id+"F18.opPattern","COPY",BODY,{"derivedFrom":makeQuery(id+"F17.opPattern","COPY",BODY,{"derivedFrom":makeQuery(id+"F14.opPattern","COPY",BODY,{"derivedFrom":makeQuery(id+"F11.opPattern","COPY",BODY,{"derivedFrom":makeQuery(id+"F4.opPattern","COPY",BODY,{"derivedFrom":makeQuery(id+"F1.opExtrude","SWEPT_BODY",BODY,{"disambiguationData":[OSD([sQuery(id+"F0.wireOp",EDGE,"E0")])]}),"instanceName":"1"}),"instanceName":"1"}),"instanceName":"1"}),"instanceName":"1"}),"instanceName":"1"});
            var Q269;
            Q269=makeQuery(id+"F18.opPattern","COPY",BODY,{"derivedFrom":makeQuery(id+"F16.opPattern","COPY",BODY,{"derivedFrom":makeQuery(id+"F15.opPattern","COPY",BODY,{"derivedFrom":makeQuery(id+"F12.opPattern","COPY",BODY,{"derivedFrom":makeQuery(id+"F11.opPattern","COPY",BODY,{"derivedFrom":makeQuery(id+"F9.opPattern","COPY",BODY,{"derivedFrom":makeQuery(id+"F4.opPattern","COPY",BODY,{"derivedFrom":makeQuery(id+"F1.opExtrude","SWEPT_BODY",BODY,{"disambiguationData":[OSD([sQuery(id+"F0.wireOp",EDGE,"E0")])]}),"instanceName":"1"}),"instanceName":"1"}),"instanceName":"1"}),"instanceName":"1"}),"instanceName":"1"}),"instanceName":"1"}),"instanceName":"1"});
            var Q270;
            Q270=makeQuery(id+"F16.opPattern","COPY",BODY,{"derivedFrom":makeQuery(id+"F11.opPattern","COPY",BODY,{"derivedFrom":makeQuery(id+"F10.opPattern","COPY",BODY,{"derivedFrom":makeQuery(id+"F1.opExtrude","SWEPT_BODY",BODY,{"disambiguationData":[OSD([sQuery(id+"F0.wireOp",EDGE,"E0")])]}),"instanceName":"1"}),"instanceName":"1"}),"instanceName":"1"});
            var Q271;
            Q271=makeQuery(id+"F18.opPattern","COPY",BODY,{"derivedFrom":makeQuery(id+"F16.opPattern","COPY",BODY,{"derivedFrom":makeQuery(id+"F15.opPattern","COPY",BODY,{"derivedFrom":makeQuery(id+"F12.opPattern","COPY",BODY,{"derivedFrom":makeQuery(id+"F11.opPattern","COPY",BODY,{"derivedFrom":makeQuery(id+"F4.opPattern","COPY",BODY,{"derivedFrom":makeQuery(id+"F1.opExtrude","SWEPT_BODY",BODY,{"disambiguationData":[OSD([sQuery(id+"F0.wireOp",EDGE,"E0")])]}),"instanceName":"1"}),"instanceName":"1"}),"instanceName":"1"}),"instanceName":"1"}),"instanceName":"1"}),"instanceName":"1"});
            var Q272;
            Q272=makeQuery(id+"F16.opPattern","COPY",BODY,{"derivedFrom":makeQuery(id+"F14.opPattern","COPY",BODY,{"derivedFrom":makeQuery(id+"F11.opPattern","COPY",BODY,{"derivedFrom":makeQuery(id+"F9.opPattern","COPY",BODY,{"derivedFrom":makeQuery(id+"F1.opExtrude","SWEPT_BODY",BODY,{"disambiguationData":[OSD([sQuery(id+"F0.wireOp",EDGE,"E0")])]}),"instanceName":"1"}),"instanceName":"1"}),"instanceName":"1"}),"instanceName":"1"});
            var Q273;
            Q273=makeQuery(id+"F16.opPattern","COPY",BODY,{"derivedFrom":makeQuery(id+"F15.opPattern","COPY",BODY,{"derivedFrom":makeQuery(id+"F12.opPattern","COPY",BODY,{"derivedFrom":makeQuery(id+"F11.opPattern","COPY",BODY,{"derivedFrom":makeQuery(id+"F4.opPattern","COPY",BODY,{"derivedFrom":makeQuery(id+"F1.opExtrude","SWEPT_BODY",BODY,{"disambiguationData":[OSD([sQuery(id+"F0.wireOp",EDGE,"E0")])]}),"instanceName":"1"}),"instanceName":"1"}),"instanceName":"1"}),"instanceName":"1"}),"instanceName":"1"});
            var Q274;
            Q274=makeQuery(id+"F18.opPattern","COPY",BODY,{"derivedFrom":makeQuery(id+"F17.opPattern","COPY",BODY,{"derivedFrom":makeQuery(id+"F15.opPattern","COPY",BODY,{"derivedFrom":makeQuery(id+"F9.opPattern","COPY",BODY,{"derivedFrom":makeQuery(id+"F4.opPattern","COPY",BODY,{"derivedFrom":makeQuery(id+"F1.opExtrude","SWEPT_BODY",BODY,{"disambiguationData":[OSD([sQuery(id+"F0.wireOp",EDGE,"E0")])]}),"instanceName":"1"}),"instanceName":"1"}),"instanceName":"1"}),"instanceName":"1"}),"instanceName":"1"});
            var Q275;
            Q275=makeQuery(id+"F18.opPattern","COPY",BODY,{"derivedFrom":makeQuery(id+"F12.opPattern","COPY",BODY,{"derivedFrom":makeQuery(id+"F11.opPattern","COPY",BODY,{"derivedFrom":makeQuery(id+"F10.opPattern","COPY",BODY,{"derivedFrom":makeQuery(id+"F1.opExtrude","SWEPT_BODY",BODY,{"disambiguationData":[OSD([sQuery(id+"F0.wireOp",EDGE,"E0")])]}),"instanceName":"1"}),"instanceName":"1"}),"instanceName":"1"}),"instanceName":"1"});
            var Q276;
            Q276=makeQuery(id+"F16.opPattern","COPY",BODY,{"derivedFrom":makeQuery(id+"F12.opPattern","COPY",BODY,{"derivedFrom":makeQuery(id+"F1.opExtrude","SWEPT_BODY",BODY,{"disambiguationData":[OSD([sQuery(id+"F0.wireOp",EDGE,"E0")])]}),"instanceName":"1"}),"instanceName":"1"});
            var Q277;
            Q277=makeQuery(id+"F16.opPattern","COPY",BODY,{"derivedFrom":makeQuery(id+"F11.opPattern","COPY",BODY,{"derivedFrom":makeQuery(id+"F9.opPattern","COPY",BODY,{"derivedFrom":makeQuery(id+"F4.opPattern","COPY",BODY,{"derivedFrom":makeQuery(id+"F1.opExtrude","SWEPT_BODY",BODY,{"disambiguationData":[OSD([sQuery(id+"F0.wireOp",EDGE,"E0")])]}),"instanceName":"1"}),"instanceName":"1"}),"instanceName":"1"}),"instanceName":"1"});
            var Q278;
            Q278=makeQuery(id+"F18.opPattern","COPY",BODY,{"derivedFrom":makeQuery(id+"F16.opPattern","COPY",BODY,{"derivedFrom":makeQuery(id+"F10.opPattern","COPY",BODY,{"derivedFrom":makeQuery(id+"F1.opExtrude","SWEPT_BODY",BODY,{"disambiguationData":[OSD([sQuery(id+"F0.wireOp",EDGE,"E0")])]}),"instanceName":"1"}),"instanceName":"1"}),"instanceName":"1"});
            var Q279;
            Q279=makeQuery(id+"F18.opPattern","COPY",BODY,{"derivedFrom":makeQuery(id+"F16.opPattern","COPY",BODY,{"derivedFrom":makeQuery(id+"F15.opPattern","COPY",BODY,{"derivedFrom":makeQuery(id+"F12.opPattern","COPY",BODY,{"derivedFrom":makeQuery(id+"F4.opPattern","COPY",BODY,{"derivedFrom":makeQuery(id+"F1.opExtrude","SWEPT_BODY",BODY,{"disambiguationData":[OSD([sQuery(id+"F0.wireOp",EDGE,"E0")])]}),"instanceName":"1"}),"instanceName":"1"}),"instanceName":"1"}),"instanceName":"1"}),"instanceName":"1"});
            var Q280;
            Q280=makeQuery(id+"F16.opPattern","COPY",BODY,{"derivedFrom":makeQuery(id+"F9.opPattern","COPY",BODY,{"derivedFrom":makeQuery(id+"F4.opPattern","COPY",BODY,{"derivedFrom":makeQuery(id+"F1.opExtrude","SWEPT_BODY",BODY,{"disambiguationData":[OSD([sQuery(id+"F0.wireOp",EDGE,"E0")])]}),"instanceName":"1"}),"instanceName":"1"}),"instanceName":"1"});
            var Q281;
            Q281=makeQuery(id+"F18.opPattern","COPY",BODY,{"derivedFrom":makeQuery(id+"F15.opPattern","COPY",BODY,{"derivedFrom":makeQuery(id+"F9.opPattern","COPY",BODY,{"derivedFrom":makeQuery(id+"F4.opPattern","COPY",BODY,{"derivedFrom":makeQuery(id+"F1.opExtrude","SWEPT_BODY",BODY,{"disambiguationData":[OSD([sQuery(id+"F0.wireOp",EDGE,"E0")])]}),"instanceName":"1"}),"instanceName":"1"}),"instanceName":"1"}),"instanceName":"1"});
            var Q282;
            Q282=makeQuery(id+"F16.opPattern","COPY",BODY,{"derivedFrom":makeQuery(id+"F15.opPattern","COPY",BODY,{"derivedFrom":makeQuery(id+"F10.opPattern","COPY",BODY,{"derivedFrom":makeQuery(id+"F1.opExtrude","SWEPT_BODY",BODY,{"disambiguationData":[OSD([sQuery(id+"F0.wireOp",EDGE,"E0")])]}),"instanceName":"1"}),"instanceName":"1"}),"instanceName":"1"});
            var Q283;
            Q283=makeQuery(id+"F18.opPattern","COPY",BODY,{"derivedFrom":makeQuery(id+"F17.opPattern","COPY",BODY,{"derivedFrom":makeQuery(id+"F12.opPattern","COPY",BODY,{"derivedFrom":makeQuery(id+"F11.opPattern","COPY",BODY,{"derivedFrom":makeQuery(id+"F10.opPattern","COPY",BODY,{"derivedFrom":makeQuery(id+"F1.opExtrude","SWEPT_BODY",BODY,{"disambiguationData":[OSD([sQuery(id+"F0.wireOp",EDGE,"E0")])]}),"instanceName":"1"}),"instanceName":"1"}),"instanceName":"1"}),"instanceName":"1"}),"instanceName":"1"});
            var Q284;
            Q284=makeQuery(id+"F16.opPattern","COPY",BODY,{"derivedFrom":makeQuery(id+"F15.opPattern","COPY",BODY,{"derivedFrom":makeQuery(id+"F14.opPattern","COPY",BODY,{"derivedFrom":makeQuery(id+"F1.opExtrude","SWEPT_BODY",BODY,{"disambiguationData":[OSD([sQuery(id+"F0.wireOp",EDGE,"E0")])]}),"instanceName":"1"}),"instanceName":"1"}),"instanceName":"1"});
            var Q285;
            Q285=makeQuery(id+"F17.opPattern","COPY",BODY,{"derivedFrom":makeQuery(id+"F10.opPattern","COPY",BODY,{"derivedFrom":makeQuery(id+"F1.opExtrude","SWEPT_BODY",BODY,{"disambiguationData":[OSD([sQuery(id+"F0.wireOp",EDGE,"E0")])]}),"instanceName":"1"}),"instanceName":"1"});
            var Q286;
            Q286=makeQuery(id+"F17.opPattern","COPY",BODY,{"derivedFrom":makeQuery(id+"F12.opPattern","COPY",BODY,{"derivedFrom":makeQuery(id+"F11.opPattern","COPY",BODY,{"derivedFrom":makeQuery(id+"F4.opPattern","COPY",BODY,{"derivedFrom":makeQuery(id+"F1.opExtrude","SWEPT_BODY",BODY,{"disambiguationData":[OSD([sQuery(id+"F0.wireOp",EDGE,"E0")])]}),"instanceName":"1"}),"instanceName":"1"}),"instanceName":"1"}),"instanceName":"1"});
            var Q287;
            Q287=makeQuery(id+"F17.opPattern","COPY",BODY,{"derivedFrom":makeQuery(id+"F14.opPattern","COPY",BODY,{"derivedFrom":makeQuery(id+"F4.opPattern","COPY",BODY,{"derivedFrom":makeQuery(id+"F1.opExtrude","SWEPT_BODY",BODY,{"disambiguationData":[OSD([sQuery(id+"F0.wireOp",EDGE,"E0")])]}),"instanceName":"1"}),"instanceName":"1"}),"instanceName":"1"});
            var Q288;
            Q288=makeQuery(id+"F15.opPattern","COPY",BODY,{"derivedFrom":makeQuery(id+"F12.opPattern","COPY",BODY,{"derivedFrom":makeQuery(id+"F11.opPattern","COPY",BODY,{"derivedFrom":makeQuery(id+"F9.opPattern","COPY",BODY,{"derivedFrom":makeQuery(id+"F1.opExtrude","SWEPT_BODY",BODY,{"disambiguationData":[OSD([sQuery(id+"F0.wireOp",EDGE,"E0")])]}),"instanceName":"1"}),"instanceName":"1"}),"instanceName":"1"}),"instanceName":"1"});
            var Q289;
            Q289=makeQuery(id+"F16.opPattern","COPY",BODY,{"derivedFrom":makeQuery(id+"F15.opPattern","COPY",BODY,{"derivedFrom":makeQuery(id+"F11.opPattern","COPY",BODY,{"derivedFrom":makeQuery(id+"F9.opPattern","COPY",BODY,{"derivedFrom":makeQuery(id+"F1.opExtrude","SWEPT_BODY",BODY,{"disambiguationData":[OSD([sQuery(id+"F0.wireOp",EDGE,"E0")])]}),"instanceName":"1"}),"instanceName":"1"}),"instanceName":"1"}),"instanceName":"1"});
            var Q290;
            Q290=makeQuery(id+"F17.opPattern","COPY",BODY,{"derivedFrom":makeQuery(id+"F14.opPattern","COPY",BODY,{"derivedFrom":makeQuery(id+"F11.opPattern","COPY",BODY,{"derivedFrom":makeQuery(id+"F10.opPattern","COPY",BODY,{"derivedFrom":makeQuery(id+"F1.opExtrude","SWEPT_BODY",BODY,{"disambiguationData":[OSD([sQuery(id+"F0.wireOp",EDGE,"E0")])]}),"instanceName":"1"}),"instanceName":"1"}),"instanceName":"1"}),"instanceName":"1"});
            var Q291;
            Q291=makeQuery(id+"F17.opPattern","COPY",BODY,{"derivedFrom":makeQuery(id+"F15.opPattern","COPY",BODY,{"derivedFrom":makeQuery(id+"F12.opPattern","COPY",BODY,{"derivedFrom":makeQuery(id+"F9.opPattern","COPY",BODY,{"derivedFrom":makeQuery(id+"F4.opPattern","COPY",BODY,{"derivedFrom":makeQuery(id+"F1.opExtrude","SWEPT_BODY",BODY,{"disambiguationData":[OSD([sQuery(id+"F0.wireOp",EDGE,"E0")])]}),"instanceName":"1"}),"instanceName":"1"}),"instanceName":"1"}),"instanceName":"1"}),"instanceName":"1"});
            var Q292;
            Q292=makeQuery(id+"F17.opPattern","COPY",BODY,{"derivedFrom":makeQuery(id+"F15.opPattern","COPY",BODY,{"derivedFrom":makeQuery(id+"F12.opPattern","COPY",BODY,{"derivedFrom":makeQuery(id+"F1.opExtrude","SWEPT_BODY",BODY,{"disambiguationData":[OSD([sQuery(id+"F0.wireOp",EDGE,"E0")])]}),"instanceName":"1"}),"instanceName":"1"}),"instanceName":"1"});
            var Q293;
            Q293=makeQuery(id+"F17.opPattern","COPY",BODY,{"derivedFrom":makeQuery(id+"F15.opPattern","COPY",BODY,{"derivedFrom":makeQuery(id+"F14.opPattern","COPY",BODY,{"derivedFrom":makeQuery(id+"F10.opPattern","COPY",BODY,{"derivedFrom":makeQuery(id+"F1.opExtrude","SWEPT_BODY",BODY,{"disambiguationData":[OSD([sQuery(id+"F0.wireOp",EDGE,"E0")])]}),"instanceName":"1"}),"instanceName":"1"}),"instanceName":"1"}),"instanceName":"1"});
            var Q294;
            Q294=makeQuery(id+"F16.opPattern","COPY",BODY,{"derivedFrom":makeQuery(id+"F15.opPattern","COPY",BODY,{"derivedFrom":makeQuery(id+"F14.opPattern","COPY",BODY,{"derivedFrom":makeQuery(id+"F11.opPattern","COPY",BODY,{"derivedFrom":makeQuery(id+"F9.opPattern","COPY",BODY,{"derivedFrom":makeQuery(id+"F1.opExtrude","SWEPT_BODY",BODY,{"disambiguationData":[OSD([sQuery(id+"F0.wireOp",EDGE,"E0")])]}),"instanceName":"1"}),"instanceName":"1"}),"instanceName":"1"}),"instanceName":"1"}),"instanceName":"1"});
            var Q295;
            Q295=makeQuery(id+"F17.opPattern","COPY",BODY,{"derivedFrom":makeQuery(id+"F15.opPattern","COPY",BODY,{"derivedFrom":makeQuery(id+"F12.opPattern","COPY",BODY,{"derivedFrom":makeQuery(id+"F11.opPattern","COPY",BODY,{"derivedFrom":makeQuery(id+"F9.opPattern","COPY",BODY,{"derivedFrom":makeQuery(id+"F1.opExtrude","SWEPT_BODY",BODY,{"disambiguationData":[OSD([sQuery(id+"F0.wireOp",EDGE,"E0")])]}),"instanceName":"1"}),"instanceName":"1"}),"instanceName":"1"}),"instanceName":"1"}),"instanceName":"1"});
            var Q296;
            Q296=makeQuery(id+"F17.opPattern","COPY",BODY,{"derivedFrom":makeQuery(id+"F16.opPattern","COPY",BODY,{"derivedFrom":makeQuery(id+"F4.opPattern","COPY",BODY,{"derivedFrom":makeQuery(id+"F1.opExtrude","SWEPT_BODY",BODY,{"disambiguationData":[OSD([sQuery(id+"F0.wireOp",EDGE,"E0")])]}),"instanceName":"1"}),"instanceName":"1"}),"instanceName":"1"});
            var Q297;
            Q297=makeQuery(id+"F17.opPattern","COPY",BODY,{"derivedFrom":makeQuery(id+"F16.opPattern","COPY",BODY,{"derivedFrom":makeQuery(id+"F12.opPattern","COPY",BODY,{"derivedFrom":makeQuery(id+"F1.opExtrude","SWEPT_BODY",BODY,{"disambiguationData":[OSD([sQuery(id+"F0.wireOp",EDGE,"E0")])]}),"instanceName":"1"}),"instanceName":"1"}),"instanceName":"1"});
            var Q298;
            Q298=makeQuery(id+"F17.opPattern","COPY",BODY,{"derivedFrom":makeQuery(id+"F16.opPattern","COPY",BODY,{"derivedFrom":makeQuery(id+"F11.opPattern","COPY",BODY,{"derivedFrom":makeQuery(id+"F9.opPattern","COPY",BODY,{"derivedFrom":makeQuery(id+"F4.opPattern","COPY",BODY,{"derivedFrom":makeQuery(id+"F1.opExtrude","SWEPT_BODY",BODY,{"disambiguationData":[OSD([sQuery(id+"F0.wireOp",EDGE,"E0")])]}),"instanceName":"1"}),"instanceName":"1"}),"instanceName":"1"}),"instanceName":"1"}),"instanceName":"1"});
            var Q299;
            Q299=makeQuery(id+"F17.opPattern","COPY",BODY,{"derivedFrom":makeQuery(id+"F16.opPattern","COPY",BODY,{"derivedFrom":makeQuery(id+"F11.opPattern","COPY",BODY,{"derivedFrom":makeQuery(id+"F1.opExtrude","SWEPT_BODY",BODY,{"disambiguationData":[OSD([sQuery(id+"F0.wireOp",EDGE,"E0")])]}),"instanceName":"1"}),"instanceName":"1"}),"instanceName":"1"});
            var Q300;
            Q300=makeQuery(id+"F17.opPattern","COPY",BODY,{"derivedFrom":makeQuery(id+"F16.opPattern","COPY",BODY,{"derivedFrom":makeQuery(id+"F12.opPattern","COPY",BODY,{"derivedFrom":makeQuery(id+"F11.opPattern","COPY",BODY,{"derivedFrom":makeQuery(id+"F10.opPattern","COPY",BODY,{"derivedFrom":makeQuery(id+"F1.opExtrude","SWEPT_BODY",BODY,{"disambiguationData":[OSD([sQuery(id+"F0.wireOp",EDGE,"E0")])]}),"instanceName":"1"}),"instanceName":"1"}),"instanceName":"1"}),"instanceName":"1"}),"instanceName":"1"});
            var Q301;
            Q301=makeQuery(id+"F17.opPattern","COPY",BODY,{"derivedFrom":makeQuery(id+"F16.opPattern","COPY",BODY,{"derivedFrom":makeQuery(id+"F12.opPattern","COPY",BODY,{"derivedFrom":makeQuery(id+"F9.opPattern","COPY",BODY,{"derivedFrom":makeQuery(id+"F4.opPattern","COPY",BODY,{"derivedFrom":makeQuery(id+"F1.opExtrude","SWEPT_BODY",BODY,{"disambiguationData":[OSD([sQuery(id+"F0.wireOp",EDGE,"E0")])]}),"instanceName":"1"}),"instanceName":"1"}),"instanceName":"1"}),"instanceName":"1"}),"instanceName":"1"});
            var Q302;
            Q302=makeQuery(id+"F17.opPattern","COPY",BODY,{"derivedFrom":makeQuery(id+"F16.opPattern","COPY",BODY,{"derivedFrom":makeQuery(id+"F15.opPattern","COPY",BODY,{"derivedFrom":makeQuery(id+"F4.opPattern","COPY",BODY,{"derivedFrom":makeQuery(id+"F1.opExtrude","SWEPT_BODY",BODY,{"disambiguationData":[OSD([sQuery(id+"F0.wireOp",EDGE,"E0")])]}),"instanceName":"1"}),"instanceName":"1"}),"instanceName":"1"}),"instanceName":"1"});
            var Q303;
            Q303=makeQuery(id+"F17.opPattern","COPY",BODY,{"derivedFrom":makeQuery(id+"F16.opPattern","COPY",BODY,{"derivedFrom":makeQuery(id+"F14.opPattern","COPY",BODY,{"derivedFrom":makeQuery(id+"F11.opPattern","COPY",BODY,{"derivedFrom":makeQuery(id+"F4.opPattern","COPY",BODY,{"derivedFrom":makeQuery(id+"F1.opExtrude","SWEPT_BODY",BODY,{"disambiguationData":[OSD([sQuery(id+"F0.wireOp",EDGE,"E0")])]}),"instanceName":"1"}),"instanceName":"1"}),"instanceName":"1"}),"instanceName":"1"}),"instanceName":"1"});
            var Q304;
            Q304=makeQuery(id+"F18.opPattern","COPY",BODY,{"derivedFrom":makeQuery(id+"F17.opPattern","COPY",BODY,{"derivedFrom":makeQuery(id+"F12.opPattern","COPY",BODY,{"derivedFrom":makeQuery(id+"F11.opPattern","COPY",BODY,{"derivedFrom":makeQuery(id+"F9.opPattern","COPY",BODY,{"derivedFrom":makeQuery(id+"F1.opExtrude","SWEPT_BODY",BODY,{"disambiguationData":[OSD([sQuery(id+"F0.wireOp",EDGE,"E0")])]}),"instanceName":"1"}),"instanceName":"1"}),"instanceName":"1"}),"instanceName":"1"}),"instanceName":"1"});
            var Q305;
            Q305=makeQuery(id+"F17.opPattern","COPY",BODY,{"derivedFrom":makeQuery(id+"F16.opPattern","COPY",BODY,{"derivedFrom":makeQuery(id+"F15.opPattern","COPY",BODY,{"derivedFrom":makeQuery(id+"F9.opPattern","COPY",BODY,{"derivedFrom":makeQuery(id+"F1.opExtrude","SWEPT_BODY",BODY,{"disambiguationData":[OSD([sQuery(id+"F0.wireOp",EDGE,"E0")])]}),"instanceName":"1"}),"instanceName":"1"}),"instanceName":"1"}),"instanceName":"1"});
            var Q306;
            Q306=makeQuery(id+"F17.opPattern","COPY",BODY,{"derivedFrom":makeQuery(id+"F16.opPattern","COPY",BODY,{"derivedFrom":makeQuery(id+"F15.opPattern","COPY",BODY,{"derivedFrom":makeQuery(id+"F12.opPattern","COPY",BODY,{"derivedFrom":makeQuery(id+"F10.opPattern","COPY",BODY,{"derivedFrom":makeQuery(id+"F1.opExtrude","SWEPT_BODY",BODY,{"disambiguationData":[OSD([sQuery(id+"F0.wireOp",EDGE,"E0")])]}),"instanceName":"1"}),"instanceName":"1"}),"instanceName":"1"}),"instanceName":"1"}),"instanceName":"1"});
            var Q307;
            Q307=makeQuery(id+"F16.opPattern","COPY",BODY,{"derivedFrom":makeQuery(id+"F15.opPattern","COPY",BODY,{"derivedFrom":makeQuery(id+"F11.opPattern","COPY",BODY,{"derivedFrom":makeQuery(id+"F9.opPattern","COPY",BODY,{"derivedFrom":makeQuery(id+"F4.opPattern","COPY",BODY,{"derivedFrom":makeQuery(id+"F1.opExtrude","SWEPT_BODY",BODY,{"disambiguationData":[OSD([sQuery(id+"F0.wireOp",EDGE,"E0")])]}),"instanceName":"1"}),"instanceName":"1"}),"instanceName":"1"}),"instanceName":"1"}),"instanceName":"1"});
            var Q308;
            Q308=makeQuery(id+"F17.opPattern","COPY",BODY,{"derivedFrom":makeQuery(id+"F16.opPattern","COPY",BODY,{"derivedFrom":makeQuery(id+"F15.opPattern","COPY",BODY,{"derivedFrom":makeQuery(id+"F14.opPattern","COPY",BODY,{"derivedFrom":makeQuery(id+"F11.opPattern","COPY",BODY,{"derivedFrom":makeQuery(id+"F9.opPattern","COPY",BODY,{"derivedFrom":makeQuery(id+"F1.opExtrude","SWEPT_BODY",BODY,{"disambiguationData":[OSD([sQuery(id+"F0.wireOp",EDGE,"E0")])]}),"instanceName":"1"}),"instanceName":"1"}),"instanceName":"1"}),"instanceName":"1"}),"instanceName":"1"}),"instanceName":"1"});
            var Q309;
            Q309=makeQuery(id+"F17.opPattern","COPY",BODY,{"derivedFrom":makeQuery(id+"F16.opPattern","COPY",BODY,{"derivedFrom":makeQuery(id+"F15.opPattern","COPY",BODY,{"derivedFrom":makeQuery(id+"F14.opPattern","COPY",BODY,{"derivedFrom":makeQuery(id+"F4.opPattern","COPY",BODY,{"derivedFrom":makeQuery(id+"F1.opExtrude","SWEPT_BODY",BODY,{"disambiguationData":[OSD([sQuery(id+"F0.wireOp",EDGE,"E0")])]}),"instanceName":"1"}),"instanceName":"1"}),"instanceName":"1"}),"instanceName":"1"}),"instanceName":"1"});
            var Q310;
            Q310=makeQuery(id+"F17.opPattern","COPY",BODY,{"derivedFrom":makeQuery(id+"F12.opPattern","COPY",BODY,{"derivedFrom":makeQuery(id+"F9.opPattern","COPY",BODY,{"derivedFrom":makeQuery(id+"F1.opExtrude","SWEPT_BODY",BODY,{"disambiguationData":[OSD([sQuery(id+"F0.wireOp",EDGE,"E0")])]}),"instanceName":"1"}),"instanceName":"1"}),"instanceName":"1"});
            var Q311;
            Q311=makeQuery(id+"F17.opPattern","COPY",BODY,{"derivedFrom":makeQuery(id+"F14.opPattern","COPY",BODY,{"derivedFrom":makeQuery(id+"F1.opExtrude","SWEPT_BODY",BODY,{"disambiguationData":[OSD([sQuery(id+"F0.wireOp",EDGE,"E0")])]}),"instanceName":"1"}),"instanceName":"1"});
            var Q312;
            Q312=makeQuery(id+"F17.opPattern","COPY",BODY,{"derivedFrom":makeQuery(id+"F15.opPattern","COPY",BODY,{"derivedFrom":makeQuery(id+"F11.opPattern","COPY",BODY,{"derivedFrom":makeQuery(id+"F4.opPattern","COPY",BODY,{"derivedFrom":makeQuery(id+"F1.opExtrude","SWEPT_BODY",BODY,{"disambiguationData":[OSD([sQuery(id+"F0.wireOp",EDGE,"E0")])]}),"instanceName":"1"}),"instanceName":"1"}),"instanceName":"1"}),"instanceName":"1"});
            var Q313;
            Q313=makeQuery(id+"F17.opPattern","COPY",BODY,{"derivedFrom":makeQuery(id+"F15.opPattern","COPY",BODY,{"derivedFrom":makeQuery(id+"F1.opExtrude","SWEPT_BODY",BODY,{"disambiguationData":[OSD([sQuery(id+"F0.wireOp",EDGE,"E0")])]}),"instanceName":"1"}),"instanceName":"1"});
            var Q314;
            Q314=makeQuery(id+"F17.opPattern","COPY",BODY,{"derivedFrom":makeQuery(id+"F15.opPattern","COPY",BODY,{"derivedFrom":makeQuery(id+"F14.opPattern","COPY",BODY,{"derivedFrom":makeQuery(id+"F11.opPattern","COPY",BODY,{"derivedFrom":makeQuery(id+"F10.opPattern","COPY",BODY,{"derivedFrom":makeQuery(id+"F1.opExtrude","SWEPT_BODY",BODY,{"disambiguationData":[OSD([sQuery(id+"F0.wireOp",EDGE,"E0")])]}),"instanceName":"1"}),"instanceName":"1"}),"instanceName":"1"}),"instanceName":"1"}),"instanceName":"1"});
            var Q315;
            Q315=makeQuery(id+"F17.opPattern","COPY",BODY,{"derivedFrom":makeQuery(id+"F15.opPattern","COPY",BODY,{"derivedFrom":makeQuery(id+"F12.opPattern","COPY",BODY,{"derivedFrom":makeQuery(id+"F11.opPattern","COPY",BODY,{"derivedFrom":makeQuery(id+"F10.opPattern","COPY",BODY,{"derivedFrom":makeQuery(id+"F1.opExtrude","SWEPT_BODY",BODY,{"disambiguationData":[OSD([sQuery(id+"F0.wireOp",EDGE,"E0")])]}),"instanceName":"1"}),"instanceName":"1"}),"instanceName":"1"}),"instanceName":"1"}),"instanceName":"1"});
            var Q316;
            Q316=makeQuery(id+"F17.opPattern","COPY",BODY,{"derivedFrom":makeQuery(id+"F16.opPattern","COPY",BODY,{"derivedFrom":makeQuery(id+"F12.opPattern","COPY",BODY,{"derivedFrom":makeQuery(id+"F9.opPattern","COPY",BODY,{"derivedFrom":makeQuery(id+"F1.opExtrude","SWEPT_BODY",BODY,{"disambiguationData":[OSD([sQuery(id+"F0.wireOp",EDGE,"E0")])]}),"instanceName":"1"}),"instanceName":"1"}),"instanceName":"1"}),"instanceName":"1"});
            var Q317;
            Q317=makeQuery(id+"F16.opPattern","COPY",BODY,{"derivedFrom":makeQuery(id+"F12.opPattern","COPY",BODY,{"derivedFrom":makeQuery(id+"F10.opPattern","COPY",BODY,{"derivedFrom":makeQuery(id+"F1.opExtrude","SWEPT_BODY",BODY,{"disambiguationData":[OSD([sQuery(id+"F0.wireOp",EDGE,"E0")])]}),"instanceName":"1"}),"instanceName":"1"}),"instanceName":"1"});
            var Q318;
            Q318=makeQuery(id+"F16.opPattern","COPY",BODY,{"derivedFrom":makeQuery(id+"F15.opPattern","COPY",BODY,{"derivedFrom":makeQuery(id+"F9.opPattern","COPY",BODY,{"derivedFrom":makeQuery(id+"F1.opExtrude","SWEPT_BODY",BODY,{"disambiguationData":[OSD([sQuery(id+"F0.wireOp",EDGE,"E0")])]}),"instanceName":"1"}),"instanceName":"1"}),"instanceName":"1"});
            var Q319;
            Q319=makeQuery(id+"F17.opPattern","COPY",BODY,{"derivedFrom":makeQuery(id+"F16.opPattern","COPY",BODY,{"derivedFrom":makeQuery(id+"F12.opPattern","COPY",BODY,{"derivedFrom":makeQuery(id+"F10.opPattern","COPY",BODY,{"derivedFrom":makeQuery(id+"F1.opExtrude","SWEPT_BODY",BODY,{"disambiguationData":[OSD([sQuery(id+"F0.wireOp",EDGE,"E0")])]}),"instanceName":"1"}),"instanceName":"1"}),"instanceName":"1"}),"instanceName":"1"});
            var Q320;
            Q320=makeQuery(id+"F17.opPattern","COPY",BODY,{"derivedFrom":makeQuery(id+"F16.opPattern","COPY",BODY,{"derivedFrom":makeQuery(id+"F14.opPattern","COPY",BODY,{"derivedFrom":makeQuery(id+"F11.opPattern","COPY",BODY,{"derivedFrom":makeQuery(id+"F9.opPattern","COPY",BODY,{"derivedFrom":makeQuery(id+"F4.opPattern","COPY",BODY,{"derivedFrom":makeQuery(id+"F1.opExtrude","SWEPT_BODY",BODY,{"disambiguationData":[OSD([sQuery(id+"F0.wireOp",EDGE,"E0")])]}),"instanceName":"1"}),"instanceName":"1"}),"instanceName":"1"}),"instanceName":"1"}),"instanceName":"1"}),"instanceName":"1"});
            var Q321;
            Q321=makeQuery(id+"F17.opPattern","COPY",BODY,{"derivedFrom":makeQuery(id+"F16.opPattern","COPY",BODY,{"derivedFrom":makeQuery(id+"F14.opPattern","COPY",BODY,{"derivedFrom":makeQuery(id+"F11.opPattern","COPY",BODY,{"derivedFrom":makeQuery(id+"F1.opExtrude","SWEPT_BODY",BODY,{"disambiguationData":[OSD([sQuery(id+"F0.wireOp",EDGE,"E0")])]}),"instanceName":"1"}),"instanceName":"1"}),"instanceName":"1"}),"instanceName":"1"});
            var Q322;
            Q322=makeQuery(id+"F17.opPattern","COPY",BODY,{"derivedFrom":makeQuery(id+"F16.opPattern","COPY",BODY,{"derivedFrom":makeQuery(id+"F15.opPattern","COPY",BODY,{"derivedFrom":makeQuery(id+"F9.opPattern","COPY",BODY,{"derivedFrom":makeQuery(id+"F4.opPattern","COPY",BODY,{"derivedFrom":makeQuery(id+"F1.opExtrude","SWEPT_BODY",BODY,{"disambiguationData":[OSD([sQuery(id+"F0.wireOp",EDGE,"E0")])]}),"instanceName":"1"}),"instanceName":"1"}),"instanceName":"1"}),"instanceName":"1"}),"instanceName":"1"});
            var Q323;
            Q323=makeQuery(id+"F17.opPattern","COPY",BODY,{"derivedFrom":makeQuery(id+"F16.opPattern","COPY",BODY,{"derivedFrom":makeQuery(id+"F15.opPattern","COPY",BODY,{"derivedFrom":makeQuery(id+"F1.opExtrude","SWEPT_BODY",BODY,{"disambiguationData":[OSD([sQuery(id+"F0.wireOp",EDGE,"E0")])]}),"instanceName":"1"}),"instanceName":"1"}),"instanceName":"1"});
            var Q324;
            Q324=makeQuery(id+"F17.opPattern","COPY",BODY,{"derivedFrom":makeQuery(id+"F16.opPattern","COPY",BODY,{"derivedFrom":makeQuery(id+"F15.opPattern","COPY",BODY,{"derivedFrom":makeQuery(id+"F12.opPattern","COPY",BODY,{"derivedFrom":makeQuery(id+"F9.opPattern","COPY",BODY,{"derivedFrom":makeQuery(id+"F4.opPattern","COPY",BODY,{"derivedFrom":makeQuery(id+"F1.opExtrude","SWEPT_BODY",BODY,{"disambiguationData":[OSD([sQuery(id+"F0.wireOp",EDGE,"E0")])]}),"instanceName":"1"}),"instanceName":"1"}),"instanceName":"1"}),"instanceName":"1"}),"instanceName":"1"}),"instanceName":"1"});
            var Q325;
            Q325=makeQuery(id+"F17.opPattern","COPY",BODY,{"derivedFrom":makeQuery(id+"F16.opPattern","COPY",BODY,{"derivedFrom":makeQuery(id+"F15.opPattern","COPY",BODY,{"derivedFrom":makeQuery(id+"F11.opPattern","COPY",BODY,{"derivedFrom":makeQuery(id+"F10.opPattern","COPY",BODY,{"derivedFrom":makeQuery(id+"F1.opExtrude","SWEPT_BODY",BODY,{"disambiguationData":[OSD([sQuery(id+"F0.wireOp",EDGE,"E0")])]}),"instanceName":"1"}),"instanceName":"1"}),"instanceName":"1"}),"instanceName":"1"}),"instanceName":"1"});
            var Q326;
            Q326=makeQuery(id+"F16.opPattern","COPY",BODY,{"derivedFrom":makeQuery(id+"F15.opPattern","COPY",BODY,{"derivedFrom":makeQuery(id+"F14.opPattern","COPY",BODY,{"derivedFrom":makeQuery(id+"F11.opPattern","COPY",BODY,{"derivedFrom":makeQuery(id+"F9.opPattern","COPY",BODY,{"derivedFrom":makeQuery(id+"F4.opPattern","COPY",BODY,{"derivedFrom":makeQuery(id+"F1.opExtrude","SWEPT_BODY",BODY,{"disambiguationData":[OSD([sQuery(id+"F0.wireOp",EDGE,"E0")])]}),"instanceName":"1"}),"instanceName":"1"}),"instanceName":"1"}),"instanceName":"1"}),"instanceName":"1"}),"instanceName":"1"});
            var Q327;
            Q327=makeQuery(id+"F17.opPattern","COPY",BODY,{"derivedFrom":makeQuery(id+"F16.opPattern","COPY",BODY,{"derivedFrom":makeQuery(id+"F15.opPattern","COPY",BODY,{"derivedFrom":makeQuery(id+"F14.opPattern","COPY",BODY,{"derivedFrom":makeQuery(id+"F1.opExtrude","SWEPT_BODY",BODY,{"disambiguationData":[OSD([sQuery(id+"F0.wireOp",EDGE,"E0")])]}),"instanceName":"1"}),"instanceName":"1"}),"instanceName":"1"}),"instanceName":"1"});
            var Q328;
            Q328=makeQuery(id+"F17.opPattern","COPY",BODY,{"derivedFrom":makeQuery(id+"F12.opPattern","COPY",BODY,{"derivedFrom":makeQuery(id+"F4.opPattern","COPY",BODY,{"derivedFrom":makeQuery(id+"F1.opExtrude","SWEPT_BODY",BODY,{"disambiguationData":[OSD([sQuery(id+"F0.wireOp",EDGE,"E0")])]}),"instanceName":"1"}),"instanceName":"1"}),"instanceName":"1"});
            var Q329;
            Q329=makeQuery(id+"F17.opPattern","COPY",BODY,{"derivedFrom":makeQuery(id+"F16.opPattern","COPY",BODY,{"derivedFrom":makeQuery(id+"F14.opPattern","COPY",BODY,{"derivedFrom":makeQuery(id+"F1.opExtrude","SWEPT_BODY",BODY,{"disambiguationData":[OSD([sQuery(id+"F0.wireOp",EDGE,"E0")])]}),"instanceName":"1"}),"instanceName":"1"}),"instanceName":"1"});
            var Q330;
            Q330=makeQuery(id+"F17.opPattern","COPY",BODY,{"derivedFrom":makeQuery(id+"F16.opPattern","COPY",BODY,{"derivedFrom":makeQuery(id+"F12.opPattern","COPY",BODY,{"derivedFrom":makeQuery(id+"F11.opPattern","COPY",BODY,{"derivedFrom":makeQuery(id+"F9.opPattern","COPY",BODY,{"derivedFrom":makeQuery(id+"F4.opPattern","COPY",BODY,{"derivedFrom":makeQuery(id+"F1.opExtrude","SWEPT_BODY",BODY,{"disambiguationData":[OSD([sQuery(id+"F0.wireOp",EDGE,"E0")])]}),"instanceName":"1"}),"instanceName":"1"}),"instanceName":"1"}),"instanceName":"1"}),"instanceName":"1"}),"instanceName":"1"});
            var Q331;
            Q331=makeQuery(id+"F17.opPattern","COPY",BODY,{"derivedFrom":makeQuery(id+"F11.opPattern","COPY",BODY,{"derivedFrom":makeQuery(id+"F1.opExtrude","SWEPT_BODY",BODY,{"disambiguationData":[OSD([sQuery(id+"F0.wireOp",EDGE,"E0")])]}),"instanceName":"1"}),"instanceName":"1"});
            var Q332;
            Q332=makeQuery(id+"F17.opPattern","COPY",BODY,{"derivedFrom":makeQuery(id+"F14.opPattern","COPY",BODY,{"derivedFrom":makeQuery(id+"F10.opPattern","COPY",BODY,{"derivedFrom":makeQuery(id+"F1.opExtrude","SWEPT_BODY",BODY,{"disambiguationData":[OSD([sQuery(id+"F0.wireOp",EDGE,"E0")])]}),"instanceName":"1"}),"instanceName":"1"}),"instanceName":"1"});
            var Q333;
            Q333=makeQuery(id+"F17.opPattern","COPY",BODY,{"derivedFrom":makeQuery(id+"F16.opPattern","COPY",BODY,{"derivedFrom":makeQuery(id+"F15.opPattern","COPY",BODY,{"derivedFrom":makeQuery(id+"F11.opPattern","COPY",BODY,{"derivedFrom":makeQuery(id+"F4.opPattern","COPY",BODY,{"derivedFrom":makeQuery(id+"F1.opExtrude","SWEPT_BODY",BODY,{"disambiguationData":[OSD([sQuery(id+"F0.wireOp",EDGE,"E0")])]}),"instanceName":"1"}),"instanceName":"1"}),"instanceName":"1"}),"instanceName":"1"}),"instanceName":"1"});
            var Q334;
            Q334=makeQuery(id+"F17.opPattern","COPY",BODY,{"derivedFrom":makeQuery(id+"F12.opPattern","COPY",BODY,{"derivedFrom":makeQuery(id+"F11.opPattern","COPY",BODY,{"derivedFrom":makeQuery(id+"F9.opPattern","COPY",BODY,{"derivedFrom":makeQuery(id+"F4.opPattern","COPY",BODY,{"derivedFrom":makeQuery(id+"F1.opExtrude","SWEPT_BODY",BODY,{"disambiguationData":[OSD([sQuery(id+"F0.wireOp",EDGE,"E0")])]}),"instanceName":"1"}),"instanceName":"1"}),"instanceName":"1"}),"instanceName":"1"}),"instanceName":"1"});
            var Q335;
            Q335=makeQuery(id+"F17.opPattern","COPY",BODY,{"derivedFrom":makeQuery(id+"F12.opPattern","COPY",BODY,{"derivedFrom":makeQuery(id+"F11.opPattern","COPY",BODY,{"derivedFrom":makeQuery(id+"F1.opExtrude","SWEPT_BODY",BODY,{"disambiguationData":[OSD([sQuery(id+"F0.wireOp",EDGE,"E0")])]}),"instanceName":"1"}),"instanceName":"1"}),"instanceName":"1"});
            var Q336;
            Q336=makeQuery(id+"F17.opPattern","COPY",BODY,{"derivedFrom":makeQuery(id+"F16.opPattern","COPY",BODY,{"derivedFrom":makeQuery(id+"F15.opPattern","COPY",BODY,{"derivedFrom":makeQuery(id+"F12.opPattern","COPY",BODY,{"derivedFrom":makeQuery(id+"F11.opPattern","COPY",BODY,{"derivedFrom":makeQuery(id+"F10.opPattern","COPY",BODY,{"derivedFrom":makeQuery(id+"F1.opExtrude","SWEPT_BODY",BODY,{"disambiguationData":[OSD([sQuery(id+"F0.wireOp",EDGE,"E0")])]}),"instanceName":"1"}),"instanceName":"1"}),"instanceName":"1"}),"instanceName":"1"}),"instanceName":"1"}),"instanceName":"1"});
            var Q337;
            Q337=makeQuery(id+"F17.opPattern","COPY",BODY,{"derivedFrom":makeQuery(id+"F15.opPattern","COPY",BODY,{"derivedFrom":makeQuery(id+"F12.opPattern","COPY",BODY,{"derivedFrom":makeQuery(id+"F9.opPattern","COPY",BODY,{"derivedFrom":makeQuery(id+"F1.opExtrude","SWEPT_BODY",BODY,{"disambiguationData":[OSD([sQuery(id+"F0.wireOp",EDGE,"E0")])]}),"instanceName":"1"}),"instanceName":"1"}),"instanceName":"1"}),"instanceName":"1"});
            var Q338;
            Q338=makeQuery(id+"F17.opPattern","COPY",BODY,{"derivedFrom":makeQuery(id+"F15.opPattern","COPY",BODY,{"derivedFrom":makeQuery(id+"F12.opPattern","COPY",BODY,{"derivedFrom":makeQuery(id+"F4.opPattern","COPY",BODY,{"derivedFrom":makeQuery(id+"F1.opExtrude","SWEPT_BODY",BODY,{"disambiguationData":[OSD([sQuery(id+"F0.wireOp",EDGE,"E0")])]}),"instanceName":"1"}),"instanceName":"1"}),"instanceName":"1"}),"instanceName":"1"});
            var Q339;
            Q339=makeQuery(id+"F17.opPattern","COPY",BODY,{"derivedFrom":makeQuery(id+"F16.opPattern","COPY",BODY,{"derivedFrom":makeQuery(id+"F15.opPattern","COPY",BODY,{"derivedFrom":makeQuery(id+"F14.opPattern","COPY",BODY,{"derivedFrom":makeQuery(id+"F11.opPattern","COPY",BODY,{"derivedFrom":makeQuery(id+"F10.opPattern","COPY",BODY,{"derivedFrom":makeQuery(id+"F1.opExtrude","SWEPT_BODY",BODY,{"disambiguationData":[OSD([sQuery(id+"F0.wireOp",EDGE,"E0")])]}),"instanceName":"1"}),"instanceName":"1"}),"instanceName":"1"}),"instanceName":"1"}),"instanceName":"1"}),"instanceName":"1"});
            var Q340;
            Q340=makeQuery(id+"F17.opPattern","COPY",BODY,{"derivedFrom":makeQuery(id+"F15.opPattern","COPY",BODY,{"derivedFrom":makeQuery(id+"F12.opPattern","COPY",BODY,{"derivedFrom":makeQuery(id+"F11.opPattern","COPY",BODY,{"derivedFrom":makeQuery(id+"F9.opPattern","COPY",BODY,{"derivedFrom":makeQuery(id+"F4.opPattern","COPY",BODY,{"derivedFrom":makeQuery(id+"F1.opExtrude","SWEPT_BODY",BODY,{"disambiguationData":[OSD([sQuery(id+"F0.wireOp",EDGE,"E0")])]}),"instanceName":"1"}),"instanceName":"1"}),"instanceName":"1"}),"instanceName":"1"}),"instanceName":"1"}),"instanceName":"1"});
            var Q341;
            Q341=makeQuery(id+"F17.opPattern","COPY",BODY,{"derivedFrom":makeQuery(id+"F15.opPattern","COPY",BODY,{"derivedFrom":makeQuery(id+"F12.opPattern","COPY",BODY,{"derivedFrom":makeQuery(id+"F11.opPattern","COPY",BODY,{"derivedFrom":makeQuery(id+"F1.opExtrude","SWEPT_BODY",BODY,{"disambiguationData":[OSD([sQuery(id+"F0.wireOp",EDGE,"E0")])]}),"instanceName":"1"}),"instanceName":"1"}),"instanceName":"1"}),"instanceName":"1"});
            var Q342;
            Q342=makeQuery(id+"F17.opPattern","COPY",BODY,{"derivedFrom":makeQuery(id+"F16.opPattern","COPY",BODY,{"derivedFrom":makeQuery(id+"F9.opPattern","COPY",BODY,{"derivedFrom":makeQuery(id+"F4.opPattern","COPY",BODY,{"derivedFrom":makeQuery(id+"F1.opExtrude","SWEPT_BODY",BODY,{"disambiguationData":[OSD([sQuery(id+"F0.wireOp",EDGE,"E0")])]}),"instanceName":"1"}),"instanceName":"1"}),"instanceName":"1"}),"instanceName":"1"});
            var Q343;
            Q343=makeQuery(id+"F17.opPattern","COPY",BODY,{"derivedFrom":makeQuery(id+"F16.opPattern","COPY",BODY,{"derivedFrom":makeQuery(id+"F1.opExtrude","SWEPT_BODY",BODY,{"disambiguationData":[OSD([sQuery(id+"F0.wireOp",EDGE,"E0")])]}),"instanceName":"1"}),"instanceName":"1"});
            var Q344;
            Q344=makeQuery(id+"F17.opPattern","COPY",BODY,{"derivedFrom":makeQuery(id+"F16.opPattern","COPY",BODY,{"derivedFrom":makeQuery(id+"F11.opPattern","COPY",BODY,{"derivedFrom":makeQuery(id+"F9.opPattern","COPY",BODY,{"derivedFrom":makeQuery(id+"F1.opExtrude","SWEPT_BODY",BODY,{"disambiguationData":[OSD([sQuery(id+"F0.wireOp",EDGE,"E0")])]}),"instanceName":"1"}),"instanceName":"1"}),"instanceName":"1"}),"instanceName":"1"});
            var Q345;
            Q345=makeQuery(id+"F17.opPattern","COPY",BODY,{"derivedFrom":makeQuery(id+"F14.opPattern","COPY",BODY,{"derivedFrom":makeQuery(id+"F11.opPattern","COPY",BODY,{"derivedFrom":makeQuery(id+"F1.opExtrude","SWEPT_BODY",BODY,{"disambiguationData":[OSD([sQuery(id+"F0.wireOp",EDGE,"E0")])]}),"instanceName":"1"}),"instanceName":"1"}),"instanceName":"1"});
            var Q346;
            Q346=makeQuery(id+"F17.opPattern","COPY",BODY,{"derivedFrom":makeQuery(id+"F15.opPattern","COPY",BODY,{"derivedFrom":makeQuery(id+"F4.opPattern","COPY",BODY,{"derivedFrom":makeQuery(id+"F1.opExtrude","SWEPT_BODY",BODY,{"disambiguationData":[OSD([sQuery(id+"F0.wireOp",EDGE,"E0")])]}),"instanceName":"1"}),"instanceName":"1"}),"instanceName":"1"});
            var Q347;
            Q347=makeQuery(id+"F17.opPattern","COPY",BODY,{"derivedFrom":makeQuery(id+"F15.opPattern","COPY",BODY,{"derivedFrom":makeQuery(id+"F11.opPattern","COPY",BODY,{"derivedFrom":makeQuery(id+"F10.opPattern","COPY",BODY,{"derivedFrom":makeQuery(id+"F1.opExtrude","SWEPT_BODY",BODY,{"disambiguationData":[OSD([sQuery(id+"F0.wireOp",EDGE,"E0")])]}),"instanceName":"1"}),"instanceName":"1"}),"instanceName":"1"}),"instanceName":"1"});
            var Q348;
            Q348=makeQuery(id+"F17.opPattern","COPY",BODY,{"derivedFrom":makeQuery(id+"F16.opPattern","COPY",BODY,{"derivedFrom":makeQuery(id+"F12.opPattern","COPY",BODY,{"derivedFrom":makeQuery(id+"F4.opPattern","COPY",BODY,{"derivedFrom":makeQuery(id+"F1.opExtrude","SWEPT_BODY",BODY,{"disambiguationData":[OSD([sQuery(id+"F0.wireOp",EDGE,"E0")])]}),"instanceName":"1"}),"instanceName":"1"}),"instanceName":"1"}),"instanceName":"1"});
            var Q349;
            Q349=makeQuery(id+"F18.opPattern","COPY",BODY,{"derivedFrom":makeQuery(id+"F12.opPattern","COPY",BODY,{"derivedFrom":makeQuery(id+"F1.opExtrude","SWEPT_BODY",BODY,{"disambiguationData":[OSD([sQuery(id+"F0.wireOp",EDGE,"E0")])]}),"instanceName":"1"}),"instanceName":"1"});
            var Q350;
            Q350=makeQuery(id+"F17.opPattern","COPY",BODY,{"derivedFrom":makeQuery(id+"F16.opPattern","COPY",BODY,{"derivedFrom":makeQuery(id+"F12.opPattern","COPY",BODY,{"derivedFrom":makeQuery(id+"F11.opPattern","COPY",BODY,{"derivedFrom":makeQuery(id+"F1.opExtrude","SWEPT_BODY",BODY,{"disambiguationData":[OSD([sQuery(id+"F0.wireOp",EDGE,"E0")])]}),"instanceName":"1"}),"instanceName":"1"}),"instanceName":"1"}),"instanceName":"1"});
            var Q351;
            Q351=makeQuery(id+"F16.opPattern","COPY",BODY,{"derivedFrom":makeQuery(id+"F14.opPattern","COPY",BODY,{"derivedFrom":makeQuery(id+"F11.opPattern","COPY",BODY,{"derivedFrom":makeQuery(id+"F4.opPattern","COPY",BODY,{"derivedFrom":makeQuery(id+"F1.opExtrude","SWEPT_BODY",BODY,{"disambiguationData":[OSD([sQuery(id+"F0.wireOp",EDGE,"E0")])]}),"instanceName":"1"}),"instanceName":"1"}),"instanceName":"1"}),"instanceName":"1"});
            var Q352;
            Q352=makeQuery(id+"F17.opPattern","COPY",BODY,{"derivedFrom":makeQuery(id+"F12.opPattern","COPY",BODY,{"derivedFrom":makeQuery(id+"F9.opPattern","COPY",BODY,{"derivedFrom":makeQuery(id+"F4.opPattern","COPY",BODY,{"derivedFrom":makeQuery(id+"F1.opExtrude","SWEPT_BODY",BODY,{"disambiguationData":[OSD([sQuery(id+"F0.wireOp",EDGE,"E0")])]}),"instanceName":"1"}),"instanceName":"1"}),"instanceName":"1"}),"instanceName":"1"});
            var Q353;
            Q353=makeQuery(id+"F17.opPattern","COPY",BODY,{"derivedFrom":makeQuery(id+"F11.opPattern","COPY",BODY,{"derivedFrom":makeQuery(id+"F9.opPattern","COPY",BODY,{"derivedFrom":makeQuery(id+"F1.opExtrude","SWEPT_BODY",BODY,{"disambiguationData":[OSD([sQuery(id+"F0.wireOp",EDGE,"E0")])]}),"instanceName":"1"}),"instanceName":"1"}),"instanceName":"1"});
            var Q354;
            Q354=makeQuery(id+"F16.opPattern","COPY",BODY,{"derivedFrom":makeQuery(id+"F12.opPattern","COPY",BODY,{"derivedFrom":makeQuery(id+"F11.opPattern","COPY",BODY,{"derivedFrom":makeQuery(id+"F10.opPattern","COPY",BODY,{"derivedFrom":makeQuery(id+"F1.opExtrude","SWEPT_BODY",BODY,{"disambiguationData":[OSD([sQuery(id+"F0.wireOp",EDGE,"E0")])]}),"instanceName":"1"}),"instanceName":"1"}),"instanceName":"1"}),"instanceName":"1"});
            var Q355;
            Q355=makeQuery(id+"F17.opPattern","COPY",BODY,{"derivedFrom":makeQuery(id+"F16.opPattern","COPY",BODY,{"derivedFrom":makeQuery(id+"F15.opPattern","COPY",BODY,{"derivedFrom":makeQuery(id+"F11.opPattern","COPY",BODY,{"derivedFrom":makeQuery(id+"F9.opPattern","COPY",BODY,{"derivedFrom":makeQuery(id+"F1.opExtrude","SWEPT_BODY",BODY,{"disambiguationData":[OSD([sQuery(id+"F0.wireOp",EDGE,"E0")])]}),"instanceName":"1"}),"instanceName":"1"}),"instanceName":"1"}),"instanceName":"1"}),"instanceName":"1"});
            var Q356;
            Q356=makeQuery(id+"F17.opPattern","COPY",BODY,{"derivedFrom":makeQuery(id+"F16.opPattern","COPY",BODY,{"derivedFrom":makeQuery(id+"F15.opPattern","COPY",BODY,{"derivedFrom":makeQuery(id+"F14.opPattern","COPY",BODY,{"derivedFrom":makeQuery(id+"F11.opPattern","COPY",BODY,{"derivedFrom":makeQuery(id+"F9.opPattern","COPY",BODY,{"derivedFrom":makeQuery(id+"F4.opPattern","COPY",BODY,{"derivedFrom":makeQuery(id+"F1.opExtrude","SWEPT_BODY",BODY,{"disambiguationData":[OSD([sQuery(id+"F0.wireOp",EDGE,"E0")])]}),"instanceName":"1"}),"instanceName":"1"}),"instanceName":"1"}),"instanceName":"1"}),"instanceName":"1"}),"instanceName":"1"}),"instanceName":"1"});
            var Q357;
            Q357=makeQuery(id+"F17.opPattern","COPY",BODY,{"derivedFrom":makeQuery(id+"F16.opPattern","COPY",BODY,{"derivedFrom":makeQuery(id+"F15.opPattern","COPY",BODY,{"derivedFrom":makeQuery(id+"F14.opPattern","COPY",BODY,{"derivedFrom":makeQuery(id+"F11.opPattern","COPY",BODY,{"derivedFrom":makeQuery(id+"F1.opExtrude","SWEPT_BODY",BODY,{"disambiguationData":[OSD([sQuery(id+"F0.wireOp",EDGE,"E0")])]}),"instanceName":"1"}),"instanceName":"1"}),"instanceName":"1"}),"instanceName":"1"}),"instanceName":"1"});
            var Q358;
            Q358=makeQuery(id+"F17.opPattern","COPY",BODY,{"derivedFrom":makeQuery(id+"F16.opPattern","COPY",BODY,{"derivedFrom":makeQuery(id+"F15.opPattern","COPY",BODY,{"derivedFrom":makeQuery(id+"F12.opPattern","COPY",BODY,{"derivedFrom":makeQuery(id+"F11.opPattern","COPY",BODY,{"derivedFrom":makeQuery(id+"F9.opPattern","COPY",BODY,{"derivedFrom":makeQuery(id+"F1.opExtrude","SWEPT_BODY",BODY,{"disambiguationData":[OSD([sQuery(id+"F0.wireOp",EDGE,"E0")])]}),"instanceName":"1"}),"instanceName":"1"}),"instanceName":"1"}),"instanceName":"1"}),"instanceName":"1"}),"instanceName":"1"});
            var Q359;
            Q359=makeQuery(id+"F17.opPattern","COPY",BODY,{"derivedFrom":makeQuery(id+"F16.opPattern","COPY",BODY,{"derivedFrom":makeQuery(id+"F15.opPattern","COPY",BODY,{"derivedFrom":makeQuery(id+"F14.opPattern","COPY",BODY,{"derivedFrom":makeQuery(id+"F10.opPattern","COPY",BODY,{"derivedFrom":makeQuery(id+"F1.opExtrude","SWEPT_BODY",BODY,{"disambiguationData":[OSD([sQuery(id+"F0.wireOp",EDGE,"E0")])]}),"instanceName":"1"}),"instanceName":"1"}),"instanceName":"1"}),"instanceName":"1"}),"instanceName":"1"});
            var Q360;
            Q360=makeQuery(id+"F18.opPattern","COPY",BODY,{"derivedFrom":makeQuery(id+"F16.opPattern","COPY",BODY,{"derivedFrom":makeQuery(id+"F14.opPattern","COPY",BODY,{"derivedFrom":makeQuery(id+"F11.opPattern","COPY",BODY,{"derivedFrom":makeQuery(id+"F9.opPattern","COPY",BODY,{"derivedFrom":makeQuery(id+"F1.opExtrude","SWEPT_BODY",BODY,{"disambiguationData":[OSD([sQuery(id+"F0.wireOp",EDGE,"E0")])]}),"instanceName":"1"}),"instanceName":"1"}),"instanceName":"1"}),"instanceName":"1"}),"instanceName":"1"});
            var Q361;
            Q361=makeQuery(id+"F17.opPattern","COPY",BODY,{"derivedFrom":makeQuery(id+"F16.opPattern","COPY",BODY,{"derivedFrom":makeQuery(id+"F11.opPattern","COPY",BODY,{"derivedFrom":makeQuery(id+"F4.opPattern","COPY",BODY,{"derivedFrom":makeQuery(id+"F1.opExtrude","SWEPT_BODY",BODY,{"disambiguationData":[OSD([sQuery(id+"F0.wireOp",EDGE,"E0")])]}),"instanceName":"1"}),"instanceName":"1"}),"instanceName":"1"}),"instanceName":"1"});
            var Q362;
            Q362=makeQuery(id+"F18.opPattern","COPY",BODY,{"derivedFrom":makeQuery(id+"F16.opPattern","COPY",BODY,{"derivedFrom":makeQuery(id+"F11.opPattern","COPY",BODY,{"derivedFrom":makeQuery(id+"F10.opPattern","COPY",BODY,{"derivedFrom":makeQuery(id+"F1.opExtrude","SWEPT_BODY",BODY,{"disambiguationData":[OSD([sQuery(id+"F0.wireOp",EDGE,"E0")])]}),"instanceName":"1"}),"instanceName":"1"}),"instanceName":"1"}),"instanceName":"1"});
            var Q363;
            Q363=makeQuery(id+"F17.opPattern","COPY",BODY,{"derivedFrom":makeQuery(id+"F15.opPattern","COPY",BODY,{"derivedFrom":makeQuery(id+"F12.opPattern","COPY",BODY,{"derivedFrom":makeQuery(id+"F10.opPattern","COPY",BODY,{"derivedFrom":makeQuery(id+"F1.opExtrude","SWEPT_BODY",BODY,{"disambiguationData":[OSD([sQuery(id+"F0.wireOp",EDGE,"E0")])]}),"instanceName":"1"}),"instanceName":"1"}),"instanceName":"1"}),"instanceName":"1"});
            var Q364;
            Q364=makeQuery(id+"F18.opPattern","COPY",BODY,{"derivedFrom":makeQuery(id+"F12.opPattern","COPY",BODY,{"derivedFrom":makeQuery(id+"F11.opPattern","COPY",BODY,{"derivedFrom":makeQuery(id+"F9.opPattern","COPY",BODY,{"derivedFrom":makeQuery(id+"F1.opExtrude","SWEPT_BODY",BODY,{"disambiguationData":[OSD([sQuery(id+"F0.wireOp",EDGE,"E0")])]}),"instanceName":"1"}),"instanceName":"1"}),"instanceName":"1"}),"instanceName":"1"});
            var Q365;
            Q365=makeQuery(id+"F17.opPattern","COPY",BODY,{"derivedFrom":makeQuery(id+"F16.opPattern","COPY",BODY,{"derivedFrom":makeQuery(id+"F14.opPattern","COPY",BODY,{"derivedFrom":makeQuery(id+"F4.opPattern","COPY",BODY,{"derivedFrom":makeQuery(id+"F1.opExtrude","SWEPT_BODY",BODY,{"disambiguationData":[OSD([sQuery(id+"F0.wireOp",EDGE,"E0")])]}),"instanceName":"1"}),"instanceName":"1"}),"instanceName":"1"}),"instanceName":"1"});
            var Q366;
            Q366=makeQuery(id+"F18.opPattern","COPY",BODY,{"derivedFrom":makeQuery(id+"F15.opPattern","COPY",BODY,{"derivedFrom":makeQuery(id+"F11.opPattern","COPY",BODY,{"derivedFrom":makeQuery(id+"F1.opExtrude","SWEPT_BODY",BODY,{"disambiguationData":[OSD([sQuery(id+"F0.wireOp",EDGE,"E0")])]}),"instanceName":"1"}),"instanceName":"1"}),"instanceName":"1"});
            var Q367;
            Q367=makeQuery(id+"F16.opPattern","COPY",BODY,{"derivedFrom":makeQuery(id+"F15.opPattern","COPY",BODY,{"derivedFrom":makeQuery(id+"F9.opPattern","COPY",BODY,{"derivedFrom":makeQuery(id+"F4.opPattern","COPY",BODY,{"derivedFrom":makeQuery(id+"F1.opExtrude","SWEPT_BODY",BODY,{"disambiguationData":[OSD([sQuery(id+"F0.wireOp",EDGE,"E0")])]}),"instanceName":"1"}),"instanceName":"1"}),"instanceName":"1"}),"instanceName":"1"});
            var Q368;
            Q368=makeQuery(id+"F18.opPattern","COPY",BODY,{"derivedFrom":makeQuery(id+"F17.opPattern","COPY",BODY,{"derivedFrom":makeQuery(id+"F15.opPattern","COPY",BODY,{"derivedFrom":makeQuery(id+"F11.opPattern","COPY",BODY,{"derivedFrom":makeQuery(id+"F1.opExtrude","SWEPT_BODY",BODY,{"disambiguationData":[OSD([sQuery(id+"F0.wireOp",EDGE,"E0")])]}),"instanceName":"1"}),"instanceName":"1"}),"instanceName":"1"}),"instanceName":"1"});
            var Q369;
            Q369=makeQuery(id+"F18.opPattern","COPY",BODY,{"derivedFrom":makeQuery(id+"F15.opPattern","COPY",BODY,{"derivedFrom":makeQuery(id+"F14.opPattern","COPY",BODY,{"derivedFrom":makeQuery(id+"F11.opPattern","COPY",BODY,{"derivedFrom":makeQuery(id+"F4.opPattern","COPY",BODY,{"derivedFrom":makeQuery(id+"F1.opExtrude","SWEPT_BODY",BODY,{"disambiguationData":[OSD([sQuery(id+"F0.wireOp",EDGE,"E0")])]}),"instanceName":"1"}),"instanceName":"1"}),"instanceName":"1"}),"instanceName":"1"}),"instanceName":"1"});
            var Q370;
            Q370=makeQuery(id+"F16.opPattern","COPY",BODY,{"derivedFrom":makeQuery(id+"F12.opPattern","COPY",BODY,{"derivedFrom":makeQuery(id+"F11.opPattern","COPY",BODY,{"derivedFrom":makeQuery(id+"F9.opPattern","COPY",BODY,{"derivedFrom":makeQuery(id+"F1.opExtrude","SWEPT_BODY",BODY,{"disambiguationData":[OSD([sQuery(id+"F0.wireOp",EDGE,"E0")])]}),"instanceName":"1"}),"instanceName":"1"}),"instanceName":"1"}),"instanceName":"1"});
            var Q371;
            Q371=makeQuery(id+"F17.opPattern","COPY",BODY,{"derivedFrom":makeQuery(id+"F12.opPattern","COPY",BODY,{"derivedFrom":makeQuery(id+"F1.opExtrude","SWEPT_BODY",BODY,{"disambiguationData":[OSD([sQuery(id+"F0.wireOp",EDGE,"E0")])]}),"instanceName":"1"}),"instanceName":"1"});
            var Q372;
            Q372=makeQuery(id+"F18.opPattern","COPY",BODY,{"derivedFrom":makeQuery(id+"F16.opPattern","COPY",BODY,{"derivedFrom":makeQuery(id+"F15.opPattern","COPY",BODY,{"derivedFrom":makeQuery(id+"F14.opPattern","COPY",BODY,{"derivedFrom":makeQuery(id+"F11.opPattern","COPY",BODY,{"derivedFrom":makeQuery(id+"F10.opPattern","COPY",BODY,{"derivedFrom":makeQuery(id+"F1.opExtrude","SWEPT_BODY",BODY,{"disambiguationData":[OSD([sQuery(id+"F0.wireOp",EDGE,"E0")])]}),"instanceName":"1"}),"instanceName":"1"}),"instanceName":"1"}),"instanceName":"1"}),"instanceName":"1"}),"instanceName":"1"});
            var Q373;
            Q373=makeQuery(id+"F17.opPattern","COPY",BODY,{"derivedFrom":makeQuery(id+"F15.opPattern","COPY",BODY,{"derivedFrom":makeQuery(id+"F10.opPattern","COPY",BODY,{"derivedFrom":makeQuery(id+"F1.opExtrude","SWEPT_BODY",BODY,{"disambiguationData":[OSD([sQuery(id+"F0.wireOp",EDGE,"E0")])]}),"instanceName":"1"}),"instanceName":"1"}),"instanceName":"1"});
            var Q374;
            Q374=makeQuery(id+"F17.opPattern","COPY",BODY,{"derivedFrom":makeQuery(id+"F15.opPattern","COPY",BODY,{"derivedFrom":makeQuery(id+"F12.opPattern","COPY",BODY,{"derivedFrom":makeQuery(id+"F11.opPattern","COPY",BODY,{"derivedFrom":makeQuery(id+"F4.opPattern","COPY",BODY,{"derivedFrom":makeQuery(id+"F1.opExtrude","SWEPT_BODY",BODY,{"disambiguationData":[OSD([sQuery(id+"F0.wireOp",EDGE,"E0")])]}),"instanceName":"1"}),"instanceName":"1"}),"instanceName":"1"}),"instanceName":"1"}),"instanceName":"1"});
            var Q375;
            Q375=makeQuery(id+"F17.opPattern","COPY",BODY,{"derivedFrom":makeQuery(id+"F16.opPattern","COPY",BODY,{"derivedFrom":makeQuery(id+"F12.opPattern","COPY",BODY,{"derivedFrom":makeQuery(id+"F11.opPattern","COPY",BODY,{"derivedFrom":makeQuery(id+"F9.opPattern","COPY",BODY,{"derivedFrom":makeQuery(id+"F1.opExtrude","SWEPT_BODY",BODY,{"disambiguationData":[OSD([sQuery(id+"F0.wireOp",EDGE,"E0")])]}),"instanceName":"1"}),"instanceName":"1"}),"instanceName":"1"}),"instanceName":"1"}),"instanceName":"1"});
            var Q376;
            Q376=makeQuery(id+"F17.opPattern","COPY",BODY,{"derivedFrom":makeQuery(id+"F16.opPattern","COPY",BODY,{"derivedFrom":makeQuery(id+"F15.opPattern","COPY",BODY,{"derivedFrom":makeQuery(id+"F11.opPattern","COPY",BODY,{"derivedFrom":makeQuery(id+"F9.opPattern","COPY",BODY,{"derivedFrom":makeQuery(id+"F4.opPattern","COPY",BODY,{"derivedFrom":makeQuery(id+"F1.opExtrude","SWEPT_BODY",BODY,{"disambiguationData":[OSD([sQuery(id+"F0.wireOp",EDGE,"E0")])]}),"instanceName":"1"}),"instanceName":"1"}),"instanceName":"1"}),"instanceName":"1"}),"instanceName":"1"}),"instanceName":"1"});
            var Q377;
            Q377=makeQuery(id+"F17.opPattern","COPY",BODY,{"derivedFrom":makeQuery(id+"F16.opPattern","COPY",BODY,{"derivedFrom":makeQuery(id+"F15.opPattern","COPY",BODY,{"derivedFrom":makeQuery(id+"F11.opPattern","COPY",BODY,{"derivedFrom":makeQuery(id+"F1.opExtrude","SWEPT_BODY",BODY,{"disambiguationData":[OSD([sQuery(id+"F0.wireOp",EDGE,"E0")])]}),"instanceName":"1"}),"instanceName":"1"}),"instanceName":"1"}),"instanceName":"1"});
            var Q378;
            Q378=makeQuery(id+"F17.opPattern","COPY",BODY,{"derivedFrom":makeQuery(id+"F15.opPattern","COPY",BODY,{"derivedFrom":makeQuery(id+"F14.opPattern","COPY",BODY,{"derivedFrom":makeQuery(id+"F11.opPattern","COPY",BODY,{"derivedFrom":makeQuery(id+"F9.opPattern","COPY",BODY,{"derivedFrom":makeQuery(id+"F4.opPattern","COPY",BODY,{"derivedFrom":makeQuery(id+"F1.opExtrude","SWEPT_BODY",BODY,{"disambiguationData":[OSD([sQuery(id+"F0.wireOp",EDGE,"E0")])]}),"instanceName":"1"}),"instanceName":"1"}),"instanceName":"1"}),"instanceName":"1"}),"instanceName":"1"}),"instanceName":"1"});
            var Q379;
            Q379=makeQuery(id+"F16.opPattern","COPY",BODY,{"derivedFrom":makeQuery(id+"F15.opPattern","COPY",BODY,{"derivedFrom":makeQuery(id+"F14.opPattern","COPY",BODY,{"derivedFrom":makeQuery(id+"F11.opPattern","COPY",BODY,{"derivedFrom":makeQuery(id+"F1.opExtrude","SWEPT_BODY",BODY,{"disambiguationData":[OSD([sQuery(id+"F0.wireOp",EDGE,"E0")])]}),"instanceName":"1"}),"instanceName":"1"}),"instanceName":"1"}),"instanceName":"1"});
            var Q380;
            Q380=makeQuery(id+"F17.opPattern","COPY",BODY,{"derivedFrom":makeQuery(id+"F16.opPattern","COPY",BODY,{"derivedFrom":makeQuery(id+"F9.opPattern","COPY",BODY,{"derivedFrom":makeQuery(id+"F1.opExtrude","SWEPT_BODY",BODY,{"disambiguationData":[OSD([sQuery(id+"F0.wireOp",EDGE,"E0")])]}),"instanceName":"1"}),"instanceName":"1"}),"instanceName":"1"});
            var Q381;
            Q381=makeQuery(id+"F17.opPattern","COPY",BODY,{"derivedFrom":makeQuery(id+"F11.opPattern","COPY",BODY,{"derivedFrom":makeQuery(id+"F10.opPattern","COPY",BODY,{"derivedFrom":makeQuery(id+"F1.opExtrude","SWEPT_BODY",BODY,{"disambiguationData":[OSD([sQuery(id+"F0.wireOp",EDGE,"E0")])]}),"instanceName":"1"}),"instanceName":"1"}),"instanceName":"1"});
            var Q382;
            Q382=makeQuery(id+"F17.opPattern","COPY",BODY,{"derivedFrom":makeQuery(id+"F11.opPattern","COPY",BODY,{"derivedFrom":makeQuery(id+"F4.opPattern","COPY",BODY,{"derivedFrom":makeQuery(id+"F1.opExtrude","SWEPT_BODY",BODY,{"disambiguationData":[OSD([sQuery(id+"F0.wireOp",EDGE,"E0")])]}),"instanceName":"1"}),"instanceName":"1"}),"instanceName":"1"});
            var Q383;
            Q383=makeQuery(id+"F17.opPattern","COPY",BODY,{"derivedFrom":makeQuery(id+"F16.opPattern","COPY",BODY,{"derivedFrom":makeQuery(id+"F15.opPattern","COPY",BODY,{"derivedFrom":makeQuery(id+"F12.opPattern","COPY",BODY,{"derivedFrom":makeQuery(id+"F9.opPattern","COPY",BODY,{"derivedFrom":makeQuery(id+"F1.opExtrude","SWEPT_BODY",BODY,{"disambiguationData":[OSD([sQuery(id+"F0.wireOp",EDGE,"E0")])]}),"instanceName":"1"}),"instanceName":"1"}),"instanceName":"1"}),"instanceName":"1"}),"instanceName":"1"});
            var Q384;
            Q384=makeQuery(id+"F17.opPattern","COPY",BODY,{"derivedFrom":makeQuery(id+"F14.opPattern","COPY",BODY,{"derivedFrom":makeQuery(id+"F11.opPattern","COPY",BODY,{"derivedFrom":makeQuery(id+"F9.opPattern","COPY",BODY,{"derivedFrom":makeQuery(id+"F1.opExtrude","SWEPT_BODY",BODY,{"disambiguationData":[OSD([sQuery(id+"F0.wireOp",EDGE,"E0")])]}),"instanceName":"1"}),"instanceName":"1"}),"instanceName":"1"}),"instanceName":"1"});
            var Q385;
            Q385=makeQuery(id+"F17.opPattern","COPY",BODY,{"derivedFrom":makeQuery(id+"F11.opPattern","COPY",BODY,{"derivedFrom":makeQuery(id+"F9.opPattern","COPY",BODY,{"derivedFrom":makeQuery(id+"F4.opPattern","COPY",BODY,{"derivedFrom":makeQuery(id+"F1.opExtrude","SWEPT_BODY",BODY,{"disambiguationData":[OSD([sQuery(id+"F0.wireOp",EDGE,"E0")])]}),"instanceName":"1"}),"instanceName":"1"}),"instanceName":"1"}),"instanceName":"1"});
            var Q386;
            Q386=makeQuery(id+"F17.opPattern","COPY",BODY,{"derivedFrom":makeQuery(id+"F14.opPattern","COPY",BODY,{"derivedFrom":makeQuery(id+"F11.opPattern","COPY",BODY,{"derivedFrom":makeQuery(id+"F4.opPattern","COPY",BODY,{"derivedFrom":makeQuery(id+"F1.opExtrude","SWEPT_BODY",BODY,{"disambiguationData":[OSD([sQuery(id+"F0.wireOp",EDGE,"E0")])]}),"instanceName":"1"}),"instanceName":"1"}),"instanceName":"1"}),"instanceName":"1"});
            var Q387;
            Q387=makeQuery(id+"F17.opPattern","COPY",BODY,{"derivedFrom":makeQuery(id+"F16.opPattern","COPY",BODY,{"derivedFrom":makeQuery(id+"F15.opPattern","COPY",BODY,{"derivedFrom":makeQuery(id+"F14.opPattern","COPY",BODY,{"derivedFrom":makeQuery(id+"F11.opPattern","COPY",BODY,{"derivedFrom":makeQuery(id+"F4.opPattern","COPY",BODY,{"derivedFrom":makeQuery(id+"F1.opExtrude","SWEPT_BODY",BODY,{"disambiguationData":[OSD([sQuery(id+"F0.wireOp",EDGE,"E0")])]}),"instanceName":"1"}),"instanceName":"1"}),"instanceName":"1"}),"instanceName":"1"}),"instanceName":"1"}),"instanceName":"1"});
            var Q388;
            Q388=makeQuery(id+"F17.opPattern","COPY",BODY,{"derivedFrom":makeQuery(id+"F16.opPattern","COPY",BODY,{"derivedFrom":makeQuery(id+"F12.opPattern","COPY",BODY,{"derivedFrom":makeQuery(id+"F11.opPattern","COPY",BODY,{"derivedFrom":makeQuery(id+"F4.opPattern","COPY",BODY,{"derivedFrom":makeQuery(id+"F1.opExtrude","SWEPT_BODY",BODY,{"disambiguationData":[OSD([sQuery(id+"F0.wireOp",EDGE,"E0")])]}),"instanceName":"1"}),"instanceName":"1"}),"instanceName":"1"}),"instanceName":"1"}),"instanceName":"1"});
            var Q389;
            Q389=makeQuery(id+"F17.opPattern","COPY",BODY,{"derivedFrom":makeQuery(id+"F9.opPattern","COPY",BODY,{"derivedFrom":makeQuery(id+"F4.opPattern","COPY",BODY,{"derivedFrom":makeQuery(id+"F1.opExtrude","SWEPT_BODY",BODY,{"disambiguationData":[OSD([sQuery(id+"F0.wireOp",EDGE,"E0")])]}),"instanceName":"1"}),"instanceName":"1"}),"instanceName":"1"});
            var Q390;
            Q390=makeQuery(id+"F17.opPattern","COPY",BODY,{"derivedFrom":makeQuery(id+"F15.opPattern","COPY",BODY,{"derivedFrom":makeQuery(id+"F14.opPattern","COPY",BODY,{"derivedFrom":makeQuery(id+"F1.opExtrude","SWEPT_BODY",BODY,{"disambiguationData":[OSD([sQuery(id+"F0.wireOp",EDGE,"E0")])]}),"instanceName":"1"}),"instanceName":"1"}),"instanceName":"1"});
            var Q391;
            Q391=makeQuery(id+"F17.opPattern","COPY",BODY,{"derivedFrom":makeQuery(id+"F12.opPattern","COPY",BODY,{"derivedFrom":makeQuery(id+"F11.opPattern","COPY",BODY,{"derivedFrom":makeQuery(id+"F10.opPattern","COPY",BODY,{"derivedFrom":makeQuery(id+"F1.opExtrude","SWEPT_BODY",BODY,{"disambiguationData":[OSD([sQuery(id+"F0.wireOp",EDGE,"E0")])]}),"instanceName":"1"}),"instanceName":"1"}),"instanceName":"1"}),"instanceName":"1"});
            var Q392;
            Q392=makeQuery(id+"F16.opPattern","COPY",BODY,{"derivedFrom":makeQuery(id+"F15.opPattern","COPY",BODY,{"derivedFrom":makeQuery(id+"F11.opPattern","COPY",BODY,{"derivedFrom":makeQuery(id+"F1.opExtrude","SWEPT_BODY",BODY,{"disambiguationData":[OSD([sQuery(id+"F0.wireOp",EDGE,"E0")])]}),"instanceName":"1"}),"instanceName":"1"}),"instanceName":"1"});
            var Q393;
            Q393=makeQuery(id+"F17.opPattern","COPY",BODY,{"derivedFrom":makeQuery(id+"F15.opPattern","COPY",BODY,{"derivedFrom":makeQuery(id+"F14.opPattern","COPY",BODY,{"derivedFrom":makeQuery(id+"F11.opPattern","COPY",BODY,{"derivedFrom":makeQuery(id+"F9.opPattern","COPY",BODY,{"derivedFrom":makeQuery(id+"F1.opExtrude","SWEPT_BODY",BODY,{"disambiguationData":[OSD([sQuery(id+"F0.wireOp",EDGE,"E0")])]}),"instanceName":"1"}),"instanceName":"1"}),"instanceName":"1"}),"instanceName":"1"}),"instanceName":"1"});
            var Q394;
            Q394=makeQuery(id+"F16.opPattern","COPY",BODY,{"derivedFrom":makeQuery(id+"F15.opPattern","COPY",BODY,{"derivedFrom":makeQuery(id+"F14.opPattern","COPY",BODY,{"derivedFrom":makeQuery(id+"F11.opPattern","COPY",BODY,{"derivedFrom":makeQuery(id+"F4.opPattern","COPY",BODY,{"derivedFrom":makeQuery(id+"F1.opExtrude","SWEPT_BODY",BODY,{"disambiguationData":[OSD([sQuery(id+"F0.wireOp",EDGE,"E0")])]}),"instanceName":"1"}),"instanceName":"1"}),"instanceName":"1"}),"instanceName":"1"}),"instanceName":"1"});
            var Q395;
            Q395=makeQuery(id+"F17.opPattern","COPY",BODY,{"derivedFrom":makeQuery(id+"F16.opPattern","COPY",BODY,{"derivedFrom":makeQuery(id+"F14.opPattern","COPY",BODY,{"derivedFrom":makeQuery(id+"F11.opPattern","COPY",BODY,{"derivedFrom":makeQuery(id+"F10.opPattern","COPY",BODY,{"derivedFrom":makeQuery(id+"F1.opExtrude","SWEPT_BODY",BODY,{"disambiguationData":[OSD([sQuery(id+"F0.wireOp",EDGE,"E0")])]}),"instanceName":"1"}),"instanceName":"1"}),"instanceName":"1"}),"instanceName":"1"}),"instanceName":"1"});
            var Q396;
            Q396=makeQuery(id+"F17.opPattern","COPY",BODY,{"derivedFrom":makeQuery(id+"F16.opPattern","COPY",BODY,{"derivedFrom":makeQuery(id+"F15.opPattern","COPY",BODY,{"derivedFrom":makeQuery(id+"F12.opPattern","COPY",BODY,{"derivedFrom":makeQuery(id+"F11.opPattern","COPY",BODY,{"derivedFrom":makeQuery(id+"F1.opExtrude","SWEPT_BODY",BODY,{"disambiguationData":[OSD([sQuery(id+"F0.wireOp",EDGE,"E0")])]}),"instanceName":"1"}),"instanceName":"1"}),"instanceName":"1"}),"instanceName":"1"}),"instanceName":"1"});
            var Q397;
            Q397=makeQuery(id+"F17.opPattern","COPY",BODY,{"derivedFrom":makeQuery(id+"F14.opPattern","COPY",BODY,{"derivedFrom":makeQuery(id+"F11.opPattern","COPY",BODY,{"derivedFrom":makeQuery(id+"F9.opPattern","COPY",BODY,{"derivedFrom":makeQuery(id+"F4.opPattern","COPY",BODY,{"derivedFrom":makeQuery(id+"F1.opExtrude","SWEPT_BODY",BODY,{"disambiguationData":[OSD([sQuery(id+"F0.wireOp",EDGE,"E0")])]}),"instanceName":"1"}),"instanceName":"1"}),"instanceName":"1"}),"instanceName":"1"}),"instanceName":"1"});
            var Q398;
            Q398=makeQuery(id+"F17.opPattern","COPY",BODY,{"derivedFrom":makeQuery(id+"F16.opPattern","COPY",BODY,{"derivedFrom":makeQuery(id+"F14.opPattern","COPY",BODY,{"derivedFrom":makeQuery(id+"F10.opPattern","COPY",BODY,{"derivedFrom":makeQuery(id+"F1.opExtrude","SWEPT_BODY",BODY,{"disambiguationData":[OSD([sQuery(id+"F0.wireOp",EDGE,"E0")])]}),"instanceName":"1"}),"instanceName":"1"}),"instanceName":"1"}),"instanceName":"1"});
            var Q399;
            Q399=makeQuery(id+"F17.opPattern","COPY",BODY,{"derivedFrom":makeQuery(id+"F16.opPattern","COPY",BODY,{"derivedFrom":makeQuery(id+"F15.opPattern","COPY",BODY,{"derivedFrom":makeQuery(id+"F12.opPattern","COPY",BODY,{"derivedFrom":makeQuery(id+"F1.opExtrude","SWEPT_BODY",BODY,{"disambiguationData":[OSD([sQuery(id+"F0.wireOp",EDGE,"E0")])]}),"instanceName":"1"}),"instanceName":"1"}),"instanceName":"1"}),"instanceName":"1"});
            var Q400;
            Q400=makeQuery(id+"F17.opPattern","COPY",BODY,{"derivedFrom":makeQuery(id+"F12.opPattern","COPY",BODY,{"derivedFrom":makeQuery(id+"F10.opPattern","COPY",BODY,{"derivedFrom":makeQuery(id+"F1.opExtrude","SWEPT_BODY",BODY,{"disambiguationData":[OSD([sQuery(id+"F0.wireOp",EDGE,"E0")])]}),"instanceName":"1"}),"instanceName":"1"}),"instanceName":"1"});
            var Q401;
            Q401=makeQuery(id+"F17.opPattern","COPY",BODY,{"derivedFrom":makeQuery(id+"F16.opPattern","COPY",BODY,{"derivedFrom":makeQuery(id+"F15.opPattern","COPY",BODY,{"derivedFrom":makeQuery(id+"F10.opPattern","COPY",BODY,{"derivedFrom":makeQuery(id+"F1.opExtrude","SWEPT_BODY",BODY,{"disambiguationData":[OSD([sQuery(id+"F0.wireOp",EDGE,"E0")])]}),"instanceName":"1"}),"instanceName":"1"}),"instanceName":"1"}),"instanceName":"1"});
            var Q402;
            Q402=makeQuery(id+"F17.opPattern","COPY",BODY,{"derivedFrom":makeQuery(id+"F15.opPattern","COPY",BODY,{"derivedFrom":makeQuery(id+"F9.opPattern","COPY",BODY,{"derivedFrom":makeQuery(id+"F1.opExtrude","SWEPT_BODY",BODY,{"disambiguationData":[OSD([sQuery(id+"F0.wireOp",EDGE,"E0")])]}),"instanceName":"1"}),"instanceName":"1"}),"instanceName":"1"});
            var Q403;
            Q403=makeQuery(id+"F17.opPattern","COPY",BODY,{"derivedFrom":makeQuery(id+"F15.opPattern","COPY",BODY,{"derivedFrom":makeQuery(id+"F14.opPattern","COPY",BODY,{"derivedFrom":makeQuery(id+"F4.opPattern","COPY",BODY,{"derivedFrom":makeQuery(id+"F1.opExtrude","SWEPT_BODY",BODY,{"disambiguationData":[OSD([sQuery(id+"F0.wireOp",EDGE,"E0")])]}),"instanceName":"1"}),"instanceName":"1"}),"instanceName":"1"}),"instanceName":"1"});
            var Q404;
            Q404=makeQuery(id+"F17.opPattern","COPY",BODY,{"derivedFrom":makeQuery(id+"F15.opPattern","COPY",BODY,{"derivedFrom":makeQuery(id+"F9.opPattern","COPY",BODY,{"derivedFrom":makeQuery(id+"F4.opPattern","COPY",BODY,{"derivedFrom":makeQuery(id+"F1.opExtrude","SWEPT_BODY",BODY,{"disambiguationData":[OSD([sQuery(id+"F0.wireOp",EDGE,"E0")])]}),"instanceName":"1"}),"instanceName":"1"}),"instanceName":"1"}),"instanceName":"1"});
            var Q405;
            Q405=makeQuery(id+"F17.opPattern","COPY",BODY,{"derivedFrom":makeQuery(id+"F16.opPattern","COPY",BODY,{"derivedFrom":makeQuery(id+"F15.opPattern","COPY",BODY,{"derivedFrom":makeQuery(id+"F12.opPattern","COPY",BODY,{"derivedFrom":makeQuery(id+"F11.opPattern","COPY",BODY,{"derivedFrom":makeQuery(id+"F9.opPattern","COPY",BODY,{"derivedFrom":makeQuery(id+"F4.opPattern","COPY",BODY,{"derivedFrom":makeQuery(id+"F1.opExtrude","SWEPT_BODY",BODY,{"disambiguationData":[OSD([sQuery(id+"F0.wireOp",EDGE,"E0")])]}),"instanceName":"1"}),"instanceName":"1"}),"instanceName":"1"}),"instanceName":"1"}),"instanceName":"1"}),"instanceName":"1"}),"instanceName":"1"});
            var Q406;
            Q406=makeQuery(id+"F17.opPattern","COPY",BODY,{"derivedFrom":makeQuery(id+"F16.opPattern","COPY",BODY,{"derivedFrom":makeQuery(id+"F15.opPattern","COPY",BODY,{"derivedFrom":makeQuery(id+"F12.opPattern","COPY",BODY,{"derivedFrom":makeQuery(id+"F4.opPattern","COPY",BODY,{"derivedFrom":makeQuery(id+"F1.opExtrude","SWEPT_BODY",BODY,{"disambiguationData":[OSD([sQuery(id+"F0.wireOp",EDGE,"E0")])]}),"instanceName":"1"}),"instanceName":"1"}),"instanceName":"1"}),"instanceName":"1"}),"instanceName":"1"});
            var Q407;
            Q407=makeQuery(id+"F17.opPattern","COPY",BODY,{"derivedFrom":makeQuery(id+"F15.opPattern","COPY",BODY,{"derivedFrom":makeQuery(id+"F14.opPattern","COPY",BODY,{"derivedFrom":makeQuery(id+"F11.opPattern","COPY",BODY,{"derivedFrom":makeQuery(id+"F1.opExtrude","SWEPT_BODY",BODY,{"disambiguationData":[OSD([sQuery(id+"F0.wireOp",EDGE,"E0")])]}),"instanceName":"1"}),"instanceName":"1"}),"instanceName":"1"}),"instanceName":"1"});
            var Q408;
            Q408=makeQuery(id+"F17.opPattern","COPY",BODY,{"derivedFrom":makeQuery(id+"F16.opPattern","COPY",BODY,{"derivedFrom":makeQuery(id+"F10.opPattern","COPY",BODY,{"derivedFrom":makeQuery(id+"F1.opExtrude","SWEPT_BODY",BODY,{"disambiguationData":[OSD([sQuery(id+"F0.wireOp",EDGE,"E0")])]}),"instanceName":"1"}),"instanceName":"1"}),"instanceName":"1"});
            var Q409;
            Q409=makeQuery(id+"F17.opPattern","COPY",BODY,{"derivedFrom":makeQuery(id+"F15.opPattern","COPY",BODY,{"derivedFrom":makeQuery(id+"F11.opPattern","COPY",BODY,{"derivedFrom":makeQuery(id+"F9.opPattern","COPY",BODY,{"derivedFrom":makeQuery(id+"F1.opExtrude","SWEPT_BODY",BODY,{"disambiguationData":[OSD([sQuery(id+"F0.wireOp",EDGE,"E0")])]}),"instanceName":"1"}),"instanceName":"1"}),"instanceName":"1"}),"instanceName":"1"});
            var Q410;
            Q410=makeQuery(id+"F17.opPattern","COPY",BODY,{"derivedFrom":makeQuery(id+"F12.opPattern","COPY",BODY,{"derivedFrom":makeQuery(id+"F11.opPattern","COPY",BODY,{"derivedFrom":makeQuery(id+"F9.opPattern","COPY",BODY,{"derivedFrom":makeQuery(id+"F1.opExtrude","SWEPT_BODY",BODY,{"disambiguationData":[OSD([sQuery(id+"F0.wireOp",EDGE,"E0")])]}),"instanceName":"1"}),"instanceName":"1"}),"instanceName":"1"}),"instanceName":"1"});
            var Q411;
            Q411=makeQuery(id+"F17.opPattern","COPY",BODY,{"derivedFrom":makeQuery(id+"F15.opPattern","COPY",BODY,{"derivedFrom":makeQuery(id+"F11.opPattern","COPY",BODY,{"derivedFrom":makeQuery(id+"F9.opPattern","COPY",BODY,{"derivedFrom":makeQuery(id+"F4.opPattern","COPY",BODY,{"derivedFrom":makeQuery(id+"F1.opExtrude","SWEPT_BODY",BODY,{"disambiguationData":[OSD([sQuery(id+"F0.wireOp",EDGE,"E0")])]}),"instanceName":"1"}),"instanceName":"1"}),"instanceName":"1"}),"instanceName":"1"}),"instanceName":"1"});
            var Q412;
            Q412=makeQuery(id+"F17.opPattern","COPY",BODY,{"derivedFrom":makeQuery(id+"F15.opPattern","COPY",BODY,{"derivedFrom":makeQuery(id+"F11.opPattern","COPY",BODY,{"derivedFrom":makeQuery(id+"F1.opExtrude","SWEPT_BODY",BODY,{"disambiguationData":[OSD([sQuery(id+"F0.wireOp",EDGE,"E0")])]}),"instanceName":"1"}),"instanceName":"1"}),"instanceName":"1"});
            var Q413;
            Q413=makeQuery(id+"F17.opPattern","COPY",BODY,{"derivedFrom":makeQuery(id+"F15.opPattern","COPY",BODY,{"derivedFrom":makeQuery(id+"F14.opPattern","COPY",BODY,{"derivedFrom":makeQuery(id+"F11.opPattern","COPY",BODY,{"derivedFrom":makeQuery(id+"F4.opPattern","COPY",BODY,{"derivedFrom":makeQuery(id+"F1.opExtrude","SWEPT_BODY",BODY,{"disambiguationData":[OSD([sQuery(id+"F0.wireOp",EDGE,"E0")])]}),"instanceName":"1"}),"instanceName":"1"}),"instanceName":"1"}),"instanceName":"1"}),"instanceName":"1"});
            var Q414;
            Q414=makeQuery(id+"F17.opPattern","COPY",BODY,{"derivedFrom":makeQuery(id+"F16.opPattern","COPY",BODY,{"derivedFrom":makeQuery(id+"F11.opPattern","COPY",BODY,{"derivedFrom":makeQuery(id+"F10.opPattern","COPY",BODY,{"derivedFrom":makeQuery(id+"F1.opExtrude","SWEPT_BODY",BODY,{"disambiguationData":[OSD([sQuery(id+"F0.wireOp",EDGE,"E0")])]}),"instanceName":"1"}),"instanceName":"1"}),"instanceName":"1"}),"instanceName":"1"});
            var Q415;
            Q415=makeQuery(id+"F17.opPattern","COPY",BODY,{"derivedFrom":makeQuery(id+"F16.opPattern","COPY",BODY,{"derivedFrom":makeQuery(id+"F14.opPattern","COPY",BODY,{"derivedFrom":makeQuery(id+"F11.opPattern","COPY",BODY,{"derivedFrom":makeQuery(id+"F9.opPattern","COPY",BODY,{"derivedFrom":makeQuery(id+"F1.opExtrude","SWEPT_BODY",BODY,{"disambiguationData":[OSD([sQuery(id+"F0.wireOp",EDGE,"E0")])]}),"instanceName":"1"}),"instanceName":"1"}),"instanceName":"1"}),"instanceName":"1"}),"instanceName":"1"});
            var Q416;
            Q416=makeQuery(id+"F17.opPattern","COPY",BODY,{"derivedFrom":makeQuery(id+"F16.opPattern","COPY",BODY,{"derivedFrom":makeQuery(id+"F15.opPattern","COPY",BODY,{"derivedFrom":makeQuery(id+"F12.opPattern","COPY",BODY,{"derivedFrom":makeQuery(id+"F11.opPattern","COPY",BODY,{"derivedFrom":makeQuery(id+"F4.opPattern","COPY",BODY,{"derivedFrom":makeQuery(id+"F1.opExtrude","SWEPT_BODY",BODY,{"disambiguationData":[OSD([sQuery(id+"F0.wireOp",EDGE,"E0")])]}),"instanceName":"1"}),"instanceName":"1"}),"instanceName":"1"}),"instanceName":"1"}),"instanceName":"1"}),"instanceName":"1"});
            var Q417;
            Q417=makeQuery(id+"F11.opPattern","COPY",BODY,{"derivedFrom":makeQuery(id+"F9.opPattern","COPY",BODY,{"derivedFrom":makeQuery(id+"F4.opPattern","COPY",BODY,{"derivedFrom":makeQuery(id+"F1.opExtrude","SWEPT_BODY",BODY,{"disambiguationData":[OSD([sQuery(id+"F0.wireOp",EDGE,"E0")])]}),"instanceName":"1"}),"instanceName":"1"}),"instanceName":"1"});
            var Q418;
            Q418=makeQuery(id+"F1.opExtrude","SWEPT_BODY",BODY,{"disambiguationData":[OSD([sQuery(id+"F0.wireOp",EDGE,"E0")])]});
            var Q419;
            Q419=makeQuery(id+"F4.opPattern","COPY",BODY,{"derivedFrom":makeQuery(id+"F1.opExtrude","SWEPT_BODY",BODY,{"disambiguationData":[OSD([sQuery(id+"F0.wireOp",EDGE,"E0")])]}),"instanceName":"1"});
            var Q420;
            {var subQ0=sQuery(id+"F0.wireOp",EDGE,"E0");Q420=makeQuery(id+"F6.opFillet","BLEND_EDGE",EDGE,{"blendedFrom":[makeQuery(id+"F4.opPattern","COPY",EDGE,{"derivedFrom":makeQuery(id+"F1.opExtrude","CAP_EDGE",EDGE,{"disambiguationData":[OSD([subQ0])],"isStart":false}),"instanceName":"1"}),makeQuery(id+"F4.opPattern","COPY",FACE,{"derivedFrom":makeQuery(id+"F1.opExtrude","CAP_FACE",FACE,{"disambiguationData":[OSD([subQ0])],"isStart":false}),"instanceName":"1"})],"blendedInto":[makeQuery(id+"F4.opPattern","COPY",FACE,{"derivedFrom":makeQuery(id+"F1.opExtrude","CAP_FACE",FACE,{"disambiguationData":[OSD([subQ0])],"isStart":false}),"instanceName":"1"})]});}
            transform(context, id + "F19", {"entities" : qUnion([Q0, Q1, Q2, Q3, Q4, Q5, Q6, Q7, Q8, Q9, Q10, Q11, Q12, Q13, Q14, Q15, Q16, Q17, Q18, Q19, Q20, Q21, Q22, Q23, Q24, Q25, Q26, Q27, Q28, Q29, Q30, Q31, Q32, Q33, Q34, Q35, Q36, Q37, Q38, Q39, Q40, Q41, Q42, Q43, Q44, Q45, Q46, Q47, Q48, Q49, Q50, Q51, Q52, Q53, Q54, Q55, Q56, Q57, Q58, Q59, Q60, Q61, Q62, Q63, Q64, Q65, Q66, Q67, Q68, Q69, Q70, Q71, Q72, Q73, Q74, Q75, Q76, Q77, Q78, Q79, Q80, Q81, Q82, Q83, Q84, Q85, Q86, Q87, Q88, Q89, Q90, Q91, Q92, Q93, Q94, Q95, Q96, Q97, Q98, Q99, Q100, Q101, Q102, Q103, Q104, Q105, Q106, Q107, Q108, Q109, Q110, Q111, Q112, Q113, Q114, Q115, Q116, Q117, Q118, Q119, Q120, Q121, Q122, Q123, Q124, Q125, Q126, Q127, Q128, Q129, Q130, Q131, Q132, Q133, Q134, Q135, Q136, Q137, Q138, Q139, Q140, Q141, Q142, Q143, Q144, Q145, Q146, Q147, Q148, Q149, Q150, Q151, Q152, Q153, Q154, Q155, Q156, Q157, Q158, Q159, Q160, Q161, Q162, Q163, Q164, Q165, Q166, Q167, Q168, Q169, Q170, Q171, Q172, Q173, Q174, Q175, Q176, Q177, Q178, Q179, Q180, Q181, Q182, Q183, Q184, Q185, Q186, Q187, Q188, Q189, Q190, Q191, Q192, Q193, Q194, Q195, Q196, Q197, Q198, Q199, Q200, Q201, Q202, Q203, Q204, Q205, Q206, Q207, Q208, Q209, Q210, Q211, Q212, Q213, Q214, Q215, Q216, Q217, Q218, Q219, Q220, Q221, Q222, Q223, Q224, Q225, Q226, Q227, Q228, Q229, Q230, Q231, Q232, Q233, Q234, Q235, Q236, Q237, Q238, Q239, Q240, Q241, Q242, Q243, Q244, Q245, Q246, Q247, Q248, Q249, Q250, Q251, Q252, Q253, Q254, Q255, Q256, Q257, Q258, Q259, Q260, Q261, Q262, Q263, Q264, Q265, Q266, Q267, Q268, Q269, Q270, Q271, Q272, Q273, Q274, Q275, Q276, Q277, Q278, Q279, Q280, Q281, Q282, Q283, Q284, Q285, Q286, Q287, Q288, Q289, Q290, Q291, Q292, Q293, Q294, Q295, Q296, Q297, Q298, Q299, Q300, Q301, Q302, Q303, Q304, Q305, Q306, Q307, Q308, Q309, Q310, Q311, Q312, Q313, Q314, Q315, Q316, Q317, Q318, Q319, Q320, Q321, Q322, Q323, Q324, Q325, Q326, Q327, Q328, Q329, Q330, Q331, Q332, Q333, Q334, Q335, Q336, Q337, Q338, Q339, Q340, Q341, Q342, Q343, Q344, Q345, Q346, Q347, Q348, Q349, Q350, Q351, Q352, Q353, Q354, Q355, Q356, Q357, Q358, Q359, Q360, Q361, Q362, Q363, Q364, Q365, Q366, Q367, Q368, Q369, Q370, Q371, Q372, Q373, Q374, Q375, Q376, Q377, Q378, Q379, Q380, Q381, Q382, Q383, Q384, Q385, Q386, Q387, Q388, Q389, Q390, Q391, Q392, Q393, Q394, Q395, Q396, Q397, Q398, Q399, Q400, Q401, Q402, Q403, Q404, Q405, Q406, Q407, Q408, Q409, Q410, Q411, Q412, Q413, Q414, Q415, Q416, Q417, Q418, Q419]), "transformType" : TransformType.ROTATION, "transformAxis" : qUnion([Q420]), "angle" : 90 * degree, "makeCopy" : false});
        }
        {
            var Q0;
            Q0=makeQuery(id+"F9.opPattern","COPY",BODY,{"derivedFrom":makeQuery(id+"F1.opExtrude","SWEPT_BODY",BODY,{"disambiguationData":[OSD([sQuery(id+"F0.wireOp",EDGE,"E0")])]}),"instanceName":"1"});
            var Q1;
            Q1=makeQuery(id+"F12.opPattern","COPY",BODY,{"derivedFrom":makeQuery(id+"F11.opPattern","COPY",BODY,{"derivedFrom":makeQuery(id+"F10.opPattern","COPY",BODY,{"derivedFrom":makeQuery(id+"F1.opExtrude","SWEPT_BODY",BODY,{"disambiguationData":[OSD([sQuery(id+"F0.wireOp",EDGE,"E0")])]}),"instanceName":"1"}),"instanceName":"1"}),"instanceName":"1"});
            var Q2;
            Q2=makeQuery(id+"F12.opPattern","COPY",BODY,{"derivedFrom":makeQuery(id+"F9.opPattern","COPY",BODY,{"derivedFrom":makeQuery(id+"F4.opPattern","COPY",BODY,{"derivedFrom":makeQuery(id+"F1.opExtrude","SWEPT_BODY",BODY,{"disambiguationData":[OSD([sQuery(id+"F0.wireOp",EDGE,"E0")])]}),"instanceName":"1"}),"instanceName":"1"}),"instanceName":"1"});
            var Q3;
            Q3=makeQuery(id+"F18.opPattern","COPY",BODY,{"derivedFrom":makeQuery(id+"F17.opPattern","COPY",BODY,{"derivedFrom":makeQuery(id+"F15.opPattern","COPY",BODY,{"derivedFrom":makeQuery(id+"F12.opPattern","COPY",BODY,{"derivedFrom":makeQuery(id+"F1.opExtrude","SWEPT_BODY",BODY,{"disambiguationData":[OSD([sQuery(id+"F0.wireOp",EDGE,"E0")])]}),"instanceName":"1"}),"instanceName":"1"}),"instanceName":"1"}),"instanceName":"1"});
            var Q4;
            Q4=makeQuery(id+"F12.opPattern","COPY",BODY,{"derivedFrom":makeQuery(id+"F11.opPattern","COPY",BODY,{"derivedFrom":makeQuery(id+"F9.opPattern","COPY",BODY,{"derivedFrom":makeQuery(id+"F4.opPattern","COPY",BODY,{"derivedFrom":makeQuery(id+"F1.opExtrude","SWEPT_BODY",BODY,{"disambiguationData":[OSD([sQuery(id+"F0.wireOp",EDGE,"E0")])]}),"instanceName":"1"}),"instanceName":"1"}),"instanceName":"1"}),"instanceName":"1"});
            var Q5;
            Q5=makeQuery(id+"F12.opPattern","COPY",BODY,{"derivedFrom":makeQuery(id+"F9.opPattern","COPY",BODY,{"derivedFrom":makeQuery(id+"F1.opExtrude","SWEPT_BODY",BODY,{"disambiguationData":[OSD([sQuery(id+"F0.wireOp",EDGE,"E0")])]}),"instanceName":"1"}),"instanceName":"1"});
            var Q6;
            Q6=makeQuery(id+"F12.opPattern","COPY",BODY,{"derivedFrom":makeQuery(id+"F11.opPattern","COPY",BODY,{"derivedFrom":makeQuery(id+"F4.opPattern","COPY",BODY,{"derivedFrom":makeQuery(id+"F1.opExtrude","SWEPT_BODY",BODY,{"disambiguationData":[OSD([sQuery(id+"F0.wireOp",EDGE,"E0")])]}),"instanceName":"1"}),"instanceName":"1"}),"instanceName":"1"});
            var Q7;
            Q7=makeQuery(id+"F11.opPattern","COPY",BODY,{"derivedFrom":makeQuery(id+"F9.opPattern","COPY",BODY,{"derivedFrom":makeQuery(id+"F4.opPattern","COPY",BODY,{"derivedFrom":makeQuery(id+"F1.opExtrude","SWEPT_BODY",BODY,{"disambiguationData":[OSD([sQuery(id+"F0.wireOp",EDGE,"E0")])]}),"instanceName":"1"}),"instanceName":"1"}),"instanceName":"1"});
            var Q8;
            Q8=makeQuery(id+"F12.opPattern","COPY",BODY,{"derivedFrom":makeQuery(id+"F10.opPattern","COPY",BODY,{"derivedFrom":makeQuery(id+"F1.opExtrude","SWEPT_BODY",BODY,{"disambiguationData":[OSD([sQuery(id+"F0.wireOp",EDGE,"E0")])]}),"instanceName":"1"}),"instanceName":"1"});
            var Q9;
            Q9=makeQuery(id+"F11.opPattern","COPY",BODY,{"derivedFrom":makeQuery(id+"F9.opPattern","COPY",BODY,{"derivedFrom":makeQuery(id+"F1.opExtrude","SWEPT_BODY",BODY,{"disambiguationData":[OSD([sQuery(id+"F0.wireOp",EDGE,"E0")])]}),"instanceName":"1"}),"instanceName":"1"});
            var Q10;
            Q10=makeQuery(id+"F18.opPattern","COPY",BODY,{"derivedFrom":makeQuery(id+"F17.opPattern","COPY",BODY,{"derivedFrom":makeQuery(id+"F16.opPattern","COPY",BODY,{"derivedFrom":makeQuery(id+"F14.opPattern","COPY",BODY,{"derivedFrom":makeQuery(id+"F11.opPattern","COPY",BODY,{"derivedFrom":makeQuery(id+"F9.opPattern","COPY",BODY,{"derivedFrom":makeQuery(id+"F4.opPattern","COPY",BODY,{"derivedFrom":makeQuery(id+"F1.opExtrude","SWEPT_BODY",BODY,{"disambiguationData":[OSD([sQuery(id+"F0.wireOp",EDGE,"E0")])]}),"instanceName":"1"}),"instanceName":"1"}),"instanceName":"1"}),"instanceName":"1"}),"instanceName":"1"}),"instanceName":"1"}),"instanceName":"1"});
            var Q11;
            Q11=makeQuery(id+"F11.opPattern","COPY",BODY,{"derivedFrom":makeQuery(id+"F10.opPattern","COPY",BODY,{"derivedFrom":makeQuery(id+"F1.opExtrude","SWEPT_BODY",BODY,{"disambiguationData":[OSD([sQuery(id+"F0.wireOp",EDGE,"E0")])]}),"instanceName":"1"}),"instanceName":"1"});
            var Q12;
            Q12=makeQuery(id+"F18.opPattern","COPY",BODY,{"derivedFrom":makeQuery(id+"F17.opPattern","COPY",BODY,{"derivedFrom":makeQuery(id+"F16.opPattern","COPY",BODY,{"derivedFrom":makeQuery(id+"F12.opPattern","COPY",BODY,{"derivedFrom":makeQuery(id+"F11.opPattern","COPY",BODY,{"derivedFrom":makeQuery(id+"F10.opPattern","COPY",BODY,{"derivedFrom":makeQuery(id+"F1.opExtrude","SWEPT_BODY",BODY,{"disambiguationData":[OSD([sQuery(id+"F0.wireOp",EDGE,"E0")])]}),"instanceName":"1"}),"instanceName":"1"}),"instanceName":"1"}),"instanceName":"1"}),"instanceName":"1"}),"instanceName":"1"});
            var Q13;
            Q13=makeQuery(id+"F18.opPattern","COPY",BODY,{"derivedFrom":makeQuery(id+"F17.opPattern","COPY",BODY,{"derivedFrom":makeQuery(id+"F16.opPattern","COPY",BODY,{"derivedFrom":makeQuery(id+"F14.opPattern","COPY",BODY,{"derivedFrom":makeQuery(id+"F11.opPattern","COPY",BODY,{"derivedFrom":makeQuery(id+"F10.opPattern","COPY",BODY,{"derivedFrom":makeQuery(id+"F1.opExtrude","SWEPT_BODY",BODY,{"disambiguationData":[OSD([sQuery(id+"F0.wireOp",EDGE,"E0")])]}),"instanceName":"1"}),"instanceName":"1"}),"instanceName":"1"}),"instanceName":"1"}),"instanceName":"1"}),"instanceName":"1"});
            var Q14;
            Q14=makeQuery(id+"F18.opPattern","COPY",BODY,{"derivedFrom":makeQuery(id+"F17.opPattern","COPY",BODY,{"derivedFrom":makeQuery(id+"F16.opPattern","COPY",BODY,{"derivedFrom":makeQuery(id+"F14.opPattern","COPY",BODY,{"derivedFrom":makeQuery(id+"F11.opPattern","COPY",BODY,{"derivedFrom":makeQuery(id+"F1.opExtrude","SWEPT_BODY",BODY,{"disambiguationData":[OSD([sQuery(id+"F0.wireOp",EDGE,"E0")])]}),"instanceName":"1"}),"instanceName":"1"}),"instanceName":"1"}),"instanceName":"1"}),"instanceName":"1"});
            var Q15;
            Q15=makeQuery(id+"F18.opPattern","COPY",BODY,{"derivedFrom":makeQuery(id+"F17.opPattern","COPY",BODY,{"derivedFrom":makeQuery(id+"F16.opPattern","COPY",BODY,{"derivedFrom":makeQuery(id+"F14.opPattern","COPY",BODY,{"derivedFrom":makeQuery(id+"F11.opPattern","COPY",BODY,{"derivedFrom":makeQuery(id+"F4.opPattern","COPY",BODY,{"derivedFrom":makeQuery(id+"F1.opExtrude","SWEPT_BODY",BODY,{"disambiguationData":[OSD([sQuery(id+"F0.wireOp",EDGE,"E0")])]}),"instanceName":"1"}),"instanceName":"1"}),"instanceName":"1"}),"instanceName":"1"}),"instanceName":"1"}),"instanceName":"1"});
            var Q16;
            Q16=makeQuery(id+"F18.opPattern","COPY",BODY,{"derivedFrom":makeQuery(id+"F17.opPattern","COPY",BODY,{"derivedFrom":makeQuery(id+"F16.opPattern","COPY",BODY,{"derivedFrom":makeQuery(id+"F12.opPattern","COPY",BODY,{"derivedFrom":makeQuery(id+"F4.opPattern","COPY",BODY,{"derivedFrom":makeQuery(id+"F1.opExtrude","SWEPT_BODY",BODY,{"disambiguationData":[OSD([sQuery(id+"F0.wireOp",EDGE,"E0")])]}),"instanceName":"1"}),"instanceName":"1"}),"instanceName":"1"}),"instanceName":"1"}),"instanceName":"1"});
            var Q17;
            Q17=makeQuery(id+"F18.opPattern","COPY",BODY,{"derivedFrom":makeQuery(id+"F17.opPattern","COPY",BODY,{"derivedFrom":makeQuery(id+"F16.opPattern","COPY",BODY,{"derivedFrom":makeQuery(id+"F12.opPattern","COPY",BODY,{"derivedFrom":makeQuery(id+"F9.opPattern","COPY",BODY,{"derivedFrom":makeQuery(id+"F4.opPattern","COPY",BODY,{"derivedFrom":makeQuery(id+"F1.opExtrude","SWEPT_BODY",BODY,{"disambiguationData":[OSD([sQuery(id+"F0.wireOp",EDGE,"E0")])]}),"instanceName":"1"}),"instanceName":"1"}),"instanceName":"1"}),"instanceName":"1"}),"instanceName":"1"}),"instanceName":"1"});
            var Q18;
            Q18=makeQuery(id+"F18.opPattern","COPY",BODY,{"derivedFrom":makeQuery(id+"F17.opPattern","COPY",BODY,{"derivedFrom":makeQuery(id+"F16.opPattern","COPY",BODY,{"derivedFrom":makeQuery(id+"F12.opPattern","COPY",BODY,{"derivedFrom":makeQuery(id+"F11.opPattern","COPY",BODY,{"derivedFrom":makeQuery(id+"F9.opPattern","COPY",BODY,{"derivedFrom":makeQuery(id+"F1.opExtrude","SWEPT_BODY",BODY,{"disambiguationData":[OSD([sQuery(id+"F0.wireOp",EDGE,"E0")])]}),"instanceName":"1"}),"instanceName":"1"}),"instanceName":"1"}),"instanceName":"1"}),"instanceName":"1"}),"instanceName":"1"});
            var Q19;
            Q19=makeQuery(id+"F18.opPattern","COPY",BODY,{"derivedFrom":makeQuery(id+"F17.opPattern","COPY",BODY,{"derivedFrom":makeQuery(id+"F16.opPattern","COPY",BODY,{"derivedFrom":makeQuery(id+"F11.opPattern","COPY",BODY,{"derivedFrom":makeQuery(id+"F1.opExtrude","SWEPT_BODY",BODY,{"disambiguationData":[OSD([sQuery(id+"F0.wireOp",EDGE,"E0")])]}),"instanceName":"1"}),"instanceName":"1"}),"instanceName":"1"}),"instanceName":"1"});
            var Q20;
            Q20=makeQuery(id+"F18.opPattern","COPY",BODY,{"derivedFrom":makeQuery(id+"F17.opPattern","COPY",BODY,{"derivedFrom":makeQuery(id+"F16.opPattern","COPY",BODY,{"derivedFrom":makeQuery(id+"F12.opPattern","COPY",BODY,{"derivedFrom":makeQuery(id+"F11.opPattern","COPY",BODY,{"derivedFrom":makeQuery(id+"F1.opExtrude","SWEPT_BODY",BODY,{"disambiguationData":[OSD([sQuery(id+"F0.wireOp",EDGE,"E0")])]}),"instanceName":"1"}),"instanceName":"1"}),"instanceName":"1"}),"instanceName":"1"}),"instanceName":"1"});
            var Q21;
            Q21=makeQuery(id+"F18.opPattern","COPY",BODY,{"derivedFrom":makeQuery(id+"F17.opPattern","COPY",BODY,{"derivedFrom":makeQuery(id+"F16.opPattern","COPY",BODY,{"derivedFrom":makeQuery(id+"F11.opPattern","COPY",BODY,{"derivedFrom":makeQuery(id+"F9.opPattern","COPY",BODY,{"derivedFrom":makeQuery(id+"F1.opExtrude","SWEPT_BODY",BODY,{"disambiguationData":[OSD([sQuery(id+"F0.wireOp",EDGE,"E0")])]}),"instanceName":"1"}),"instanceName":"1"}),"instanceName":"1"}),"instanceName":"1"}),"instanceName":"1"});
            var Q22;
            Q22=makeQuery(id+"F18.opPattern","COPY",BODY,{"derivedFrom":makeQuery(id+"F17.opPattern","COPY",BODY,{"derivedFrom":makeQuery(id+"F16.opPattern","COPY",BODY,{"derivedFrom":makeQuery(id+"F10.opPattern","COPY",BODY,{"derivedFrom":makeQuery(id+"F1.opExtrude","SWEPT_BODY",BODY,{"disambiguationData":[OSD([sQuery(id+"F0.wireOp",EDGE,"E0")])]}),"instanceName":"1"}),"instanceName":"1"}),"instanceName":"1"}),"instanceName":"1"});
            var Q23;
            Q23=makeQuery(id+"F18.opPattern","COPY",BODY,{"derivedFrom":makeQuery(id+"F17.opPattern","COPY",BODY,{"derivedFrom":makeQuery(id+"F16.opPattern","COPY",BODY,{"derivedFrom":makeQuery(id+"F14.opPattern","COPY",BODY,{"derivedFrom":makeQuery(id+"F1.opExtrude","SWEPT_BODY",BODY,{"disambiguationData":[OSD([sQuery(id+"F0.wireOp",EDGE,"E0")])]}),"instanceName":"1"}),"instanceName":"1"}),"instanceName":"1"}),"instanceName":"1"});
            var Q24;
            Q24=makeQuery(id+"F18.opPattern","COPY",BODY,{"derivedFrom":makeQuery(id+"F17.opPattern","COPY",BODY,{"derivedFrom":makeQuery(id+"F16.opPattern","COPY",BODY,{"derivedFrom":makeQuery(id+"F12.opPattern","COPY",BODY,{"derivedFrom":makeQuery(id+"F1.opExtrude","SWEPT_BODY",BODY,{"disambiguationData":[OSD([sQuery(id+"F0.wireOp",EDGE,"E0")])]}),"instanceName":"1"}),"instanceName":"1"}),"instanceName":"1"}),"instanceName":"1"});
            var Q25;
            Q25=makeQuery(id+"F18.opPattern","COPY",BODY,{"derivedFrom":makeQuery(id+"F17.opPattern","COPY",BODY,{"derivedFrom":makeQuery(id+"F16.opPattern","COPY",BODY,{"derivedFrom":makeQuery(id+"F11.opPattern","COPY",BODY,{"derivedFrom":makeQuery(id+"F9.opPattern","COPY",BODY,{"derivedFrom":makeQuery(id+"F4.opPattern","COPY",BODY,{"derivedFrom":makeQuery(id+"F1.opExtrude","SWEPT_BODY",BODY,{"disambiguationData":[OSD([sQuery(id+"F0.wireOp",EDGE,"E0")])]}),"instanceName":"1"}),"instanceName":"1"}),"instanceName":"1"}),"instanceName":"1"}),"instanceName":"1"}),"instanceName":"1"});
            var Q26;
            Q26=makeQuery(id+"F18.opPattern","COPY",BODY,{"derivedFrom":makeQuery(id+"F17.opPattern","COPY",BODY,{"derivedFrom":makeQuery(id+"F16.opPattern","COPY",BODY,{"derivedFrom":makeQuery(id+"F11.opPattern","COPY",BODY,{"derivedFrom":makeQuery(id+"F4.opPattern","COPY",BODY,{"derivedFrom":makeQuery(id+"F1.opExtrude","SWEPT_BODY",BODY,{"disambiguationData":[OSD([sQuery(id+"F0.wireOp",EDGE,"E0")])]}),"instanceName":"1"}),"instanceName":"1"}),"instanceName":"1"}),"instanceName":"1"}),"instanceName":"1"});
            var Q27;
            Q27=makeQuery(id+"F18.opPattern","COPY",BODY,{"derivedFrom":makeQuery(id+"F17.opPattern","COPY",BODY,{"derivedFrom":makeQuery(id+"F16.opPattern","COPY",BODY,{"derivedFrom":makeQuery(id+"F12.opPattern","COPY",BODY,{"derivedFrom":makeQuery(id+"F9.opPattern","COPY",BODY,{"derivedFrom":makeQuery(id+"F1.opExtrude","SWEPT_BODY",BODY,{"disambiguationData":[OSD([sQuery(id+"F0.wireOp",EDGE,"E0")])]}),"instanceName":"1"}),"instanceName":"1"}),"instanceName":"1"}),"instanceName":"1"}),"instanceName":"1"});
            var Q28;
            Q28=makeQuery(id+"F17.opPattern","COPY",BODY,{"derivedFrom":makeQuery(id+"F16.opPattern","COPY",BODY,{"derivedFrom":makeQuery(id+"F15.opPattern","COPY",BODY,{"derivedFrom":makeQuery(id+"F14.opPattern","COPY",BODY,{"derivedFrom":makeQuery(id+"F11.opPattern","COPY",BODY,{"derivedFrom":makeQuery(id+"F9.opPattern","COPY",BODY,{"derivedFrom":makeQuery(id+"F1.opExtrude","SWEPT_BODY",BODY,{"disambiguationData":[OSD([sQuery(id+"F0.wireOp",EDGE,"E0")])]}),"instanceName":"1"}),"instanceName":"1"}),"instanceName":"1"}),"instanceName":"1"}),"instanceName":"1"}),"instanceName":"1"});
            var Q29;
            Q29=makeQuery(id+"F17.opPattern","COPY",BODY,{"derivedFrom":makeQuery(id+"F16.opPattern","COPY",BODY,{"derivedFrom":makeQuery(id+"F15.opPattern","COPY",BODY,{"derivedFrom":makeQuery(id+"F14.opPattern","COPY",BODY,{"derivedFrom":makeQuery(id+"F11.opPattern","COPY",BODY,{"derivedFrom":makeQuery(id+"F10.opPattern","COPY",BODY,{"derivedFrom":makeQuery(id+"F1.opExtrude","SWEPT_BODY",BODY,{"disambiguationData":[OSD([sQuery(id+"F0.wireOp",EDGE,"E0")])]}),"instanceName":"1"}),"instanceName":"1"}),"instanceName":"1"}),"instanceName":"1"}),"instanceName":"1"}),"instanceName":"1"});
            var Q30;
            Q30=makeQuery(id+"F17.opPattern","COPY",BODY,{"derivedFrom":makeQuery(id+"F16.opPattern","COPY",BODY,{"derivedFrom":makeQuery(id+"F15.opPattern","COPY",BODY,{"derivedFrom":makeQuery(id+"F12.opPattern","COPY",BODY,{"derivedFrom":makeQuery(id+"F11.opPattern","COPY",BODY,{"derivedFrom":makeQuery(id+"F4.opPattern","COPY",BODY,{"derivedFrom":makeQuery(id+"F1.opExtrude","SWEPT_BODY",BODY,{"disambiguationData":[OSD([sQuery(id+"F0.wireOp",EDGE,"E0")])]}),"instanceName":"1"}),"instanceName":"1"}),"instanceName":"1"}),"instanceName":"1"}),"instanceName":"1"}),"instanceName":"1"});
            var Q31;
            Q31=makeQuery(id+"F18.opPattern","COPY",BODY,{"derivedFrom":makeQuery(id+"F17.opPattern","COPY",BODY,{"derivedFrom":makeQuery(id+"F15.opPattern","COPY",BODY,{"derivedFrom":makeQuery(id+"F14.opPattern","COPY",BODY,{"derivedFrom":makeQuery(id+"F11.opPattern","COPY",BODY,{"derivedFrom":makeQuery(id+"F1.opExtrude","SWEPT_BODY",BODY,{"disambiguationData":[OSD([sQuery(id+"F0.wireOp",EDGE,"E0")])]}),"instanceName":"1"}),"instanceName":"1"}),"instanceName":"1"}),"instanceName":"1"}),"instanceName":"1"});
            var Q32;
            Q32=makeQuery(id+"F17.opPattern","COPY",BODY,{"derivedFrom":makeQuery(id+"F16.opPattern","COPY",BODY,{"derivedFrom":makeQuery(id+"F15.opPattern","COPY",BODY,{"derivedFrom":makeQuery(id+"F14.opPattern","COPY",BODY,{"derivedFrom":makeQuery(id+"F1.opExtrude","SWEPT_BODY",BODY,{"disambiguationData":[OSD([sQuery(id+"F0.wireOp",EDGE,"E0")])]}),"instanceName":"1"}),"instanceName":"1"}),"instanceName":"1"}),"instanceName":"1"});
            var Q33;
            Q33=makeQuery(id+"F17.opPattern","COPY",BODY,{"derivedFrom":makeQuery(id+"F16.opPattern","COPY",BODY,{"derivedFrom":makeQuery(id+"F15.opPattern","COPY",BODY,{"derivedFrom":makeQuery(id+"F11.opPattern","COPY",BODY,{"derivedFrom":makeQuery(id+"F10.opPattern","COPY",BODY,{"derivedFrom":makeQuery(id+"F1.opExtrude","SWEPT_BODY",BODY,{"disambiguationData":[OSD([sQuery(id+"F0.wireOp",EDGE,"E0")])]}),"instanceName":"1"}),"instanceName":"1"}),"instanceName":"1"}),"instanceName":"1"}),"instanceName":"1"});
            var Q34;
            Q34=makeQuery(id+"F17.opPattern","COPY",BODY,{"derivedFrom":makeQuery(id+"F16.opPattern","COPY",BODY,{"derivedFrom":makeQuery(id+"F14.opPattern","COPY",BODY,{"derivedFrom":makeQuery(id+"F11.opPattern","COPY",BODY,{"derivedFrom":makeQuery(id+"F9.opPattern","COPY",BODY,{"derivedFrom":makeQuery(id+"F1.opExtrude","SWEPT_BODY",BODY,{"disambiguationData":[OSD([sQuery(id+"F0.wireOp",EDGE,"E0")])]}),"instanceName":"1"}),"instanceName":"1"}),"instanceName":"1"}),"instanceName":"1"}),"instanceName":"1"});
            var Q35;
            Q35=makeQuery(id+"F18.opPattern","COPY",BODY,{"derivedFrom":makeQuery(id+"F17.opPattern","COPY",BODY,{"derivedFrom":makeQuery(id+"F15.opPattern","COPY",BODY,{"derivedFrom":makeQuery(id+"F14.opPattern","COPY",BODY,{"derivedFrom":makeQuery(id+"F10.opPattern","COPY",BODY,{"derivedFrom":makeQuery(id+"F1.opExtrude","SWEPT_BODY",BODY,{"disambiguationData":[OSD([sQuery(id+"F0.wireOp",EDGE,"E0")])]}),"instanceName":"1"}),"instanceName":"1"}),"instanceName":"1"}),"instanceName":"1"}),"instanceName":"1"});
            var Q36;
            Q36=makeQuery(id+"F17.opPattern","COPY",BODY,{"derivedFrom":makeQuery(id+"F16.opPattern","COPY",BODY,{"derivedFrom":makeQuery(id+"F14.opPattern","COPY",BODY,{"derivedFrom":makeQuery(id+"F11.opPattern","COPY",BODY,{"derivedFrom":makeQuery(id+"F9.opPattern","COPY",BODY,{"derivedFrom":makeQuery(id+"F4.opPattern","COPY",BODY,{"derivedFrom":makeQuery(id+"F1.opExtrude","SWEPT_BODY",BODY,{"disambiguationData":[OSD([sQuery(id+"F0.wireOp",EDGE,"E0")])]}),"instanceName":"1"}),"instanceName":"1"}),"instanceName":"1"}),"instanceName":"1"}),"instanceName":"1"}),"instanceName":"1"});
            var Q37;
            Q37=makeQuery(id+"F17.opPattern","COPY",BODY,{"derivedFrom":makeQuery(id+"F12.opPattern","COPY",BODY,{"derivedFrom":makeQuery(id+"F11.opPattern","COPY",BODY,{"derivedFrom":makeQuery(id+"F4.opPattern","COPY",BODY,{"derivedFrom":makeQuery(id+"F1.opExtrude","SWEPT_BODY",BODY,{"disambiguationData":[OSD([sQuery(id+"F0.wireOp",EDGE,"E0")])]}),"instanceName":"1"}),"instanceName":"1"}),"instanceName":"1"}),"instanceName":"1"});
            var Q38;
            Q38=makeQuery(id+"F17.opPattern","COPY",BODY,{"derivedFrom":makeQuery(id+"F16.opPattern","COPY",BODY,{"derivedFrom":makeQuery(id+"F15.opPattern","COPY",BODY,{"derivedFrom":makeQuery(id+"F1.opExtrude","SWEPT_BODY",BODY,{"disambiguationData":[OSD([sQuery(id+"F0.wireOp",EDGE,"E0")])]}),"instanceName":"1"}),"instanceName":"1"}),"instanceName":"1"});
            var Q39;
            Q39=makeQuery(id+"F17.opPattern","COPY",BODY,{"derivedFrom":makeQuery(id+"F12.opPattern","COPY",BODY,{"derivedFrom":makeQuery(id+"F11.opPattern","COPY",BODY,{"derivedFrom":makeQuery(id+"F9.opPattern","COPY",BODY,{"derivedFrom":makeQuery(id+"F1.opExtrude","SWEPT_BODY",BODY,{"disambiguationData":[OSD([sQuery(id+"F0.wireOp",EDGE,"E0")])]}),"instanceName":"1"}),"instanceName":"1"}),"instanceName":"1"}),"instanceName":"1"});
            var Q40;
            Q40=makeQuery(id+"F17.opPattern","COPY",BODY,{"derivedFrom":makeQuery(id+"F16.opPattern","COPY",BODY,{"derivedFrom":makeQuery(id+"F14.opPattern","COPY",BODY,{"derivedFrom":makeQuery(id+"F1.opExtrude","SWEPT_BODY",BODY,{"disambiguationData":[OSD([sQuery(id+"F0.wireOp",EDGE,"E0")])]}),"instanceName":"1"}),"instanceName":"1"}),"instanceName":"1"});
            var Q41;
            Q41=makeQuery(id+"F17.opPattern","COPY",BODY,{"derivedFrom":makeQuery(id+"F16.opPattern","COPY",BODY,{"derivedFrom":makeQuery(id+"F14.opPattern","COPY",BODY,{"derivedFrom":makeQuery(id+"F11.opPattern","COPY",BODY,{"derivedFrom":makeQuery(id+"F4.opPattern","COPY",BODY,{"derivedFrom":makeQuery(id+"F1.opExtrude","SWEPT_BODY",BODY,{"disambiguationData":[OSD([sQuery(id+"F0.wireOp",EDGE,"E0")])]}),"instanceName":"1"}),"instanceName":"1"}),"instanceName":"1"}),"instanceName":"1"}),"instanceName":"1"});
            var Q42;
            Q42=makeQuery(id+"F17.opPattern","COPY",BODY,{"derivedFrom":makeQuery(id+"F12.opPattern","COPY",BODY,{"derivedFrom":makeQuery(id+"F4.opPattern","COPY",BODY,{"derivedFrom":makeQuery(id+"F1.opExtrude","SWEPT_BODY",BODY,{"disambiguationData":[OSD([sQuery(id+"F0.wireOp",EDGE,"E0")])]}),"instanceName":"1"}),"instanceName":"1"}),"instanceName":"1"});
            var Q43;
            Q43=makeQuery(id+"F18.opPattern","COPY",BODY,{"derivedFrom":makeQuery(id+"F17.opPattern","COPY",BODY,{"derivedFrom":makeQuery(id+"F16.opPattern","COPY",BODY,{"derivedFrom":makeQuery(id+"F4.opPattern","COPY",BODY,{"derivedFrom":makeQuery(id+"F1.opExtrude","SWEPT_BODY",BODY,{"disambiguationData":[OSD([sQuery(id+"F0.wireOp",EDGE,"E0")])]}),"instanceName":"1"}),"instanceName":"1"}),"instanceName":"1"}),"instanceName":"1"});
            var Q44;
            Q44=makeQuery(id+"F17.opPattern","COPY",BODY,{"derivedFrom":makeQuery(id+"F16.opPattern","COPY",BODY,{"derivedFrom":makeQuery(id+"F12.opPattern","COPY",BODY,{"derivedFrom":makeQuery(id+"F1.opExtrude","SWEPT_BODY",BODY,{"disambiguationData":[OSD([sQuery(id+"F0.wireOp",EDGE,"E0")])]}),"instanceName":"1"}),"instanceName":"1"}),"instanceName":"1"});
            var Q45;
            Q45=makeQuery(id+"F17.opPattern","COPY",BODY,{"derivedFrom":makeQuery(id+"F16.opPattern","COPY",BODY,{"derivedFrom":makeQuery(id+"F12.opPattern","COPY",BODY,{"derivedFrom":makeQuery(id+"F9.opPattern","COPY",BODY,{"derivedFrom":makeQuery(id+"F1.opExtrude","SWEPT_BODY",BODY,{"disambiguationData":[OSD([sQuery(id+"F0.wireOp",EDGE,"E0")])]}),"instanceName":"1"}),"instanceName":"1"}),"instanceName":"1"}),"instanceName":"1"});
            var Q46;
            Q46=makeQuery(id+"F17.opPattern","COPY",BODY,{"derivedFrom":makeQuery(id+"F15.opPattern","COPY",BODY,{"derivedFrom":makeQuery(id+"F14.opPattern","COPY",BODY,{"derivedFrom":makeQuery(id+"F11.opPattern","COPY",BODY,{"derivedFrom":makeQuery(id+"F10.opPattern","COPY",BODY,{"derivedFrom":makeQuery(id+"F1.opExtrude","SWEPT_BODY",BODY,{"disambiguationData":[OSD([sQuery(id+"F0.wireOp",EDGE,"E0")])]}),"instanceName":"1"}),"instanceName":"1"}),"instanceName":"1"}),"instanceName":"1"}),"instanceName":"1"});
            var Q47;
            Q47=makeQuery(id+"F17.opPattern","COPY",BODY,{"derivedFrom":makeQuery(id+"F16.opPattern","COPY",BODY,{"derivedFrom":makeQuery(id+"F11.opPattern","COPY",BODY,{"derivedFrom":makeQuery(id+"F9.opPattern","COPY",BODY,{"derivedFrom":makeQuery(id+"F4.opPattern","COPY",BODY,{"derivedFrom":makeQuery(id+"F1.opExtrude","SWEPT_BODY",BODY,{"disambiguationData":[OSD([sQuery(id+"F0.wireOp",EDGE,"E0")])]}),"instanceName":"1"}),"instanceName":"1"}),"instanceName":"1"}),"instanceName":"1"}),"instanceName":"1"});
            var Q48;
            Q48=makeQuery(id+"F17.opPattern","COPY",BODY,{"derivedFrom":makeQuery(id+"F15.opPattern","COPY",BODY,{"derivedFrom":makeQuery(id+"F1.opExtrude","SWEPT_BODY",BODY,{"disambiguationData":[OSD([sQuery(id+"F0.wireOp",EDGE,"E0")])]}),"instanceName":"1"}),"instanceName":"1"});
            var Q49;
            Q49=makeQuery(id+"F17.opPattern","COPY",BODY,{"derivedFrom":makeQuery(id+"F14.opPattern","COPY",BODY,{"derivedFrom":makeQuery(id+"F11.opPattern","COPY",BODY,{"derivedFrom":makeQuery(id+"F9.opPattern","COPY",BODY,{"derivedFrom":makeQuery(id+"F4.opPattern","COPY",BODY,{"derivedFrom":makeQuery(id+"F1.opExtrude","SWEPT_BODY",BODY,{"disambiguationData":[OSD([sQuery(id+"F0.wireOp",EDGE,"E0")])]}),"instanceName":"1"}),"instanceName":"1"}),"instanceName":"1"}),"instanceName":"1"}),"instanceName":"1"});
            var Q50;
            Q50=makeQuery(id+"F17.opPattern","COPY",BODY,{"derivedFrom":makeQuery(id+"F16.opPattern","COPY",BODY,{"derivedFrom":makeQuery(id+"F12.opPattern","COPY",BODY,{"derivedFrom":makeQuery(id+"F10.opPattern","COPY",BODY,{"derivedFrom":makeQuery(id+"F1.opExtrude","SWEPT_BODY",BODY,{"disambiguationData":[OSD([sQuery(id+"F0.wireOp",EDGE,"E0")])]}),"instanceName":"1"}),"instanceName":"1"}),"instanceName":"1"}),"instanceName":"1"});
            var Q51;
            Q51=makeQuery(id+"F17.opPattern","COPY",BODY,{"derivedFrom":makeQuery(id+"F16.opPattern","COPY",BODY,{"derivedFrom":makeQuery(id+"F11.opPattern","COPY",BODY,{"derivedFrom":makeQuery(id+"F1.opExtrude","SWEPT_BODY",BODY,{"disambiguationData":[OSD([sQuery(id+"F0.wireOp",EDGE,"E0")])]}),"instanceName":"1"}),"instanceName":"1"}),"instanceName":"1"});
            var Q52;
            Q52=makeQuery(id+"F17.opPattern","COPY",BODY,{"derivedFrom":makeQuery(id+"F16.opPattern","COPY",BODY,{"derivedFrom":makeQuery(id+"F9.opPattern","COPY",BODY,{"derivedFrom":makeQuery(id+"F4.opPattern","COPY",BODY,{"derivedFrom":makeQuery(id+"F1.opExtrude","SWEPT_BODY",BODY,{"disambiguationData":[OSD([sQuery(id+"F0.wireOp",EDGE,"E0")])]}),"instanceName":"1"}),"instanceName":"1"}),"instanceName":"1"}),"instanceName":"1"});
            var Q53;
            Q53=makeQuery(id+"F17.opPattern","COPY",BODY,{"derivedFrom":makeQuery(id+"F15.opPattern","COPY",BODY,{"derivedFrom":makeQuery(id+"F14.opPattern","COPY",BODY,{"derivedFrom":makeQuery(id+"F11.opPattern","COPY",BODY,{"derivedFrom":makeQuery(id+"F4.opPattern","COPY",BODY,{"derivedFrom":makeQuery(id+"F1.opExtrude","SWEPT_BODY",BODY,{"disambiguationData":[OSD([sQuery(id+"F0.wireOp",EDGE,"E0")])]}),"instanceName":"1"}),"instanceName":"1"}),"instanceName":"1"}),"instanceName":"1"}),"instanceName":"1"});
            var Q54;
            Q54=makeQuery(id+"F17.opPattern","COPY",BODY,{"derivedFrom":makeQuery(id+"F16.opPattern","COPY",BODY,{"derivedFrom":makeQuery(id+"F1.opExtrude","SWEPT_BODY",BODY,{"disambiguationData":[OSD([sQuery(id+"F0.wireOp",EDGE,"E0")])]}),"instanceName":"1"}),"instanceName":"1"});
            var Q55;
            Q55=makeQuery(id+"F17.opPattern","COPY",BODY,{"derivedFrom":makeQuery(id+"F15.opPattern","COPY",BODY,{"derivedFrom":makeQuery(id+"F12.opPattern","COPY",BODY,{"derivedFrom":makeQuery(id+"F9.opPattern","COPY",BODY,{"derivedFrom":makeQuery(id+"F1.opExtrude","SWEPT_BODY",BODY,{"disambiguationData":[OSD([sQuery(id+"F0.wireOp",EDGE,"E0")])]}),"instanceName":"1"}),"instanceName":"1"}),"instanceName":"1"}),"instanceName":"1"});
            var Q56;
            Q56=makeQuery(id+"F17.opPattern","COPY",BODY,{"derivedFrom":makeQuery(id+"F15.opPattern","COPY",BODY,{"derivedFrom":makeQuery(id+"F12.opPattern","COPY",BODY,{"derivedFrom":makeQuery(id+"F11.opPattern","COPY",BODY,{"derivedFrom":makeQuery(id+"F9.opPattern","COPY",BODY,{"derivedFrom":makeQuery(id+"F1.opExtrude","SWEPT_BODY",BODY,{"disambiguationData":[OSD([sQuery(id+"F0.wireOp",EDGE,"E0")])]}),"instanceName":"1"}),"instanceName":"1"}),"instanceName":"1"}),"instanceName":"1"}),"instanceName":"1"});
            var Q57;
            Q57=makeQuery(id+"F17.opPattern","COPY",BODY,{"derivedFrom":makeQuery(id+"F15.opPattern","COPY",BODY,{"derivedFrom":makeQuery(id+"F12.opPattern","COPY",BODY,{"derivedFrom":makeQuery(id+"F11.opPattern","COPY",BODY,{"derivedFrom":makeQuery(id+"F10.opPattern","COPY",BODY,{"derivedFrom":makeQuery(id+"F1.opExtrude","SWEPT_BODY",BODY,{"disambiguationData":[OSD([sQuery(id+"F0.wireOp",EDGE,"E0")])]}),"instanceName":"1"}),"instanceName":"1"}),"instanceName":"1"}),"instanceName":"1"}),"instanceName":"1"});
            var Q58;
            Q58=makeQuery(id+"F17.opPattern","COPY",BODY,{"derivedFrom":makeQuery(id+"F15.opPattern","COPY",BODY,{"derivedFrom":makeQuery(id+"F11.opPattern","COPY",BODY,{"derivedFrom":makeQuery(id+"F1.opExtrude","SWEPT_BODY",BODY,{"disambiguationData":[OSD([sQuery(id+"F0.wireOp",EDGE,"E0")])]}),"instanceName":"1"}),"instanceName":"1"}),"instanceName":"1"});
            var Q59;
            Q59=makeQuery(id+"F17.opPattern","COPY",BODY,{"derivedFrom":makeQuery(id+"F15.opPattern","COPY",BODY,{"derivedFrom":makeQuery(id+"F11.opPattern","COPY",BODY,{"derivedFrom":makeQuery(id+"F9.opPattern","COPY",BODY,{"derivedFrom":makeQuery(id+"F4.opPattern","COPY",BODY,{"derivedFrom":makeQuery(id+"F1.opExtrude","SWEPT_BODY",BODY,{"disambiguationData":[OSD([sQuery(id+"F0.wireOp",EDGE,"E0")])]}),"instanceName":"1"}),"instanceName":"1"}),"instanceName":"1"}),"instanceName":"1"}),"instanceName":"1"});
            var Q60;
            Q60=makeQuery(id+"F17.opPattern","COPY",BODY,{"derivedFrom":makeQuery(id+"F14.opPattern","COPY",BODY,{"derivedFrom":makeQuery(id+"F10.opPattern","COPY",BODY,{"derivedFrom":makeQuery(id+"F1.opExtrude","SWEPT_BODY",BODY,{"disambiguationData":[OSD([sQuery(id+"F0.wireOp",EDGE,"E0")])]}),"instanceName":"1"}),"instanceName":"1"}),"instanceName":"1"});
            var Q61;
            Q61=makeQuery(id+"F17.opPattern","COPY",BODY,{"derivedFrom":makeQuery(id+"F16.opPattern","COPY",BODY,{"derivedFrom":makeQuery(id+"F15.opPattern","COPY",BODY,{"derivedFrom":makeQuery(id+"F14.opPattern","COPY",BODY,{"derivedFrom":makeQuery(id+"F4.opPattern","COPY",BODY,{"derivedFrom":makeQuery(id+"F1.opExtrude","SWEPT_BODY",BODY,{"disambiguationData":[OSD([sQuery(id+"F0.wireOp",EDGE,"E0")])]}),"instanceName":"1"}),"instanceName":"1"}),"instanceName":"1"}),"instanceName":"1"}),"instanceName":"1"});
            var Q62;
            Q62=makeQuery(id+"F17.opPattern","COPY",BODY,{"derivedFrom":makeQuery(id+"F16.opPattern","COPY",BODY,{"derivedFrom":makeQuery(id+"F14.opPattern","COPY",BODY,{"derivedFrom":makeQuery(id+"F11.opPattern","COPY",BODY,{"derivedFrom":makeQuery(id+"F10.opPattern","COPY",BODY,{"derivedFrom":makeQuery(id+"F1.opExtrude","SWEPT_BODY",BODY,{"disambiguationData":[OSD([sQuery(id+"F0.wireOp",EDGE,"E0")])]}),"instanceName":"1"}),"instanceName":"1"}),"instanceName":"1"}),"instanceName":"1"}),"instanceName":"1"});
            var Q63;
            Q63=makeQuery(id+"F17.opPattern","COPY",BODY,{"derivedFrom":makeQuery(id+"F16.opPattern","COPY",BODY,{"derivedFrom":makeQuery(id+"F15.opPattern","COPY",BODY,{"derivedFrom":makeQuery(id+"F9.opPattern","COPY",BODY,{"derivedFrom":makeQuery(id+"F1.opExtrude","SWEPT_BODY",BODY,{"disambiguationData":[OSD([sQuery(id+"F0.wireOp",EDGE,"E0")])]}),"instanceName":"1"}),"instanceName":"1"}),"instanceName":"1"}),"instanceName":"1"});
            var Q64;
            Q64=makeQuery(id+"F17.opPattern","COPY",BODY,{"derivedFrom":makeQuery(id+"F16.opPattern","COPY",BODY,{"derivedFrom":makeQuery(id+"F15.opPattern","COPY",BODY,{"derivedFrom":makeQuery(id+"F10.opPattern","COPY",BODY,{"derivedFrom":makeQuery(id+"F1.opExtrude","SWEPT_BODY",BODY,{"disambiguationData":[OSD([sQuery(id+"F0.wireOp",EDGE,"E0")])]}),"instanceName":"1"}),"instanceName":"1"}),"instanceName":"1"}),"instanceName":"1"});
            var Q65;
            Q65=makeQuery(id+"F17.opPattern","COPY",BODY,{"derivedFrom":makeQuery(id+"F16.opPattern","COPY",BODY,{"derivedFrom":makeQuery(id+"F14.opPattern","COPY",BODY,{"derivedFrom":makeQuery(id+"F4.opPattern","COPY",BODY,{"derivedFrom":makeQuery(id+"F1.opExtrude","SWEPT_BODY",BODY,{"disambiguationData":[OSD([sQuery(id+"F0.wireOp",EDGE,"E0")])]}),"instanceName":"1"}),"instanceName":"1"}),"instanceName":"1"}),"instanceName":"1"});
            var Q66;
            Q66=makeQuery(id+"F17.opPattern","COPY",BODY,{"derivedFrom":makeQuery(id+"F12.opPattern","COPY",BODY,{"derivedFrom":makeQuery(id+"F9.opPattern","COPY",BODY,{"derivedFrom":makeQuery(id+"F1.opExtrude","SWEPT_BODY",BODY,{"disambiguationData":[OSD([sQuery(id+"F0.wireOp",EDGE,"E0")])]}),"instanceName":"1"}),"instanceName":"1"}),"instanceName":"1"});
            var Q67;
            Q67=makeQuery(id+"F17.opPattern","COPY",BODY,{"derivedFrom":makeQuery(id+"F12.opPattern","COPY",BODY,{"derivedFrom":makeQuery(id+"F11.opPattern","COPY",BODY,{"derivedFrom":makeQuery(id+"F9.opPattern","COPY",BODY,{"derivedFrom":makeQuery(id+"F4.opPattern","COPY",BODY,{"derivedFrom":makeQuery(id+"F1.opExtrude","SWEPT_BODY",BODY,{"disambiguationData":[OSD([sQuery(id+"F0.wireOp",EDGE,"E0")])]}),"instanceName":"1"}),"instanceName":"1"}),"instanceName":"1"}),"instanceName":"1"}),"instanceName":"1"});
            var Q68;
            Q68=makeQuery(id+"F17.opPattern","COPY",BODY,{"derivedFrom":makeQuery(id+"F14.opPattern","COPY",BODY,{"derivedFrom":makeQuery(id+"F1.opExtrude","SWEPT_BODY",BODY,{"disambiguationData":[OSD([sQuery(id+"F0.wireOp",EDGE,"E0")])]}),"instanceName":"1"}),"instanceName":"1"});
            var Q69;
            Q69=makeQuery(id+"F18.opPattern","COPY",BODY,{"derivedFrom":makeQuery(id+"F17.opPattern","COPY",BODY,{"derivedFrom":makeQuery(id+"F15.opPattern","COPY",BODY,{"derivedFrom":makeQuery(id+"F12.opPattern","COPY",BODY,{"derivedFrom":makeQuery(id+"F9.opPattern","COPY",BODY,{"derivedFrom":makeQuery(id+"F4.opPattern","COPY",BODY,{"derivedFrom":makeQuery(id+"F1.opExtrude","SWEPT_BODY",BODY,{"disambiguationData":[OSD([sQuery(id+"F0.wireOp",EDGE,"E0")])]}),"instanceName":"1"}),"instanceName":"1"}),"instanceName":"1"}),"instanceName":"1"}),"instanceName":"1"}),"instanceName":"1"});
            var Q70;
            Q70=makeQuery(id+"F17.opPattern","COPY",BODY,{"derivedFrom":makeQuery(id+"F16.opPattern","COPY",BODY,{"derivedFrom":makeQuery(id+"F12.opPattern","COPY",BODY,{"derivedFrom":makeQuery(id+"F11.opPattern","COPY",BODY,{"derivedFrom":makeQuery(id+"F9.opPattern","COPY",BODY,{"derivedFrom":makeQuery(id+"F1.opExtrude","SWEPT_BODY",BODY,{"disambiguationData":[OSD([sQuery(id+"F0.wireOp",EDGE,"E0")])]}),"instanceName":"1"}),"instanceName":"1"}),"instanceName":"1"}),"instanceName":"1"}),"instanceName":"1"});
            var Q71;
            Q71=makeQuery(id+"F17.opPattern","COPY",BODY,{"derivedFrom":makeQuery(id+"F12.opPattern","COPY",BODY,{"derivedFrom":makeQuery(id+"F1.opExtrude","SWEPT_BODY",BODY,{"disambiguationData":[OSD([sQuery(id+"F0.wireOp",EDGE,"E0")])]}),"instanceName":"1"}),"instanceName":"1"});
            var Q72;
            Q72=makeQuery(id+"F17.opPattern","COPY",BODY,{"derivedFrom":makeQuery(id+"F16.opPattern","COPY",BODY,{"derivedFrom":makeQuery(id+"F10.opPattern","COPY",BODY,{"derivedFrom":makeQuery(id+"F1.opExtrude","SWEPT_BODY",BODY,{"disambiguationData":[OSD([sQuery(id+"F0.wireOp",EDGE,"E0")])]}),"instanceName":"1"}),"instanceName":"1"}),"instanceName":"1"});
            var Q73;
            Q73=makeQuery(id+"F17.opPattern","COPY",BODY,{"derivedFrom":makeQuery(id+"F15.opPattern","COPY",BODY,{"derivedFrom":makeQuery(id+"F9.opPattern","COPY",BODY,{"derivedFrom":makeQuery(id+"F4.opPattern","COPY",BODY,{"derivedFrom":makeQuery(id+"F1.opExtrude","SWEPT_BODY",BODY,{"disambiguationData":[OSD([sQuery(id+"F0.wireOp",EDGE,"E0")])]}),"instanceName":"1"}),"instanceName":"1"}),"instanceName":"1"}),"instanceName":"1"});
            var Q74;
            Q74=makeQuery(id+"F17.opPattern","COPY",BODY,{"derivedFrom":makeQuery(id+"F16.opPattern","COPY",BODY,{"derivedFrom":makeQuery(id+"F9.opPattern","COPY",BODY,{"derivedFrom":makeQuery(id+"F1.opExtrude","SWEPT_BODY",BODY,{"disambiguationData":[OSD([sQuery(id+"F0.wireOp",EDGE,"E0")])]}),"instanceName":"1"}),"instanceName":"1"}),"instanceName":"1"});
            var Q75;
            Q75=makeQuery(id+"F17.opPattern","COPY",BODY,{"derivedFrom":makeQuery(id+"F16.opPattern","COPY",BODY,{"derivedFrom":makeQuery(id+"F4.opPattern","COPY",BODY,{"derivedFrom":makeQuery(id+"F1.opExtrude","SWEPT_BODY",BODY,{"disambiguationData":[OSD([sQuery(id+"F0.wireOp",EDGE,"E0")])]}),"instanceName":"1"}),"instanceName":"1"}),"instanceName":"1"});
            var Q76;
            Q76=makeQuery(id+"F17.opPattern","COPY",BODY,{"derivedFrom":makeQuery(id+"F15.opPattern","COPY",BODY,{"derivedFrom":makeQuery(id+"F12.opPattern","COPY",BODY,{"derivedFrom":makeQuery(id+"F9.opPattern","COPY",BODY,{"derivedFrom":makeQuery(id+"F4.opPattern","COPY",BODY,{"derivedFrom":makeQuery(id+"F1.opExtrude","SWEPT_BODY",BODY,{"disambiguationData":[OSD([sQuery(id+"F0.wireOp",EDGE,"E0")])]}),"instanceName":"1"}),"instanceName":"1"}),"instanceName":"1"}),"instanceName":"1"}),"instanceName":"1"});
            var Q77;
            Q77=makeQuery(id+"F18.opPattern","COPY",BODY,{"derivedFrom":makeQuery(id+"F17.opPattern","COPY",BODY,{"derivedFrom":makeQuery(id+"F15.opPattern","COPY",BODY,{"derivedFrom":makeQuery(id+"F12.opPattern","COPY",BODY,{"derivedFrom":makeQuery(id+"F11.opPattern","COPY",BODY,{"derivedFrom":makeQuery(id+"F9.opPattern","COPY",BODY,{"derivedFrom":makeQuery(id+"F1.opExtrude","SWEPT_BODY",BODY,{"disambiguationData":[OSD([sQuery(id+"F0.wireOp",EDGE,"E0")])]}),"instanceName":"1"}),"instanceName":"1"}),"instanceName":"1"}),"instanceName":"1"}),"instanceName":"1"}),"instanceName":"1"});
            var Q78;
            Q78=makeQuery(id+"F17.opPattern","COPY",BODY,{"derivedFrom":makeQuery(id+"F15.opPattern","COPY",BODY,{"derivedFrom":makeQuery(id+"F12.opPattern","COPY",BODY,{"derivedFrom":makeQuery(id+"F1.opExtrude","SWEPT_BODY",BODY,{"disambiguationData":[OSD([sQuery(id+"F0.wireOp",EDGE,"E0")])]}),"instanceName":"1"}),"instanceName":"1"}),"instanceName":"1"});
            var Q79;
            Q79=makeQuery(id+"F17.opPattern","COPY",BODY,{"derivedFrom":makeQuery(id+"F16.opPattern","COPY",BODY,{"derivedFrom":makeQuery(id+"F15.opPattern","COPY",BODY,{"derivedFrom":makeQuery(id+"F12.opPattern","COPY",BODY,{"derivedFrom":makeQuery(id+"F4.opPattern","COPY",BODY,{"derivedFrom":makeQuery(id+"F1.opExtrude","SWEPT_BODY",BODY,{"disambiguationData":[OSD([sQuery(id+"F0.wireOp",EDGE,"E0")])]}),"instanceName":"1"}),"instanceName":"1"}),"instanceName":"1"}),"instanceName":"1"}),"instanceName":"1"});
            var Q80;
            Q80=makeQuery(id+"F17.opPattern","COPY",BODY,{"derivedFrom":makeQuery(id+"F14.opPattern","COPY",BODY,{"derivedFrom":makeQuery(id+"F11.opPattern","COPY",BODY,{"derivedFrom":makeQuery(id+"F1.opExtrude","SWEPT_BODY",BODY,{"disambiguationData":[OSD([sQuery(id+"F0.wireOp",EDGE,"E0")])]}),"instanceName":"1"}),"instanceName":"1"}),"instanceName":"1"});
            var Q81;
            Q81=makeQuery(id+"F17.opPattern","COPY",BODY,{"derivedFrom":makeQuery(id+"F15.opPattern","COPY",BODY,{"derivedFrom":makeQuery(id+"F4.opPattern","COPY",BODY,{"derivedFrom":makeQuery(id+"F1.opExtrude","SWEPT_BODY",BODY,{"disambiguationData":[OSD([sQuery(id+"F0.wireOp",EDGE,"E0")])]}),"instanceName":"1"}),"instanceName":"1"}),"instanceName":"1"});
            var Q82;
            Q82=makeQuery(id+"F17.opPattern","COPY",BODY,{"derivedFrom":makeQuery(id+"F12.opPattern","COPY",BODY,{"derivedFrom":makeQuery(id+"F9.opPattern","COPY",BODY,{"derivedFrom":makeQuery(id+"F4.opPattern","COPY",BODY,{"derivedFrom":makeQuery(id+"F1.opExtrude","SWEPT_BODY",BODY,{"disambiguationData":[OSD([sQuery(id+"F0.wireOp",EDGE,"E0")])]}),"instanceName":"1"}),"instanceName":"1"}),"instanceName":"1"}),"instanceName":"1"});
            var Q83;
            Q83=makeQuery(id+"F17.opPattern","COPY",BODY,{"derivedFrom":makeQuery(id+"F16.opPattern","COPY",BODY,{"derivedFrom":makeQuery(id+"F15.opPattern","COPY",BODY,{"derivedFrom":makeQuery(id+"F11.opPattern","COPY",BODY,{"derivedFrom":makeQuery(id+"F1.opExtrude","SWEPT_BODY",BODY,{"disambiguationData":[OSD([sQuery(id+"F0.wireOp",EDGE,"E0")])]}),"instanceName":"1"}),"instanceName":"1"}),"instanceName":"1"}),"instanceName":"1"});
            var Q84;
            Q84=makeQuery(id+"F17.opPattern","COPY",BODY,{"derivedFrom":makeQuery(id+"F16.opPattern","COPY",BODY,{"derivedFrom":makeQuery(id+"F15.opPattern","COPY",BODY,{"derivedFrom":makeQuery(id+"F12.opPattern","COPY",BODY,{"derivedFrom":makeQuery(id+"F11.opPattern","COPY",BODY,{"derivedFrom":makeQuery(id+"F1.opExtrude","SWEPT_BODY",BODY,{"disambiguationData":[OSD([sQuery(id+"F0.wireOp",EDGE,"E0")])]}),"instanceName":"1"}),"instanceName":"1"}),"instanceName":"1"}),"instanceName":"1"}),"instanceName":"1"});
            var Q85;
            Q85=makeQuery(id+"F17.opPattern","COPY",BODY,{"derivedFrom":makeQuery(id+"F16.opPattern","COPY",BODY,{"derivedFrom":makeQuery(id+"F15.opPattern","COPY",BODY,{"derivedFrom":makeQuery(id+"F12.opPattern","COPY",BODY,{"derivedFrom":makeQuery(id+"F11.opPattern","COPY",BODY,{"derivedFrom":makeQuery(id+"F9.opPattern","COPY",BODY,{"derivedFrom":makeQuery(id+"F4.opPattern","COPY",BODY,{"derivedFrom":makeQuery(id+"F1.opExtrude","SWEPT_BODY",BODY,{"disambiguationData":[OSD([sQuery(id+"F0.wireOp",EDGE,"E0")])]}),"instanceName":"1"}),"instanceName":"1"}),"instanceName":"1"}),"instanceName":"1"}),"instanceName":"1"}),"instanceName":"1"}),"instanceName":"1"});
            var Q86;
            Q86=makeQuery(id+"F17.opPattern","COPY",BODY,{"derivedFrom":makeQuery(id+"F16.opPattern","COPY",BODY,{"derivedFrom":makeQuery(id+"F14.opPattern","COPY",BODY,{"derivedFrom":makeQuery(id+"F11.opPattern","COPY",BODY,{"derivedFrom":makeQuery(id+"F1.opExtrude","SWEPT_BODY",BODY,{"disambiguationData":[OSD([sQuery(id+"F0.wireOp",EDGE,"E0")])]}),"instanceName":"1"}),"instanceName":"1"}),"instanceName":"1"}),"instanceName":"1"});
            var Q87;
            Q87=makeQuery(id+"F17.opPattern","COPY",BODY,{"derivedFrom":makeQuery(id+"F16.opPattern","COPY",BODY,{"derivedFrom":makeQuery(id+"F11.opPattern","COPY",BODY,{"derivedFrom":makeQuery(id+"F9.opPattern","COPY",BODY,{"derivedFrom":makeQuery(id+"F1.opExtrude","SWEPT_BODY",BODY,{"disambiguationData":[OSD([sQuery(id+"F0.wireOp",EDGE,"E0")])]}),"instanceName":"1"}),"instanceName":"1"}),"instanceName":"1"}),"instanceName":"1"});
            var Q88;
            Q88=makeQuery(id+"F17.opPattern","COPY",BODY,{"derivedFrom":makeQuery(id+"F16.opPattern","COPY",BODY,{"derivedFrom":makeQuery(id+"F11.opPattern","COPY",BODY,{"derivedFrom":makeQuery(id+"F10.opPattern","COPY",BODY,{"derivedFrom":makeQuery(id+"F1.opExtrude","SWEPT_BODY",BODY,{"disambiguationData":[OSD([sQuery(id+"F0.wireOp",EDGE,"E0")])]}),"instanceName":"1"}),"instanceName":"1"}),"instanceName":"1"}),"instanceName":"1"});
            var Q89;
            Q89=makeQuery(id+"F17.opPattern","COPY",BODY,{"derivedFrom":makeQuery(id+"F10.opPattern","COPY",BODY,{"derivedFrom":makeQuery(id+"F1.opExtrude","SWEPT_BODY",BODY,{"disambiguationData":[OSD([sQuery(id+"F0.wireOp",EDGE,"E0")])]}),"instanceName":"1"}),"instanceName":"1"});
            var Q90;
            Q90=makeQuery(id+"F18.opPattern","COPY",BODY,{"derivedFrom":makeQuery(id+"F17.opPattern","COPY",BODY,{"derivedFrom":makeQuery(id+"F15.opPattern","COPY",BODY,{"derivedFrom":makeQuery(id+"F11.opPattern","COPY",BODY,{"derivedFrom":makeQuery(id+"F9.opPattern","COPY",BODY,{"derivedFrom":makeQuery(id+"F1.opExtrude","SWEPT_BODY",BODY,{"disambiguationData":[OSD([sQuery(id+"F0.wireOp",EDGE,"E0")])]}),"instanceName":"1"}),"instanceName":"1"}),"instanceName":"1"}),"instanceName":"1"}),"instanceName":"1"});
            var Q91;
            Q91=makeQuery(id+"F17.opPattern","COPY",BODY,{"derivedFrom":makeQuery(id+"F16.opPattern","COPY",BODY,{"derivedFrom":makeQuery(id+"F12.opPattern","COPY",BODY,{"derivedFrom":makeQuery(id+"F9.opPattern","COPY",BODY,{"derivedFrom":makeQuery(id+"F4.opPattern","COPY",BODY,{"derivedFrom":makeQuery(id+"F1.opExtrude","SWEPT_BODY",BODY,{"disambiguationData":[OSD([sQuery(id+"F0.wireOp",EDGE,"E0")])]}),"instanceName":"1"}),"instanceName":"1"}),"instanceName":"1"}),"instanceName":"1"}),"instanceName":"1"});
            var Q92;
            Q92=makeQuery(id+"F18.opPattern","COPY",BODY,{"derivedFrom":makeQuery(id+"F17.opPattern","COPY",BODY,{"derivedFrom":makeQuery(id+"F16.opPattern","COPY",BODY,{"derivedFrom":makeQuery(id+"F12.opPattern","COPY",BODY,{"derivedFrom":makeQuery(id+"F11.opPattern","COPY",BODY,{"derivedFrom":makeQuery(id+"F4.opPattern","COPY",BODY,{"derivedFrom":makeQuery(id+"F1.opExtrude","SWEPT_BODY",BODY,{"disambiguationData":[OSD([sQuery(id+"F0.wireOp",EDGE,"E0")])]}),"instanceName":"1"}),"instanceName":"1"}),"instanceName":"1"}),"instanceName":"1"}),"instanceName":"1"}),"instanceName":"1"});
            var Q93;
            Q93=makeQuery(id+"F18.opPattern","COPY",BODY,{"derivedFrom":makeQuery(id+"F17.opPattern","COPY",BODY,{"derivedFrom":makeQuery(id+"F15.opPattern","COPY",BODY,{"derivedFrom":makeQuery(id+"F12.opPattern","COPY",BODY,{"derivedFrom":makeQuery(id+"F10.opPattern","COPY",BODY,{"derivedFrom":makeQuery(id+"F1.opExtrude","SWEPT_BODY",BODY,{"disambiguationData":[OSD([sQuery(id+"F0.wireOp",EDGE,"E0")])]}),"instanceName":"1"}),"instanceName":"1"}),"instanceName":"1"}),"instanceName":"1"}),"instanceName":"1"});
            var Q94;
            Q94=makeQuery(id+"F17.opPattern","COPY",BODY,{"derivedFrom":makeQuery(id+"F11.opPattern","COPY",BODY,{"derivedFrom":makeQuery(id+"F9.opPattern","COPY",BODY,{"derivedFrom":makeQuery(id+"F1.opExtrude","SWEPT_BODY",BODY,{"disambiguationData":[OSD([sQuery(id+"F0.wireOp",EDGE,"E0")])]}),"instanceName":"1"}),"instanceName":"1"}),"instanceName":"1"});
            var Q95;
            Q95=makeQuery(id+"F17.opPattern","COPY",BODY,{"derivedFrom":makeQuery(id+"F15.opPattern","COPY",BODY,{"derivedFrom":makeQuery(id+"F14.opPattern","COPY",BODY,{"derivedFrom":makeQuery(id+"F11.opPattern","COPY",BODY,{"derivedFrom":makeQuery(id+"F1.opExtrude","SWEPT_BODY",BODY,{"disambiguationData":[OSD([sQuery(id+"F0.wireOp",EDGE,"E0")])]}),"instanceName":"1"}),"instanceName":"1"}),"instanceName":"1"}),"instanceName":"1"});
            var Q96;
            Q96=makeQuery(id+"F17.opPattern","COPY",BODY,{"derivedFrom":makeQuery(id+"F15.opPattern","COPY",BODY,{"derivedFrom":makeQuery(id+"F14.opPattern","COPY",BODY,{"derivedFrom":makeQuery(id+"F11.opPattern","COPY",BODY,{"derivedFrom":makeQuery(id+"F9.opPattern","COPY",BODY,{"derivedFrom":makeQuery(id+"F4.opPattern","COPY",BODY,{"derivedFrom":makeQuery(id+"F1.opExtrude","SWEPT_BODY",BODY,{"disambiguationData":[OSD([sQuery(id+"F0.wireOp",EDGE,"E0")])]}),"instanceName":"1"}),"instanceName":"1"}),"instanceName":"1"}),"instanceName":"1"}),"instanceName":"1"}),"instanceName":"1"});
            var Q97;
            Q97=makeQuery(id+"F18.opPattern","COPY",BODY,{"derivedFrom":makeQuery(id+"F17.opPattern","COPY",BODY,{"derivedFrom":makeQuery(id+"F16.opPattern","COPY",BODY,{"derivedFrom":makeQuery(id+"F14.opPattern","COPY",BODY,{"derivedFrom":makeQuery(id+"F4.opPattern","COPY",BODY,{"derivedFrom":makeQuery(id+"F1.opExtrude","SWEPT_BODY",BODY,{"disambiguationData":[OSD([sQuery(id+"F0.wireOp",EDGE,"E0")])]}),"instanceName":"1"}),"instanceName":"1"}),"instanceName":"1"}),"instanceName":"1"}),"instanceName":"1"});
            var Q98;
            Q98=makeQuery(id+"F17.opPattern","COPY",BODY,{"derivedFrom":makeQuery(id+"F15.opPattern","COPY",BODY,{"derivedFrom":makeQuery(id+"F11.opPattern","COPY",BODY,{"derivedFrom":makeQuery(id+"F4.opPattern","COPY",BODY,{"derivedFrom":makeQuery(id+"F1.opExtrude","SWEPT_BODY",BODY,{"disambiguationData":[OSD([sQuery(id+"F0.wireOp",EDGE,"E0")])]}),"instanceName":"1"}),"instanceName":"1"}),"instanceName":"1"}),"instanceName":"1"});
            var Q99;
            Q99=makeQuery(id+"F17.opPattern","COPY",BODY,{"derivedFrom":makeQuery(id+"F15.opPattern","COPY",BODY,{"derivedFrom":makeQuery(id+"F11.opPattern","COPY",BODY,{"derivedFrom":makeQuery(id+"F9.opPattern","COPY",BODY,{"derivedFrom":makeQuery(id+"F1.opExtrude","SWEPT_BODY",BODY,{"disambiguationData":[OSD([sQuery(id+"F0.wireOp",EDGE,"E0")])]}),"instanceName":"1"}),"instanceName":"1"}),"instanceName":"1"}),"instanceName":"1"});
            var Q100;
            Q100=makeQuery(id+"F18.opPattern","COPY",BODY,{"derivedFrom":makeQuery(id+"F17.opPattern","COPY",BODY,{"derivedFrom":makeQuery(id+"F15.opPattern","COPY",BODY,{"derivedFrom":makeQuery(id+"F12.opPattern","COPY",BODY,{"derivedFrom":makeQuery(id+"F9.opPattern","COPY",BODY,{"derivedFrom":makeQuery(id+"F1.opExtrude","SWEPT_BODY",BODY,{"disambiguationData":[OSD([sQuery(id+"F0.wireOp",EDGE,"E0")])]}),"instanceName":"1"}),"instanceName":"1"}),"instanceName":"1"}),"instanceName":"1"}),"instanceName":"1"});
            var Q101;
            Q101=makeQuery(id+"F17.opPattern","COPY",BODY,{"derivedFrom":makeQuery(id+"F12.opPattern","COPY",BODY,{"derivedFrom":makeQuery(id+"F11.opPattern","COPY",BODY,{"derivedFrom":makeQuery(id+"F1.opExtrude","SWEPT_BODY",BODY,{"disambiguationData":[OSD([sQuery(id+"F0.wireOp",EDGE,"E0")])]}),"instanceName":"1"}),"instanceName":"1"}),"instanceName":"1"});
            var Q102;
            Q102=makeQuery(id+"F17.opPattern","COPY",BODY,{"derivedFrom":makeQuery(id+"F16.opPattern","COPY",BODY,{"derivedFrom":makeQuery(id+"F12.opPattern","COPY",BODY,{"derivedFrom":makeQuery(id+"F11.opPattern","COPY",BODY,{"derivedFrom":makeQuery(id+"F1.opExtrude","SWEPT_BODY",BODY,{"disambiguationData":[OSD([sQuery(id+"F0.wireOp",EDGE,"E0")])]}),"instanceName":"1"}),"instanceName":"1"}),"instanceName":"1"}),"instanceName":"1"});
            var Q103;
            Q103=makeQuery(id+"F17.opPattern","COPY",BODY,{"derivedFrom":makeQuery(id+"F11.opPattern","COPY",BODY,{"derivedFrom":makeQuery(id+"F4.opPattern","COPY",BODY,{"derivedFrom":makeQuery(id+"F1.opExtrude","SWEPT_BODY",BODY,{"disambiguationData":[OSD([sQuery(id+"F0.wireOp",EDGE,"E0")])]}),"instanceName":"1"}),"instanceName":"1"}),"instanceName":"1"});
            var Q104;
            Q104=makeQuery(id+"F17.opPattern","COPY",BODY,{"derivedFrom":makeQuery(id+"F16.opPattern","COPY",BODY,{"derivedFrom":makeQuery(id+"F15.opPattern","COPY",BODY,{"derivedFrom":makeQuery(id+"F14.opPattern","COPY",BODY,{"derivedFrom":makeQuery(id+"F10.opPattern","COPY",BODY,{"derivedFrom":makeQuery(id+"F1.opExtrude","SWEPT_BODY",BODY,{"disambiguationData":[OSD([sQuery(id+"F0.wireOp",EDGE,"E0")])]}),"instanceName":"1"}),"instanceName":"1"}),"instanceName":"1"}),"instanceName":"1"}),"instanceName":"1"});
            var Q105;
            Q105=makeQuery(id+"F18.opPattern","COPY",BODY,{"derivedFrom":makeQuery(id+"F17.opPattern","COPY",BODY,{"derivedFrom":makeQuery(id+"F15.opPattern","COPY",BODY,{"derivedFrom":makeQuery(id+"F14.opPattern","COPY",BODY,{"derivedFrom":makeQuery(id+"F11.opPattern","COPY",BODY,{"derivedFrom":makeQuery(id+"F10.opPattern","COPY",BODY,{"derivedFrom":makeQuery(id+"F1.opExtrude","SWEPT_BODY",BODY,{"disambiguationData":[OSD([sQuery(id+"F0.wireOp",EDGE,"E0")])]}),"instanceName":"1"}),"instanceName":"1"}),"instanceName":"1"}),"instanceName":"1"}),"instanceName":"1"}),"instanceName":"1"});
            var Q106;
            Q106=makeQuery(id+"F18.opPattern","COPY",BODY,{"derivedFrom":makeQuery(id+"F17.opPattern","COPY",BODY,{"derivedFrom":makeQuery(id+"F16.opPattern","COPY",BODY,{"derivedFrom":makeQuery(id+"F12.opPattern","COPY",BODY,{"derivedFrom":makeQuery(id+"F10.opPattern","COPY",BODY,{"derivedFrom":makeQuery(id+"F1.opExtrude","SWEPT_BODY",BODY,{"disambiguationData":[OSD([sQuery(id+"F0.wireOp",EDGE,"E0")])]}),"instanceName":"1"}),"instanceName":"1"}),"instanceName":"1"}),"instanceName":"1"}),"instanceName":"1"});
            var Q107;
            Q107=makeQuery(id+"F17.opPattern","COPY",BODY,{"derivedFrom":makeQuery(id+"F11.opPattern","COPY",BODY,{"derivedFrom":makeQuery(id+"F10.opPattern","COPY",BODY,{"derivedFrom":makeQuery(id+"F1.opExtrude","SWEPT_BODY",BODY,{"disambiguationData":[OSD([sQuery(id+"F0.wireOp",EDGE,"E0")])]}),"instanceName":"1"}),"instanceName":"1"}),"instanceName":"1"});
            var Q108;
            Q108=makeQuery(id+"F17.opPattern","COPY",BODY,{"derivedFrom":makeQuery(id+"F15.opPattern","COPY",BODY,{"derivedFrom":makeQuery(id+"F12.opPattern","COPY",BODY,{"derivedFrom":makeQuery(id+"F10.opPattern","COPY",BODY,{"derivedFrom":makeQuery(id+"F1.opExtrude","SWEPT_BODY",BODY,{"disambiguationData":[OSD([sQuery(id+"F0.wireOp",EDGE,"E0")])]}),"instanceName":"1"}),"instanceName":"1"}),"instanceName":"1"}),"instanceName":"1"});
            var Q109;
            Q109=makeQuery(id+"F17.opPattern","COPY",BODY,{"derivedFrom":makeQuery(id+"F16.opPattern","COPY",BODY,{"derivedFrom":makeQuery(id+"F15.opPattern","COPY",BODY,{"derivedFrom":makeQuery(id+"F11.opPattern","COPY",BODY,{"derivedFrom":makeQuery(id+"F9.opPattern","COPY",BODY,{"derivedFrom":makeQuery(id+"F4.opPattern","COPY",BODY,{"derivedFrom":makeQuery(id+"F1.opExtrude","SWEPT_BODY",BODY,{"disambiguationData":[OSD([sQuery(id+"F0.wireOp",EDGE,"E0")])]}),"instanceName":"1"}),"instanceName":"1"}),"instanceName":"1"}),"instanceName":"1"}),"instanceName":"1"}),"instanceName":"1"});
            var Q110;
            Q110=makeQuery(id+"F17.opPattern","COPY",BODY,{"derivedFrom":makeQuery(id+"F16.opPattern","COPY",BODY,{"derivedFrom":makeQuery(id+"F15.opPattern","COPY",BODY,{"derivedFrom":makeQuery(id+"F12.opPattern","COPY",BODY,{"derivedFrom":makeQuery(id+"F1.opExtrude","SWEPT_BODY",BODY,{"disambiguationData":[OSD([sQuery(id+"F0.wireOp",EDGE,"E0")])]}),"instanceName":"1"}),"instanceName":"1"}),"instanceName":"1"}),"instanceName":"1"});
            var Q111;
            Q111=makeQuery(id+"F17.opPattern","COPY",BODY,{"derivedFrom":makeQuery(id+"F16.opPattern","COPY",BODY,{"derivedFrom":makeQuery(id+"F15.opPattern","COPY",BODY,{"derivedFrom":makeQuery(id+"F12.opPattern","COPY",BODY,{"derivedFrom":makeQuery(id+"F11.opPattern","COPY",BODY,{"derivedFrom":makeQuery(id+"F9.opPattern","COPY",BODY,{"derivedFrom":makeQuery(id+"F1.opExtrude","SWEPT_BODY",BODY,{"disambiguationData":[OSD([sQuery(id+"F0.wireOp",EDGE,"E0")])]}),"instanceName":"1"}),"instanceName":"1"}),"instanceName":"1"}),"instanceName":"1"}),"instanceName":"1"}),"instanceName":"1"});
            var Q112;
            Q112=makeQuery(id+"F17.opPattern","COPY",BODY,{"derivedFrom":makeQuery(id+"F16.opPattern","COPY",BODY,{"derivedFrom":makeQuery(id+"F12.opPattern","COPY",BODY,{"derivedFrom":makeQuery(id+"F11.opPattern","COPY",BODY,{"derivedFrom":makeQuery(id+"F4.opPattern","COPY",BODY,{"derivedFrom":makeQuery(id+"F1.opExtrude","SWEPT_BODY",BODY,{"disambiguationData":[OSD([sQuery(id+"F0.wireOp",EDGE,"E0")])]}),"instanceName":"1"}),"instanceName":"1"}),"instanceName":"1"}),"instanceName":"1"}),"instanceName":"1"});
            var Q113;
            Q113=makeQuery(id+"F17.opPattern","COPY",BODY,{"derivedFrom":makeQuery(id+"F16.opPattern","COPY",BODY,{"derivedFrom":makeQuery(id+"F11.opPattern","COPY",BODY,{"derivedFrom":makeQuery(id+"F4.opPattern","COPY",BODY,{"derivedFrom":makeQuery(id+"F1.opExtrude","SWEPT_BODY",BODY,{"disambiguationData":[OSD([sQuery(id+"F0.wireOp",EDGE,"E0")])]}),"instanceName":"1"}),"instanceName":"1"}),"instanceName":"1"}),"instanceName":"1"});
            var Q114;
            Q114=makeQuery(id+"F18.opPattern","COPY",BODY,{"derivedFrom":makeQuery(id+"F17.opPattern","COPY",BODY,{"derivedFrom":makeQuery(id+"F15.opPattern","COPY",BODY,{"derivedFrom":makeQuery(id+"F14.opPattern","COPY",BODY,{"derivedFrom":makeQuery(id+"F1.opExtrude","SWEPT_BODY",BODY,{"disambiguationData":[OSD([sQuery(id+"F0.wireOp",EDGE,"E0")])]}),"instanceName":"1"}),"instanceName":"1"}),"instanceName":"1"}),"instanceName":"1"});
            var Q115;
            Q115=makeQuery(id+"F17.opPattern","COPY",BODY,{"derivedFrom":makeQuery(id+"F15.opPattern","COPY",BODY,{"derivedFrom":makeQuery(id+"F12.opPattern","COPY",BODY,{"derivedFrom":makeQuery(id+"F11.opPattern","COPY",BODY,{"derivedFrom":makeQuery(id+"F4.opPattern","COPY",BODY,{"derivedFrom":makeQuery(id+"F1.opExtrude","SWEPT_BODY",BODY,{"disambiguationData":[OSD([sQuery(id+"F0.wireOp",EDGE,"E0")])]}),"instanceName":"1"}),"instanceName":"1"}),"instanceName":"1"}),"instanceName":"1"}),"instanceName":"1"});
            var Q116;
            Q116=makeQuery(id+"F17.opPattern","COPY",BODY,{"derivedFrom":makeQuery(id+"F15.opPattern","COPY",BODY,{"derivedFrom":makeQuery(id+"F9.opPattern","COPY",BODY,{"derivedFrom":makeQuery(id+"F1.opExtrude","SWEPT_BODY",BODY,{"disambiguationData":[OSD([sQuery(id+"F0.wireOp",EDGE,"E0")])]}),"instanceName":"1"}),"instanceName":"1"}),"instanceName":"1"});
            var Q117;
            Q117=makeQuery(id+"F18.opPattern","COPY",BODY,{"derivedFrom":makeQuery(id+"F17.opPattern","COPY",BODY,{"derivedFrom":makeQuery(id+"F15.opPattern","COPY",BODY,{"derivedFrom":makeQuery(id+"F14.opPattern","COPY",BODY,{"derivedFrom":makeQuery(id+"F11.opPattern","COPY",BODY,{"derivedFrom":makeQuery(id+"F9.opPattern","COPY",BODY,{"derivedFrom":makeQuery(id+"F1.opExtrude","SWEPT_BODY",BODY,{"disambiguationData":[OSD([sQuery(id+"F0.wireOp",EDGE,"E0")])]}),"instanceName":"1"}),"instanceName":"1"}),"instanceName":"1"}),"instanceName":"1"}),"instanceName":"1"}),"instanceName":"1"});
            var Q118;
            Q118=makeQuery(id+"F18.opPattern","COPY",BODY,{"derivedFrom":makeQuery(id+"F17.opPattern","COPY",BODY,{"derivedFrom":makeQuery(id+"F16.opPattern","COPY",BODY,{"derivedFrom":makeQuery(id+"F12.opPattern","COPY",BODY,{"derivedFrom":makeQuery(id+"F11.opPattern","COPY",BODY,{"derivedFrom":makeQuery(id+"F9.opPattern","COPY",BODY,{"derivedFrom":makeQuery(id+"F4.opPattern","COPY",BODY,{"derivedFrom":makeQuery(id+"F1.opExtrude","SWEPT_BODY",BODY,{"disambiguationData":[OSD([sQuery(id+"F0.wireOp",EDGE,"E0")])]}),"instanceName":"1"}),"instanceName":"1"}),"instanceName":"1"}),"instanceName":"1"}),"instanceName":"1"}),"instanceName":"1"}),"instanceName":"1"});
            var Q119;
            Q119=makeQuery(id+"F17.opPattern","COPY",BODY,{"derivedFrom":makeQuery(id+"F15.opPattern","COPY",BODY,{"derivedFrom":makeQuery(id+"F14.opPattern","COPY",BODY,{"derivedFrom":makeQuery(id+"F11.opPattern","COPY",BODY,{"derivedFrom":makeQuery(id+"F9.opPattern","COPY",BODY,{"derivedFrom":makeQuery(id+"F1.opExtrude","SWEPT_BODY",BODY,{"disambiguationData":[OSD([sQuery(id+"F0.wireOp",EDGE,"E0")])]}),"instanceName":"1"}),"instanceName":"1"}),"instanceName":"1"}),"instanceName":"1"}),"instanceName":"1"});
            var Q120;
            Q120=makeQuery(id+"F17.opPattern","COPY",BODY,{"derivedFrom":makeQuery(id+"F14.opPattern","COPY",BODY,{"derivedFrom":makeQuery(id+"F11.opPattern","COPY",BODY,{"derivedFrom":makeQuery(id+"F4.opPattern","COPY",BODY,{"derivedFrom":makeQuery(id+"F1.opExtrude","SWEPT_BODY",BODY,{"disambiguationData":[OSD([sQuery(id+"F0.wireOp",EDGE,"E0")])]}),"instanceName":"1"}),"instanceName":"1"}),"instanceName":"1"}),"instanceName":"1"});
            var Q121;
            Q121=makeQuery(id+"F17.opPattern","COPY",BODY,{"derivedFrom":makeQuery(id+"F12.opPattern","COPY",BODY,{"derivedFrom":makeQuery(id+"F11.opPattern","COPY",BODY,{"derivedFrom":makeQuery(id+"F10.opPattern","COPY",BODY,{"derivedFrom":makeQuery(id+"F1.opExtrude","SWEPT_BODY",BODY,{"disambiguationData":[OSD([sQuery(id+"F0.wireOp",EDGE,"E0")])]}),"instanceName":"1"}),"instanceName":"1"}),"instanceName":"1"}),"instanceName":"1"});
            var Q122;
            Q122=makeQuery(id+"F18.opPattern","COPY",BODY,{"derivedFrom":makeQuery(id+"F17.opPattern","COPY",BODY,{"derivedFrom":makeQuery(id+"F16.opPattern","COPY",BODY,{"derivedFrom":makeQuery(id+"F9.opPattern","COPY",BODY,{"derivedFrom":makeQuery(id+"F1.opExtrude","SWEPT_BODY",BODY,{"disambiguationData":[OSD([sQuery(id+"F0.wireOp",EDGE,"E0")])]}),"instanceName":"1"}),"instanceName":"1"}),"instanceName":"1"}),"instanceName":"1"});
            var Q123;
            Q123=makeQuery(id+"F17.opPattern","COPY",BODY,{"derivedFrom":makeQuery(id+"F11.opPattern","COPY",BODY,{"derivedFrom":makeQuery(id+"F1.opExtrude","SWEPT_BODY",BODY,{"disambiguationData":[OSD([sQuery(id+"F0.wireOp",EDGE,"E0")])]}),"instanceName":"1"}),"instanceName":"1"});
            var Q124;
            Q124=makeQuery(id+"F17.opPattern","COPY",BODY,{"derivedFrom":makeQuery(id+"F11.opPattern","COPY",BODY,{"derivedFrom":makeQuery(id+"F9.opPattern","COPY",BODY,{"derivedFrom":makeQuery(id+"F4.opPattern","COPY",BODY,{"derivedFrom":makeQuery(id+"F1.opExtrude","SWEPT_BODY",BODY,{"disambiguationData":[OSD([sQuery(id+"F0.wireOp",EDGE,"E0")])]}),"instanceName":"1"}),"instanceName":"1"}),"instanceName":"1"}),"instanceName":"1"});
            var Q125;
            Q125=makeQuery(id+"F17.opPattern","COPY",BODY,{"derivedFrom":makeQuery(id+"F16.opPattern","COPY",BODY,{"derivedFrom":makeQuery(id+"F15.opPattern","COPY",BODY,{"derivedFrom":makeQuery(id+"F12.opPattern","COPY",BODY,{"derivedFrom":makeQuery(id+"F9.opPattern","COPY",BODY,{"derivedFrom":makeQuery(id+"F4.opPattern","COPY",BODY,{"derivedFrom":makeQuery(id+"F1.opExtrude","SWEPT_BODY",BODY,{"disambiguationData":[OSD([sQuery(id+"F0.wireOp",EDGE,"E0")])]}),"instanceName":"1"}),"instanceName":"1"}),"instanceName":"1"}),"instanceName":"1"}),"instanceName":"1"}),"instanceName":"1"});
            var Q126;
            Q126=makeQuery(id+"F17.opPattern","COPY",BODY,{"derivedFrom":makeQuery(id+"F16.opPattern","COPY",BODY,{"derivedFrom":makeQuery(id+"F15.opPattern","COPY",BODY,{"derivedFrom":makeQuery(id+"F9.opPattern","COPY",BODY,{"derivedFrom":makeQuery(id+"F4.opPattern","COPY",BODY,{"derivedFrom":makeQuery(id+"F1.opExtrude","SWEPT_BODY",BODY,{"disambiguationData":[OSD([sQuery(id+"F0.wireOp",EDGE,"E0")])]}),"instanceName":"1"}),"instanceName":"1"}),"instanceName":"1"}),"instanceName":"1"}),"instanceName":"1"});
            var Q127;
            Q127=makeQuery(id+"F17.opPattern","COPY",BODY,{"derivedFrom":makeQuery(id+"F15.opPattern","COPY",BODY,{"derivedFrom":makeQuery(id+"F14.opPattern","COPY",BODY,{"derivedFrom":makeQuery(id+"F4.opPattern","COPY",BODY,{"derivedFrom":makeQuery(id+"F1.opExtrude","SWEPT_BODY",BODY,{"disambiguationData":[OSD([sQuery(id+"F0.wireOp",EDGE,"E0")])]}),"instanceName":"1"}),"instanceName":"1"}),"instanceName":"1"}),"instanceName":"1"});
            var Q128;
            Q128=makeQuery(id+"F18.opPattern","COPY",BODY,{"derivedFrom":makeQuery(id+"F17.opPattern","COPY",BODY,{"derivedFrom":makeQuery(id+"F15.opPattern","COPY",BODY,{"derivedFrom":makeQuery(id+"F12.opPattern","COPY",BODY,{"derivedFrom":makeQuery(id+"F11.opPattern","COPY",BODY,{"derivedFrom":makeQuery(id+"F10.opPattern","COPY",BODY,{"derivedFrom":makeQuery(id+"F1.opExtrude","SWEPT_BODY",BODY,{"disambiguationData":[OSD([sQuery(id+"F0.wireOp",EDGE,"E0")])]}),"instanceName":"1"}),"instanceName":"1"}),"instanceName":"1"}),"instanceName":"1"}),"instanceName":"1"}),"instanceName":"1"});
            var Q129;
            Q129=makeQuery(id+"F18.opPattern","COPY",BODY,{"derivedFrom":makeQuery(id+"F17.opPattern","COPY",BODY,{"derivedFrom":makeQuery(id+"F15.opPattern","COPY",BODY,{"derivedFrom":makeQuery(id+"F11.opPattern","COPY",BODY,{"derivedFrom":makeQuery(id+"F10.opPattern","COPY",BODY,{"derivedFrom":makeQuery(id+"F1.opExtrude","SWEPT_BODY",BODY,{"disambiguationData":[OSD([sQuery(id+"F0.wireOp",EDGE,"E0")])]}),"instanceName":"1"}),"instanceName":"1"}),"instanceName":"1"}),"instanceName":"1"}),"instanceName":"1"});
            var Q130;
            Q130=makeQuery(id+"F17.opPattern","COPY",BODY,{"derivedFrom":makeQuery(id+"F15.opPattern","COPY",BODY,{"derivedFrom":makeQuery(id+"F12.opPattern","COPY",BODY,{"derivedFrom":makeQuery(id+"F11.opPattern","COPY",BODY,{"derivedFrom":makeQuery(id+"F1.opExtrude","SWEPT_BODY",BODY,{"disambiguationData":[OSD([sQuery(id+"F0.wireOp",EDGE,"E0")])]}),"instanceName":"1"}),"instanceName":"1"}),"instanceName":"1"}),"instanceName":"1"});
            var Q131;
            Q131=makeQuery(id+"F17.opPattern","COPY",BODY,{"derivedFrom":makeQuery(id+"F12.opPattern","COPY",BODY,{"derivedFrom":makeQuery(id+"F10.opPattern","COPY",BODY,{"derivedFrom":makeQuery(id+"F1.opExtrude","SWEPT_BODY",BODY,{"disambiguationData":[OSD([sQuery(id+"F0.wireOp",EDGE,"E0")])]}),"instanceName":"1"}),"instanceName":"1"}),"instanceName":"1"});
            var Q132;
            Q132=makeQuery(id+"F18.opPattern","COPY",BODY,{"derivedFrom":makeQuery(id+"F17.opPattern","COPY",BODY,{"derivedFrom":makeQuery(id+"F15.opPattern","COPY",BODY,{"derivedFrom":makeQuery(id+"F12.opPattern","COPY",BODY,{"derivedFrom":makeQuery(id+"F11.opPattern","COPY",BODY,{"derivedFrom":makeQuery(id+"F4.opPattern","COPY",BODY,{"derivedFrom":makeQuery(id+"F1.opExtrude","SWEPT_BODY",BODY,{"disambiguationData":[OSD([sQuery(id+"F0.wireOp",EDGE,"E0")])]}),"instanceName":"1"}),"instanceName":"1"}),"instanceName":"1"}),"instanceName":"1"}),"instanceName":"1"}),"instanceName":"1"});
            var Q133;
            Q133=makeQuery(id+"F18.opPattern","COPY",BODY,{"derivedFrom":makeQuery(id+"F17.opPattern","COPY",BODY,{"derivedFrom":makeQuery(id+"F15.opPattern","COPY",BODY,{"derivedFrom":makeQuery(id+"F14.opPattern","COPY",BODY,{"derivedFrom":makeQuery(id+"F11.opPattern","COPY",BODY,{"derivedFrom":makeQuery(id+"F4.opPattern","COPY",BODY,{"derivedFrom":makeQuery(id+"F1.opExtrude","SWEPT_BODY",BODY,{"disambiguationData":[OSD([sQuery(id+"F0.wireOp",EDGE,"E0")])]}),"instanceName":"1"}),"instanceName":"1"}),"instanceName":"1"}),"instanceName":"1"}),"instanceName":"1"}),"instanceName":"1"});
            var Q134;
            Q134=makeQuery(id+"F17.opPattern","COPY",BODY,{"derivedFrom":makeQuery(id+"F16.opPattern","COPY",BODY,{"derivedFrom":makeQuery(id+"F15.opPattern","COPY",BODY,{"derivedFrom":makeQuery(id+"F11.opPattern","COPY",BODY,{"derivedFrom":makeQuery(id+"F9.opPattern","COPY",BODY,{"derivedFrom":makeQuery(id+"F1.opExtrude","SWEPT_BODY",BODY,{"disambiguationData":[OSD([sQuery(id+"F0.wireOp",EDGE,"E0")])]}),"instanceName":"1"}),"instanceName":"1"}),"instanceName":"1"}),"instanceName":"1"}),"instanceName":"1"});
            var Q135;
            Q135=makeQuery(id+"F17.opPattern","COPY",BODY,{"derivedFrom":makeQuery(id+"F16.opPattern","COPY",BODY,{"derivedFrom":makeQuery(id+"F15.opPattern","COPY",BODY,{"derivedFrom":makeQuery(id+"F11.opPattern","COPY",BODY,{"derivedFrom":makeQuery(id+"F4.opPattern","COPY",BODY,{"derivedFrom":makeQuery(id+"F1.opExtrude","SWEPT_BODY",BODY,{"disambiguationData":[OSD([sQuery(id+"F0.wireOp",EDGE,"E0")])]}),"instanceName":"1"}),"instanceName":"1"}),"instanceName":"1"}),"instanceName":"1"}),"instanceName":"1"});
            var Q136;
            Q136=makeQuery(id+"F18.opPattern","COPY",BODY,{"derivedFrom":makeQuery(id+"F17.opPattern","COPY",BODY,{"derivedFrom":makeQuery(id+"F15.opPattern","COPY",BODY,{"derivedFrom":makeQuery(id+"F11.opPattern","COPY",BODY,{"derivedFrom":makeQuery(id+"F9.opPattern","COPY",BODY,{"derivedFrom":makeQuery(id+"F4.opPattern","COPY",BODY,{"derivedFrom":makeQuery(id+"F1.opExtrude","SWEPT_BODY",BODY,{"disambiguationData":[OSD([sQuery(id+"F0.wireOp",EDGE,"E0")])]}),"instanceName":"1"}),"instanceName":"1"}),"instanceName":"1"}),"instanceName":"1"}),"instanceName":"1"}),"instanceName":"1"});
            var Q137;
            Q137=makeQuery(id+"F17.opPattern","COPY",BODY,{"derivedFrom":makeQuery(id+"F16.opPattern","COPY",BODY,{"derivedFrom":makeQuery(id+"F12.opPattern","COPY",BODY,{"derivedFrom":makeQuery(id+"F11.opPattern","COPY",BODY,{"derivedFrom":makeQuery(id+"F9.opPattern","COPY",BODY,{"derivedFrom":makeQuery(id+"F4.opPattern","COPY",BODY,{"derivedFrom":makeQuery(id+"F1.opExtrude","SWEPT_BODY",BODY,{"disambiguationData":[OSD([sQuery(id+"F0.wireOp",EDGE,"E0")])]}),"instanceName":"1"}),"instanceName":"1"}),"instanceName":"1"}),"instanceName":"1"}),"instanceName":"1"}),"instanceName":"1"});
            var Q138;
            Q138=makeQuery(id+"F17.opPattern","COPY",BODY,{"derivedFrom":makeQuery(id+"F15.opPattern","COPY",BODY,{"derivedFrom":makeQuery(id+"F11.opPattern","COPY",BODY,{"derivedFrom":makeQuery(id+"F10.opPattern","COPY",BODY,{"derivedFrom":makeQuery(id+"F1.opExtrude","SWEPT_BODY",BODY,{"disambiguationData":[OSD([sQuery(id+"F0.wireOp",EDGE,"E0")])]}),"instanceName":"1"}),"instanceName":"1"}),"instanceName":"1"}),"instanceName":"1"});
            var Q139;
            Q139=makeQuery(id+"F17.opPattern","COPY",BODY,{"derivedFrom":makeQuery(id+"F16.opPattern","COPY",BODY,{"derivedFrom":makeQuery(id+"F15.opPattern","COPY",BODY,{"derivedFrom":makeQuery(id+"F14.opPattern","COPY",BODY,{"derivedFrom":makeQuery(id+"F11.opPattern","COPY",BODY,{"derivedFrom":makeQuery(id+"F1.opExtrude","SWEPT_BODY",BODY,{"disambiguationData":[OSD([sQuery(id+"F0.wireOp",EDGE,"E0")])]}),"instanceName":"1"}),"instanceName":"1"}),"instanceName":"1"}),"instanceName":"1"}),"instanceName":"1"});
            var Q140;
            Q140=makeQuery(id+"F16.opPattern","COPY",BODY,{"derivedFrom":makeQuery(id+"F12.opPattern","COPY",BODY,{"derivedFrom":makeQuery(id+"F11.opPattern","COPY",BODY,{"derivedFrom":makeQuery(id+"F4.opPattern","COPY",BODY,{"derivedFrom":makeQuery(id+"F1.opExtrude","SWEPT_BODY",BODY,{"disambiguationData":[OSD([sQuery(id+"F0.wireOp",EDGE,"E0")])]}),"instanceName":"1"}),"instanceName":"1"}),"instanceName":"1"}),"instanceName":"1"});
            var Q141;
            Q141=makeQuery(id+"F16.opPattern","COPY",BODY,{"derivedFrom":makeQuery(id+"F12.opPattern","COPY",BODY,{"derivedFrom":makeQuery(id+"F11.opPattern","COPY",BODY,{"derivedFrom":makeQuery(id+"F9.opPattern","COPY",BODY,{"derivedFrom":makeQuery(id+"F1.opExtrude","SWEPT_BODY",BODY,{"disambiguationData":[OSD([sQuery(id+"F0.wireOp",EDGE,"E0")])]}),"instanceName":"1"}),"instanceName":"1"}),"instanceName":"1"}),"instanceName":"1"});
            var Q142;
            Q142=makeQuery(id+"F16.opPattern","COPY",BODY,{"derivedFrom":makeQuery(id+"F14.opPattern","COPY",BODY,{"derivedFrom":makeQuery(id+"F10.opPattern","COPY",BODY,{"derivedFrom":makeQuery(id+"F1.opExtrude","SWEPT_BODY",BODY,{"disambiguationData":[OSD([sQuery(id+"F0.wireOp",EDGE,"E0")])]}),"instanceName":"1"}),"instanceName":"1"}),"instanceName":"1"});
            var Q143;
            Q143=makeQuery(id+"F16.opPattern","COPY",BODY,{"derivedFrom":makeQuery(id+"F12.opPattern","COPY",BODY,{"derivedFrom":makeQuery(id+"F4.opPattern","COPY",BODY,{"derivedFrom":makeQuery(id+"F1.opExtrude","SWEPT_BODY",BODY,{"disambiguationData":[OSD([sQuery(id+"F0.wireOp",EDGE,"E0")])]}),"instanceName":"1"}),"instanceName":"1"}),"instanceName":"1"});
            var Q144;
            Q144=makeQuery(id+"F16.opPattern","COPY",BODY,{"derivedFrom":makeQuery(id+"F15.opPattern","COPY",BODY,{"derivedFrom":makeQuery(id+"F12.opPattern","COPY",BODY,{"derivedFrom":makeQuery(id+"F10.opPattern","COPY",BODY,{"derivedFrom":makeQuery(id+"F1.opExtrude","SWEPT_BODY",BODY,{"disambiguationData":[OSD([sQuery(id+"F0.wireOp",EDGE,"E0")])]}),"instanceName":"1"}),"instanceName":"1"}),"instanceName":"1"}),"instanceName":"1"});
            var Q145;
            Q145=makeQuery(id+"F17.opPattern","COPY",BODY,{"derivedFrom":makeQuery(id+"F16.opPattern","COPY",BODY,{"derivedFrom":makeQuery(id+"F14.opPattern","COPY",BODY,{"derivedFrom":makeQuery(id+"F10.opPattern","COPY",BODY,{"derivedFrom":makeQuery(id+"F1.opExtrude","SWEPT_BODY",BODY,{"disambiguationData":[OSD([sQuery(id+"F0.wireOp",EDGE,"E0")])]}),"instanceName":"1"}),"instanceName":"1"}),"instanceName":"1"}),"instanceName":"1"});
            var Q146;
            Q146=makeQuery(id+"F16.opPattern","COPY",BODY,{"derivedFrom":makeQuery(id+"F15.opPattern","COPY",BODY,{"derivedFrom":makeQuery(id+"F14.opPattern","COPY",BODY,{"derivedFrom":makeQuery(id+"F11.opPattern","COPY",BODY,{"derivedFrom":makeQuery(id+"F4.opPattern","COPY",BODY,{"derivedFrom":makeQuery(id+"F1.opExtrude","SWEPT_BODY",BODY,{"disambiguationData":[OSD([sQuery(id+"F0.wireOp",EDGE,"E0")])]}),"instanceName":"1"}),"instanceName":"1"}),"instanceName":"1"}),"instanceName":"1"}),"instanceName":"1"});
            var Q147;
            Q147=makeQuery(id+"F16.opPattern","COPY",BODY,{"derivedFrom":makeQuery(id+"F15.opPattern","COPY",BODY,{"derivedFrom":makeQuery(id+"F12.opPattern","COPY",BODY,{"derivedFrom":makeQuery(id+"F11.opPattern","COPY",BODY,{"derivedFrom":makeQuery(id+"F10.opPattern","COPY",BODY,{"derivedFrom":makeQuery(id+"F1.opExtrude","SWEPT_BODY",BODY,{"disambiguationData":[OSD([sQuery(id+"F0.wireOp",EDGE,"E0")])]}),"instanceName":"1"}),"instanceName":"1"}),"instanceName":"1"}),"instanceName":"1"}),"instanceName":"1"});
            var Q148;
            Q148=makeQuery(id+"F16.opPattern","COPY",BODY,{"derivedFrom":makeQuery(id+"F15.opPattern","COPY",BODY,{"derivedFrom":makeQuery(id+"F12.opPattern","COPY",BODY,{"derivedFrom":makeQuery(id+"F11.opPattern","COPY",BODY,{"derivedFrom":makeQuery(id+"F9.opPattern","COPY",BODY,{"derivedFrom":makeQuery(id+"F1.opExtrude","SWEPT_BODY",BODY,{"disambiguationData":[OSD([sQuery(id+"F0.wireOp",EDGE,"E0")])]}),"instanceName":"1"}),"instanceName":"1"}),"instanceName":"1"}),"instanceName":"1"}),"instanceName":"1"});
            var Q149;
            Q149=makeQuery(id+"F16.opPattern","COPY",BODY,{"derivedFrom":makeQuery(id+"F15.opPattern","COPY",BODY,{"derivedFrom":makeQuery(id+"F11.opPattern","COPY",BODY,{"derivedFrom":makeQuery(id+"F1.opExtrude","SWEPT_BODY",BODY,{"disambiguationData":[OSD([sQuery(id+"F0.wireOp",EDGE,"E0")])]}),"instanceName":"1"}),"instanceName":"1"}),"instanceName":"1"});
            var Q150;
            Q150=makeQuery(id+"F16.opPattern","COPY",BODY,{"derivedFrom":makeQuery(id+"F15.opPattern","COPY",BODY,{"derivedFrom":makeQuery(id+"F11.opPattern","COPY",BODY,{"derivedFrom":makeQuery(id+"F9.opPattern","COPY",BODY,{"derivedFrom":makeQuery(id+"F4.opPattern","COPY",BODY,{"derivedFrom":makeQuery(id+"F1.opExtrude","SWEPT_BODY",BODY,{"disambiguationData":[OSD([sQuery(id+"F0.wireOp",EDGE,"E0")])]}),"instanceName":"1"}),"instanceName":"1"}),"instanceName":"1"}),"instanceName":"1"}),"instanceName":"1"});
            var Q151;
            Q151=makeQuery(id+"F16.opPattern","COPY",BODY,{"derivedFrom":makeQuery(id+"F15.opPattern","COPY",BODY,{"derivedFrom":makeQuery(id+"F12.opPattern","COPY",BODY,{"derivedFrom":makeQuery(id+"F9.opPattern","COPY",BODY,{"derivedFrom":makeQuery(id+"F1.opExtrude","SWEPT_BODY",BODY,{"disambiguationData":[OSD([sQuery(id+"F0.wireOp",EDGE,"E0")])]}),"instanceName":"1"}),"instanceName":"1"}),"instanceName":"1"}),"instanceName":"1"});
            var Q152;
            Q152=makeQuery(id+"F16.opPattern","COPY",BODY,{"derivedFrom":makeQuery(id+"F15.opPattern","COPY",BODY,{"derivedFrom":makeQuery(id+"F9.opPattern","COPY",BODY,{"derivedFrom":makeQuery(id+"F1.opExtrude","SWEPT_BODY",BODY,{"disambiguationData":[OSD([sQuery(id+"F0.wireOp",EDGE,"E0")])]}),"instanceName":"1"}),"instanceName":"1"}),"instanceName":"1"});
            var Q153;
            Q153=makeQuery(id+"F17.opPattern","COPY",BODY,{"derivedFrom":makeQuery(id+"F16.opPattern","COPY",BODY,{"derivedFrom":makeQuery(id+"F12.opPattern","COPY",BODY,{"derivedFrom":makeQuery(id+"F4.opPattern","COPY",BODY,{"derivedFrom":makeQuery(id+"F1.opExtrude","SWEPT_BODY",BODY,{"disambiguationData":[OSD([sQuery(id+"F0.wireOp",EDGE,"E0")])]}),"instanceName":"1"}),"instanceName":"1"}),"instanceName":"1"}),"instanceName":"1"});
            var Q154;
            Q154=makeQuery(id+"F17.opPattern","COPY",BODY,{"derivedFrom":makeQuery(id+"F15.opPattern","COPY",BODY,{"derivedFrom":makeQuery(id+"F14.opPattern","COPY",BODY,{"derivedFrom":makeQuery(id+"F1.opExtrude","SWEPT_BODY",BODY,{"disambiguationData":[OSD([sQuery(id+"F0.wireOp",EDGE,"E0")])]}),"instanceName":"1"}),"instanceName":"1"}),"instanceName":"1"});
            var Q155;
            Q155=makeQuery(id+"F17.opPattern","COPY",BODY,{"derivedFrom":makeQuery(id+"F16.opPattern","COPY",BODY,{"derivedFrom":makeQuery(id+"F15.opPattern","COPY",BODY,{"derivedFrom":makeQuery(id+"F12.opPattern","COPY",BODY,{"derivedFrom":makeQuery(id+"F9.opPattern","COPY",BODY,{"derivedFrom":makeQuery(id+"F1.opExtrude","SWEPT_BODY",BODY,{"disambiguationData":[OSD([sQuery(id+"F0.wireOp",EDGE,"E0")])]}),"instanceName":"1"}),"instanceName":"1"}),"instanceName":"1"}),"instanceName":"1"}),"instanceName":"1"});
            var Q156;
            Q156=makeQuery(id+"F16.opPattern","COPY",BODY,{"derivedFrom":makeQuery(id+"F12.opPattern","COPY",BODY,{"derivedFrom":makeQuery(id+"F1.opExtrude","SWEPT_BODY",BODY,{"disambiguationData":[OSD([sQuery(id+"F0.wireOp",EDGE,"E0")])]}),"instanceName":"1"}),"instanceName":"1"});
            var Q157;
            Q157=makeQuery(id+"F16.opPattern","COPY",BODY,{"derivedFrom":makeQuery(id+"F12.opPattern","COPY",BODY,{"derivedFrom":makeQuery(id+"F9.opPattern","COPY",BODY,{"derivedFrom":makeQuery(id+"F4.opPattern","COPY",BODY,{"derivedFrom":makeQuery(id+"F1.opExtrude","SWEPT_BODY",BODY,{"disambiguationData":[OSD([sQuery(id+"F0.wireOp",EDGE,"E0")])]}),"instanceName":"1"}),"instanceName":"1"}),"instanceName":"1"}),"instanceName":"1"});
            var Q158;
            Q158=makeQuery(id+"F18.opPattern","COPY",BODY,{"derivedFrom":makeQuery(id+"F17.opPattern","COPY",BODY,{"derivedFrom":makeQuery(id+"F16.opPattern","COPY",BODY,{"derivedFrom":makeQuery(id+"F9.opPattern","COPY",BODY,{"derivedFrom":makeQuery(id+"F4.opPattern","COPY",BODY,{"derivedFrom":makeQuery(id+"F1.opExtrude","SWEPT_BODY",BODY,{"disambiguationData":[OSD([sQuery(id+"F0.wireOp",EDGE,"E0")])]}),"instanceName":"1"}),"instanceName":"1"}),"instanceName":"1"}),"instanceName":"1"}),"instanceName":"1"});
            var Q159;
            Q159=makeQuery(id+"F16.opPattern","COPY",BODY,{"derivedFrom":makeQuery(id+"F14.opPattern","COPY",BODY,{"derivedFrom":makeQuery(id+"F11.opPattern","COPY",BODY,{"derivedFrom":makeQuery(id+"F9.opPattern","COPY",BODY,{"derivedFrom":makeQuery(id+"F1.opExtrude","SWEPT_BODY",BODY,{"disambiguationData":[OSD([sQuery(id+"F0.wireOp",EDGE,"E0")])]}),"instanceName":"1"}),"instanceName":"1"}),"instanceName":"1"}),"instanceName":"1"});
            var Q160;
            Q160=makeQuery(id+"F16.opPattern","COPY",BODY,{"derivedFrom":makeQuery(id+"F15.opPattern","COPY",BODY,{"derivedFrom":makeQuery(id+"F9.opPattern","COPY",BODY,{"derivedFrom":makeQuery(id+"F4.opPattern","COPY",BODY,{"derivedFrom":makeQuery(id+"F1.opExtrude","SWEPT_BODY",BODY,{"disambiguationData":[OSD([sQuery(id+"F0.wireOp",EDGE,"E0")])]}),"instanceName":"1"}),"instanceName":"1"}),"instanceName":"1"}),"instanceName":"1"});
            var Q161;
            Q161=makeQuery(id+"F17.opPattern","COPY",BODY,{"derivedFrom":makeQuery(id+"F9.opPattern","COPY",BODY,{"derivedFrom":makeQuery(id+"F4.opPattern","COPY",BODY,{"derivedFrom":makeQuery(id+"F1.opExtrude","SWEPT_BODY",BODY,{"disambiguationData":[OSD([sQuery(id+"F0.wireOp",EDGE,"E0")])]}),"instanceName":"1"}),"instanceName":"1"}),"instanceName":"1"});
            var Q162;
            Q162=makeQuery(id+"F18.opPattern","COPY",BODY,{"derivedFrom":makeQuery(id+"F17.opPattern","COPY",BODY,{"derivedFrom":makeQuery(id+"F16.opPattern","COPY",BODY,{"derivedFrom":makeQuery(id+"F11.opPattern","COPY",BODY,{"derivedFrom":makeQuery(id+"F10.opPattern","COPY",BODY,{"derivedFrom":makeQuery(id+"F1.opExtrude","SWEPT_BODY",BODY,{"disambiguationData":[OSD([sQuery(id+"F0.wireOp",EDGE,"E0")])]}),"instanceName":"1"}),"instanceName":"1"}),"instanceName":"1"}),"instanceName":"1"}),"instanceName":"1"});
            var Q163;
            Q163=makeQuery(id+"F16.opPattern","COPY",BODY,{"derivedFrom":makeQuery(id+"F15.opPattern","COPY",BODY,{"derivedFrom":makeQuery(id+"F12.opPattern","COPY",BODY,{"derivedFrom":makeQuery(id+"F1.opExtrude","SWEPT_BODY",BODY,{"disambiguationData":[OSD([sQuery(id+"F0.wireOp",EDGE,"E0")])]}),"instanceName":"1"}),"instanceName":"1"}),"instanceName":"1"});
            var Q164;
            Q164=makeQuery(id+"F17.opPattern","COPY",BODY,{"derivedFrom":makeQuery(id+"F15.opPattern","COPY",BODY,{"derivedFrom":makeQuery(id+"F12.opPattern","COPY",BODY,{"derivedFrom":makeQuery(id+"F11.opPattern","COPY",BODY,{"derivedFrom":makeQuery(id+"F9.opPattern","COPY",BODY,{"derivedFrom":makeQuery(id+"F4.opPattern","COPY",BODY,{"derivedFrom":makeQuery(id+"F1.opExtrude","SWEPT_BODY",BODY,{"disambiguationData":[OSD([sQuery(id+"F0.wireOp",EDGE,"E0")])]}),"instanceName":"1"}),"instanceName":"1"}),"instanceName":"1"}),"instanceName":"1"}),"instanceName":"1"}),"instanceName":"1"});
            var Q165;
            Q165=makeQuery(id+"F16.opPattern","COPY",BODY,{"derivedFrom":makeQuery(id+"F15.opPattern","COPY",BODY,{"derivedFrom":makeQuery(id+"F12.opPattern","COPY",BODY,{"derivedFrom":makeQuery(id+"F9.opPattern","COPY",BODY,{"derivedFrom":makeQuery(id+"F4.opPattern","COPY",BODY,{"derivedFrom":makeQuery(id+"F1.opExtrude","SWEPT_BODY",BODY,{"disambiguationData":[OSD([sQuery(id+"F0.wireOp",EDGE,"E0")])]}),"instanceName":"1"}),"instanceName":"1"}),"instanceName":"1"}),"instanceName":"1"}),"instanceName":"1"});
            var Q166;
            Q166=makeQuery(id+"F17.opPattern","COPY",BODY,{"derivedFrom":makeQuery(id+"F14.opPattern","COPY",BODY,{"derivedFrom":makeQuery(id+"F11.opPattern","COPY",BODY,{"derivedFrom":makeQuery(id+"F10.opPattern","COPY",BODY,{"derivedFrom":makeQuery(id+"F1.opExtrude","SWEPT_BODY",BODY,{"disambiguationData":[OSD([sQuery(id+"F0.wireOp",EDGE,"E0")])]}),"instanceName":"1"}),"instanceName":"1"}),"instanceName":"1"}),"instanceName":"1"});
            var Q167;
            Q167=makeQuery(id+"F16.opPattern","COPY",BODY,{"derivedFrom":makeQuery(id+"F15.opPattern","COPY",BODY,{"derivedFrom":makeQuery(id+"F4.opPattern","COPY",BODY,{"derivedFrom":makeQuery(id+"F1.opExtrude","SWEPT_BODY",BODY,{"disambiguationData":[OSD([sQuery(id+"F0.wireOp",EDGE,"E0")])]}),"instanceName":"1"}),"instanceName":"1"}),"instanceName":"1"});
            var Q168;
            Q168=makeQuery(id+"F17.opPattern","COPY",BODY,{"derivedFrom":makeQuery(id+"F14.opPattern","COPY",BODY,{"derivedFrom":makeQuery(id+"F11.opPattern","COPY",BODY,{"derivedFrom":makeQuery(id+"F9.opPattern","COPY",BODY,{"derivedFrom":makeQuery(id+"F1.opExtrude","SWEPT_BODY",BODY,{"disambiguationData":[OSD([sQuery(id+"F0.wireOp",EDGE,"E0")])]}),"instanceName":"1"}),"instanceName":"1"}),"instanceName":"1"}),"instanceName":"1"});
            var Q169;
            Q169=makeQuery(id+"F17.opPattern","COPY",BODY,{"derivedFrom":makeQuery(id+"F16.opPattern","COPY",BODY,{"derivedFrom":makeQuery(id+"F12.opPattern","COPY",BODY,{"derivedFrom":makeQuery(id+"F11.opPattern","COPY",BODY,{"derivedFrom":makeQuery(id+"F10.opPattern","COPY",BODY,{"derivedFrom":makeQuery(id+"F1.opExtrude","SWEPT_BODY",BODY,{"disambiguationData":[OSD([sQuery(id+"F0.wireOp",EDGE,"E0")])]}),"instanceName":"1"}),"instanceName":"1"}),"instanceName":"1"}),"instanceName":"1"}),"instanceName":"1"});
            var Q170;
            Q170=makeQuery(id+"F16.opPattern","COPY",BODY,{"derivedFrom":makeQuery(id+"F10.opPattern","COPY",BODY,{"derivedFrom":makeQuery(id+"F1.opExtrude","SWEPT_BODY",BODY,{"disambiguationData":[OSD([sQuery(id+"F0.wireOp",EDGE,"E0")])]}),"instanceName":"1"}),"instanceName":"1"});
            var Q171;
            Q171=makeQuery(id+"F17.opPattern","COPY",BODY,{"derivedFrom":makeQuery(id+"F16.opPattern","COPY",BODY,{"derivedFrom":makeQuery(id+"F15.opPattern","COPY",BODY,{"derivedFrom":makeQuery(id+"F12.opPattern","COPY",BODY,{"derivedFrom":makeQuery(id+"F11.opPattern","COPY",BODY,{"derivedFrom":makeQuery(id+"F10.opPattern","COPY",BODY,{"derivedFrom":makeQuery(id+"F1.opExtrude","SWEPT_BODY",BODY,{"disambiguationData":[OSD([sQuery(id+"F0.wireOp",EDGE,"E0")])]}),"instanceName":"1"}),"instanceName":"1"}),"instanceName":"1"}),"instanceName":"1"}),"instanceName":"1"}),"instanceName":"1"});
            var Q172;
            Q172=makeQuery(id+"F17.opPattern","COPY",BODY,{"derivedFrom":makeQuery(id+"F16.opPattern","COPY",BODY,{"derivedFrom":makeQuery(id+"F15.opPattern","COPY",BODY,{"derivedFrom":makeQuery(id+"F14.opPattern","COPY",BODY,{"derivedFrom":makeQuery(id+"F11.opPattern","COPY",BODY,{"derivedFrom":makeQuery(id+"F4.opPattern","COPY",BODY,{"derivedFrom":makeQuery(id+"F1.opExtrude","SWEPT_BODY",BODY,{"disambiguationData":[OSD([sQuery(id+"F0.wireOp",EDGE,"E0")])]}),"instanceName":"1"}),"instanceName":"1"}),"instanceName":"1"}),"instanceName":"1"}),"instanceName":"1"}),"instanceName":"1"});
            var Q173;
            Q173=makeQuery(id+"F16.opPattern","COPY",BODY,{"derivedFrom":makeQuery(id+"F15.opPattern","COPY",BODY,{"derivedFrom":makeQuery(id+"F14.opPattern","COPY",BODY,{"derivedFrom":makeQuery(id+"F11.opPattern","COPY",BODY,{"derivedFrom":makeQuery(id+"F10.opPattern","COPY",BODY,{"derivedFrom":makeQuery(id+"F1.opExtrude","SWEPT_BODY",BODY,{"disambiguationData":[OSD([sQuery(id+"F0.wireOp",EDGE,"E0")])]}),"instanceName":"1"}),"instanceName":"1"}),"instanceName":"1"}),"instanceName":"1"}),"instanceName":"1"});
            var Q174;
            Q174=makeQuery(id+"F16.opPattern","COPY",BODY,{"derivedFrom":makeQuery(id+"F14.opPattern","COPY",BODY,{"derivedFrom":makeQuery(id+"F4.opPattern","COPY",BODY,{"derivedFrom":makeQuery(id+"F1.opExtrude","SWEPT_BODY",BODY,{"disambiguationData":[OSD([sQuery(id+"F0.wireOp",EDGE,"E0")])]}),"instanceName":"1"}),"instanceName":"1"}),"instanceName":"1"});
            var Q175;
            Q175=makeQuery(id+"F16.opPattern","COPY",BODY,{"derivedFrom":makeQuery(id+"F14.opPattern","COPY",BODY,{"derivedFrom":makeQuery(id+"F11.opPattern","COPY",BODY,{"derivedFrom":makeQuery(id+"F1.opExtrude","SWEPT_BODY",BODY,{"disambiguationData":[OSD([sQuery(id+"F0.wireOp",EDGE,"E0")])]}),"instanceName":"1"}),"instanceName":"1"}),"instanceName":"1"});
            var Q176;
            Q176=makeQuery(id+"F16.opPattern","COPY",BODY,{"derivedFrom":makeQuery(id+"F15.opPattern","COPY",BODY,{"derivedFrom":makeQuery(id+"F14.opPattern","COPY",BODY,{"derivedFrom":makeQuery(id+"F11.opPattern","COPY",BODY,{"derivedFrom":makeQuery(id+"F1.opExtrude","SWEPT_BODY",BODY,{"disambiguationData":[OSD([sQuery(id+"F0.wireOp",EDGE,"E0")])]}),"instanceName":"1"}),"instanceName":"1"}),"instanceName":"1"}),"instanceName":"1"});
            var Q177;
            Q177=makeQuery(id+"F16.opPattern","COPY",BODY,{"derivedFrom":makeQuery(id+"F15.opPattern","COPY",BODY,{"derivedFrom":makeQuery(id+"F14.opPattern","COPY",BODY,{"derivedFrom":makeQuery(id+"F11.opPattern","COPY",BODY,{"derivedFrom":makeQuery(id+"F9.opPattern","COPY",BODY,{"derivedFrom":makeQuery(id+"F4.opPattern","COPY",BODY,{"derivedFrom":makeQuery(id+"F1.opExtrude","SWEPT_BODY",BODY,{"disambiguationData":[OSD([sQuery(id+"F0.wireOp",EDGE,"E0")])]}),"instanceName":"1"}),"instanceName":"1"}),"instanceName":"1"}),"instanceName":"1"}),"instanceName":"1"}),"instanceName":"1"});
            var Q178;
            Q178=makeQuery(id+"F16.opPattern","COPY",BODY,{"derivedFrom":makeQuery(id+"F15.opPattern","COPY",BODY,{"derivedFrom":makeQuery(id+"F11.opPattern","COPY",BODY,{"derivedFrom":makeQuery(id+"F4.opPattern","COPY",BODY,{"derivedFrom":makeQuery(id+"F1.opExtrude","SWEPT_BODY",BODY,{"disambiguationData":[OSD([sQuery(id+"F0.wireOp",EDGE,"E0")])]}),"instanceName":"1"}),"instanceName":"1"}),"instanceName":"1"}),"instanceName":"1"});
            var Q179;
            Q179=makeQuery(id+"F16.opPattern","COPY",BODY,{"derivedFrom":makeQuery(id+"F15.opPattern","COPY",BODY,{"derivedFrom":makeQuery(id+"F11.opPattern","COPY",BODY,{"derivedFrom":makeQuery(id+"F9.opPattern","COPY",BODY,{"derivedFrom":makeQuery(id+"F1.opExtrude","SWEPT_BODY",BODY,{"disambiguationData":[OSD([sQuery(id+"F0.wireOp",EDGE,"E0")])]}),"instanceName":"1"}),"instanceName":"1"}),"instanceName":"1"}),"instanceName":"1"});
            var Q180;
            Q180=makeQuery(id+"F16.opPattern","COPY",BODY,{"derivedFrom":makeQuery(id+"F12.opPattern","COPY",BODY,{"derivedFrom":makeQuery(id+"F11.opPattern","COPY",BODY,{"derivedFrom":makeQuery(id+"F1.opExtrude","SWEPT_BODY",BODY,{"disambiguationData":[OSD([sQuery(id+"F0.wireOp",EDGE,"E0")])]}),"instanceName":"1"}),"instanceName":"1"}),"instanceName":"1"});
            var Q181;
            Q181=makeQuery(id+"F16.opPattern","COPY",BODY,{"derivedFrom":makeQuery(id+"F12.opPattern","COPY",BODY,{"derivedFrom":makeQuery(id+"F11.opPattern","COPY",BODY,{"derivedFrom":makeQuery(id+"F9.opPattern","COPY",BODY,{"derivedFrom":makeQuery(id+"F4.opPattern","COPY",BODY,{"derivedFrom":makeQuery(id+"F1.opExtrude","SWEPT_BODY",BODY,{"disambiguationData":[OSD([sQuery(id+"F0.wireOp",EDGE,"E0")])]}),"instanceName":"1"}),"instanceName":"1"}),"instanceName":"1"}),"instanceName":"1"}),"instanceName":"1"});
            var Q182;
            Q182=makeQuery(id+"F16.opPattern","COPY",BODY,{"derivedFrom":makeQuery(id+"F11.opPattern","COPY",BODY,{"derivedFrom":makeQuery(id+"F4.opPattern","COPY",BODY,{"derivedFrom":makeQuery(id+"F1.opExtrude","SWEPT_BODY",BODY,{"disambiguationData":[OSD([sQuery(id+"F0.wireOp",EDGE,"E0")])]}),"instanceName":"1"}),"instanceName":"1"}),"instanceName":"1"});
            var Q183;
            Q183=makeQuery(id+"F17.opPattern","COPY",BODY,{"derivedFrom":makeQuery(id+"F15.opPattern","COPY",BODY,{"derivedFrom":makeQuery(id+"F10.opPattern","COPY",BODY,{"derivedFrom":makeQuery(id+"F1.opExtrude","SWEPT_BODY",BODY,{"disambiguationData":[OSD([sQuery(id+"F0.wireOp",EDGE,"E0")])]}),"instanceName":"1"}),"instanceName":"1"}),"instanceName":"1"});
            var Q184;
            Q184=makeQuery(id+"F17.opPattern","COPY",BODY,{"derivedFrom":makeQuery(id+"F14.opPattern","COPY",BODY,{"derivedFrom":makeQuery(id+"F4.opPattern","COPY",BODY,{"derivedFrom":makeQuery(id+"F1.opExtrude","SWEPT_BODY",BODY,{"disambiguationData":[OSD([sQuery(id+"F0.wireOp",EDGE,"E0")])]}),"instanceName":"1"}),"instanceName":"1"}),"instanceName":"1"});
            var Q185;
            Q185=makeQuery(id+"F17.opPattern","COPY",BODY,{"derivedFrom":makeQuery(id+"F9.opPattern","COPY",BODY,{"derivedFrom":makeQuery(id+"F1.opExtrude","SWEPT_BODY",BODY,{"disambiguationData":[OSD([sQuery(id+"F0.wireOp",EDGE,"E0")])]}),"instanceName":"1"}),"instanceName":"1"});
            var Q186;
            Q186=makeQuery(id+"F17.opPattern","COPY",BODY,{"derivedFrom":makeQuery(id+"F16.opPattern","COPY",BODY,{"derivedFrom":makeQuery(id+"F15.opPattern","COPY",BODY,{"derivedFrom":makeQuery(id+"F4.opPattern","COPY",BODY,{"derivedFrom":makeQuery(id+"F1.opExtrude","SWEPT_BODY",BODY,{"disambiguationData":[OSD([sQuery(id+"F0.wireOp",EDGE,"E0")])]}),"instanceName":"1"}),"instanceName":"1"}),"instanceName":"1"}),"instanceName":"1"});
            var Q187;
            Q187=makeQuery(id+"F16.opPattern","COPY",BODY,{"derivedFrom":makeQuery(id+"F15.opPattern","COPY",BODY,{"derivedFrom":makeQuery(id+"F12.opPattern","COPY",BODY,{"derivedFrom":makeQuery(id+"F11.opPattern","COPY",BODY,{"derivedFrom":makeQuery(id+"F4.opPattern","COPY",BODY,{"derivedFrom":makeQuery(id+"F1.opExtrude","SWEPT_BODY",BODY,{"disambiguationData":[OSD([sQuery(id+"F0.wireOp",EDGE,"E0")])]}),"instanceName":"1"}),"instanceName":"1"}),"instanceName":"1"}),"instanceName":"1"}),"instanceName":"1"});
            var Q188;
            Q188=makeQuery(id+"F18.opPattern","COPY",BODY,{"derivedFrom":makeQuery(id+"F17.opPattern","COPY",BODY,{"derivedFrom":makeQuery(id+"F16.opPattern","COPY",BODY,{"derivedFrom":makeQuery(id+"F1.opExtrude","SWEPT_BODY",BODY,{"disambiguationData":[OSD([sQuery(id+"F0.wireOp",EDGE,"E0")])]}),"instanceName":"1"}),"instanceName":"1"}),"instanceName":"1"});
            var Q189;
            Q189=makeQuery(id+"F16.opPattern","COPY",BODY,{"derivedFrom":makeQuery(id+"F11.opPattern","COPY",BODY,{"derivedFrom":makeQuery(id+"F10.opPattern","COPY",BODY,{"derivedFrom":makeQuery(id+"F1.opExtrude","SWEPT_BODY",BODY,{"disambiguationData":[OSD([sQuery(id+"F0.wireOp",EDGE,"E0")])]}),"instanceName":"1"}),"instanceName":"1"}),"instanceName":"1"});
            var Q190;
            Q190=makeQuery(id+"F16.opPattern","COPY",BODY,{"derivedFrom":makeQuery(id+"F15.opPattern","COPY",BODY,{"derivedFrom":makeQuery(id+"F1.opExtrude","SWEPT_BODY",BODY,{"disambiguationData":[OSD([sQuery(id+"F0.wireOp",EDGE,"E0")])]}),"instanceName":"1"}),"instanceName":"1"});
            var Q191;
            Q191=makeQuery(id+"F16.opPattern","COPY",BODY,{"derivedFrom":makeQuery(id+"F12.opPattern","COPY",BODY,{"derivedFrom":makeQuery(id+"F9.opPattern","COPY",BODY,{"derivedFrom":makeQuery(id+"F1.opExtrude","SWEPT_BODY",BODY,{"disambiguationData":[OSD([sQuery(id+"F0.wireOp",EDGE,"E0")])]}),"instanceName":"1"}),"instanceName":"1"}),"instanceName":"1"});
            var Q192;
            Q192=makeQuery(id+"F18.opPattern","COPY",BODY,{"derivedFrom":makeQuery(id+"F16.opPattern","COPY",BODY,{"derivedFrom":makeQuery(id+"F15.opPattern","COPY",BODY,{"derivedFrom":makeQuery(id+"F14.opPattern","COPY",BODY,{"derivedFrom":makeQuery(id+"F11.opPattern","COPY",BODY,{"derivedFrom":makeQuery(id+"F10.opPattern","COPY",BODY,{"derivedFrom":makeQuery(id+"F1.opExtrude","SWEPT_BODY",BODY,{"disambiguationData":[OSD([sQuery(id+"F0.wireOp",EDGE,"E0")])]}),"instanceName":"1"}),"instanceName":"1"}),"instanceName":"1"}),"instanceName":"1"}),"instanceName":"1"}),"instanceName":"1"});
            var Q193;
            Q193=makeQuery(id+"F18.opPattern","COPY",BODY,{"derivedFrom":makeQuery(id+"F16.opPattern","COPY",BODY,{"derivedFrom":makeQuery(id+"F15.opPattern","COPY",BODY,{"derivedFrom":makeQuery(id+"F14.opPattern","COPY",BODY,{"derivedFrom":makeQuery(id+"F1.opExtrude","SWEPT_BODY",BODY,{"disambiguationData":[OSD([sQuery(id+"F0.wireOp",EDGE,"E0")])]}),"instanceName":"1"}),"instanceName":"1"}),"instanceName":"1"}),"instanceName":"1"});
            var Q194;
            Q194=makeQuery(id+"F18.opPattern","COPY",BODY,{"derivedFrom":makeQuery(id+"F16.opPattern","COPY",BODY,{"derivedFrom":makeQuery(id+"F15.opPattern","COPY",BODY,{"derivedFrom":makeQuery(id+"F14.opPattern","COPY",BODY,{"derivedFrom":makeQuery(id+"F11.opPattern","COPY",BODY,{"derivedFrom":makeQuery(id+"F9.opPattern","COPY",BODY,{"derivedFrom":makeQuery(id+"F1.opExtrude","SWEPT_BODY",BODY,{"disambiguationData":[OSD([sQuery(id+"F0.wireOp",EDGE,"E0")])]}),"instanceName":"1"}),"instanceName":"1"}),"instanceName":"1"}),"instanceName":"1"}),"instanceName":"1"}),"instanceName":"1"});
            var Q195;
            Q195=makeQuery(id+"F18.opPattern","COPY",BODY,{"derivedFrom":makeQuery(id+"F16.opPattern","COPY",BODY,{"derivedFrom":makeQuery(id+"F15.opPattern","COPY",BODY,{"derivedFrom":makeQuery(id+"F11.opPattern","COPY",BODY,{"derivedFrom":makeQuery(id+"F10.opPattern","COPY",BODY,{"derivedFrom":makeQuery(id+"F1.opExtrude","SWEPT_BODY",BODY,{"disambiguationData":[OSD([sQuery(id+"F0.wireOp",EDGE,"E0")])]}),"instanceName":"1"}),"instanceName":"1"}),"instanceName":"1"}),"instanceName":"1"}),"instanceName":"1"});
            var Q196;
            Q196=makeQuery(id+"F18.opPattern","COPY",BODY,{"derivedFrom":makeQuery(id+"F16.opPattern","COPY",BODY,{"derivedFrom":makeQuery(id+"F15.opPattern","COPY",BODY,{"derivedFrom":makeQuery(id+"F12.opPattern","COPY",BODY,{"derivedFrom":makeQuery(id+"F11.opPattern","COPY",BODY,{"derivedFrom":makeQuery(id+"F4.opPattern","COPY",BODY,{"derivedFrom":makeQuery(id+"F1.opExtrude","SWEPT_BODY",BODY,{"disambiguationData":[OSD([sQuery(id+"F0.wireOp",EDGE,"E0")])]}),"instanceName":"1"}),"instanceName":"1"}),"instanceName":"1"}),"instanceName":"1"}),"instanceName":"1"}),"instanceName":"1"});
            var Q197;
            Q197=makeQuery(id+"F18.opPattern","COPY",BODY,{"derivedFrom":makeQuery(id+"F16.opPattern","COPY",BODY,{"derivedFrom":makeQuery(id+"F14.opPattern","COPY",BODY,{"derivedFrom":makeQuery(id+"F11.opPattern","COPY",BODY,{"derivedFrom":makeQuery(id+"F4.opPattern","COPY",BODY,{"derivedFrom":makeQuery(id+"F1.opExtrude","SWEPT_BODY",BODY,{"disambiguationData":[OSD([sQuery(id+"F0.wireOp",EDGE,"E0")])]}),"instanceName":"1"}),"instanceName":"1"}),"instanceName":"1"}),"instanceName":"1"}),"instanceName":"1"});
            var Q198;
            Q198=makeQuery(id+"F18.opPattern","COPY",BODY,{"derivedFrom":makeQuery(id+"F16.opPattern","COPY",BODY,{"derivedFrom":makeQuery(id+"F14.opPattern","COPY",BODY,{"derivedFrom":makeQuery(id+"F11.opPattern","COPY",BODY,{"derivedFrom":makeQuery(id+"F9.opPattern","COPY",BODY,{"derivedFrom":makeQuery(id+"F1.opExtrude","SWEPT_BODY",BODY,{"disambiguationData":[OSD([sQuery(id+"F0.wireOp",EDGE,"E0")])]}),"instanceName":"1"}),"instanceName":"1"}),"instanceName":"1"}),"instanceName":"1"}),"instanceName":"1"});
            var Q199;
            Q199=makeQuery(id+"F18.opPattern","COPY",BODY,{"derivedFrom":makeQuery(id+"F16.opPattern","COPY",BODY,{"derivedFrom":makeQuery(id+"F12.opPattern","COPY",BODY,{"derivedFrom":makeQuery(id+"F10.opPattern","COPY",BODY,{"derivedFrom":makeQuery(id+"F1.opExtrude","SWEPT_BODY",BODY,{"disambiguationData":[OSD([sQuery(id+"F0.wireOp",EDGE,"E0")])]}),"instanceName":"1"}),"instanceName":"1"}),"instanceName":"1"}),"instanceName":"1"});
            var Q200;
            Q200=makeQuery(id+"F17.opPattern","COPY",BODY,{"derivedFrom":makeQuery(id+"F16.opPattern","COPY",BODY,{"derivedFrom":makeQuery(id+"F15.opPattern","COPY",BODY,{"derivedFrom":makeQuery(id+"F14.opPattern","COPY",BODY,{"derivedFrom":makeQuery(id+"F11.opPattern","COPY",BODY,{"derivedFrom":makeQuery(id+"F9.opPattern","COPY",BODY,{"derivedFrom":makeQuery(id+"F4.opPattern","COPY",BODY,{"derivedFrom":makeQuery(id+"F1.opExtrude","SWEPT_BODY",BODY,{"disambiguationData":[OSD([sQuery(id+"F0.wireOp",EDGE,"E0")])]}),"instanceName":"1"}),"instanceName":"1"}),"instanceName":"1"}),"instanceName":"1"}),"instanceName":"1"}),"instanceName":"1"}),"instanceName":"1"});
            var Q201;
            Q201=makeQuery(id+"F18.opPattern","COPY",BODY,{"derivedFrom":makeQuery(id+"F16.opPattern","COPY",BODY,{"derivedFrom":makeQuery(id+"F12.opPattern","COPY",BODY,{"derivedFrom":makeQuery(id+"F9.opPattern","COPY",BODY,{"derivedFrom":makeQuery(id+"F1.opExtrude","SWEPT_BODY",BODY,{"disambiguationData":[OSD([sQuery(id+"F0.wireOp",EDGE,"E0")])]}),"instanceName":"1"}),"instanceName":"1"}),"instanceName":"1"}),"instanceName":"1"});
            var Q202;
            Q202=makeQuery(id+"F18.opPattern","COPY",BODY,{"derivedFrom":makeQuery(id+"F17.opPattern","COPY",BODY,{"derivedFrom":makeQuery(id+"F12.opPattern","COPY",BODY,{"derivedFrom":makeQuery(id+"F11.opPattern","COPY",BODY,{"derivedFrom":makeQuery(id+"F4.opPattern","COPY",BODY,{"derivedFrom":makeQuery(id+"F1.opExtrude","SWEPT_BODY",BODY,{"disambiguationData":[OSD([sQuery(id+"F0.wireOp",EDGE,"E0")])]}),"instanceName":"1"}),"instanceName":"1"}),"instanceName":"1"}),"instanceName":"1"}),"instanceName":"1"});
            var Q203;
            Q203=makeQuery(id+"F18.opPattern","COPY",BODY,{"derivedFrom":makeQuery(id+"F17.opPattern","COPY",BODY,{"derivedFrom":makeQuery(id+"F12.opPattern","COPY",BODY,{"derivedFrom":makeQuery(id+"F11.opPattern","COPY",BODY,{"derivedFrom":makeQuery(id+"F9.opPattern","COPY",BODY,{"derivedFrom":makeQuery(id+"F1.opExtrude","SWEPT_BODY",BODY,{"disambiguationData":[OSD([sQuery(id+"F0.wireOp",EDGE,"E0")])]}),"instanceName":"1"}),"instanceName":"1"}),"instanceName":"1"}),"instanceName":"1"}),"instanceName":"1"});
            var Q204;
            Q204=makeQuery(id+"F18.opPattern","COPY",BODY,{"derivedFrom":makeQuery(id+"F17.opPattern","COPY",BODY,{"derivedFrom":makeQuery(id+"F14.opPattern","COPY",BODY,{"derivedFrom":makeQuery(id+"F10.opPattern","COPY",BODY,{"derivedFrom":makeQuery(id+"F1.opExtrude","SWEPT_BODY",BODY,{"disambiguationData":[OSD([sQuery(id+"F0.wireOp",EDGE,"E0")])]}),"instanceName":"1"}),"instanceName":"1"}),"instanceName":"1"}),"instanceName":"1"});
            var Q205;
            Q205=makeQuery(id+"F18.opPattern","COPY",BODY,{"derivedFrom":makeQuery(id+"F15.opPattern","COPY",BODY,{"derivedFrom":makeQuery(id+"F14.opPattern","COPY",BODY,{"derivedFrom":makeQuery(id+"F11.opPattern","COPY",BODY,{"derivedFrom":makeQuery(id+"F10.opPattern","COPY",BODY,{"derivedFrom":makeQuery(id+"F1.opExtrude","SWEPT_BODY",BODY,{"disambiguationData":[OSD([sQuery(id+"F0.wireOp",EDGE,"E0")])]}),"instanceName":"1"}),"instanceName":"1"}),"instanceName":"1"}),"instanceName":"1"}),"instanceName":"1"});
            var Q206;
            Q206=makeQuery(id+"F18.opPattern","COPY",BODY,{"derivedFrom":makeQuery(id+"F17.opPattern","COPY",BODY,{"derivedFrom":makeQuery(id+"F15.opPattern","COPY",BODY,{"derivedFrom":makeQuery(id+"F11.opPattern","COPY",BODY,{"derivedFrom":makeQuery(id+"F1.opExtrude","SWEPT_BODY",BODY,{"disambiguationData":[OSD([sQuery(id+"F0.wireOp",EDGE,"E0")])]}),"instanceName":"1"}),"instanceName":"1"}),"instanceName":"1"}),"instanceName":"1"});
            var Q207;
            Q207=makeQuery(id+"F18.opPattern","COPY",BODY,{"derivedFrom":makeQuery(id+"F17.opPattern","COPY",BODY,{"derivedFrom":makeQuery(id+"F12.opPattern","COPY",BODY,{"derivedFrom":makeQuery(id+"F4.opPattern","COPY",BODY,{"derivedFrom":makeQuery(id+"F1.opExtrude","SWEPT_BODY",BODY,{"disambiguationData":[OSD([sQuery(id+"F0.wireOp",EDGE,"E0")])]}),"instanceName":"1"}),"instanceName":"1"}),"instanceName":"1"}),"instanceName":"1"});
            var Q208;
            Q208=makeQuery(id+"F18.opPattern","COPY",BODY,{"derivedFrom":makeQuery(id+"F14.opPattern","COPY",BODY,{"derivedFrom":makeQuery(id+"F11.opPattern","COPY",BODY,{"derivedFrom":makeQuery(id+"F9.opPattern","COPY",BODY,{"derivedFrom":makeQuery(id+"F4.opPattern","COPY",BODY,{"derivedFrom":makeQuery(id+"F1.opExtrude","SWEPT_BODY",BODY,{"disambiguationData":[OSD([sQuery(id+"F0.wireOp",EDGE,"E0")])]}),"instanceName":"1"}),"instanceName":"1"}),"instanceName":"1"}),"instanceName":"1"}),"instanceName":"1"});
            var Q209;
            Q209=makeQuery(id+"F18.opPattern","COPY",BODY,{"derivedFrom":makeQuery(id+"F15.opPattern","COPY",BODY,{"derivedFrom":makeQuery(id+"F1.opExtrude","SWEPT_BODY",BODY,{"disambiguationData":[OSD([sQuery(id+"F0.wireOp",EDGE,"E0")])]}),"instanceName":"1"}),"instanceName":"1"});
            var Q210;
            Q210=makeQuery(id+"F18.opPattern","COPY",BODY,{"derivedFrom":makeQuery(id+"F14.opPattern","COPY",BODY,{"derivedFrom":makeQuery(id+"F11.opPattern","COPY",BODY,{"derivedFrom":makeQuery(id+"F4.opPattern","COPY",BODY,{"derivedFrom":makeQuery(id+"F1.opExtrude","SWEPT_BODY",BODY,{"disambiguationData":[OSD([sQuery(id+"F0.wireOp",EDGE,"E0")])]}),"instanceName":"1"}),"instanceName":"1"}),"instanceName":"1"}),"instanceName":"1"});
            var Q211;
            Q211=makeQuery(id+"F18.opPattern","COPY",BODY,{"derivedFrom":makeQuery(id+"F14.opPattern","COPY",BODY,{"derivedFrom":makeQuery(id+"F1.opExtrude","SWEPT_BODY",BODY,{"disambiguationData":[OSD([sQuery(id+"F0.wireOp",EDGE,"E0")])]}),"instanceName":"1"}),"instanceName":"1"});
            var Q212;
            Q212=makeQuery(id+"F18.opPattern","COPY",BODY,{"derivedFrom":makeQuery(id+"F11.opPattern","COPY",BODY,{"derivedFrom":makeQuery(id+"F9.opPattern","COPY",BODY,{"derivedFrom":makeQuery(id+"F4.opPattern","COPY",BODY,{"derivedFrom":makeQuery(id+"F1.opExtrude","SWEPT_BODY",BODY,{"disambiguationData":[OSD([sQuery(id+"F0.wireOp",EDGE,"E0")])]}),"instanceName":"1"}),"instanceName":"1"}),"instanceName":"1"}),"instanceName":"1"});
            var Q213;
            Q213=makeQuery(id+"F18.opPattern","COPY",BODY,{"derivedFrom":makeQuery(id+"F12.opPattern","COPY",BODY,{"derivedFrom":makeQuery(id+"F1.opExtrude","SWEPT_BODY",BODY,{"disambiguationData":[OSD([sQuery(id+"F0.wireOp",EDGE,"E0")])]}),"instanceName":"1"}),"instanceName":"1"});
            var Q214;
            Q214=makeQuery(id+"F18.opPattern","COPY",BODY,{"derivedFrom":makeQuery(id+"F12.opPattern","COPY",BODY,{"derivedFrom":makeQuery(id+"F9.opPattern","COPY",BODY,{"derivedFrom":makeQuery(id+"F1.opExtrude","SWEPT_BODY",BODY,{"disambiguationData":[OSD([sQuery(id+"F0.wireOp",EDGE,"E0")])]}),"instanceName":"1"}),"instanceName":"1"}),"instanceName":"1"});
            var Q215;
            Q215=makeQuery(id+"F16.opPattern","COPY",BODY,{"derivedFrom":makeQuery(id+"F15.opPattern","COPY",BODY,{"derivedFrom":makeQuery(id+"F14.opPattern","COPY",BODY,{"derivedFrom":makeQuery(id+"F11.opPattern","COPY",BODY,{"derivedFrom":makeQuery(id+"F9.opPattern","COPY",BODY,{"derivedFrom":makeQuery(id+"F1.opExtrude","SWEPT_BODY",BODY,{"disambiguationData":[OSD([sQuery(id+"F0.wireOp",EDGE,"E0")])]}),"instanceName":"1"}),"instanceName":"1"}),"instanceName":"1"}),"instanceName":"1"}),"instanceName":"1"});
            var Q216;
            Q216=makeQuery(id+"F18.opPattern","COPY",BODY,{"derivedFrom":makeQuery(id+"F16.opPattern","COPY",BODY,{"derivedFrom":makeQuery(id+"F11.opPattern","COPY",BODY,{"derivedFrom":makeQuery(id+"F1.opExtrude","SWEPT_BODY",BODY,{"disambiguationData":[OSD([sQuery(id+"F0.wireOp",EDGE,"E0")])]}),"instanceName":"1"}),"instanceName":"1"}),"instanceName":"1"});
            var Q217;
            Q217=makeQuery(id+"F18.opPattern","COPY",BODY,{"derivedFrom":makeQuery(id+"F16.opPattern","COPY",BODY,{"derivedFrom":makeQuery(id+"F11.opPattern","COPY",BODY,{"derivedFrom":makeQuery(id+"F9.opPattern","COPY",BODY,{"derivedFrom":makeQuery(id+"F4.opPattern","COPY",BODY,{"derivedFrom":makeQuery(id+"F1.opExtrude","SWEPT_BODY",BODY,{"disambiguationData":[OSD([sQuery(id+"F0.wireOp",EDGE,"E0")])]}),"instanceName":"1"}),"instanceName":"1"}),"instanceName":"1"}),"instanceName":"1"}),"instanceName":"1"});
            var Q218;
            Q218=makeQuery(id+"F18.opPattern","COPY",BODY,{"derivedFrom":makeQuery(id+"F17.opPattern","COPY",BODY,{"derivedFrom":makeQuery(id+"F14.opPattern","COPY",BODY,{"derivedFrom":makeQuery(id+"F11.opPattern","COPY",BODY,{"derivedFrom":makeQuery(id+"F9.opPattern","COPY",BODY,{"derivedFrom":makeQuery(id+"F4.opPattern","COPY",BODY,{"derivedFrom":makeQuery(id+"F1.opExtrude","SWEPT_BODY",BODY,{"disambiguationData":[OSD([sQuery(id+"F0.wireOp",EDGE,"E0")])]}),"instanceName":"1"}),"instanceName":"1"}),"instanceName":"1"}),"instanceName":"1"}),"instanceName":"1"}),"instanceName":"1"});
            var Q219;
            Q219=makeQuery(id+"F18.opPattern","COPY",BODY,{"derivedFrom":makeQuery(id+"F15.opPattern","COPY",BODY,{"derivedFrom":makeQuery(id+"F14.opPattern","COPY",BODY,{"derivedFrom":makeQuery(id+"F11.opPattern","COPY",BODY,{"derivedFrom":makeQuery(id+"F4.opPattern","COPY",BODY,{"derivedFrom":makeQuery(id+"F1.opExtrude","SWEPT_BODY",BODY,{"disambiguationData":[OSD([sQuery(id+"F0.wireOp",EDGE,"E0")])]}),"instanceName":"1"}),"instanceName":"1"}),"instanceName":"1"}),"instanceName":"1"}),"instanceName":"1"});
            var Q220;
            Q220=makeQuery(id+"F18.opPattern","COPY",BODY,{"derivedFrom":makeQuery(id+"F16.opPattern","COPY",BODY,{"derivedFrom":makeQuery(id+"F1.opExtrude","SWEPT_BODY",BODY,{"disambiguationData":[OSD([sQuery(id+"F0.wireOp",EDGE,"E0")])]}),"instanceName":"1"}),"instanceName":"1"});
            var Q221;
            Q221=makeQuery(id+"F18.opPattern","COPY",BODY,{"derivedFrom":makeQuery(id+"F16.opPattern","COPY",BODY,{"derivedFrom":makeQuery(id+"F9.opPattern","COPY",BODY,{"derivedFrom":makeQuery(id+"F4.opPattern","COPY",BODY,{"derivedFrom":makeQuery(id+"F1.opExtrude","SWEPT_BODY",BODY,{"disambiguationData":[OSD([sQuery(id+"F0.wireOp",EDGE,"E0")])]}),"instanceName":"1"}),"instanceName":"1"}),"instanceName":"1"}),"instanceName":"1"});
            var Q222;
            Q222=makeQuery(id+"F18.opPattern","COPY",BODY,{"derivedFrom":makeQuery(id+"F17.opPattern","COPY",BODY,{"derivedFrom":makeQuery(id+"F14.opPattern","COPY",BODY,{"derivedFrom":makeQuery(id+"F1.opExtrude","SWEPT_BODY",BODY,{"disambiguationData":[OSD([sQuery(id+"F0.wireOp",EDGE,"E0")])]}),"instanceName":"1"}),"instanceName":"1"}),"instanceName":"1"});
            var Q223;
            Q223=makeQuery(id+"F16.opPattern","COPY",BODY,{"derivedFrom":makeQuery(id+"F14.opPattern","COPY",BODY,{"derivedFrom":makeQuery(id+"F11.opPattern","COPY",BODY,{"derivedFrom":makeQuery(id+"F4.opPattern","COPY",BODY,{"derivedFrom":makeQuery(id+"F1.opExtrude","SWEPT_BODY",BODY,{"disambiguationData":[OSD([sQuery(id+"F0.wireOp",EDGE,"E0")])]}),"instanceName":"1"}),"instanceName":"1"}),"instanceName":"1"}),"instanceName":"1"});
            var Q224;
            Q224=makeQuery(id+"F18.opPattern","COPY",BODY,{"derivedFrom":makeQuery(id+"F15.opPattern","COPY",BODY,{"derivedFrom":makeQuery(id+"F12.opPattern","COPY",BODY,{"derivedFrom":makeQuery(id+"F11.opPattern","COPY",BODY,{"derivedFrom":makeQuery(id+"F9.opPattern","COPY",BODY,{"derivedFrom":makeQuery(id+"F1.opExtrude","SWEPT_BODY",BODY,{"disambiguationData":[OSD([sQuery(id+"F0.wireOp",EDGE,"E0")])]}),"instanceName":"1"}),"instanceName":"1"}),"instanceName":"1"}),"instanceName":"1"}),"instanceName":"1"});
            var Q225;
            Q225=makeQuery(id+"F18.opPattern","COPY",BODY,{"derivedFrom":makeQuery(id+"F15.opPattern","COPY",BODY,{"derivedFrom":makeQuery(id+"F12.opPattern","COPY",BODY,{"derivedFrom":makeQuery(id+"F11.opPattern","COPY",BODY,{"derivedFrom":makeQuery(id+"F10.opPattern","COPY",BODY,{"derivedFrom":makeQuery(id+"F1.opExtrude","SWEPT_BODY",BODY,{"disambiguationData":[OSD([sQuery(id+"F0.wireOp",EDGE,"E0")])]}),"instanceName":"1"}),"instanceName":"1"}),"instanceName":"1"}),"instanceName":"1"}),"instanceName":"1"});
            var Q226;
            Q226=makeQuery(id+"F18.opPattern","COPY",BODY,{"derivedFrom":makeQuery(id+"F17.opPattern","COPY",BODY,{"derivedFrom":makeQuery(id+"F12.opPattern","COPY",BODY,{"derivedFrom":makeQuery(id+"F9.opPattern","COPY",BODY,{"derivedFrom":makeQuery(id+"F1.opExtrude","SWEPT_BODY",BODY,{"disambiguationData":[OSD([sQuery(id+"F0.wireOp",EDGE,"E0")])]}),"instanceName":"1"}),"instanceName":"1"}),"instanceName":"1"}),"instanceName":"1"});
            var Q227;
            Q227=makeQuery(id+"F18.opPattern","COPY",BODY,{"derivedFrom":makeQuery(id+"F17.opPattern","COPY",BODY,{"derivedFrom":makeQuery(id+"F12.opPattern","COPY",BODY,{"derivedFrom":makeQuery(id+"F1.opExtrude","SWEPT_BODY",BODY,{"disambiguationData":[OSD([sQuery(id+"F0.wireOp",EDGE,"E0")])]}),"instanceName":"1"}),"instanceName":"1"}),"instanceName":"1"});
            var Q228;
            Q228=makeQuery(id+"F18.opPattern","COPY",BODY,{"derivedFrom":makeQuery(id+"F15.opPattern","COPY",BODY,{"derivedFrom":makeQuery(id+"F11.opPattern","COPY",BODY,{"derivedFrom":makeQuery(id+"F1.opExtrude","SWEPT_BODY",BODY,{"disambiguationData":[OSD([sQuery(id+"F0.wireOp",EDGE,"E0")])]}),"instanceName":"1"}),"instanceName":"1"}),"instanceName":"1"});
            var Q229;
            Q229=makeQuery(id+"F18.opPattern","COPY",BODY,{"derivedFrom":makeQuery(id+"F15.opPattern","COPY",BODY,{"derivedFrom":makeQuery(id+"F11.opPattern","COPY",BODY,{"derivedFrom":makeQuery(id+"F9.opPattern","COPY",BODY,{"derivedFrom":makeQuery(id+"F4.opPattern","COPY",BODY,{"derivedFrom":makeQuery(id+"F1.opExtrude","SWEPT_BODY",BODY,{"disambiguationData":[OSD([sQuery(id+"F0.wireOp",EDGE,"E0")])]}),"instanceName":"1"}),"instanceName":"1"}),"instanceName":"1"}),"instanceName":"1"}),"instanceName":"1"});
            var Q230;
            Q230=makeQuery(id+"F16.opPattern","COPY",BODY,{"derivedFrom":makeQuery(id+"F12.opPattern","COPY",BODY,{"derivedFrom":makeQuery(id+"F11.opPattern","COPY",BODY,{"derivedFrom":makeQuery(id+"F10.opPattern","COPY",BODY,{"derivedFrom":makeQuery(id+"F1.opExtrude","SWEPT_BODY",BODY,{"disambiguationData":[OSD([sQuery(id+"F0.wireOp",EDGE,"E0")])]}),"instanceName":"1"}),"instanceName":"1"}),"instanceName":"1"}),"instanceName":"1"});
            var Q231;
            Q231=makeQuery(id+"F18.opPattern","COPY",BODY,{"derivedFrom":makeQuery(id+"F15.opPattern","COPY",BODY,{"derivedFrom":makeQuery(id+"F12.opPattern","COPY",BODY,{"derivedFrom":makeQuery(id+"F9.opPattern","COPY",BODY,{"derivedFrom":makeQuery(id+"F1.opExtrude","SWEPT_BODY",BODY,{"disambiguationData":[OSD([sQuery(id+"F0.wireOp",EDGE,"E0")])]}),"instanceName":"1"}),"instanceName":"1"}),"instanceName":"1"}),"instanceName":"1"});
            var Q232;
            Q232=makeQuery(id+"F16.opPattern","COPY",BODY,{"derivedFrom":makeQuery(id+"F11.opPattern","COPY",BODY,{"derivedFrom":makeQuery(id+"F1.opExtrude","SWEPT_BODY",BODY,{"disambiguationData":[OSD([sQuery(id+"F0.wireOp",EDGE,"E0")])]}),"instanceName":"1"}),"instanceName":"1"});
            var Q233;
            Q233=makeQuery(id+"F16.opPattern","COPY",BODY,{"derivedFrom":makeQuery(id+"F11.opPattern","COPY",BODY,{"derivedFrom":makeQuery(id+"F9.opPattern","COPY",BODY,{"derivedFrom":makeQuery(id+"F4.opPattern","COPY",BODY,{"derivedFrom":makeQuery(id+"F1.opExtrude","SWEPT_BODY",BODY,{"disambiguationData":[OSD([sQuery(id+"F0.wireOp",EDGE,"E0")])]}),"instanceName":"1"}),"instanceName":"1"}),"instanceName":"1"}),"instanceName":"1"});
            var Q234;
            Q234=makeQuery(id+"F18.opPattern","COPY",BODY,{"derivedFrom":makeQuery(id+"F12.opPattern","COPY",BODY,{"derivedFrom":makeQuery(id+"F11.opPattern","COPY",BODY,{"derivedFrom":makeQuery(id+"F4.opPattern","COPY",BODY,{"derivedFrom":makeQuery(id+"F1.opExtrude","SWEPT_BODY",BODY,{"disambiguationData":[OSD([sQuery(id+"F0.wireOp",EDGE,"E0")])]}),"instanceName":"1"}),"instanceName":"1"}),"instanceName":"1"}),"instanceName":"1"});
            var Q235;
            Q235=makeQuery(id+"F18.opPattern","COPY",BODY,{"derivedFrom":makeQuery(id+"F16.opPattern","COPY",BODY,{"derivedFrom":makeQuery(id+"F15.opPattern","COPY",BODY,{"derivedFrom":makeQuery(id+"F1.opExtrude","SWEPT_BODY",BODY,{"disambiguationData":[OSD([sQuery(id+"F0.wireOp",EDGE,"E0")])]}),"instanceName":"1"}),"instanceName":"1"}),"instanceName":"1"});
            var Q236;
            Q236=makeQuery(id+"F18.opPattern","COPY",BODY,{"derivedFrom":makeQuery(id+"F12.opPattern","COPY",BODY,{"derivedFrom":makeQuery(id+"F11.opPattern","COPY",BODY,{"derivedFrom":makeQuery(id+"F9.opPattern","COPY",BODY,{"derivedFrom":makeQuery(id+"F1.opExtrude","SWEPT_BODY",BODY,{"disambiguationData":[OSD([sQuery(id+"F0.wireOp",EDGE,"E0")])]}),"instanceName":"1"}),"instanceName":"1"}),"instanceName":"1"}),"instanceName":"1"});
            var Q237;
            Q237=makeQuery(id+"F18.opPattern","COPY",BODY,{"derivedFrom":makeQuery(id+"F14.opPattern","COPY",BODY,{"derivedFrom":makeQuery(id+"F10.opPattern","COPY",BODY,{"derivedFrom":makeQuery(id+"F1.opExtrude","SWEPT_BODY",BODY,{"disambiguationData":[OSD([sQuery(id+"F0.wireOp",EDGE,"E0")])]}),"instanceName":"1"}),"instanceName":"1"}),"instanceName":"1"});
            var Q238;
            Q238=makeQuery(id+"F18.opPattern","COPY",BODY,{"derivedFrom":makeQuery(id+"F16.opPattern","COPY",BODY,{"derivedFrom":makeQuery(id+"F14.opPattern","COPY",BODY,{"derivedFrom":makeQuery(id+"F1.opExtrude","SWEPT_BODY",BODY,{"disambiguationData":[OSD([sQuery(id+"F0.wireOp",EDGE,"E0")])]}),"instanceName":"1"}),"instanceName":"1"}),"instanceName":"1"});
            var Q239;
            Q239=makeQuery(id+"F18.opPattern","COPY",BODY,{"derivedFrom":makeQuery(id+"F12.opPattern","COPY",BODY,{"derivedFrom":makeQuery(id+"F4.opPattern","COPY",BODY,{"derivedFrom":makeQuery(id+"F1.opExtrude","SWEPT_BODY",BODY,{"disambiguationData":[OSD([sQuery(id+"F0.wireOp",EDGE,"E0")])]}),"instanceName":"1"}),"instanceName":"1"}),"instanceName":"1"});
            var Q240;
            Q240=makeQuery(id+"F18.opPattern","COPY",BODY,{"derivedFrom":makeQuery(id+"F16.opPattern","COPY",BODY,{"derivedFrom":makeQuery(id+"F14.opPattern","COPY",BODY,{"derivedFrom":makeQuery(id+"F11.opPattern","COPY",BODY,{"derivedFrom":makeQuery(id+"F9.opPattern","COPY",BODY,{"derivedFrom":makeQuery(id+"F4.opPattern","COPY",BODY,{"derivedFrom":makeQuery(id+"F1.opExtrude","SWEPT_BODY",BODY,{"disambiguationData":[OSD([sQuery(id+"F0.wireOp",EDGE,"E0")])]}),"instanceName":"1"}),"instanceName":"1"}),"instanceName":"1"}),"instanceName":"1"}),"instanceName":"1"}),"instanceName":"1"});
            var Q241;
            Q241=makeQuery(id+"F17.opPattern","COPY",BODY,{"derivedFrom":makeQuery(id+"F15.opPattern","COPY",BODY,{"derivedFrom":makeQuery(id+"F14.opPattern","COPY",BODY,{"derivedFrom":makeQuery(id+"F10.opPattern","COPY",BODY,{"derivedFrom":makeQuery(id+"F1.opExtrude","SWEPT_BODY",BODY,{"disambiguationData":[OSD([sQuery(id+"F0.wireOp",EDGE,"E0")])]}),"instanceName":"1"}),"instanceName":"1"}),"instanceName":"1"}),"instanceName":"1"});
            var Q242;
            Q242=makeQuery(id+"F17.opPattern","COPY",BODY,{"derivedFrom":makeQuery(id+"F15.opPattern","COPY",BODY,{"derivedFrom":makeQuery(id+"F12.opPattern","COPY",BODY,{"derivedFrom":makeQuery(id+"F4.opPattern","COPY",BODY,{"derivedFrom":makeQuery(id+"F1.opExtrude","SWEPT_BODY",BODY,{"disambiguationData":[OSD([sQuery(id+"F0.wireOp",EDGE,"E0")])]}),"instanceName":"1"}),"instanceName":"1"}),"instanceName":"1"}),"instanceName":"1"});
            var Q243;
            Q243=makeQuery(id+"F18.opPattern","COPY",BODY,{"derivedFrom":makeQuery(id+"F16.opPattern","COPY",BODY,{"derivedFrom":makeQuery(id+"F15.opPattern","COPY",BODY,{"derivedFrom":makeQuery(id+"F14.opPattern","COPY",BODY,{"derivedFrom":makeQuery(id+"F4.opPattern","COPY",BODY,{"derivedFrom":makeQuery(id+"F1.opExtrude","SWEPT_BODY",BODY,{"disambiguationData":[OSD([sQuery(id+"F0.wireOp",EDGE,"E0")])]}),"instanceName":"1"}),"instanceName":"1"}),"instanceName":"1"}),"instanceName":"1"}),"instanceName":"1"});
            var Q244;
            Q244=makeQuery(id+"F18.opPattern","COPY",BODY,{"derivedFrom":makeQuery(id+"F16.opPattern","COPY",BODY,{"derivedFrom":makeQuery(id+"F15.opPattern","COPY",BODY,{"derivedFrom":makeQuery(id+"F9.opPattern","COPY",BODY,{"derivedFrom":makeQuery(id+"F1.opExtrude","SWEPT_BODY",BODY,{"disambiguationData":[OSD([sQuery(id+"F0.wireOp",EDGE,"E0")])]}),"instanceName":"1"}),"instanceName":"1"}),"instanceName":"1"}),"instanceName":"1"});
            var Q245;
            Q245=makeQuery(id+"F18.opPattern","COPY",BODY,{"derivedFrom":makeQuery(id+"F16.opPattern","COPY",BODY,{"derivedFrom":makeQuery(id+"F15.opPattern","COPY",BODY,{"derivedFrom":makeQuery(id+"F10.opPattern","COPY",BODY,{"derivedFrom":makeQuery(id+"F1.opExtrude","SWEPT_BODY",BODY,{"disambiguationData":[OSD([sQuery(id+"F0.wireOp",EDGE,"E0")])]}),"instanceName":"1"}),"instanceName":"1"}),"instanceName":"1"}),"instanceName":"1"});
            var Q246;
            Q246=makeQuery(id+"F18.opPattern","COPY",BODY,{"derivedFrom":makeQuery(id+"F16.opPattern","COPY",BODY,{"derivedFrom":makeQuery(id+"F14.opPattern","COPY",BODY,{"derivedFrom":makeQuery(id+"F4.opPattern","COPY",BODY,{"derivedFrom":makeQuery(id+"F1.opExtrude","SWEPT_BODY",BODY,{"disambiguationData":[OSD([sQuery(id+"F0.wireOp",EDGE,"E0")])]}),"instanceName":"1"}),"instanceName":"1"}),"instanceName":"1"}),"instanceName":"1"});
            var Q247;
            Q247=makeQuery(id+"F17.opPattern","COPY",BODY,{"derivedFrom":makeQuery(id+"F16.opPattern","COPY",BODY,{"derivedFrom":makeQuery(id+"F15.opPattern","COPY",BODY,{"derivedFrom":makeQuery(id+"F12.opPattern","COPY",BODY,{"derivedFrom":makeQuery(id+"F10.opPattern","COPY",BODY,{"derivedFrom":makeQuery(id+"F1.opExtrude","SWEPT_BODY",BODY,{"disambiguationData":[OSD([sQuery(id+"F0.wireOp",EDGE,"E0")])]}),"instanceName":"1"}),"instanceName":"1"}),"instanceName":"1"}),"instanceName":"1"}),"instanceName":"1"});
            var Q248;
            Q248=makeQuery(id+"F18.opPattern","COPY",BODY,{"derivedFrom":makeQuery(id+"F17.opPattern","COPY",BODY,{"derivedFrom":makeQuery(id+"F15.opPattern","COPY",BODY,{"derivedFrom":makeQuery(id+"F1.opExtrude","SWEPT_BODY",BODY,{"disambiguationData":[OSD([sQuery(id+"F0.wireOp",EDGE,"E0")])]}),"instanceName":"1"}),"instanceName":"1"}),"instanceName":"1"});
            var Q249;
            Q249=makeQuery(id+"F16.opPattern","COPY",BODY,{"derivedFrom":makeQuery(id+"F15.opPattern","COPY",BODY,{"derivedFrom":makeQuery(id+"F14.opPattern","COPY",BODY,{"derivedFrom":makeQuery(id+"F4.opPattern","COPY",BODY,{"derivedFrom":makeQuery(id+"F1.opExtrude","SWEPT_BODY",BODY,{"disambiguationData":[OSD([sQuery(id+"F0.wireOp",EDGE,"E0")])]}),"instanceName":"1"}),"instanceName":"1"}),"instanceName":"1"}),"instanceName":"1"});
            var Q250;
            Q250=makeQuery(id+"F18.opPattern","COPY",BODY,{"derivedFrom":makeQuery(id+"F16.opPattern","COPY",BODY,{"derivedFrom":makeQuery(id+"F10.opPattern","COPY",BODY,{"derivedFrom":makeQuery(id+"F1.opExtrude","SWEPT_BODY",BODY,{"disambiguationData":[OSD([sQuery(id+"F0.wireOp",EDGE,"E0")])]}),"instanceName":"1"}),"instanceName":"1"}),"instanceName":"1"});
            var Q251;
            Q251=makeQuery(id+"F18.opPattern","COPY",BODY,{"derivedFrom":makeQuery(id+"F17.opPattern","COPY",BODY,{"derivedFrom":makeQuery(id+"F15.opPattern","COPY",BODY,{"derivedFrom":makeQuery(id+"F4.opPattern","COPY",BODY,{"derivedFrom":makeQuery(id+"F1.opExtrude","SWEPT_BODY",BODY,{"disambiguationData":[OSD([sQuery(id+"F0.wireOp",EDGE,"E0")])]}),"instanceName":"1"}),"instanceName":"1"}),"instanceName":"1"}),"instanceName":"1"});
            var Q252;
            Q252=makeQuery(id+"F16.opPattern","COPY",BODY,{"derivedFrom":makeQuery(id+"F15.opPattern","COPY",BODY,{"derivedFrom":makeQuery(id+"F12.opPattern","COPY",BODY,{"derivedFrom":makeQuery(id+"F11.opPattern","COPY",BODY,{"derivedFrom":makeQuery(id+"F1.opExtrude","SWEPT_BODY",BODY,{"disambiguationData":[OSD([sQuery(id+"F0.wireOp",EDGE,"E0")])]}),"instanceName":"1"}),"instanceName":"1"}),"instanceName":"1"}),"instanceName":"1"});
            var Q253;
            Q253=makeQuery(id+"F18.opPattern","COPY",BODY,{"derivedFrom":makeQuery(id+"F17.opPattern","COPY",BODY,{"derivedFrom":makeQuery(id+"F12.opPattern","COPY",BODY,{"derivedFrom":makeQuery(id+"F11.opPattern","COPY",BODY,{"derivedFrom":makeQuery(id+"F10.opPattern","COPY",BODY,{"derivedFrom":makeQuery(id+"F1.opExtrude","SWEPT_BODY",BODY,{"disambiguationData":[OSD([sQuery(id+"F0.wireOp",EDGE,"E0")])]}),"instanceName":"1"}),"instanceName":"1"}),"instanceName":"1"}),"instanceName":"1"}),"instanceName":"1"});
            var Q254;
            Q254=makeQuery(id+"F16.opPattern","COPY",BODY,{"derivedFrom":makeQuery(id+"F12.opPattern","COPY",BODY,{"derivedFrom":makeQuery(id+"F10.opPattern","COPY",BODY,{"derivedFrom":makeQuery(id+"F1.opExtrude","SWEPT_BODY",BODY,{"disambiguationData":[OSD([sQuery(id+"F0.wireOp",EDGE,"E0")])]}),"instanceName":"1"}),"instanceName":"1"}),"instanceName":"1"});
            var Q255;
            Q255=makeQuery(id+"F18.opPattern","COPY",BODY,{"derivedFrom":makeQuery(id+"F15.opPattern","COPY",BODY,{"derivedFrom":makeQuery(id+"F12.opPattern","COPY",BODY,{"derivedFrom":makeQuery(id+"F4.opPattern","COPY",BODY,{"derivedFrom":makeQuery(id+"F1.opExtrude","SWEPT_BODY",BODY,{"disambiguationData":[OSD([sQuery(id+"F0.wireOp",EDGE,"E0")])]}),"instanceName":"1"}),"instanceName":"1"}),"instanceName":"1"}),"instanceName":"1"});
            var Q256;
            Q256=makeQuery(id+"F18.opPattern","COPY",BODY,{"derivedFrom":makeQuery(id+"F17.opPattern","COPY",BODY,{"derivedFrom":makeQuery(id+"F11.opPattern","COPY",BODY,{"derivedFrom":makeQuery(id+"F9.opPattern","COPY",BODY,{"derivedFrom":makeQuery(id+"F1.opExtrude","SWEPT_BODY",BODY,{"disambiguationData":[OSD([sQuery(id+"F0.wireOp",EDGE,"E0")])]}),"instanceName":"1"}),"instanceName":"1"}),"instanceName":"1"}),"instanceName":"1"});
            var Q257;
            Q257=makeQuery(id+"F18.opPattern","COPY",BODY,{"derivedFrom":makeQuery(id+"F17.opPattern","COPY",BODY,{"derivedFrom":makeQuery(id+"F15.opPattern","COPY",BODY,{"derivedFrom":makeQuery(id+"F12.opPattern","COPY",BODY,{"derivedFrom":makeQuery(id+"F4.opPattern","COPY",BODY,{"derivedFrom":makeQuery(id+"F1.opExtrude","SWEPT_BODY",BODY,{"disambiguationData":[OSD([sQuery(id+"F0.wireOp",EDGE,"E0")])]}),"instanceName":"1"}),"instanceName":"1"}),"instanceName":"1"}),"instanceName":"1"}),"instanceName":"1"});
            var Q258;
            Q258=makeQuery(id+"F18.opPattern","COPY",BODY,{"derivedFrom":makeQuery(id+"F17.opPattern","COPY",BODY,{"derivedFrom":makeQuery(id+"F12.opPattern","COPY",BODY,{"derivedFrom":makeQuery(id+"F9.opPattern","COPY",BODY,{"derivedFrom":makeQuery(id+"F4.opPattern","COPY",BODY,{"derivedFrom":makeQuery(id+"F1.opExtrude","SWEPT_BODY",BODY,{"disambiguationData":[OSD([sQuery(id+"F0.wireOp",EDGE,"E0")])]}),"instanceName":"1"}),"instanceName":"1"}),"instanceName":"1"}),"instanceName":"1"}),"instanceName":"1"});
            var Q259;
            Q259=makeQuery(id+"F18.opPattern","COPY",BODY,{"derivedFrom":makeQuery(id+"F14.opPattern","COPY",BODY,{"derivedFrom":makeQuery(id+"F11.opPattern","COPY",BODY,{"derivedFrom":makeQuery(id+"F9.opPattern","COPY",BODY,{"derivedFrom":makeQuery(id+"F1.opExtrude","SWEPT_BODY",BODY,{"disambiguationData":[OSD([sQuery(id+"F0.wireOp",EDGE,"E0")])]}),"instanceName":"1"}),"instanceName":"1"}),"instanceName":"1"}),"instanceName":"1"});
            var Q260;
            Q260=makeQuery(id+"F18.opPattern","COPY",BODY,{"derivedFrom":makeQuery(id+"F10.opPattern","COPY",BODY,{"derivedFrom":makeQuery(id+"F1.opExtrude","SWEPT_BODY",BODY,{"disambiguationData":[OSD([sQuery(id+"F0.wireOp",EDGE,"E0")])]}),"instanceName":"1"}),"instanceName":"1"});
            var Q261;
            Q261=makeQuery(id+"F18.opPattern","COPY",BODY,{"derivedFrom":makeQuery(id+"F16.opPattern","COPY",BODY,{"derivedFrom":makeQuery(id+"F4.opPattern","COPY",BODY,{"derivedFrom":makeQuery(id+"F1.opExtrude","SWEPT_BODY",BODY,{"disambiguationData":[OSD([sQuery(id+"F0.wireOp",EDGE,"E0")])]}),"instanceName":"1"}),"instanceName":"1"}),"instanceName":"1"});
            var Q262;
            Q262=makeQuery(id+"F18.opPattern","COPY",BODY,{"derivedFrom":makeQuery(id+"F16.opPattern","COPY",BODY,{"derivedFrom":makeQuery(id+"F9.opPattern","COPY",BODY,{"derivedFrom":makeQuery(id+"F1.opExtrude","SWEPT_BODY",BODY,{"disambiguationData":[OSD([sQuery(id+"F0.wireOp",EDGE,"E0")])]}),"instanceName":"1"}),"instanceName":"1"}),"instanceName":"1"});
            var Q263;
            Q263=makeQuery(id+"F18.opPattern","COPY",BODY,{"derivedFrom":makeQuery(id+"F17.opPattern","COPY",BODY,{"derivedFrom":makeQuery(id+"F10.opPattern","COPY",BODY,{"derivedFrom":makeQuery(id+"F1.opExtrude","SWEPT_BODY",BODY,{"disambiguationData":[OSD([sQuery(id+"F0.wireOp",EDGE,"E0")])]}),"instanceName":"1"}),"instanceName":"1"}),"instanceName":"1"});
            var Q264;
            Q264=makeQuery(id+"F18.opPattern","COPY",BODY,{"derivedFrom":makeQuery(id+"F15.opPattern","COPY",BODY,{"derivedFrom":makeQuery(id+"F12.opPattern","COPY",BODY,{"derivedFrom":makeQuery(id+"F1.opExtrude","SWEPT_BODY",BODY,{"disambiguationData":[OSD([sQuery(id+"F0.wireOp",EDGE,"E0")])]}),"instanceName":"1"}),"instanceName":"1"}),"instanceName":"1"});
            var Q265;
            Q265=makeQuery(id+"F18.opPattern","COPY",BODY,{"derivedFrom":makeQuery(id+"F17.opPattern","COPY",BODY,{"derivedFrom":makeQuery(id+"F15.opPattern","COPY",BODY,{"derivedFrom":makeQuery(id+"F12.opPattern","COPY",BODY,{"derivedFrom":makeQuery(id+"F11.opPattern","COPY",BODY,{"derivedFrom":makeQuery(id+"F1.opExtrude","SWEPT_BODY",BODY,{"disambiguationData":[OSD([sQuery(id+"F0.wireOp",EDGE,"E0")])]}),"instanceName":"1"}),"instanceName":"1"}),"instanceName":"1"}),"instanceName":"1"}),"instanceName":"1"});
            var Q266;
            Q266=makeQuery(id+"F18.opPattern","COPY",BODY,{"derivedFrom":makeQuery(id+"F15.opPattern","COPY",BODY,{"derivedFrom":makeQuery(id+"F12.opPattern","COPY",BODY,{"derivedFrom":makeQuery(id+"F9.opPattern","COPY",BODY,{"derivedFrom":makeQuery(id+"F4.opPattern","COPY",BODY,{"derivedFrom":makeQuery(id+"F1.opExtrude","SWEPT_BODY",BODY,{"disambiguationData":[OSD([sQuery(id+"F0.wireOp",EDGE,"E0")])]}),"instanceName":"1"}),"instanceName":"1"}),"instanceName":"1"}),"instanceName":"1"}),"instanceName":"1"});
            var Q267;
            Q267=makeQuery(id+"F18.opPattern","COPY",BODY,{"derivedFrom":makeQuery(id+"F16.opPattern","COPY",BODY,{"derivedFrom":makeQuery(id+"F15.opPattern","COPY",BODY,{"derivedFrom":makeQuery(id+"F12.opPattern","COPY",BODY,{"derivedFrom":makeQuery(id+"F4.opPattern","COPY",BODY,{"derivedFrom":makeQuery(id+"F1.opExtrude","SWEPT_BODY",BODY,{"disambiguationData":[OSD([sQuery(id+"F0.wireOp",EDGE,"E0")])]}),"instanceName":"1"}),"instanceName":"1"}),"instanceName":"1"}),"instanceName":"1"}),"instanceName":"1"});
            var Q268;
            Q268=makeQuery(id+"F18.opPattern","COPY",BODY,{"derivedFrom":makeQuery(id+"F15.opPattern","COPY",BODY,{"derivedFrom":makeQuery(id+"F4.opPattern","COPY",BODY,{"derivedFrom":makeQuery(id+"F1.opExtrude","SWEPT_BODY",BODY,{"disambiguationData":[OSD([sQuery(id+"F0.wireOp",EDGE,"E0")])]}),"instanceName":"1"}),"instanceName":"1"}),"instanceName":"1"});
            var Q269;
            Q269=makeQuery(id+"F18.opPattern","COPY",BODY,{"derivedFrom":makeQuery(id+"F16.opPattern","COPY",BODY,{"derivedFrom":makeQuery(id+"F15.opPattern","COPY",BODY,{"derivedFrom":makeQuery(id+"F11.opPattern","COPY",BODY,{"derivedFrom":makeQuery(id+"F1.opExtrude","SWEPT_BODY",BODY,{"disambiguationData":[OSD([sQuery(id+"F0.wireOp",EDGE,"E0")])]}),"instanceName":"1"}),"instanceName":"1"}),"instanceName":"1"}),"instanceName":"1"});
            var Q270;
            Q270=makeQuery(id+"F18.opPattern","COPY",BODY,{"derivedFrom":makeQuery(id+"F12.opPattern","COPY",BODY,{"derivedFrom":makeQuery(id+"F9.opPattern","COPY",BODY,{"derivedFrom":makeQuery(id+"F4.opPattern","COPY",BODY,{"derivedFrom":makeQuery(id+"F1.opExtrude","SWEPT_BODY",BODY,{"disambiguationData":[OSD([sQuery(id+"F0.wireOp",EDGE,"E0")])]}),"instanceName":"1"}),"instanceName":"1"}),"instanceName":"1"}),"instanceName":"1"});
            var Q271;
            Q271=makeQuery(id+"F18.opPattern","COPY",BODY,{"derivedFrom":makeQuery(id+"F17.opPattern","COPY",BODY,{"derivedFrom":makeQuery(id+"F11.opPattern","COPY",BODY,{"derivedFrom":makeQuery(id+"F4.opPattern","COPY",BODY,{"derivedFrom":makeQuery(id+"F1.opExtrude","SWEPT_BODY",BODY,{"disambiguationData":[OSD([sQuery(id+"F0.wireOp",EDGE,"E0")])]}),"instanceName":"1"}),"instanceName":"1"}),"instanceName":"1"}),"instanceName":"1"});
            var Q272;
            Q272=makeQuery(id+"F18.opPattern","COPY",BODY,{"derivedFrom":makeQuery(id+"F16.opPattern","COPY",BODY,{"derivedFrom":makeQuery(id+"F15.opPattern","COPY",BODY,{"derivedFrom":makeQuery(id+"F12.opPattern","COPY",BODY,{"derivedFrom":makeQuery(id+"F11.opPattern","COPY",BODY,{"derivedFrom":makeQuery(id+"F9.opPattern","COPY",BODY,{"derivedFrom":makeQuery(id+"F4.opPattern","COPY",BODY,{"derivedFrom":makeQuery(id+"F1.opExtrude","SWEPT_BODY",BODY,{"disambiguationData":[OSD([sQuery(id+"F0.wireOp",EDGE,"E0")])]}),"instanceName":"1"}),"instanceName":"1"}),"instanceName":"1"}),"instanceName":"1"}),"instanceName":"1"}),"instanceName":"1"}),"instanceName":"1"});
            var Q273;
            Q273=makeQuery(id+"F18.opPattern","COPY",BODY,{"derivedFrom":makeQuery(id+"F16.opPattern","COPY",BODY,{"derivedFrom":makeQuery(id+"F15.opPattern","COPY",BODY,{"derivedFrom":makeQuery(id+"F12.opPattern","COPY",BODY,{"derivedFrom":makeQuery(id+"F11.opPattern","COPY",BODY,{"derivedFrom":makeQuery(id+"F1.opExtrude","SWEPT_BODY",BODY,{"disambiguationData":[OSD([sQuery(id+"F0.wireOp",EDGE,"E0")])]}),"instanceName":"1"}),"instanceName":"1"}),"instanceName":"1"}),"instanceName":"1"}),"instanceName":"1"});
            var Q274;
            Q274=makeQuery(id+"F18.opPattern","COPY",BODY,{"derivedFrom":makeQuery(id+"F16.opPattern","COPY",BODY,{"derivedFrom":makeQuery(id+"F14.opPattern","COPY",BODY,{"derivedFrom":makeQuery(id+"F11.opPattern","COPY",BODY,{"derivedFrom":makeQuery(id+"F1.opExtrude","SWEPT_BODY",BODY,{"disambiguationData":[OSD([sQuery(id+"F0.wireOp",EDGE,"E0")])]}),"instanceName":"1"}),"instanceName":"1"}),"instanceName":"1"}),"instanceName":"1"});
            var Q275;
            Q275=makeQuery(id+"F18.opPattern","COPY",BODY,{"derivedFrom":makeQuery(id+"F16.opPattern","COPY",BODY,{"derivedFrom":makeQuery(id+"F11.opPattern","COPY",BODY,{"derivedFrom":makeQuery(id+"F10.opPattern","COPY",BODY,{"derivedFrom":makeQuery(id+"F1.opExtrude","SWEPT_BODY",BODY,{"disambiguationData":[OSD([sQuery(id+"F0.wireOp",EDGE,"E0")])]}),"instanceName":"1"}),"instanceName":"1"}),"instanceName":"1"}),"instanceName":"1"});
            var Q276;
            Q276=makeQuery(id+"F18.opPattern","COPY",BODY,{"derivedFrom":makeQuery(id+"F16.opPattern","COPY",BODY,{"derivedFrom":makeQuery(id+"F11.opPattern","COPY",BODY,{"derivedFrom":makeQuery(id+"F9.opPattern","COPY",BODY,{"derivedFrom":makeQuery(id+"F1.opExtrude","SWEPT_BODY",BODY,{"disambiguationData":[OSD([sQuery(id+"F0.wireOp",EDGE,"E0")])]}),"instanceName":"1"}),"instanceName":"1"}),"instanceName":"1"}),"instanceName":"1"});
            var Q277;
            Q277=makeQuery(id+"F18.opPattern","COPY",BODY,{"derivedFrom":makeQuery(id+"F17.opPattern","COPY",BODY,{"derivedFrom":makeQuery(id+"F15.opPattern","COPY",BODY,{"derivedFrom":makeQuery(id+"F14.opPattern","COPY",BODY,{"derivedFrom":makeQuery(id+"F4.opPattern","COPY",BODY,{"derivedFrom":makeQuery(id+"F1.opExtrude","SWEPT_BODY",BODY,{"disambiguationData":[OSD([sQuery(id+"F0.wireOp",EDGE,"E0")])]}),"instanceName":"1"}),"instanceName":"1"}),"instanceName":"1"}),"instanceName":"1"}),"instanceName":"1"});
            var Q278;
            Q278=makeQuery(id+"F18.opPattern","COPY",BODY,{"derivedFrom":makeQuery(id+"F17.opPattern","COPY",BODY,{"derivedFrom":makeQuery(id+"F12.opPattern","COPY",BODY,{"derivedFrom":makeQuery(id+"F11.opPattern","COPY",BODY,{"derivedFrom":makeQuery(id+"F1.opExtrude","SWEPT_BODY",BODY,{"disambiguationData":[OSD([sQuery(id+"F0.wireOp",EDGE,"E0")])]}),"instanceName":"1"}),"instanceName":"1"}),"instanceName":"1"}),"instanceName":"1"});
            var Q279;
            Q279=makeQuery(id+"F18.opPattern","COPY",BODY,{"derivedFrom":makeQuery(id+"F17.opPattern","COPY",BODY,{"derivedFrom":makeQuery(id+"F12.opPattern","COPY",BODY,{"derivedFrom":makeQuery(id+"F11.opPattern","COPY",BODY,{"derivedFrom":makeQuery(id+"F9.opPattern","COPY",BODY,{"derivedFrom":makeQuery(id+"F4.opPattern","COPY",BODY,{"derivedFrom":makeQuery(id+"F1.opExtrude","SWEPT_BODY",BODY,{"disambiguationData":[OSD([sQuery(id+"F0.wireOp",EDGE,"E0")])]}),"instanceName":"1"}),"instanceName":"1"}),"instanceName":"1"}),"instanceName":"1"}),"instanceName":"1"}),"instanceName":"1"});
            var Q280;
            Q280=makeQuery(id+"F18.opPattern","COPY",BODY,{"derivedFrom":makeQuery(id+"F17.opPattern","COPY",BODY,{"derivedFrom":makeQuery(id+"F15.opPattern","COPY",BODY,{"derivedFrom":makeQuery(id+"F11.opPattern","COPY",BODY,{"derivedFrom":makeQuery(id+"F4.opPattern","COPY",BODY,{"derivedFrom":makeQuery(id+"F1.opExtrude","SWEPT_BODY",BODY,{"disambiguationData":[OSD([sQuery(id+"F0.wireOp",EDGE,"E0")])]}),"instanceName":"1"}),"instanceName":"1"}),"instanceName":"1"}),"instanceName":"1"}),"instanceName":"1"});
            var Q281;
            Q281=makeQuery(id+"F18.opPattern","COPY",BODY,{"derivedFrom":makeQuery(id+"F12.opPattern","COPY",BODY,{"derivedFrom":makeQuery(id+"F11.opPattern","COPY",BODY,{"derivedFrom":makeQuery(id+"F1.opExtrude","SWEPT_BODY",BODY,{"disambiguationData":[OSD([sQuery(id+"F0.wireOp",EDGE,"E0")])]}),"instanceName":"1"}),"instanceName":"1"}),"instanceName":"1"});
            var Q282;
            Q282=makeQuery(id+"F18.opPattern","COPY",BODY,{"derivedFrom":makeQuery(id+"F11.opPattern","COPY",BODY,{"derivedFrom":makeQuery(id+"F9.opPattern","COPY",BODY,{"derivedFrom":makeQuery(id+"F1.opExtrude","SWEPT_BODY",BODY,{"disambiguationData":[OSD([sQuery(id+"F0.wireOp",EDGE,"E0")])]}),"instanceName":"1"}),"instanceName":"1"}),"instanceName":"1"});
            var Q283;
            Q283=makeQuery(id+"F18.opPattern","COPY",BODY,{"derivedFrom":makeQuery(id+"F15.opPattern","COPY",BODY,{"derivedFrom":makeQuery(id+"F14.opPattern","COPY",BODY,{"derivedFrom":makeQuery(id+"F11.opPattern","COPY",BODY,{"derivedFrom":makeQuery(id+"F1.opExtrude","SWEPT_BODY",BODY,{"disambiguationData":[OSD([sQuery(id+"F0.wireOp",EDGE,"E0")])]}),"instanceName":"1"}),"instanceName":"1"}),"instanceName":"1"}),"instanceName":"1"});
            var Q284;
            Q284=makeQuery(id+"F18.opPattern","COPY",BODY,{"derivedFrom":makeQuery(id+"F15.opPattern","COPY",BODY,{"derivedFrom":makeQuery(id+"F14.opPattern","COPY",BODY,{"derivedFrom":makeQuery(id+"F11.opPattern","COPY",BODY,{"derivedFrom":makeQuery(id+"F9.opPattern","COPY",BODY,{"derivedFrom":makeQuery(id+"F4.opPattern","COPY",BODY,{"derivedFrom":makeQuery(id+"F1.opExtrude","SWEPT_BODY",BODY,{"disambiguationData":[OSD([sQuery(id+"F0.wireOp",EDGE,"E0")])]}),"instanceName":"1"}),"instanceName":"1"}),"instanceName":"1"}),"instanceName":"1"}),"instanceName":"1"}),"instanceName":"1"});
            var Q285;
            Q285=makeQuery(id+"F16.opPattern","COPY",BODY,{"derivedFrom":makeQuery(id+"F15.opPattern","COPY",BODY,{"derivedFrom":makeQuery(id+"F11.opPattern","COPY",BODY,{"derivedFrom":makeQuery(id+"F10.opPattern","COPY",BODY,{"derivedFrom":makeQuery(id+"F1.opExtrude","SWEPT_BODY",BODY,{"disambiguationData":[OSD([sQuery(id+"F0.wireOp",EDGE,"E0")])]}),"instanceName":"1"}),"instanceName":"1"}),"instanceName":"1"}),"instanceName":"1"});
            var Q286;
            Q286=makeQuery(id+"F16.opPattern","COPY",BODY,{"derivedFrom":makeQuery(id+"F14.opPattern","COPY",BODY,{"derivedFrom":makeQuery(id+"F11.opPattern","COPY",BODY,{"derivedFrom":makeQuery(id+"F9.opPattern","COPY",BODY,{"derivedFrom":makeQuery(id+"F4.opPattern","COPY",BODY,{"derivedFrom":makeQuery(id+"F1.opExtrude","SWEPT_BODY",BODY,{"disambiguationData":[OSD([sQuery(id+"F0.wireOp",EDGE,"E0")])]}),"instanceName":"1"}),"instanceName":"1"}),"instanceName":"1"}),"instanceName":"1"}),"instanceName":"1"});
            var Q287;
            Q287=makeQuery(id+"F18.opPattern","COPY",BODY,{"derivedFrom":makeQuery(id+"F15.opPattern","COPY",BODY,{"derivedFrom":makeQuery(id+"F11.opPattern","COPY",BODY,{"derivedFrom":makeQuery(id+"F4.opPattern","COPY",BODY,{"derivedFrom":makeQuery(id+"F1.opExtrude","SWEPT_BODY",BODY,{"disambiguationData":[OSD([sQuery(id+"F0.wireOp",EDGE,"E0")])]}),"instanceName":"1"}),"instanceName":"1"}),"instanceName":"1"}),"instanceName":"1"});
            var Q288;
            Q288=makeQuery(id+"F18.opPattern","COPY",BODY,{"derivedFrom":makeQuery(id+"F15.opPattern","COPY",BODY,{"derivedFrom":makeQuery(id+"F11.opPattern","COPY",BODY,{"derivedFrom":makeQuery(id+"F9.opPattern","COPY",BODY,{"derivedFrom":makeQuery(id+"F1.opExtrude","SWEPT_BODY",BODY,{"disambiguationData":[OSD([sQuery(id+"F0.wireOp",EDGE,"E0")])]}),"instanceName":"1"}),"instanceName":"1"}),"instanceName":"1"}),"instanceName":"1"});
            var Q289;
            Q289=makeQuery(id+"F16.opPattern","COPY",BODY,{"derivedFrom":makeQuery(id+"F11.opPattern","COPY",BODY,{"derivedFrom":makeQuery(id+"F9.opPattern","COPY",BODY,{"derivedFrom":makeQuery(id+"F1.opExtrude","SWEPT_BODY",BODY,{"disambiguationData":[OSD([sQuery(id+"F0.wireOp",EDGE,"E0")])]}),"instanceName":"1"}),"instanceName":"1"}),"instanceName":"1"});
            var Q290;
            Q290=makeQuery(id+"F18.opPattern","COPY",BODY,{"derivedFrom":makeQuery(id+"F12.opPattern","COPY",BODY,{"derivedFrom":makeQuery(id+"F11.opPattern","COPY",BODY,{"derivedFrom":makeQuery(id+"F9.opPattern","COPY",BODY,{"derivedFrom":makeQuery(id+"F4.opPattern","COPY",BODY,{"derivedFrom":makeQuery(id+"F1.opExtrude","SWEPT_BODY",BODY,{"disambiguationData":[OSD([sQuery(id+"F0.wireOp",EDGE,"E0")])]}),"instanceName":"1"}),"instanceName":"1"}),"instanceName":"1"}),"instanceName":"1"}),"instanceName":"1"});
            var Q291;
            Q291=makeQuery(id+"F18.opPattern","COPY",BODY,{"derivedFrom":makeQuery(id+"F11.opPattern","COPY",BODY,{"derivedFrom":makeQuery(id+"F4.opPattern","COPY",BODY,{"derivedFrom":makeQuery(id+"F1.opExtrude","SWEPT_BODY",BODY,{"disambiguationData":[OSD([sQuery(id+"F0.wireOp",EDGE,"E0")])]}),"instanceName":"1"}),"instanceName":"1"}),"instanceName":"1"});
            var Q292;
            Q292=makeQuery(id+"F18.opPattern","COPY",BODY,{"derivedFrom":makeQuery(id+"F16.opPattern","COPY",BODY,{"derivedFrom":makeQuery(id+"F12.opPattern","COPY",BODY,{"derivedFrom":makeQuery(id+"F11.opPattern","COPY",BODY,{"derivedFrom":makeQuery(id+"F9.opPattern","COPY",BODY,{"derivedFrom":makeQuery(id+"F1.opExtrude","SWEPT_BODY",BODY,{"disambiguationData":[OSD([sQuery(id+"F0.wireOp",EDGE,"E0")])]}),"instanceName":"1"}),"instanceName":"1"}),"instanceName":"1"}),"instanceName":"1"}),"instanceName":"1"});
            var Q293;
            Q293=makeQuery(id+"F18.opPattern","COPY",BODY,{"derivedFrom":makeQuery(id+"F16.opPattern","COPY",BODY,{"derivedFrom":makeQuery(id+"F15.opPattern","COPY",BODY,{"derivedFrom":makeQuery(id+"F14.opPattern","COPY",BODY,{"derivedFrom":makeQuery(id+"F10.opPattern","COPY",BODY,{"derivedFrom":makeQuery(id+"F1.opExtrude","SWEPT_BODY",BODY,{"disambiguationData":[OSD([sQuery(id+"F0.wireOp",EDGE,"E0")])]}),"instanceName":"1"}),"instanceName":"1"}),"instanceName":"1"}),"instanceName":"1"}),"instanceName":"1"});
            var Q294;
            Q294=makeQuery(id+"F18.opPattern","COPY",BODY,{"derivedFrom":makeQuery(id+"F17.opPattern","COPY",BODY,{"derivedFrom":makeQuery(id+"F15.opPattern","COPY",BODY,{"derivedFrom":makeQuery(id+"F9.opPattern","COPY",BODY,{"derivedFrom":makeQuery(id+"F4.opPattern","COPY",BODY,{"derivedFrom":makeQuery(id+"F1.opExtrude","SWEPT_BODY",BODY,{"disambiguationData":[OSD([sQuery(id+"F0.wireOp",EDGE,"E0")])]}),"instanceName":"1"}),"instanceName":"1"}),"instanceName":"1"}),"instanceName":"1"}),"instanceName":"1"});
            var Q295;
            Q295=makeQuery(id+"F18.opPattern","COPY",BODY,{"derivedFrom":makeQuery(id+"F11.opPattern","COPY",BODY,{"derivedFrom":makeQuery(id+"F10.opPattern","COPY",BODY,{"derivedFrom":makeQuery(id+"F1.opExtrude","SWEPT_BODY",BODY,{"disambiguationData":[OSD([sQuery(id+"F0.wireOp",EDGE,"E0")])]}),"instanceName":"1"}),"instanceName":"1"}),"instanceName":"1"});
            var Q296;
            Q296=makeQuery(id+"F18.opPattern","COPY",BODY,{"derivedFrom":makeQuery(id+"F15.opPattern","COPY",BODY,{"derivedFrom":makeQuery(id+"F12.opPattern","COPY",BODY,{"derivedFrom":makeQuery(id+"F10.opPattern","COPY",BODY,{"derivedFrom":makeQuery(id+"F1.opExtrude","SWEPT_BODY",BODY,{"disambiguationData":[OSD([sQuery(id+"F0.wireOp",EDGE,"E0")])]}),"instanceName":"1"}),"instanceName":"1"}),"instanceName":"1"}),"instanceName":"1"});
            var Q297;
            Q297=makeQuery(id+"F18.opPattern","COPY",BODY,{"derivedFrom":makeQuery(id+"F17.opPattern","COPY",BODY,{"derivedFrom":makeQuery(id+"F11.opPattern","COPY",BODY,{"derivedFrom":makeQuery(id+"F10.opPattern","COPY",BODY,{"derivedFrom":makeQuery(id+"F1.opExtrude","SWEPT_BODY",BODY,{"disambiguationData":[OSD([sQuery(id+"F0.wireOp",EDGE,"E0")])]}),"instanceName":"1"}),"instanceName":"1"}),"instanceName":"1"}),"instanceName":"1"});
            var Q298;
            Q298=makeQuery(id+"F18.opPattern","COPY",BODY,{"derivedFrom":makeQuery(id+"F16.opPattern","COPY",BODY,{"derivedFrom":makeQuery(id+"F15.opPattern","COPY",BODY,{"derivedFrom":makeQuery(id+"F12.opPattern","COPY",BODY,{"derivedFrom":makeQuery(id+"F1.opExtrude","SWEPT_BODY",BODY,{"disambiguationData":[OSD([sQuery(id+"F0.wireOp",EDGE,"E0")])]}),"instanceName":"1"}),"instanceName":"1"}),"instanceName":"1"}),"instanceName":"1"});
            var Q299;
            Q299=makeQuery(id+"F18.opPattern","COPY",BODY,{"derivedFrom":makeQuery(id+"F15.opPattern","COPY",BODY,{"derivedFrom":makeQuery(id+"F9.opPattern","COPY",BODY,{"derivedFrom":makeQuery(id+"F4.opPattern","COPY",BODY,{"derivedFrom":makeQuery(id+"F1.opExtrude","SWEPT_BODY",BODY,{"disambiguationData":[OSD([sQuery(id+"F0.wireOp",EDGE,"E0")])]}),"instanceName":"1"}),"instanceName":"1"}),"instanceName":"1"}),"instanceName":"1"});
            var Q300;
            Q300=makeQuery(id+"F18.opPattern","COPY",BODY,{"derivedFrom":makeQuery(id+"F16.opPattern","COPY",BODY,{"derivedFrom":makeQuery(id+"F15.opPattern","COPY",BODY,{"derivedFrom":makeQuery(id+"F11.opPattern","COPY",BODY,{"derivedFrom":makeQuery(id+"F9.opPattern","COPY",BODY,{"derivedFrom":makeQuery(id+"F4.opPattern","COPY",BODY,{"derivedFrom":makeQuery(id+"F1.opExtrude","SWEPT_BODY",BODY,{"disambiguationData":[OSD([sQuery(id+"F0.wireOp",EDGE,"E0")])]}),"instanceName":"1"}),"instanceName":"1"}),"instanceName":"1"}),"instanceName":"1"}),"instanceName":"1"}),"instanceName":"1"});
            var Q301;
            Q301=makeQuery(id+"F15.opPattern","COPY",BODY,{"derivedFrom":makeQuery(id+"F12.opPattern","COPY",BODY,{"derivedFrom":makeQuery(id+"F11.opPattern","COPY",BODY,{"derivedFrom":makeQuery(id+"F9.opPattern","COPY",BODY,{"derivedFrom":makeQuery(id+"F1.opExtrude","SWEPT_BODY",BODY,{"disambiguationData":[OSD([sQuery(id+"F0.wireOp",EDGE,"E0")])]}),"instanceName":"1"}),"instanceName":"1"}),"instanceName":"1"}),"instanceName":"1"});
            var Q302;
            Q302=makeQuery(id+"F15.opPattern","COPY",BODY,{"derivedFrom":makeQuery(id+"F14.opPattern","COPY",BODY,{"derivedFrom":makeQuery(id+"F10.opPattern","COPY",BODY,{"derivedFrom":makeQuery(id+"F1.opExtrude","SWEPT_BODY",BODY,{"disambiguationData":[OSD([sQuery(id+"F0.wireOp",EDGE,"E0")])]}),"instanceName":"1"}),"instanceName":"1"}),"instanceName":"1"});
            var Q303;
            Q303=makeQuery(id+"F15.opPattern","COPY",BODY,{"derivedFrom":makeQuery(id+"F12.opPattern","COPY",BODY,{"derivedFrom":makeQuery(id+"F4.opPattern","COPY",BODY,{"derivedFrom":makeQuery(id+"F1.opExtrude","SWEPT_BODY",BODY,{"disambiguationData":[OSD([sQuery(id+"F0.wireOp",EDGE,"E0")])]}),"instanceName":"1"}),"instanceName":"1"}),"instanceName":"1"});
            var Q304;
            Q304=makeQuery(id+"F18.opPattern","COPY",BODY,{"derivedFrom":makeQuery(id+"F16.opPattern","COPY",BODY,{"derivedFrom":makeQuery(id+"F14.opPattern","COPY",BODY,{"derivedFrom":makeQuery(id+"F11.opPattern","COPY",BODY,{"derivedFrom":makeQuery(id+"F10.opPattern","COPY",BODY,{"derivedFrom":makeQuery(id+"F1.opExtrude","SWEPT_BODY",BODY,{"disambiguationData":[OSD([sQuery(id+"F0.wireOp",EDGE,"E0")])]}),"instanceName":"1"}),"instanceName":"1"}),"instanceName":"1"}),"instanceName":"1"}),"instanceName":"1"});
            var Q305;
            Q305=makeQuery(id+"F15.opPattern","COPY",BODY,{"derivedFrom":makeQuery(id+"F12.opPattern","COPY",BODY,{"derivedFrom":makeQuery(id+"F11.opPattern","COPY",BODY,{"derivedFrom":makeQuery(id+"F4.opPattern","COPY",BODY,{"derivedFrom":makeQuery(id+"F1.opExtrude","SWEPT_BODY",BODY,{"disambiguationData":[OSD([sQuery(id+"F0.wireOp",EDGE,"E0")])]}),"instanceName":"1"}),"instanceName":"1"}),"instanceName":"1"}),"instanceName":"1"});
            var Q306;
            Q306=makeQuery(id+"F18.opPattern","COPY",BODY,{"derivedFrom":makeQuery(id+"F16.opPattern","COPY",BODY,{"derivedFrom":makeQuery(id+"F12.opPattern","COPY",BODY,{"derivedFrom":makeQuery(id+"F11.opPattern","COPY",BODY,{"derivedFrom":makeQuery(id+"F4.opPattern","COPY",BODY,{"derivedFrom":makeQuery(id+"F1.opExtrude","SWEPT_BODY",BODY,{"disambiguationData":[OSD([sQuery(id+"F0.wireOp",EDGE,"E0")])]}),"instanceName":"1"}),"instanceName":"1"}),"instanceName":"1"}),"instanceName":"1"}),"instanceName":"1"});
            var Q307;
            Q307=makeQuery(id+"F18.opPattern","COPY",BODY,{"derivedFrom":makeQuery(id+"F16.opPattern","COPY",BODY,{"derivedFrom":makeQuery(id+"F11.opPattern","COPY",BODY,{"derivedFrom":makeQuery(id+"F4.opPattern","COPY",BODY,{"derivedFrom":makeQuery(id+"F1.opExtrude","SWEPT_BODY",BODY,{"disambiguationData":[OSD([sQuery(id+"F0.wireOp",EDGE,"E0")])]}),"instanceName":"1"}),"instanceName":"1"}),"instanceName":"1"}),"instanceName":"1"});
            var Q308;
            Q308=makeQuery(id+"F18.opPattern","COPY",BODY,{"derivedFrom":makeQuery(id+"F15.opPattern","COPY",BODY,{"derivedFrom":makeQuery(id+"F14.opPattern","COPY",BODY,{"derivedFrom":makeQuery(id+"F11.opPattern","COPY",BODY,{"derivedFrom":makeQuery(id+"F9.opPattern","COPY",BODY,{"derivedFrom":makeQuery(id+"F1.opExtrude","SWEPT_BODY",BODY,{"disambiguationData":[OSD([sQuery(id+"F0.wireOp",EDGE,"E0")])]}),"instanceName":"1"}),"instanceName":"1"}),"instanceName":"1"}),"instanceName":"1"}),"instanceName":"1"});
            var Q309;
            Q309=makeQuery(id+"F18.opPattern","COPY",BODY,{"derivedFrom":makeQuery(id+"F16.opPattern","COPY",BODY,{"derivedFrom":makeQuery(id+"F15.opPattern","COPY",BODY,{"derivedFrom":makeQuery(id+"F14.opPattern","COPY",BODY,{"derivedFrom":makeQuery(id+"F11.opPattern","COPY",BODY,{"derivedFrom":makeQuery(id+"F9.opPattern","COPY",BODY,{"derivedFrom":makeQuery(id+"F4.opPattern","COPY",BODY,{"derivedFrom":makeQuery(id+"F1.opExtrude","SWEPT_BODY",BODY,{"disambiguationData":[OSD([sQuery(id+"F0.wireOp",EDGE,"E0")])]}),"instanceName":"1"}),"instanceName":"1"}),"instanceName":"1"}),"instanceName":"1"}),"instanceName":"1"}),"instanceName":"1"}),"instanceName":"1"});
            var Q310;
            Q310=makeQuery(id+"F18.opPattern","COPY",BODY,{"derivedFrom":makeQuery(id+"F17.opPattern","COPY",BODY,{"derivedFrom":makeQuery(id+"F11.opPattern","COPY",BODY,{"derivedFrom":makeQuery(id+"F1.opExtrude","SWEPT_BODY",BODY,{"disambiguationData":[OSD([sQuery(id+"F0.wireOp",EDGE,"E0")])]}),"instanceName":"1"}),"instanceName":"1"}),"instanceName":"1"});
            var Q311;
            Q311=makeQuery(id+"F18.opPattern","COPY",BODY,{"derivedFrom":makeQuery(id+"F16.opPattern","COPY",BODY,{"derivedFrom":makeQuery(id+"F15.opPattern","COPY",BODY,{"derivedFrom":makeQuery(id+"F12.opPattern","COPY",BODY,{"derivedFrom":makeQuery(id+"F11.opPattern","COPY",BODY,{"derivedFrom":makeQuery(id+"F9.opPattern","COPY",BODY,{"derivedFrom":makeQuery(id+"F1.opExtrude","SWEPT_BODY",BODY,{"disambiguationData":[OSD([sQuery(id+"F0.wireOp",EDGE,"E0")])]}),"instanceName":"1"}),"instanceName":"1"}),"instanceName":"1"}),"instanceName":"1"}),"instanceName":"1"}),"instanceName":"1"});
            var Q312;
            Q312=makeQuery(id+"F18.opPattern","COPY",BODY,{"derivedFrom":makeQuery(id+"F17.opPattern","COPY",BODY,{"derivedFrom":makeQuery(id+"F11.opPattern","COPY",BODY,{"derivedFrom":makeQuery(id+"F9.opPattern","COPY",BODY,{"derivedFrom":makeQuery(id+"F4.opPattern","COPY",BODY,{"derivedFrom":makeQuery(id+"F1.opExtrude","SWEPT_BODY",BODY,{"disambiguationData":[OSD([sQuery(id+"F0.wireOp",EDGE,"E0")])]}),"instanceName":"1"}),"instanceName":"1"}),"instanceName":"1"}),"instanceName":"1"}),"instanceName":"1"});
            var Q313;
            Q313=makeQuery(id+"F18.opPattern","COPY",BODY,{"derivedFrom":makeQuery(id+"F15.opPattern","COPY",BODY,{"derivedFrom":makeQuery(id+"F12.opPattern","COPY",BODY,{"derivedFrom":makeQuery(id+"F11.opPattern","COPY",BODY,{"derivedFrom":makeQuery(id+"F4.opPattern","COPY",BODY,{"derivedFrom":makeQuery(id+"F1.opExtrude","SWEPT_BODY",BODY,{"disambiguationData":[OSD([sQuery(id+"F0.wireOp",EDGE,"E0")])]}),"instanceName":"1"}),"instanceName":"1"}),"instanceName":"1"}),"instanceName":"1"}),"instanceName":"1"});
            var Q314;
            Q314=makeQuery(id+"F18.opPattern","COPY",BODY,{"derivedFrom":makeQuery(id+"F15.opPattern","COPY",BODY,{"derivedFrom":makeQuery(id+"F9.opPattern","COPY",BODY,{"derivedFrom":makeQuery(id+"F1.opExtrude","SWEPT_BODY",BODY,{"disambiguationData":[OSD([sQuery(id+"F0.wireOp",EDGE,"E0")])]}),"instanceName":"1"}),"instanceName":"1"}),"instanceName":"1"});
            var Q315;
            Q315=makeQuery(id+"F16.opPattern","COPY",BODY,{"derivedFrom":makeQuery(id+"F15.opPattern","COPY",BODY,{"derivedFrom":makeQuery(id+"F14.opPattern","COPY",BODY,{"derivedFrom":makeQuery(id+"F1.opExtrude","SWEPT_BODY",BODY,{"disambiguationData":[OSD([sQuery(id+"F0.wireOp",EDGE,"E0")])]}),"instanceName":"1"}),"instanceName":"1"}),"instanceName":"1"});
            var Q316;
            Q316=makeQuery(id+"F15.opPattern","COPY",BODY,{"derivedFrom":makeQuery(id+"F12.opPattern","COPY",BODY,{"derivedFrom":makeQuery(id+"F11.opPattern","COPY",BODY,{"derivedFrom":makeQuery(id+"F9.opPattern","COPY",BODY,{"derivedFrom":makeQuery(id+"F4.opPattern","COPY",BODY,{"derivedFrom":makeQuery(id+"F1.opExtrude","SWEPT_BODY",BODY,{"disambiguationData":[OSD([sQuery(id+"F0.wireOp",EDGE,"E0")])]}),"instanceName":"1"}),"instanceName":"1"}),"instanceName":"1"}),"instanceName":"1"}),"instanceName":"1"});
            var Q317;
            Q317=makeQuery(id+"F15.opPattern","COPY",BODY,{"derivedFrom":makeQuery(id+"F14.opPattern","COPY",BODY,{"derivedFrom":makeQuery(id+"F1.opExtrude","SWEPT_BODY",BODY,{"disambiguationData":[OSD([sQuery(id+"F0.wireOp",EDGE,"E0")])]}),"instanceName":"1"}),"instanceName":"1"});
            var Q318;
            Q318=makeQuery(id+"F15.opPattern","COPY",BODY,{"derivedFrom":makeQuery(id+"F12.opPattern","COPY",BODY,{"derivedFrom":makeQuery(id+"F9.opPattern","COPY",BODY,{"derivedFrom":makeQuery(id+"F1.opExtrude","SWEPT_BODY",BODY,{"disambiguationData":[OSD([sQuery(id+"F0.wireOp",EDGE,"E0")])]}),"instanceName":"1"}),"instanceName":"1"}),"instanceName":"1"});
            var Q319;
            Q319=makeQuery(id+"F18.opPattern","COPY",BODY,{"derivedFrom":makeQuery(id+"F12.opPattern","COPY",BODY,{"derivedFrom":makeQuery(id+"F10.opPattern","COPY",BODY,{"derivedFrom":makeQuery(id+"F1.opExtrude","SWEPT_BODY",BODY,{"disambiguationData":[OSD([sQuery(id+"F0.wireOp",EDGE,"E0")])]}),"instanceName":"1"}),"instanceName":"1"}),"instanceName":"1"});
            var Q320;
            Q320=makeQuery(id+"F18.opPattern","COPY",BODY,{"derivedFrom":makeQuery(id+"F12.opPattern","COPY",BODY,{"derivedFrom":makeQuery(id+"F11.opPattern","COPY",BODY,{"derivedFrom":makeQuery(id+"F10.opPattern","COPY",BODY,{"derivedFrom":makeQuery(id+"F1.opExtrude","SWEPT_BODY",BODY,{"disambiguationData":[OSD([sQuery(id+"F0.wireOp",EDGE,"E0")])]}),"instanceName":"1"}),"instanceName":"1"}),"instanceName":"1"}),"instanceName":"1"});
            var Q321;
            Q321=makeQuery(id+"F18.opPattern","COPY",BODY,{"derivedFrom":makeQuery(id+"F11.opPattern","COPY",BODY,{"derivedFrom":makeQuery(id+"F1.opExtrude","SWEPT_BODY",BODY,{"disambiguationData":[OSD([sQuery(id+"F0.wireOp",EDGE,"E0")])]}),"instanceName":"1"}),"instanceName":"1"});
            var Q322;
            Q322=makeQuery(id+"F18.opPattern","COPY",BODY,{"derivedFrom":makeQuery(id+"F17.opPattern","COPY",BODY,{"derivedFrom":makeQuery(id+"F15.opPattern","COPY",BODY,{"derivedFrom":makeQuery(id+"F12.opPattern","COPY",BODY,{"derivedFrom":makeQuery(id+"F11.opPattern","COPY",BODY,{"derivedFrom":makeQuery(id+"F9.opPattern","COPY",BODY,{"derivedFrom":makeQuery(id+"F4.opPattern","COPY",BODY,{"derivedFrom":makeQuery(id+"F1.opExtrude","SWEPT_BODY",BODY,{"disambiguationData":[OSD([sQuery(id+"F0.wireOp",EDGE,"E0")])]}),"instanceName":"1"}),"instanceName":"1"}),"instanceName":"1"}),"instanceName":"1"}),"instanceName":"1"}),"instanceName":"1"}),"instanceName":"1"});
            var Q323;
            Q323=makeQuery(id+"F18.opPattern","COPY",BODY,{"derivedFrom":makeQuery(id+"F17.opPattern","COPY",BODY,{"derivedFrom":makeQuery(id+"F15.opPattern","COPY",BODY,{"derivedFrom":makeQuery(id+"F14.opPattern","COPY",BODY,{"derivedFrom":makeQuery(id+"F11.opPattern","COPY",BODY,{"derivedFrom":makeQuery(id+"F9.opPattern","COPY",BODY,{"derivedFrom":makeQuery(id+"F4.opPattern","COPY",BODY,{"derivedFrom":makeQuery(id+"F1.opExtrude","SWEPT_BODY",BODY,{"disambiguationData":[OSD([sQuery(id+"F0.wireOp",EDGE,"E0")])]}),"instanceName":"1"}),"instanceName":"1"}),"instanceName":"1"}),"instanceName":"1"}),"instanceName":"1"}),"instanceName":"1"}),"instanceName":"1"});
            var Q324;
            Q324=makeQuery(id+"F18.opPattern","COPY",BODY,{"derivedFrom":makeQuery(id+"F17.opPattern","COPY",BODY,{"derivedFrom":makeQuery(id+"F14.opPattern","COPY",BODY,{"derivedFrom":makeQuery(id+"F11.opPattern","COPY",BODY,{"derivedFrom":makeQuery(id+"F4.opPattern","COPY",BODY,{"derivedFrom":makeQuery(id+"F1.opExtrude","SWEPT_BODY",BODY,{"disambiguationData":[OSD([sQuery(id+"F0.wireOp",EDGE,"E0")])]}),"instanceName":"1"}),"instanceName":"1"}),"instanceName":"1"}),"instanceName":"1"}),"instanceName":"1"});
            var Q325;
            Q325=makeQuery(id+"F15.opPattern","COPY",BODY,{"derivedFrom":makeQuery(id+"F12.opPattern","COPY",BODY,{"derivedFrom":makeQuery(id+"F1.opExtrude","SWEPT_BODY",BODY,{"disambiguationData":[OSD([sQuery(id+"F0.wireOp",EDGE,"E0")])]}),"instanceName":"1"}),"instanceName":"1"});
            var Q326;
            Q326=makeQuery(id+"F15.opPattern","COPY",BODY,{"derivedFrom":makeQuery(id+"F12.opPattern","COPY",BODY,{"derivedFrom":makeQuery(id+"F9.opPattern","COPY",BODY,{"derivedFrom":makeQuery(id+"F4.opPattern","COPY",BODY,{"derivedFrom":makeQuery(id+"F1.opExtrude","SWEPT_BODY",BODY,{"disambiguationData":[OSD([sQuery(id+"F0.wireOp",EDGE,"E0")])]}),"instanceName":"1"}),"instanceName":"1"}),"instanceName":"1"}),"instanceName":"1"});
            var Q327;
            Q327=makeQuery(id+"F18.opPattern","COPY",BODY,{"derivedFrom":makeQuery(id+"F17.opPattern","COPY",BODY,{"derivedFrom":makeQuery(id+"F12.opPattern","COPY",BODY,{"derivedFrom":makeQuery(id+"F10.opPattern","COPY",BODY,{"derivedFrom":makeQuery(id+"F1.opExtrude","SWEPT_BODY",BODY,{"disambiguationData":[OSD([sQuery(id+"F0.wireOp",EDGE,"E0")])]}),"instanceName":"1"}),"instanceName":"1"}),"instanceName":"1"}),"instanceName":"1"});
            var Q328;
            Q328=makeQuery(id+"F18.opPattern","COPY",BODY,{"derivedFrom":makeQuery(id+"F15.opPattern","COPY",BODY,{"derivedFrom":makeQuery(id+"F12.opPattern","COPY",BODY,{"derivedFrom":makeQuery(id+"F11.opPattern","COPY",BODY,{"derivedFrom":makeQuery(id+"F1.opExtrude","SWEPT_BODY",BODY,{"disambiguationData":[OSD([sQuery(id+"F0.wireOp",EDGE,"E0")])]}),"instanceName":"1"}),"instanceName":"1"}),"instanceName":"1"}),"instanceName":"1"});
            var Q329;
            Q329=makeQuery(id+"F18.opPattern","COPY",BODY,{"derivedFrom":makeQuery(id+"F15.opPattern","COPY",BODY,{"derivedFrom":makeQuery(id+"F14.opPattern","COPY",BODY,{"derivedFrom":makeQuery(id+"F4.opPattern","COPY",BODY,{"derivedFrom":makeQuery(id+"F1.opExtrude","SWEPT_BODY",BODY,{"disambiguationData":[OSD([sQuery(id+"F0.wireOp",EDGE,"E0")])]}),"instanceName":"1"}),"instanceName":"1"}),"instanceName":"1"}),"instanceName":"1"});
            var Q330;
            Q330=makeQuery(id+"F18.opPattern","COPY",BODY,{"derivedFrom":makeQuery(id+"F17.opPattern","COPY",BODY,{"derivedFrom":makeQuery(id+"F15.opPattern","COPY",BODY,{"derivedFrom":makeQuery(id+"F9.opPattern","COPY",BODY,{"derivedFrom":makeQuery(id+"F1.opExtrude","SWEPT_BODY",BODY,{"disambiguationData":[OSD([sQuery(id+"F0.wireOp",EDGE,"E0")])]}),"instanceName":"1"}),"instanceName":"1"}),"instanceName":"1"}),"instanceName":"1"});
            var Q331;
            Q331=makeQuery(id+"F16.opPattern","COPY",BODY,{"derivedFrom":makeQuery(id+"F9.opPattern","COPY",BODY,{"derivedFrom":makeQuery(id+"F4.opPattern","COPY",BODY,{"derivedFrom":makeQuery(id+"F1.opExtrude","SWEPT_BODY",BODY,{"disambiguationData":[OSD([sQuery(id+"F0.wireOp",EDGE,"E0")])]}),"instanceName":"1"}),"instanceName":"1"}),"instanceName":"1"});
            var Q332;
            Q332=makeQuery(id+"F18.opPattern","COPY",BODY,{"derivedFrom":makeQuery(id+"F17.opPattern","COPY",BODY,{"derivedFrom":makeQuery(id+"F4.opPattern","COPY",BODY,{"derivedFrom":makeQuery(id+"F1.opExtrude","SWEPT_BODY",BODY,{"disambiguationData":[OSD([sQuery(id+"F0.wireOp",EDGE,"E0")])]}),"instanceName":"1"}),"instanceName":"1"}),"instanceName":"1"});
            var Q333;
            Q333=makeQuery(id+"F16.opPattern","COPY",BODY,{"derivedFrom":makeQuery(id+"F15.opPattern","COPY",BODY,{"derivedFrom":makeQuery(id+"F12.opPattern","COPY",BODY,{"derivedFrom":makeQuery(id+"F11.opPattern","COPY",BODY,{"derivedFrom":makeQuery(id+"F9.opPattern","COPY",BODY,{"derivedFrom":makeQuery(id+"F4.opPattern","COPY",BODY,{"derivedFrom":makeQuery(id+"F1.opExtrude","SWEPT_BODY",BODY,{"disambiguationData":[OSD([sQuery(id+"F0.wireOp",EDGE,"E0")])]}),"instanceName":"1"}),"instanceName":"1"}),"instanceName":"1"}),"instanceName":"1"}),"instanceName":"1"}),"instanceName":"1"});
            var Q334;
            Q334=makeQuery(id+"F18.opPattern","COPY",BODY,{"derivedFrom":makeQuery(id+"F16.opPattern","COPY",BODY,{"derivedFrom":makeQuery(id+"F15.opPattern","COPY",BODY,{"derivedFrom":makeQuery(id+"F12.opPattern","COPY",BODY,{"derivedFrom":makeQuery(id+"F9.opPattern","COPY",BODY,{"derivedFrom":makeQuery(id+"F4.opPattern","COPY",BODY,{"derivedFrom":makeQuery(id+"F1.opExtrude","SWEPT_BODY",BODY,{"disambiguationData":[OSD([sQuery(id+"F0.wireOp",EDGE,"E0")])]}),"instanceName":"1"}),"instanceName":"1"}),"instanceName":"1"}),"instanceName":"1"}),"instanceName":"1"}),"instanceName":"1"});
            var Q335;
            Q335=makeQuery(id+"F16.opPattern","COPY",BODY,{"derivedFrom":makeQuery(id+"F14.opPattern","COPY",BODY,{"derivedFrom":makeQuery(id+"F11.opPattern","COPY",BODY,{"derivedFrom":makeQuery(id+"F10.opPattern","COPY",BODY,{"derivedFrom":makeQuery(id+"F1.opExtrude","SWEPT_BODY",BODY,{"disambiguationData":[OSD([sQuery(id+"F0.wireOp",EDGE,"E0")])]}),"instanceName":"1"}),"instanceName":"1"}),"instanceName":"1"}),"instanceName":"1"});
            var Q336;
            Q336=makeQuery(id+"F18.opPattern","COPY",BODY,{"derivedFrom":makeQuery(id+"F16.opPattern","COPY",BODY,{"derivedFrom":makeQuery(id+"F15.opPattern","COPY",BODY,{"derivedFrom":makeQuery(id+"F11.opPattern","COPY",BODY,{"derivedFrom":makeQuery(id+"F9.opPattern","COPY",BODY,{"derivedFrom":makeQuery(id+"F1.opExtrude","SWEPT_BODY",BODY,{"disambiguationData":[OSD([sQuery(id+"F0.wireOp",EDGE,"E0")])]}),"instanceName":"1"}),"instanceName":"1"}),"instanceName":"1"}),"instanceName":"1"}),"instanceName":"1"});
            var Q337;
            Q337=makeQuery(id+"F15.opPattern","COPY",BODY,{"derivedFrom":makeQuery(id+"F10.opPattern","COPY",BODY,{"derivedFrom":makeQuery(id+"F1.opExtrude","SWEPT_BODY",BODY,{"disambiguationData":[OSD([sQuery(id+"F0.wireOp",EDGE,"E0")])]}),"instanceName":"1"}),"instanceName":"1"});
            var Q338;
            Q338=makeQuery(id+"F18.opPattern","COPY",BODY,{"derivedFrom":makeQuery(id+"F17.opPattern","COPY",BODY,{"derivedFrom":makeQuery(id+"F16.opPattern","COPY",BODY,{"derivedFrom":makeQuery(id+"F14.opPattern","COPY",BODY,{"derivedFrom":makeQuery(id+"F11.opPattern","COPY",BODY,{"derivedFrom":makeQuery(id+"F9.opPattern","COPY",BODY,{"derivedFrom":makeQuery(id+"F1.opExtrude","SWEPT_BODY",BODY,{"disambiguationData":[OSD([sQuery(id+"F0.wireOp",EDGE,"E0")])]}),"instanceName":"1"}),"instanceName":"1"}),"instanceName":"1"}),"instanceName":"1"}),"instanceName":"1"}),"instanceName":"1"});
            var Q339;
            Q339=makeQuery(id+"F18.opPattern","COPY",BODY,{"derivedFrom":makeQuery(id+"F16.opPattern","COPY",BODY,{"derivedFrom":makeQuery(id+"F12.opPattern","COPY",BODY,{"derivedFrom":makeQuery(id+"F11.opPattern","COPY",BODY,{"derivedFrom":makeQuery(id+"F9.opPattern","COPY",BODY,{"derivedFrom":makeQuery(id+"F4.opPattern","COPY",BODY,{"derivedFrom":makeQuery(id+"F1.opExtrude","SWEPT_BODY",BODY,{"disambiguationData":[OSD([sQuery(id+"F0.wireOp",EDGE,"E0")])]}),"instanceName":"1"}),"instanceName":"1"}),"instanceName":"1"}),"instanceName":"1"}),"instanceName":"1"}),"instanceName":"1"});
            var Q340;
            Q340=makeQuery(id+"F15.opPattern","COPY",BODY,{"derivedFrom":makeQuery(id+"F11.opPattern","COPY",BODY,{"derivedFrom":makeQuery(id+"F4.opPattern","COPY",BODY,{"derivedFrom":makeQuery(id+"F1.opExtrude","SWEPT_BODY",BODY,{"disambiguationData":[OSD([sQuery(id+"F0.wireOp",EDGE,"E0")])]}),"instanceName":"1"}),"instanceName":"1"}),"instanceName":"1"});
            var Q341;
            Q341=makeQuery(id+"F18.opPattern","COPY",BODY,{"derivedFrom":makeQuery(id+"F16.opPattern","COPY",BODY,{"derivedFrom":makeQuery(id+"F12.opPattern","COPY",BODY,{"derivedFrom":makeQuery(id+"F11.opPattern","COPY",BODY,{"derivedFrom":makeQuery(id+"F1.opExtrude","SWEPT_BODY",BODY,{"disambiguationData":[OSD([sQuery(id+"F0.wireOp",EDGE,"E0")])]}),"instanceName":"1"}),"instanceName":"1"}),"instanceName":"1"}),"instanceName":"1"});
            var Q342;
            Q342=makeQuery(id+"F15.opPattern","COPY",BODY,{"derivedFrom":makeQuery(id+"F14.opPattern","COPY",BODY,{"derivedFrom":makeQuery(id+"F4.opPattern","COPY",BODY,{"derivedFrom":makeQuery(id+"F1.opExtrude","SWEPT_BODY",BODY,{"disambiguationData":[OSD([sQuery(id+"F0.wireOp",EDGE,"E0")])]}),"instanceName":"1"}),"instanceName":"1"}),"instanceName":"1"});
            var Q343;
            Q343=makeQuery(id+"F18.opPattern","COPY",BODY,{"derivedFrom":makeQuery(id+"F15.opPattern","COPY",BODY,{"derivedFrom":makeQuery(id+"F11.opPattern","COPY",BODY,{"derivedFrom":makeQuery(id+"F10.opPattern","COPY",BODY,{"derivedFrom":makeQuery(id+"F1.opExtrude","SWEPT_BODY",BODY,{"disambiguationData":[OSD([sQuery(id+"F0.wireOp",EDGE,"E0")])]}),"instanceName":"1"}),"instanceName":"1"}),"instanceName":"1"}),"instanceName":"1"});
            var Q344;
            Q344=makeQuery(id+"F18.opPattern","COPY",BODY,{"derivedFrom":makeQuery(id+"F14.opPattern","COPY",BODY,{"derivedFrom":makeQuery(id+"F11.opPattern","COPY",BODY,{"derivedFrom":makeQuery(id+"F1.opExtrude","SWEPT_BODY",BODY,{"disambiguationData":[OSD([sQuery(id+"F0.wireOp",EDGE,"E0")])]}),"instanceName":"1"}),"instanceName":"1"}),"instanceName":"1"});
            var Q345;
            Q345=makeQuery(id+"F15.opPattern","COPY",BODY,{"derivedFrom":makeQuery(id+"F11.opPattern","COPY",BODY,{"derivedFrom":makeQuery(id+"F9.opPattern","COPY",BODY,{"derivedFrom":makeQuery(id+"F1.opExtrude","SWEPT_BODY",BODY,{"disambiguationData":[OSD([sQuery(id+"F0.wireOp",EDGE,"E0")])]}),"instanceName":"1"}),"instanceName":"1"}),"instanceName":"1"});
            var Q346;
            Q346=makeQuery(id+"F18.opPattern","COPY",BODY,{"derivedFrom":makeQuery(id+"F17.opPattern","COPY",BODY,{"derivedFrom":makeQuery(id+"F16.opPattern","COPY",BODY,{"derivedFrom":makeQuery(id+"F14.opPattern","COPY",BODY,{"derivedFrom":makeQuery(id+"F10.opPattern","COPY",BODY,{"derivedFrom":makeQuery(id+"F1.opExtrude","SWEPT_BODY",BODY,{"disambiguationData":[OSD([sQuery(id+"F0.wireOp",EDGE,"E0")])]}),"instanceName":"1"}),"instanceName":"1"}),"instanceName":"1"}),"instanceName":"1"}),"instanceName":"1"});
            var Q347;
            Q347=makeQuery(id+"F18.opPattern","COPY",BODY,{"derivedFrom":makeQuery(id+"F16.opPattern","COPY",BODY,{"derivedFrom":makeQuery(id+"F15.opPattern","COPY",BODY,{"derivedFrom":makeQuery(id+"F11.opPattern","COPY",BODY,{"derivedFrom":makeQuery(id+"F4.opPattern","COPY",BODY,{"derivedFrom":makeQuery(id+"F1.opExtrude","SWEPT_BODY",BODY,{"disambiguationData":[OSD([sQuery(id+"F0.wireOp",EDGE,"E0")])]}),"instanceName":"1"}),"instanceName":"1"}),"instanceName":"1"}),"instanceName":"1"}),"instanceName":"1"});
            var Q348;
            Q348=makeQuery(id+"F15.opPattern","COPY",BODY,{"derivedFrom":makeQuery(id+"F12.opPattern","COPY",BODY,{"derivedFrom":makeQuery(id+"F11.opPattern","COPY",BODY,{"derivedFrom":makeQuery(id+"F1.opExtrude","SWEPT_BODY",BODY,{"disambiguationData":[OSD([sQuery(id+"F0.wireOp",EDGE,"E0")])]}),"instanceName":"1"}),"instanceName":"1"}),"instanceName":"1"});
            var Q349;
            Q349=makeQuery(id+"F16.opPattern","COPY",BODY,{"derivedFrom":makeQuery(id+"F15.opPattern","COPY",BODY,{"derivedFrom":makeQuery(id+"F10.opPattern","COPY",BODY,{"derivedFrom":makeQuery(id+"F1.opExtrude","SWEPT_BODY",BODY,{"disambiguationData":[OSD([sQuery(id+"F0.wireOp",EDGE,"E0")])]}),"instanceName":"1"}),"instanceName":"1"}),"instanceName":"1"});
            var Q350;
            Q350=makeQuery(id+"F16.opPattern","COPY",BODY,{"derivedFrom":makeQuery(id+"F9.opPattern","COPY",BODY,{"derivedFrom":makeQuery(id+"F1.opExtrude","SWEPT_BODY",BODY,{"disambiguationData":[OSD([sQuery(id+"F0.wireOp",EDGE,"E0")])]}),"instanceName":"1"}),"instanceName":"1"});
            var Q351;
            Q351=makeQuery(id+"F18.opPattern","COPY",BODY,{"derivedFrom":makeQuery(id+"F17.opPattern","COPY",BODY,{"derivedFrom":makeQuery(id+"F14.opPattern","COPY",BODY,{"derivedFrom":makeQuery(id+"F11.opPattern","COPY",BODY,{"derivedFrom":makeQuery(id+"F1.opExtrude","SWEPT_BODY",BODY,{"disambiguationData":[OSD([sQuery(id+"F0.wireOp",EDGE,"E0")])]}),"instanceName":"1"}),"instanceName":"1"}),"instanceName":"1"}),"instanceName":"1"});
            var Q352;
            Q352=makeQuery(id+"F15.opPattern","COPY",BODY,{"derivedFrom":makeQuery(id+"F11.opPattern","COPY",BODY,{"derivedFrom":makeQuery(id+"F10.opPattern","COPY",BODY,{"derivedFrom":makeQuery(id+"F1.opExtrude","SWEPT_BODY",BODY,{"disambiguationData":[OSD([sQuery(id+"F0.wireOp",EDGE,"E0")])]}),"instanceName":"1"}),"instanceName":"1"}),"instanceName":"1"});
            var Q353;
            Q353=makeQuery(id+"F18.opPattern","COPY",BODY,{"derivedFrom":makeQuery(id+"F16.opPattern","COPY",BODY,{"derivedFrom":makeQuery(id+"F15.opPattern","COPY",BODY,{"derivedFrom":makeQuery(id+"F14.opPattern","COPY",BODY,{"derivedFrom":makeQuery(id+"F11.opPattern","COPY",BODY,{"derivedFrom":makeQuery(id+"F1.opExtrude","SWEPT_BODY",BODY,{"disambiguationData":[OSD([sQuery(id+"F0.wireOp",EDGE,"E0")])]}),"instanceName":"1"}),"instanceName":"1"}),"instanceName":"1"}),"instanceName":"1"}),"instanceName":"1"});
            var Q354;
            Q354=makeQuery(id+"F18.opPattern","COPY",BODY,{"derivedFrom":makeQuery(id+"F16.opPattern","COPY",BODY,{"derivedFrom":makeQuery(id+"F14.opPattern","COPY",BODY,{"derivedFrom":makeQuery(id+"F10.opPattern","COPY",BODY,{"derivedFrom":makeQuery(id+"F1.opExtrude","SWEPT_BODY",BODY,{"disambiguationData":[OSD([sQuery(id+"F0.wireOp",EDGE,"E0")])]}),"instanceName":"1"}),"instanceName":"1"}),"instanceName":"1"}),"instanceName":"1"});
            var Q355;
            Q355=makeQuery(id+"F15.opPattern","COPY",BODY,{"derivedFrom":makeQuery(id+"F12.opPattern","COPY",BODY,{"derivedFrom":makeQuery(id+"F11.opPattern","COPY",BODY,{"derivedFrom":makeQuery(id+"F10.opPattern","COPY",BODY,{"derivedFrom":makeQuery(id+"F1.opExtrude","SWEPT_BODY",BODY,{"disambiguationData":[OSD([sQuery(id+"F0.wireOp",EDGE,"E0")])]}),"instanceName":"1"}),"instanceName":"1"}),"instanceName":"1"}),"instanceName":"1"});
            var Q356;
            Q356=makeQuery(id+"F15.opPattern","COPY",BODY,{"derivedFrom":makeQuery(id+"F14.opPattern","COPY",BODY,{"derivedFrom":makeQuery(id+"F11.opPattern","COPY",BODY,{"derivedFrom":makeQuery(id+"F4.opPattern","COPY",BODY,{"derivedFrom":makeQuery(id+"F1.opExtrude","SWEPT_BODY",BODY,{"disambiguationData":[OSD([sQuery(id+"F0.wireOp",EDGE,"E0")])]}),"instanceName":"1"}),"instanceName":"1"}),"instanceName":"1"}),"instanceName":"1"});
            var Q357;
            Q357=makeQuery(id+"F15.opPattern","COPY",BODY,{"derivedFrom":makeQuery(id+"F11.opPattern","COPY",BODY,{"derivedFrom":makeQuery(id+"F9.opPattern","COPY",BODY,{"derivedFrom":makeQuery(id+"F4.opPattern","COPY",BODY,{"derivedFrom":makeQuery(id+"F1.opExtrude","SWEPT_BODY",BODY,{"disambiguationData":[OSD([sQuery(id+"F0.wireOp",EDGE,"E0")])]}),"instanceName":"1"}),"instanceName":"1"}),"instanceName":"1"}),"instanceName":"1"});
            var Q358;
            Q358=makeQuery(id+"F15.opPattern","COPY",BODY,{"derivedFrom":makeQuery(id+"F11.opPattern","COPY",BODY,{"derivedFrom":makeQuery(id+"F1.opExtrude","SWEPT_BODY",BODY,{"disambiguationData":[OSD([sQuery(id+"F0.wireOp",EDGE,"E0")])]}),"instanceName":"1"}),"instanceName":"1"});
            var Q359;
            Q359=makeQuery(id+"F16.opPattern","COPY",BODY,{"derivedFrom":makeQuery(id+"F15.opPattern","COPY",BODY,{"derivedFrom":makeQuery(id+"F14.opPattern","COPY",BODY,{"derivedFrom":makeQuery(id+"F10.opPattern","COPY",BODY,{"derivedFrom":makeQuery(id+"F1.opExtrude","SWEPT_BODY",BODY,{"disambiguationData":[OSD([sQuery(id+"F0.wireOp",EDGE,"E0")])]}),"instanceName":"1"}),"instanceName":"1"}),"instanceName":"1"}),"instanceName":"1"});
            var Q360;
            Q360=makeQuery(id+"F16.opPattern","COPY",BODY,{"derivedFrom":makeQuery(id+"F15.opPattern","COPY",BODY,{"derivedFrom":makeQuery(id+"F12.opPattern","COPY",BODY,{"derivedFrom":makeQuery(id+"F4.opPattern","COPY",BODY,{"derivedFrom":makeQuery(id+"F1.opExtrude","SWEPT_BODY",BODY,{"disambiguationData":[OSD([sQuery(id+"F0.wireOp",EDGE,"E0")])]}),"instanceName":"1"}),"instanceName":"1"}),"instanceName":"1"}),"instanceName":"1"});
            var Q361;
            Q361=makeQuery(id+"F18.opPattern","COPY",BODY,{"derivedFrom":makeQuery(id+"F15.opPattern","COPY",BODY,{"derivedFrom":makeQuery(id+"F14.opPattern","COPY",BODY,{"derivedFrom":makeQuery(id+"F1.opExtrude","SWEPT_BODY",BODY,{"disambiguationData":[OSD([sQuery(id+"F0.wireOp",EDGE,"E0")])]}),"instanceName":"1"}),"instanceName":"1"}),"instanceName":"1"});
            var Q362;
            Q362=makeQuery(id+"F18.opPattern","COPY",BODY,{"derivedFrom":makeQuery(id+"F17.opPattern","COPY",BODY,{"derivedFrom":makeQuery(id+"F1.opExtrude","SWEPT_BODY",BODY,{"disambiguationData":[OSD([sQuery(id+"F0.wireOp",EDGE,"E0")])]}),"instanceName":"1"}),"instanceName":"1"});
            var Q363;
            Q363=makeQuery(id+"F16.opPattern","COPY",BODY,{"derivedFrom":makeQuery(id+"F14.opPattern","COPY",BODY,{"derivedFrom":makeQuery(id+"F1.opExtrude","SWEPT_BODY",BODY,{"disambiguationData":[OSD([sQuery(id+"F0.wireOp",EDGE,"E0")])]}),"instanceName":"1"}),"instanceName":"1"});
            var Q364;
            Q364=makeQuery(id+"F18.opPattern","COPY",BODY,{"derivedFrom":makeQuery(id+"F16.opPattern","COPY",BODY,{"derivedFrom":makeQuery(id+"F15.opPattern","COPY",BODY,{"derivedFrom":makeQuery(id+"F12.opPattern","COPY",BODY,{"derivedFrom":makeQuery(id+"F9.opPattern","COPY",BODY,{"derivedFrom":makeQuery(id+"F1.opExtrude","SWEPT_BODY",BODY,{"disambiguationData":[OSD([sQuery(id+"F0.wireOp",EDGE,"E0")])]}),"instanceName":"1"}),"instanceName":"1"}),"instanceName":"1"}),"instanceName":"1"}),"instanceName":"1"});
            var Q365;
            Q365=makeQuery(id+"F18.opPattern","COPY",BODY,{"derivedFrom":makeQuery(id+"F9.opPattern","COPY",BODY,{"derivedFrom":makeQuery(id+"F4.opPattern","COPY",BODY,{"derivedFrom":makeQuery(id+"F1.opExtrude","SWEPT_BODY",BODY,{"disambiguationData":[OSD([sQuery(id+"F0.wireOp",EDGE,"E0")])]}),"instanceName":"1"}),"instanceName":"1"}),"instanceName":"1"});
            var Q366;
            Q366=makeQuery(id+"F18.opPattern","COPY",BODY,{"derivedFrom":makeQuery(id+"F17.opPattern","COPY",BODY,{"derivedFrom":makeQuery(id+"F9.opPattern","COPY",BODY,{"derivedFrom":makeQuery(id+"F4.opPattern","COPY",BODY,{"derivedFrom":makeQuery(id+"F1.opExtrude","SWEPT_BODY",BODY,{"disambiguationData":[OSD([sQuery(id+"F0.wireOp",EDGE,"E0")])]}),"instanceName":"1"}),"instanceName":"1"}),"instanceName":"1"}),"instanceName":"1"});
            var Q367;
            Q367=makeQuery(id+"F18.opPattern","COPY",BODY,{"derivedFrom":makeQuery(id+"F16.opPattern","COPY",BODY,{"derivedFrom":makeQuery(id+"F12.opPattern","COPY",BODY,{"derivedFrom":makeQuery(id+"F4.opPattern","COPY",BODY,{"derivedFrom":makeQuery(id+"F1.opExtrude","SWEPT_BODY",BODY,{"disambiguationData":[OSD([sQuery(id+"F0.wireOp",EDGE,"E0")])]}),"instanceName":"1"}),"instanceName":"1"}),"instanceName":"1"}),"instanceName":"1"});
            var Q368;
            Q368=makeQuery(id+"F18.opPattern","COPY",BODY,{"derivedFrom":makeQuery(id+"F17.opPattern","COPY",BODY,{"derivedFrom":makeQuery(id+"F14.opPattern","COPY",BODY,{"derivedFrom":makeQuery(id+"F11.opPattern","COPY",BODY,{"derivedFrom":makeQuery(id+"F10.opPattern","COPY",BODY,{"derivedFrom":makeQuery(id+"F1.opExtrude","SWEPT_BODY",BODY,{"disambiguationData":[OSD([sQuery(id+"F0.wireOp",EDGE,"E0")])]}),"instanceName":"1"}),"instanceName":"1"}),"instanceName":"1"}),"instanceName":"1"}),"instanceName":"1"});
            var Q369;
            Q369=makeQuery(id+"F15.opPattern","COPY",BODY,{"derivedFrom":makeQuery(id+"F12.opPattern","COPY",BODY,{"derivedFrom":makeQuery(id+"F10.opPattern","COPY",BODY,{"derivedFrom":makeQuery(id+"F1.opExtrude","SWEPT_BODY",BODY,{"disambiguationData":[OSD([sQuery(id+"F0.wireOp",EDGE,"E0")])]}),"instanceName":"1"}),"instanceName":"1"}),"instanceName":"1"});
            var Q370;
            Q370=makeQuery(id+"F18.opPattern","COPY",BODY,{"derivedFrom":makeQuery(id+"F14.opPattern","COPY",BODY,{"derivedFrom":makeQuery(id+"F11.opPattern","COPY",BODY,{"derivedFrom":makeQuery(id+"F10.opPattern","COPY",BODY,{"derivedFrom":makeQuery(id+"F1.opExtrude","SWEPT_BODY",BODY,{"disambiguationData":[OSD([sQuery(id+"F0.wireOp",EDGE,"E0")])]}),"instanceName":"1"}),"instanceName":"1"}),"instanceName":"1"}),"instanceName":"1"});
            var Q371;
            Q371=makeQuery(id+"F18.opPattern","COPY",BODY,{"derivedFrom":makeQuery(id+"F16.opPattern","COPY",BODY,{"derivedFrom":makeQuery(id+"F12.opPattern","COPY",BODY,{"derivedFrom":makeQuery(id+"F11.opPattern","COPY",BODY,{"derivedFrom":makeQuery(id+"F10.opPattern","COPY",BODY,{"derivedFrom":makeQuery(id+"F1.opExtrude","SWEPT_BODY",BODY,{"disambiguationData":[OSD([sQuery(id+"F0.wireOp",EDGE,"E0")])]}),"instanceName":"1"}),"instanceName":"1"}),"instanceName":"1"}),"instanceName":"1"}),"instanceName":"1"});
            var Q372;
            Q372=makeQuery(id+"F18.opPattern","COPY",BODY,{"derivedFrom":makeQuery(id+"F16.opPattern","COPY",BODY,{"derivedFrom":makeQuery(id+"F15.opPattern","COPY",BODY,{"derivedFrom":makeQuery(id+"F14.opPattern","COPY",BODY,{"derivedFrom":makeQuery(id+"F11.opPattern","COPY",BODY,{"derivedFrom":makeQuery(id+"F4.opPattern","COPY",BODY,{"derivedFrom":makeQuery(id+"F1.opExtrude","SWEPT_BODY",BODY,{"disambiguationData":[OSD([sQuery(id+"F0.wireOp",EDGE,"E0")])]}),"instanceName":"1"}),"instanceName":"1"}),"instanceName":"1"}),"instanceName":"1"}),"instanceName":"1"}),"instanceName":"1"});
            var Q373;
            Q373=makeQuery(id+"F18.opPattern","COPY",BODY,{"derivedFrom":makeQuery(id+"F16.opPattern","COPY",BODY,{"derivedFrom":makeQuery(id+"F15.opPattern","COPY",BODY,{"derivedFrom":makeQuery(id+"F12.opPattern","COPY",BODY,{"derivedFrom":makeQuery(id+"F11.opPattern","COPY",BODY,{"derivedFrom":makeQuery(id+"F10.opPattern","COPY",BODY,{"derivedFrom":makeQuery(id+"F1.opExtrude","SWEPT_BODY",BODY,{"disambiguationData":[OSD([sQuery(id+"F0.wireOp",EDGE,"E0")])]}),"instanceName":"1"}),"instanceName":"1"}),"instanceName":"1"}),"instanceName":"1"}),"instanceName":"1"}),"instanceName":"1"});
            var Q374;
            Q374=makeQuery(id+"F18.opPattern","COPY",BODY,{"derivedFrom":makeQuery(id+"F17.opPattern","COPY",BODY,{"derivedFrom":makeQuery(id+"F9.opPattern","COPY",BODY,{"derivedFrom":makeQuery(id+"F1.opExtrude","SWEPT_BODY",BODY,{"disambiguationData":[OSD([sQuery(id+"F0.wireOp",EDGE,"E0")])]}),"instanceName":"1"}),"instanceName":"1"}),"instanceName":"1"});
            var Q375;
            Q375=makeQuery(id+"F15.opPattern","COPY",BODY,{"derivedFrom":makeQuery(id+"F14.opPattern","COPY",BODY,{"derivedFrom":makeQuery(id+"F11.opPattern","COPY",BODY,{"derivedFrom":makeQuery(id+"F9.opPattern","COPY",BODY,{"derivedFrom":makeQuery(id+"F4.opPattern","COPY",BODY,{"derivedFrom":makeQuery(id+"F1.opExtrude","SWEPT_BODY",BODY,{"disambiguationData":[OSD([sQuery(id+"F0.wireOp",EDGE,"E0")])]}),"instanceName":"1"}),"instanceName":"1"}),"instanceName":"1"}),"instanceName":"1"}),"instanceName":"1"});
            var Q376;
            Q376=makeQuery(id+"F18.opPattern","COPY",BODY,{"derivedFrom":makeQuery(id+"F17.opPattern","COPY",BODY,{"derivedFrom":makeQuery(id+"F14.opPattern","COPY",BODY,{"derivedFrom":makeQuery(id+"F11.opPattern","COPY",BODY,{"derivedFrom":makeQuery(id+"F9.opPattern","COPY",BODY,{"derivedFrom":makeQuery(id+"F1.opExtrude","SWEPT_BODY",BODY,{"disambiguationData":[OSD([sQuery(id+"F0.wireOp",EDGE,"E0")])]}),"instanceName":"1"}),"instanceName":"1"}),"instanceName":"1"}),"instanceName":"1"}),"instanceName":"1"});
            var Q377;
            Q377=makeQuery(id+"F18.opPattern","COPY",BODY,{"derivedFrom":makeQuery(id+"F15.opPattern","COPY",BODY,{"derivedFrom":makeQuery(id+"F12.opPattern","COPY",BODY,{"derivedFrom":makeQuery(id+"F11.opPattern","COPY",BODY,{"derivedFrom":makeQuery(id+"F9.opPattern","COPY",BODY,{"derivedFrom":makeQuery(id+"F4.opPattern","COPY",BODY,{"derivedFrom":makeQuery(id+"F1.opExtrude","SWEPT_BODY",BODY,{"disambiguationData":[OSD([sQuery(id+"F0.wireOp",EDGE,"E0")])]}),"instanceName":"1"}),"instanceName":"1"}),"instanceName":"1"}),"instanceName":"1"}),"instanceName":"1"}),"instanceName":"1"});
            var Q378;
            Q378=makeQuery(id+"F15.opPattern","COPY",BODY,{"derivedFrom":makeQuery(id+"F14.opPattern","COPY",BODY,{"derivedFrom":makeQuery(id+"F11.opPattern","COPY",BODY,{"derivedFrom":makeQuery(id+"F1.opExtrude","SWEPT_BODY",BODY,{"disambiguationData":[OSD([sQuery(id+"F0.wireOp",EDGE,"E0")])]}),"instanceName":"1"}),"instanceName":"1"}),"instanceName":"1"});
            var Q379;
            Q379=makeQuery(id+"F18.opPattern","COPY",BODY,{"derivedFrom":makeQuery(id+"F15.opPattern","COPY",BODY,{"derivedFrom":makeQuery(id+"F10.opPattern","COPY",BODY,{"derivedFrom":makeQuery(id+"F1.opExtrude","SWEPT_BODY",BODY,{"disambiguationData":[OSD([sQuery(id+"F0.wireOp",EDGE,"E0")])]}),"instanceName":"1"}),"instanceName":"1"}),"instanceName":"1"});
            var Q380;
            Q380=makeQuery(id+"F18.opPattern","COPY",BODY,{"derivedFrom":makeQuery(id+"F14.opPattern","COPY",BODY,{"derivedFrom":makeQuery(id+"F4.opPattern","COPY",BODY,{"derivedFrom":makeQuery(id+"F1.opExtrude","SWEPT_BODY",BODY,{"disambiguationData":[OSD([sQuery(id+"F0.wireOp",EDGE,"E0")])]}),"instanceName":"1"}),"instanceName":"1"}),"instanceName":"1"});
            var Q381;
            Q381=makeQuery(id+"F18.opPattern","COPY",BODY,{"derivedFrom":makeQuery(id+"F9.opPattern","COPY",BODY,{"derivedFrom":makeQuery(id+"F1.opExtrude","SWEPT_BODY",BODY,{"disambiguationData":[OSD([sQuery(id+"F0.wireOp",EDGE,"E0")])]}),"instanceName":"1"}),"instanceName":"1"});
            var Q382;
            Q382=makeQuery(id+"F18.opPattern","COPY",BODY,{"derivedFrom":makeQuery(id+"F16.opPattern","COPY",BODY,{"derivedFrom":makeQuery(id+"F12.opPattern","COPY",BODY,{"derivedFrom":makeQuery(id+"F9.opPattern","COPY",BODY,{"derivedFrom":makeQuery(id+"F4.opPattern","COPY",BODY,{"derivedFrom":makeQuery(id+"F1.opExtrude","SWEPT_BODY",BODY,{"disambiguationData":[OSD([sQuery(id+"F0.wireOp",EDGE,"E0")])]}),"instanceName":"1"}),"instanceName":"1"}),"instanceName":"1"}),"instanceName":"1"}),"instanceName":"1"});
            var Q383;
            Q383=makeQuery(id+"F18.opPattern","COPY",BODY,{"derivedFrom":makeQuery(id+"F16.opPattern","COPY",BODY,{"derivedFrom":makeQuery(id+"F15.opPattern","COPY",BODY,{"derivedFrom":makeQuery(id+"F4.opPattern","COPY",BODY,{"derivedFrom":makeQuery(id+"F1.opExtrude","SWEPT_BODY",BODY,{"disambiguationData":[OSD([sQuery(id+"F0.wireOp",EDGE,"E0")])]}),"instanceName":"1"}),"instanceName":"1"}),"instanceName":"1"}),"instanceName":"1"});
            var Q384;
            Q384=makeQuery(id+"F18.opPattern","COPY",BODY,{"derivedFrom":makeQuery(id+"F16.opPattern","COPY",BODY,{"derivedFrom":makeQuery(id+"F12.opPattern","COPY",BODY,{"derivedFrom":makeQuery(id+"F1.opExtrude","SWEPT_BODY",BODY,{"disambiguationData":[OSD([sQuery(id+"F0.wireOp",EDGE,"E0")])]}),"instanceName":"1"}),"instanceName":"1"}),"instanceName":"1"});
            var Q385;
            Q385=makeQuery(id+"F18.opPattern","COPY",BODY,{"derivedFrom":makeQuery(id+"F17.opPattern","COPY",BODY,{"derivedFrom":makeQuery(id+"F15.opPattern","COPY",BODY,{"derivedFrom":makeQuery(id+"F10.opPattern","COPY",BODY,{"derivedFrom":makeQuery(id+"F1.opExtrude","SWEPT_BODY",BODY,{"disambiguationData":[OSD([sQuery(id+"F0.wireOp",EDGE,"E0")])]}),"instanceName":"1"}),"instanceName":"1"}),"instanceName":"1"}),"instanceName":"1"});
            var Q386;
            Q386=makeQuery(id+"F18.opPattern","COPY",BODY,{"derivedFrom":makeQuery(id+"F17.opPattern","COPY",BODY,{"derivedFrom":makeQuery(id+"F14.opPattern","COPY",BODY,{"derivedFrom":makeQuery(id+"F4.opPattern","COPY",BODY,{"derivedFrom":makeQuery(id+"F1.opExtrude","SWEPT_BODY",BODY,{"disambiguationData":[OSD([sQuery(id+"F0.wireOp",EDGE,"E0")])]}),"instanceName":"1"}),"instanceName":"1"}),"instanceName":"1"}),"instanceName":"1"});
            var Q387;
            Q387=makeQuery(id+"F14.opPattern","COPY",BODY,{"derivedFrom":makeQuery(id+"F11.opPattern","COPY",BODY,{"derivedFrom":makeQuery(id+"F4.opPattern","COPY",BODY,{"derivedFrom":makeQuery(id+"F1.opExtrude","SWEPT_BODY",BODY,{"disambiguationData":[OSD([sQuery(id+"F0.wireOp",EDGE,"E0")])]}),"instanceName":"1"}),"instanceName":"1"}),"instanceName":"1"});
            var Q388;
            Q388=makeQuery(id+"F18.opPattern","COPY",BODY,{"derivedFrom":makeQuery(id+"F16.opPattern","COPY",BODY,{"derivedFrom":makeQuery(id+"F15.opPattern","COPY",BODY,{"derivedFrom":makeQuery(id+"F12.opPattern","COPY",BODY,{"derivedFrom":makeQuery(id+"F10.opPattern","COPY",BODY,{"derivedFrom":makeQuery(id+"F1.opExtrude","SWEPT_BODY",BODY,{"disambiguationData":[OSD([sQuery(id+"F0.wireOp",EDGE,"E0")])]}),"instanceName":"1"}),"instanceName":"1"}),"instanceName":"1"}),"instanceName":"1"}),"instanceName":"1"});
            var Q389;
            Q389=makeQuery(id+"F14.opPattern","COPY",BODY,{"derivedFrom":makeQuery(id+"F11.opPattern","COPY",BODY,{"derivedFrom":makeQuery(id+"F10.opPattern","COPY",BODY,{"derivedFrom":makeQuery(id+"F1.opExtrude","SWEPT_BODY",BODY,{"disambiguationData":[OSD([sQuery(id+"F0.wireOp",EDGE,"E0")])]}),"instanceName":"1"}),"instanceName":"1"}),"instanceName":"1"});
            var Q390;
            Q390=makeQuery(id+"F18.opPattern","COPY",BODY,{"derivedFrom":makeQuery(id+"F16.opPattern","COPY",BODY,{"derivedFrom":makeQuery(id+"F15.opPattern","COPY",BODY,{"derivedFrom":makeQuery(id+"F9.opPattern","COPY",BODY,{"derivedFrom":makeQuery(id+"F4.opPattern","COPY",BODY,{"derivedFrom":makeQuery(id+"F1.opExtrude","SWEPT_BODY",BODY,{"disambiguationData":[OSD([sQuery(id+"F0.wireOp",EDGE,"E0")])]}),"instanceName":"1"}),"instanceName":"1"}),"instanceName":"1"}),"instanceName":"1"}),"instanceName":"1"});
            var Q391;
            Q391=makeQuery(id+"F15.opPattern","COPY",BODY,{"derivedFrom":makeQuery(id+"F9.opPattern","COPY",BODY,{"derivedFrom":makeQuery(id+"F4.opPattern","COPY",BODY,{"derivedFrom":makeQuery(id+"F1.opExtrude","SWEPT_BODY",BODY,{"disambiguationData":[OSD([sQuery(id+"F0.wireOp",EDGE,"E0")])]}),"instanceName":"1"}),"instanceName":"1"}),"instanceName":"1"});
            var Q392;
            Q392=makeQuery(id+"F18.opPattern","COPY",BODY,{"derivedFrom":makeQuery(id+"F15.opPattern","COPY",BODY,{"derivedFrom":makeQuery(id+"F14.opPattern","COPY",BODY,{"derivedFrom":makeQuery(id+"F10.opPattern","COPY",BODY,{"derivedFrom":makeQuery(id+"F1.opExtrude","SWEPT_BODY",BODY,{"disambiguationData":[OSD([sQuery(id+"F0.wireOp",EDGE,"E0")])]}),"instanceName":"1"}),"instanceName":"1"}),"instanceName":"1"}),"instanceName":"1"});
            var Q393;
            Q393=makeQuery(id+"F15.opPattern","COPY",BODY,{"derivedFrom":makeQuery(id+"F14.opPattern","COPY",BODY,{"derivedFrom":makeQuery(id+"F11.opPattern","COPY",BODY,{"derivedFrom":makeQuery(id+"F10.opPattern","COPY",BODY,{"derivedFrom":makeQuery(id+"F1.opExtrude","SWEPT_BODY",BODY,{"disambiguationData":[OSD([sQuery(id+"F0.wireOp",EDGE,"E0")])]}),"instanceName":"1"}),"instanceName":"1"}),"instanceName":"1"}),"instanceName":"1"});
            var Q394;
            Q394=makeQuery(id+"F15.opPattern","COPY",BODY,{"derivedFrom":makeQuery(id+"F14.opPattern","COPY",BODY,{"derivedFrom":makeQuery(id+"F11.opPattern","COPY",BODY,{"derivedFrom":makeQuery(id+"F9.opPattern","COPY",BODY,{"derivedFrom":makeQuery(id+"F1.opExtrude","SWEPT_BODY",BODY,{"disambiguationData":[OSD([sQuery(id+"F0.wireOp",EDGE,"E0")])]}),"instanceName":"1"}),"instanceName":"1"}),"instanceName":"1"}),"instanceName":"1"});
            var Q395;
            Q395=makeQuery(id+"F14.opPattern","COPY",BODY,{"derivedFrom":makeQuery(id+"F11.opPattern","COPY",BODY,{"derivedFrom":makeQuery(id+"F1.opExtrude","SWEPT_BODY",BODY,{"disambiguationData":[OSD([sQuery(id+"F0.wireOp",EDGE,"E0")])]}),"instanceName":"1"}),"instanceName":"1"});
            var Q396;
            Q396=makeQuery(id+"F14.opPattern","COPY",BODY,{"derivedFrom":makeQuery(id+"F11.opPattern","COPY",BODY,{"derivedFrom":makeQuery(id+"F9.opPattern","COPY",BODY,{"derivedFrom":makeQuery(id+"F4.opPattern","COPY",BODY,{"derivedFrom":makeQuery(id+"F1.opExtrude","SWEPT_BODY",BODY,{"disambiguationData":[OSD([sQuery(id+"F0.wireOp",EDGE,"E0")])]}),"instanceName":"1"}),"instanceName":"1"}),"instanceName":"1"}),"instanceName":"1"});
            var Q397;
            Q397=makeQuery(id+"F15.opPattern","COPY",BODY,{"derivedFrom":makeQuery(id+"F9.opPattern","COPY",BODY,{"derivedFrom":makeQuery(id+"F1.opExtrude","SWEPT_BODY",BODY,{"disambiguationData":[OSD([sQuery(id+"F0.wireOp",EDGE,"E0")])]}),"instanceName":"1"}),"instanceName":"1"});
            var Q398;
            Q398=makeQuery(id+"F14.opPattern","COPY",BODY,{"derivedFrom":makeQuery(id+"F11.opPattern","COPY",BODY,{"derivedFrom":makeQuery(id+"F9.opPattern","COPY",BODY,{"derivedFrom":makeQuery(id+"F1.opExtrude","SWEPT_BODY",BODY,{"disambiguationData":[OSD([sQuery(id+"F0.wireOp",EDGE,"E0")])]}),"instanceName":"1"}),"instanceName":"1"}),"instanceName":"1"});
            var Q399;
            Q399=makeQuery(id+"F14.opPattern","COPY",BODY,{"derivedFrom":makeQuery(id+"F10.opPattern","COPY",BODY,{"derivedFrom":makeQuery(id+"F1.opExtrude","SWEPT_BODY",BODY,{"disambiguationData":[OSD([sQuery(id+"F0.wireOp",EDGE,"E0")])]}),"instanceName":"1"}),"instanceName":"1"});
            var Q400;
            Q400=makeQuery(id+"F12.opPattern","COPY",BODY,{"derivedFrom":makeQuery(id+"F11.opPattern","COPY",BODY,{"derivedFrom":makeQuery(id+"F9.opPattern","COPY",BODY,{"derivedFrom":makeQuery(id+"F1.opExtrude","SWEPT_BODY",BODY,{"disambiguationData":[OSD([sQuery(id+"F0.wireOp",EDGE,"E0")])]}),"instanceName":"1"}),"instanceName":"1"}),"instanceName":"1"});
            var Q401;
            Q401=makeQuery(id+"F12.opPattern","COPY",BODY,{"derivedFrom":makeQuery(id+"F11.opPattern","COPY",BODY,{"derivedFrom":makeQuery(id+"F1.opExtrude","SWEPT_BODY",BODY,{"disambiguationData":[OSD([sQuery(id+"F0.wireOp",EDGE,"E0")])]}),"instanceName":"1"}),"instanceName":"1"});
            var Q402;
            Q402=makeQuery(id+"F18.opPattern","COPY",BODY,{"derivedFrom":makeQuery(id+"F4.opPattern","COPY",BODY,{"derivedFrom":makeQuery(id+"F1.opExtrude","SWEPT_BODY",BODY,{"disambiguationData":[OSD([sQuery(id+"F0.wireOp",EDGE,"E0")])]}),"instanceName":"1"}),"instanceName":"1"});
            var Q403;
            Q403=makeQuery(id+"F18.opPattern","COPY",BODY,{"derivedFrom":makeQuery(id+"F1.opExtrude","SWEPT_BODY",BODY,{"disambiguationData":[OSD([sQuery(id+"F0.wireOp",EDGE,"E0")])]}),"instanceName":"1"});
            var Q404;
            Q404=makeQuery(id+"F17.opPattern","COPY",BODY,{"derivedFrom":makeQuery(id+"F4.opPattern","COPY",BODY,{"derivedFrom":makeQuery(id+"F1.opExtrude","SWEPT_BODY",BODY,{"disambiguationData":[OSD([sQuery(id+"F0.wireOp",EDGE,"E0")])]}),"instanceName":"1"}),"instanceName":"1"});
            var Q405;
            Q405=makeQuery(id+"F17.opPattern","COPY",BODY,{"derivedFrom":makeQuery(id+"F1.opExtrude","SWEPT_BODY",BODY,{"disambiguationData":[OSD([sQuery(id+"F0.wireOp",EDGE,"E0")])]}),"instanceName":"1"});
            var Q406;
            Q406=makeQuery(id+"F16.opPattern","COPY",BODY,{"derivedFrom":makeQuery(id+"F4.opPattern","COPY",BODY,{"derivedFrom":makeQuery(id+"F1.opExtrude","SWEPT_BODY",BODY,{"disambiguationData":[OSD([sQuery(id+"F0.wireOp",EDGE,"E0")])]}),"instanceName":"1"}),"instanceName":"1"});
            var Q407;
            Q407=makeQuery(id+"F16.opPattern","COPY",BODY,{"derivedFrom":makeQuery(id+"F1.opExtrude","SWEPT_BODY",BODY,{"disambiguationData":[OSD([sQuery(id+"F0.wireOp",EDGE,"E0")])]}),"instanceName":"1"});
            var Q408;
            Q408=makeQuery(id+"F15.opPattern","COPY",BODY,{"derivedFrom":makeQuery(id+"F1.opExtrude","SWEPT_BODY",BODY,{"disambiguationData":[OSD([sQuery(id+"F0.wireOp",EDGE,"E0")])]}),"instanceName":"1"});
            var Q409;
            Q409=makeQuery(id+"F14.opPattern","COPY",BODY,{"derivedFrom":makeQuery(id+"F4.opPattern","COPY",BODY,{"derivedFrom":makeQuery(id+"F1.opExtrude","SWEPT_BODY",BODY,{"disambiguationData":[OSD([sQuery(id+"F0.wireOp",EDGE,"E0")])]}),"instanceName":"1"}),"instanceName":"1"});
            var Q410;
            Q410=makeQuery(id+"F14.opPattern","COPY",BODY,{"derivedFrom":makeQuery(id+"F1.opExtrude","SWEPT_BODY",BODY,{"disambiguationData":[OSD([sQuery(id+"F0.wireOp",EDGE,"E0")])]}),"instanceName":"1"});
            var Q411;
            Q411=makeQuery(id+"F12.opPattern","COPY",BODY,{"derivedFrom":makeQuery(id+"F4.opPattern","COPY",BODY,{"derivedFrom":makeQuery(id+"F1.opExtrude","SWEPT_BODY",BODY,{"disambiguationData":[OSD([sQuery(id+"F0.wireOp",EDGE,"E0")])]}),"instanceName":"1"}),"instanceName":"1"});
            var Q412;
            Q412=makeQuery(id+"F12.opPattern","COPY",BODY,{"derivedFrom":makeQuery(id+"F1.opExtrude","SWEPT_BODY",BODY,{"disambiguationData":[OSD([sQuery(id+"F0.wireOp",EDGE,"E0")])]}),"instanceName":"1"});
            var Q413;
            Q413=makeQuery(id+"F11.opPattern","COPY",BODY,{"derivedFrom":makeQuery(id+"F4.opPattern","COPY",BODY,{"derivedFrom":makeQuery(id+"F1.opExtrude","SWEPT_BODY",BODY,{"disambiguationData":[OSD([sQuery(id+"F0.wireOp",EDGE,"E0")])]}),"instanceName":"1"}),"instanceName":"1"});
            var Q414;
            Q414=makeQuery(id+"F11.opPattern","COPY",BODY,{"derivedFrom":makeQuery(id+"F1.opExtrude","SWEPT_BODY",BODY,{"disambiguationData":[OSD([sQuery(id+"F0.wireOp",EDGE,"E0")])]}),"instanceName":"1"});
            var Q415;
            Q415=makeQuery(id+"F10.opPattern","COPY",BODY,{"derivedFrom":makeQuery(id+"F1.opExtrude","SWEPT_BODY",BODY,{"disambiguationData":[OSD([sQuery(id+"F0.wireOp",EDGE,"E0")])]}),"instanceName":"1"});
            var Q416;
            Q416=makeQuery(id+"F1.opExtrude","SWEPT_BODY",BODY,{"disambiguationData":[OSD([sQuery(id+"F0.wireOp",EDGE,"E0")])]});
            var Q417;
            Q417=makeQuery(id+"F9.opPattern","COPY",BODY,{"derivedFrom":makeQuery(id+"F4.opPattern","COPY",BODY,{"derivedFrom":makeQuery(id+"F1.opExtrude","SWEPT_BODY",BODY,{"disambiguationData":[OSD([sQuery(id+"F0.wireOp",EDGE,"E0")])]}),"instanceName":"1"}),"instanceName":"1"});
            var Q418;
            Q418=makeQuery(id+"F15.opPattern","COPY",BODY,{"derivedFrom":makeQuery(id+"F4.opPattern","COPY",BODY,{"derivedFrom":makeQuery(id+"F1.opExtrude","SWEPT_BODY",BODY,{"disambiguationData":[OSD([sQuery(id+"F0.wireOp",EDGE,"E0")])]}),"instanceName":"1"}),"instanceName":"1"});
            var Q419;
            Q419=makeQuery(id+"F4.opPattern","COPY",BODY,{"derivedFrom":makeQuery(id+"F1.opExtrude","SWEPT_BODY",BODY,{"disambiguationData":[OSD([sQuery(id+"F0.wireOp",EDGE,"E0")])]}),"instanceName":"1"});
            transform(context, id + "F20", {"entities" : qUnion([Q0, Q1, Q2, Q3, Q4, Q5, Q6, Q7, Q8, Q9, Q10, Q11, Q12, Q13, Q14, Q15, Q16, Q17, Q18, Q19, Q20, Q21, Q22, Q23, Q24, Q25, Q26, Q27, Q28, Q29, Q30, Q31, Q32, Q33, Q34, Q35, Q36, Q37, Q38, Q39, Q40, Q41, Q42, Q43, Q44, Q45, Q46, Q47, Q48, Q49, Q50, Q51, Q52, Q53, Q54, Q55, Q56, Q57, Q58, Q59, Q60, Q61, Q62, Q63, Q64, Q65, Q66, Q67, Q68, Q69, Q70, Q71, Q72, Q73, Q74, Q75, Q76, Q77, Q78, Q79, Q80, Q81, Q82, Q83, Q84, Q85, Q86, Q87, Q88, Q89, Q90, Q91, Q92, Q93, Q94, Q95, Q96, Q97, Q98, Q99, Q100, Q101, Q102, Q103, Q104, Q105, Q106, Q107, Q108, Q109, Q110, Q111, Q112, Q113, Q114, Q115, Q116, Q117, Q118, Q119, Q120, Q121, Q122, Q123, Q124, Q125, Q126, Q127, Q128, Q129, Q130, Q131, Q132, Q133, Q134, Q135, Q136, Q137, Q138, Q139, Q140, Q141, Q142, Q143, Q144, Q145, Q146, Q147, Q148, Q149, Q150, Q151, Q152, Q153, Q154, Q155, Q156, Q157, Q158, Q159, Q160, Q161, Q162, Q163, Q164, Q165, Q166, Q167, Q168, Q169, Q170, Q171, Q172, Q173, Q174, Q175, Q176, Q177, Q178, Q179, Q180, Q181, Q182, Q183, Q184, Q185, Q186, Q187, Q188, Q189, Q190, Q191, Q192, Q193, Q194, Q195, Q196, Q197, Q198, Q199, Q200, Q201, Q202, Q203, Q204, Q205, Q206, Q207, Q208, Q209, Q210, Q211, Q212, Q213, Q214, Q215, Q216, Q217, Q218, Q219, Q220, Q221, Q222, Q223, Q224, Q225, Q226, Q227, Q228, Q229, Q230, Q231, Q232, Q233, Q234, Q235, Q236, Q237, Q238, Q239, Q240, Q241, Q242, Q243, Q244, Q245, Q246, Q247, Q248, Q249, Q250, Q251, Q252, Q253, Q254, Q255, Q256, Q257, Q258, Q259, Q260, Q261, Q262, Q263, Q264, Q265, Q266, Q267, Q268, Q269, Q270, Q271, Q272, Q273, Q274, Q275, Q276, Q277, Q278, Q279, Q280, Q281, Q282, Q283, Q284, Q285, Q286, Q287, Q288, Q289, Q290, Q291, Q292, Q293, Q294, Q295, Q296, Q297, Q298, Q299, Q300, Q301, Q302, Q303, Q304, Q305, Q306, Q307, Q308, Q309, Q310, Q311, Q312, Q313, Q314, Q315, Q316, Q317, Q318, Q319, Q320, Q321, Q322, Q323, Q324, Q325, Q326, Q327, Q328, Q329, Q330, Q331, Q332, Q333, Q334, Q335, Q336, Q337, Q338, Q339, Q340, Q341, Q342, Q343, Q344, Q345, Q346, Q347, Q348, Q349, Q350, Q351, Q352, Q353, Q354, Q355, Q356, Q357, Q358, Q359, Q360, Q361, Q362, Q363, Q364, Q365, Q366, Q367, Q368, Q369, Q370, Q371, Q372, Q373, Q374, Q375, Q376, Q377, Q378, Q379, Q380, Q381, Q382, Q383, Q384, Q385, Q386, Q387, Q388, Q389, Q390, Q391, Q392, Q393, Q394, Q395, Q396, Q397, Q398, Q399, Q400, Q401, Q402, Q403, Q404, Q405, Q406, Q407, Q408, Q409, Q410, Q411, Q412, Q413, Q414, Q415, Q416, Q417, Q418, Q419]), "transformType" : TransformType.TRANSLATION_3D, "dx" : 10.25 * mm, "dy" : 0 * mm, "dz" : 0 * mm, "makeCopy" : false});
        }
    });
